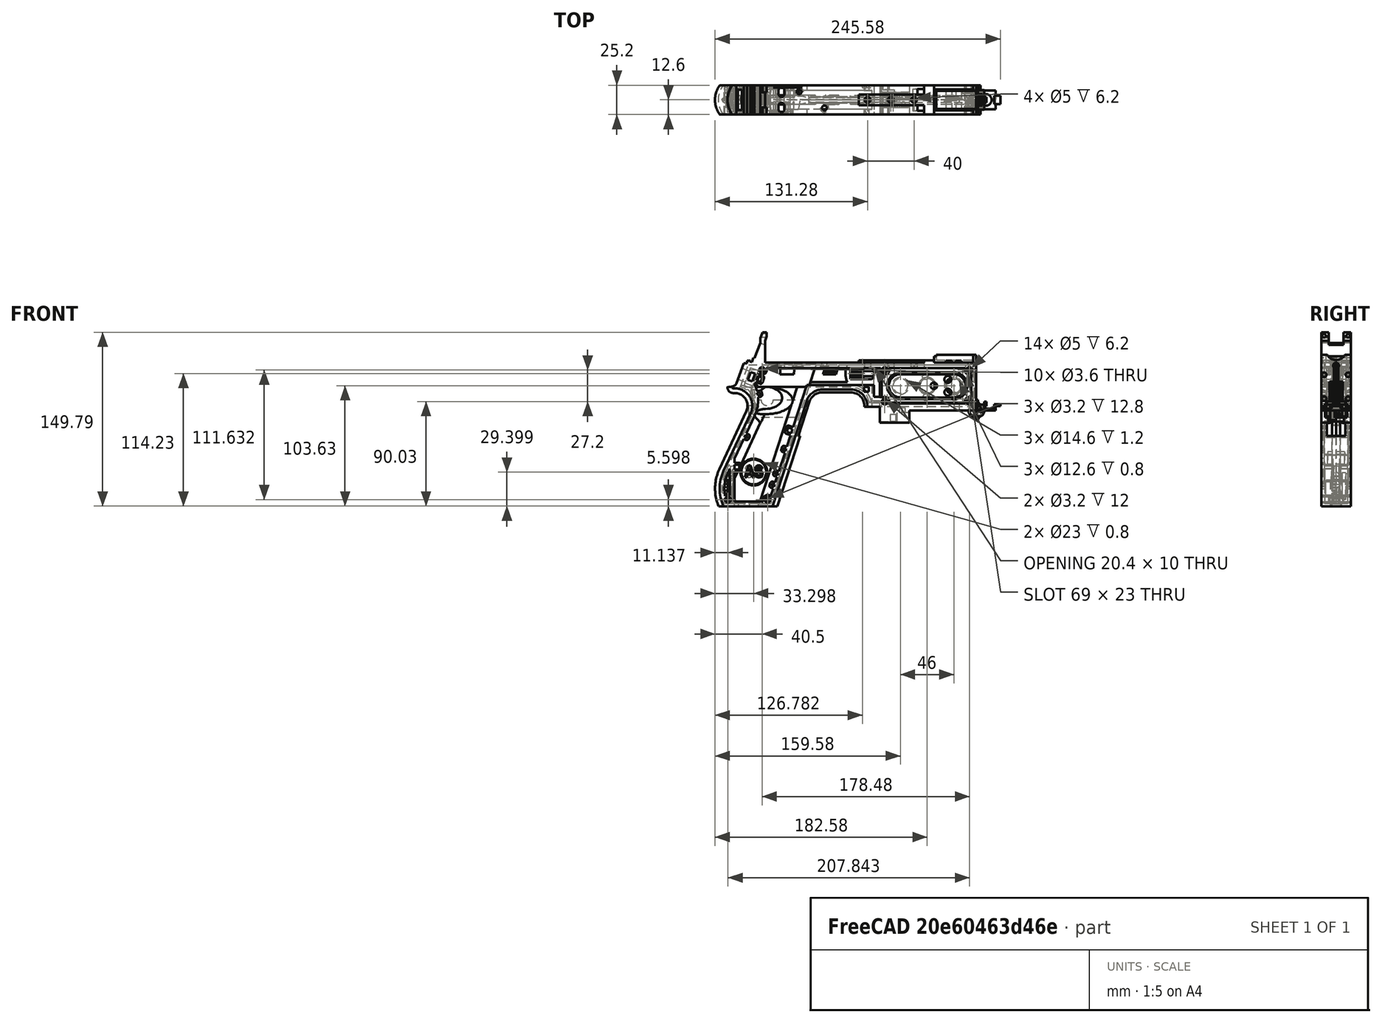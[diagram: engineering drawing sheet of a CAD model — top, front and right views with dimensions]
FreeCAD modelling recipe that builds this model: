
FCSTD DOCUMENT  (FreeCAD 1.0R39319 (Git))
Label: PICON-OF_ver_64
License: All rights reserved
LicenseURL: https://en.wikipedia.org/wiki/All_rights_reserved
objects: Sketcher::SketchObject×132, Part::Extrusion×66, Part::Cut×51, PartDesign::Pad×34, PartDesign::Pocket×21, PartDesign::Chamfer×15, PartDesign::Body×11, PartDesign::Fillet×6, Part::MultiFuse×5, Part::Part2DObjectPython×4, PartDesign::SubtractivePipe×4, PartDesign::SubtractiveLoft×4, PartDesign::Plane×3, PartDesign::SubShapeBinder×2, Part::Sweep×1, PartDesign::ShapeBinder×1, Mesh::Feature×1, PartDesign::Point×1, PartDesign::Groove×1
note: 664 computed .brp shape members not serialized (recipe doc carries the construction recipe); baked Part::Feature solids carry a one-line shape summary decoded from their .brp

FEATURE [Sketcher::SketchObject] Sketch  label="corpo principale"
  ArcFitTolerance = 1e-06
  AttacherType = Attacher::AttachEngine3D
  AttachmentSupport = -> [XZ_Plane]
  FullyConstrained = true
  MakeInternals = false
  MapMode = 5
  Placement = pos=(0,0,0) rot=(1,0,0;1.5708rad)
  sketch-geometry (65):
    g0: LineSegment StartX=0 StartY=0 StartZ=0 EndX=-57.2 EndY=0 EndZ=0
    g1: LineSegment StartX=-57.2 StartY=0 StartZ=0 EndX=-57.2 EndY=-10.4 EndZ=0
    g2: LineSegment StartX=-57.2 StartY=-10.4 StartZ=0 EndX=-82.8 EndY=-10.4 EndZ=0
    g3: LineSegment StartX=-82.8 StartY=-10.4 StartZ=0 EndX=-82.8 EndY=3.2 EndZ=0
    g4: LineSegment StartX=-82.8 StartY=3.2 StartZ=0 EndX=-93.6 EndY=3.2 EndZ=0
    g5: LineSegment StartX=-93.6 StartY=3.2 StartZ=0 EndX=-93.6 EndY=4 EndZ=0
    g6: LineSegment StartX=-107.6 StartY=18 StartZ=0 EndX=-132.428 EndY=18 EndZ=0
    g7: LineSegment StartX=-145.743 StartY=8.32624 StartZ=0 EndX=-175.232 EndY=-82.4316 EndZ=0
    g8: LineSegment StartX=-175.232 StartY=-82.4316 StartZ=0 EndX=-217.232 EndY=-82.4316 EndZ=0
    g9: LineSegment StartX=-217.232 StartY=-52.1862 StartZ=0 EndX=-193.988 EndY=-2.33927 EndZ=0
    g10: LineSegment StartX=-206.196 StartY=23.0857 StartZ=0 EndX=-199.861 EndY=40.4914 EndZ=0
    g11: LineSegment StartX=-199.861 StartY=40.4914 StartZ=0 EndX=-197.061 EndY=40.4914 EndZ=0
    g12: LineSegment StartX=-197.061 StartY=40.4914 StartZ=0 EndX=-197.061 EndY=42.8914 EndZ=0
    g13: LineSegment StartX=-197.061 StartY=42.8914 StartZ=0 EndX=-194.261 EndY=42.8914 EndZ=0
    g14: LineSegment StartX=-194.261 StartY=42.8914 StartZ=0 EndX=-194.535 EndY=42.1397 EndZ=0
    g15: LineSegment StartX=-194.535 StartY=42.1397 StartZ=0 EndX=-193.031 EndY=41.5924 EndZ=0
    g16: LineSegment StartX=-193.031 StartY=41.5924 StartZ=0 EndX=-191.663 EndY=45.3512 EndZ=0
    g17: LineSegment StartX=-191.663 StartY=45.3512 StartZ=0 EndX=-190.536 EndY=44.9408 EndZ=0
    g18: LineSegment StartX=-190.536 StartY=44.9408 StartZ=0 EndX=-185.747 EndY=58.0965 EndZ=0
    g19: LineSegment StartX=-185.747 StartY=58.0965 StartZ=0 EndX=-185.747 EndY=62.0965 EndZ=0
    g20: LineSegment StartX=-185.747 StartY=62.0965 StartZ=0 EndX=-183.832 EndY=67.3588 EndZ=0
    g21: LineSegment StartX=-183.832 StartY=67.3588 StartZ=0 EndX=-180.232 EndY=67.3588 EndZ=0
    g22: LineSegment StartX=-180.232 StartY=67.3588 StartZ=0 EndX=-180.232 EndY=63.7588 EndZ=0
    g23: LineSegment StartX=-180.232 StartY=63.7588 StartZ=0 EndX=-181.6 EndY=60 EndZ=0
    g24: LineSegment StartX=-181.6 StartY=60 StartZ=0 EndX=-181.6 EndY=41.2 EndZ=0
    g25: LineSegment StartX=-181.6 StartY=41.2 StartZ=0 EndX=-100.8 EndY=41.2 EndZ=0
    g26: LineSegment StartX=-36 StartY=43.2 StartZ=0 EndX=-36 EndY=41.2 EndZ=0
    g27: LineSegment StartX=0 StartY=48 StartZ=0 EndX=0 EndY=0 EndZ=0
    g28: LineSegment StartX=-209.901 StartY=19.85 StartZ=0 EndX=-209.901 EndY=20.1 EndZ=0
    g29: LineSegment StartX=-208.001 StartY=22 StartZ=0 EndX=-207.747 EndY=22 EndZ=0
    g30: LineSegment StartX=-207.583 StartY=19 StartZ=0 EndX=-209.051 EndY=19 EndZ=0
    g31: ArcOfCircle CenterX=-208.001 CenterY=20.1 CenterZ=0 NormalX=0 NormalY=0 NormalZ=1 AngleXU=0 Radius=1.9 StartAngle=1.5708 EndAngle=3.14159
    g32: GeomPoint [constr] X=-209.901 Y=22 Z=0
    g33: ArcOfCircle CenterX=-209.051 CenterY=19.85 CenterZ=0 NormalX=0 NormalY=0 NormalZ=1 AngleXU=0 Radius=0.85 StartAngle=3.14159 EndAngle=4.71239
    g34: GeomPoint [constr] X=-209.901 Y=19 Z=0
    g35: ArcOfCircle CenterX=-207.747 CenterY=23.65 CenterZ=0 NormalX=0 NormalY=0 NormalZ=1 AngleXU=0 Radius=1.65 StartAngle=4.71239 EndAngle=5.93412
    g36: GeomPoint [constr] X=-206.591 Y=22 Z=0
    g37: LineSegment StartX=-4 StartY=6 StartZ=0 EndX=-4 EndY=36.4 EndZ=0
    g38: LineSegment StartX=-4 StartY=36.4 StartZ=0 EndX=-185.2 EndY=36.4 EndZ=0
    g39: LineSegment StartX=-185.2 StartY=36.4 StartZ=0 EndX=-190.441 EndY=22 EndZ=0
    g40: LineSegment StartX=-214.575 StartY=-78.4316 StartZ=0 EndX=-178.142 EndY=-78.4316 EndZ=0
    g41: LineSegment StartX=-178.142 StartY=-78.4316 StartZ=0 EndX=-145.51 EndY=22 EndZ=0
    g42: LineSegment StartX=-145.51 StartY=22 StartZ=0 EndX=-87.91 EndY=22 EndZ=0
    g43: LineSegment StartX=-87.91 StartY=22 StartZ=0 EndX=-87.91 EndY=11.6 EndZ=0
    g44: LineSegment StartX=-87.91 StartY=11.6 StartZ=0 EndX=-80.11 EndY=11.6 EndZ=0
    g45: LineSegment StartX=-80.11 StartY=11.6 StartZ=0 EndX=-80.11 EndY=6 EndZ=0
    g46: LineSegment StartX=-80.11 StartY=6 StartZ=0 EndX=-4 EndY=6 EndZ=0
    g47: LineSegment StartX=-190.363 StartY=-4.02975 StartZ=0 EndX=-213.607 EndY=-53.8767 EndZ=0
    g48: ArcOfCircle CenterX=-132.428 CenterY=4 CenterZ=0 NormalX=0 NormalY=0 NormalZ=1 AngleXU=0 Radius=14 StartAngle=1.5708 EndAngle=2.82743
    g49: GeomPoint [constr] X=-142.6 Y=18 Z=0
    g50: ArcOfCircle CenterX=-107.6 CenterY=4 CenterZ=0 NormalX=0 NormalY=0 NormalZ=1 AngleXU=0 Radius=14 StartAngle=0 EndAngle=1.5708
    g51: GeomPoint [constr] X=-93.6 Y=18 Z=0
    g52: ArcOfCircle CenterX=-184.801 CenterY=-67.3089 CenterZ=0 NormalX=0 NormalY=0 NormalZ=1 AngleXU=0 Radius=35.7833 StartAngle=2.70526 EndAngle=3.57792
    g53: ArcOfCircle CenterX=-207.583 CenterY=4 CenterZ=0 NormalX=0 NormalY=0 NormalZ=1 AngleXU=0 Radius=15 StartAngle=5.84685 EndAngle=7.85398
    g54: LineSegment [constr] StartX=-213.607 StartY=-53.8767 StartZ=0 EndX=-217.232 EndY=-52.1862 EndZ=0
    g55: ArcOfCircle CenterX=-184.801 CenterY=-67.3089 CenterZ=0 NormalX=0 NormalY=0 NormalZ=1 AngleXU=0 Radius=31.7833 StartAngle=2.70526 EndAngle=3.49911
    g56: ArcOfCircle CenterX=-218.095 CenterY=8.90192 CenterZ=0 NormalX=0 NormalY=0 NormalZ=1 AngleXU=0 Radius=30.5989 StartAngle=5.84685 EndAngle=6.72553
    g57: LineSegment StartX=-44.6 StartY=43.2 StartZ=0 EndX=-36 EndY=43.2 EndZ=0
    g58: LineSegment StartX=-100.8 StartY=41.2 StartZ=0 EndX=-44.6 EndY=41.2 EndZ=0
    g59: LineSegment StartX=-44.6 StartY=41.2 StartZ=0 EndX=-44.6 EndY=43.2 EndZ=0
    g60: LineSegment StartX=-2.4 StartY=48 StartZ=0 EndX=0 EndY=48 EndZ=0
    g61: LineSegment StartX=-36 StartY=41.2 StartZ=0 EndX=-2.4 EndY=41.2 EndZ=0
    g62: LineSegment StartX=-2.4 StartY=41.2 StartZ=0 EndX=-2.4 EndY=48 EndZ=0
    g63: LineSegment [constr] StartX=-181.6 StartY=36.4 StartZ=0 EndX=-152.209 EndY=36.4 EndZ=0
    g64: LineSegment [constr] StartX=-181.6 StartY=36.4 StartZ=0 EndX=-130.41 EndY=36.4 EndZ=0
  constraints (183):
    c: Coincident(g-1,g0)
    c: PointOnObject(g0,g-1)
    c: Coincident(g0,g1)
    c: Vertical(g1)
    c: Coincident(g1,g2)
    c: Horizontal(g2)
    c: Coincident(g2,g3)
    c: Vertical(g3)
    c: Coincident(g3,g4)
    c: Coincident(g4,g5)
    c: Vertical(g5)
    c: Horizontal(g6)
    c: Coincident(g7,g8)
    c: Horizontal(g8)
    c: Coincident(g10,g11)
    c: Horizontal(g11)
    c: Coincident(g11,g12)
    c: Vertical(g12)
    c: Coincident(g12,g13)
    c: Horizontal(g13)
    c: Coincident(g13,g14)
    c: Coincident(g14,g15)
    c: Coincident(g15,g16)
    c: Coincident(g16,g17)
    c: Coincident(g17,g18)
    c: Coincident(g18,g19)
    c: Vertical(g19)
    c: Coincident(g19,g20)
    c: Coincident(g20,g21)
    c: Horizontal(g21)
    c: Coincident(g21,g22)
    c: Vertical(g22)
    c: Coincident(g22,g23)
    c: Coincident(g23,g24)
    c: Vertical(g24)
    c: Coincident(g24,g25)
    c: Horizontal(g25)
    c: Coincident(g57,g26)
    c: Vertical(g26)
    c: Coincident(g26,g61)
    c: PointOnObject(g60,g-2)
    c: Coincident(g60,g27)
    c: Coincident(g27,g0)
    c: DistanceY(g27,g27) = 48
    c: DistanceY(g1,g1) = 10.4
    c: DistanceX(g0,g0) = 57.2
    c: DistanceX(g2,g2) = 25.6
    c: Horizontal(g4)
    c: DistanceY(g3,g3) = 13.6
    c: DistanceX(g4,g4) = 10.8
    c: DistanceY(g5,g51) = 14.8
    c: DistanceX(g49,g51) = 49
    c: Distance(g7,g49) = 105.6
    c: DistanceX(g61,g60) = 36
    c: DistanceX(g25,g25) = 80.8
    c: DistanceY(g24,g24) = 18.8
    c: DistanceY(g22,g22) = 3.6
    c: Distance(g23) = 4
    c: Angle(g-1,g23) = 1.22173
    c: DistanceX(g21,g21) = 3.6
    c: Distance(g20) = 5.6
    c: Angle(g-1,g20) = 1.22173
    c: DistanceY(g19,g19) = 4
    c: Distance(g18) = 14
    c: Angle(g-1,g18) = 1.22173
    c: Distance(g17) = 1.2
    c: Distance(g16) = 4
    c: Angle(g16) = 1.22173
    c: Perpendicular(g18,g17)
    c: Distance(g15) = 1.6
    c: Perpendicular(g16,g15)
    c: Distance(g14) = 0.8
    c: DistanceX(g13,g13) = 2.8
    c: Perpendicular(g15,g14)
    c: DistanceY(g12,g12) = 2.4
    c: DistanceX(g11,g11) = 2.8
    c: Distance(g9) = 55
    c: Angle(g9,g-1) = 2.00713
    c: Horizontal(g29)
    c: Vertical(g28)
    c: Horizontal(g30)
    c: PointOnObject(g32,g29)
    c: PointOnObject(g32,g28)
    c: Tangent(g29,g31) = 1.5708
    c: Tangent(g28,g31) = 1.5708
    c: PointOnObject(g34,g28)
    c: PointOnObject(g34,g30)
    c: Tangent(g28,g33) = 1.5708
    c: Tangent(g30,g33) = 1.5708
    c: PointOnObject(g36,g29)
    c: PointOnObject(g36,g10)
    c: Tangent(g29,g35) = -1.5708
    c: Tangent(g10,g35) = -1.5708
    c: Angle(g-1,g10) = 1.22173
    c: Radius(g35) = 1.65
    c: Vertical(g37)
    c: Coincident(g37,g38)
    c: Horizontal(g38)
    c: Coincident(g38,g39)
    c: Horizontal(g40)
    c: Coincident(g40,g41)
    c: Coincident(g41,g42)
    c: Horizontal(g42)
    c: Coincident(g42,g43)
    c: Vertical(g43)
    c: Coincident(g43,g44)
    c: Horizontal(g44)
    c: Coincident(g44,g45)
    c: Vertical(g45)
    c: Coincident(g45,g46)
    c: Coincident(g46,g37)
    c: Horizontal(g46)
    c: DistanceY(g0,g37) = 6
    c: DistanceX(g37,g0) = 4
    c: DistanceY(g37,g25) = 4.8
    c: DistanceX(g38,g38) = 181.2
    c: DistanceX(g42,g42) = 57.6
    c: DistanceY(g49,g41) = 4
    c: DistanceX(g41,g49) = 2.91
    c: DistanceY(g43,g43) = 10.4
    c: DistanceX(g44,g44) = 7.8
    c: DistanceY(g7,g40) = 4
    c: Distance(g47) = 55
    c: Angle(g-1,g39) = 1.22173
    c: PointOnObject(g49,g7)
    c: PointOnObject(g49,g6)
    c: Tangent(g7,g48) = -1.5708
    c: Tangent(g6,g48) = -1.5708
    c: PointOnObject(g51,g5)
    c: PointOnObject(g51,g6)
    c: Tangent(g5,g50) = -1.5708
    c: Tangent(g6,g50) = -1.5708
    c: Radius(g50) = 14
    c: Radius(g48) = 14
    c: DistanceX(g8,g8) = 42
    c: Angle(g7,g-1) = 1.88496
    c: Parallel(g41,g7)
    c: Parallel(g47,g9)
    c: Coincident(g52,g8)
    c: Tangent(g52,g9) = 1.5708
    c: DistanceX(g9,g8) = 0
    c: Tangent(g53,g9) = -1.5708
    c: Tangent(g53,g30) = -1.5708
    c: Diameter(g53) = 30
    c: DistanceY(g53,g0) = -4
    c: Coincident(g54,g47)
    c: Distance(g54) = 4
    c: Coincident(g54,g9)
    c: Coincident(g55,g40)
    c: Tangent(g55,g47) = -1.5708
    c: Coincident(g52,g55)
    c: Coincident(g56,g39)
    c: Tangent(g56,g47) = 1.5708
    c: Horizontal(g57)
    c: DistanceX(g57,g57) = 8.6
    c: Coincident(g58,g25)
    c: Horizontal(g58)
    c: Coincident(g59,g58)
    c: Vertical(g59)
    c: DistanceY(g58,g57) = 2
    c: DistanceX(g58,g58) = 56.2
    c: Coincident(g59,g57)
    c: DistanceY(g41,g36) = 0
    c: DistanceY(g36,g39) = 0
    c: DistanceY(g28,g28) = 0.25
    c: DistanceX(g30,g36) = 2.46
    c: DistanceX(g28,g29) = 1.9
    c: Coincident(g62,g60)
    c: Horizontal(g60)
    c: DistanceX(g62,g27) = 2.4
    c: Coincident(g61,g62)
    c: DistanceY(g26,g26) = 2
    c: Vertical(g62)
    c: DistanceY(g61,g60) = 6.8
    c: Horizontal(g61)
    c: Distance(g63) = 29.391
    c: PointOnObject(g63,g38)
    c: PointOnObject(g63,g38)
    c: Distance(g64) = 51.19
    c: PointOnObject(g64,g38)
    c: PointOnObject(g64,g38)
    c: DistanceX(g24,g63) = 0
    c: DistanceX(g24,g64) = 0
FEATURE [Part::Extrusion] Extrude  label="Extrude corpo principale"
  Base = -> Sketch
  Dir = (0,-1,2e-16)
  DirMode = 2
  FaceMakerClass = Part::FaceMakerBullseye
  FaceMakerMode = 3
  LengthFwd = 25.2
  LengthRev = 12.6
  Solid = true
  Symmetric = true
FEATURE [Sketcher::SketchObject] Sketch002  label="scavo grilletto"
  ArcFitTolerance = 1e-06
  AttachmentSupport = -> [XZ_Plane]
  ExternalGeometry = -> [Sketch]
  FullyConstrained = true
  MakeInternals = false
  MapMode = 5
  Placement = pos=(0,0,0) rot=(1,0,0;1.5708rad)
  sketch-geometry (4):
    g0: LineSegment StartX=-89.51 StartY=22 StartZ=0 EndX=-152.71 EndY=22 EndZ=0
    g1: LineSegment StartX=-152.71 StartY=22 StartZ=0 EndX=-167.006 EndY=-22 EndZ=0
    g2: LineSegment StartX=-167.006 StartY=-22 StartZ=0 EndX=-89.51 EndY=-22 EndZ=0
    g3: LineSegment StartX=-89.51 StartY=-22 StartZ=0 EndX=-89.51 EndY=22 EndZ=0
  constraints (12):
    c: Horizontal(g0)
    c: Coincident(g0,g1)
    c: Coincident(g1,g2)
    c: Horizontal(g2)
    c: Coincident(g2,g3)
    c: Coincident(g3,g0)
    c: Vertical(g3)
    c: Angle(g1,g0) = 1.88496
    c: DistanceY(g3,g3) = 44
    c: DistanceX(g0,g0) = 63.2
    c: DistanceX(g0,g-3) = 1.6
    c: DistanceY(g-3,g0) = 0
FEATURE [Sketcher::SketchObject] Sketch004  label="traiettoria arrotondamento impugnatura anteriore"
  ArcFitTolerance = 1e-06
  AttachmentSupport = -> [XZ_Plane]
  ExternalGeometry = -> [Sketch]
  FullyConstrained = true
  MakeInternals = false
  MapMode = 5
  Placement = pos=(0,0,0) rot=(1,0,0;1.5708rad)
  sketch-geometry (13):
    g0: LineSegment StartX=-175.232 StartY=-82.4316 StartZ=0 EndX=-145.743 EndY=8.32624 EndZ=0
    g1: LineSegment StartX=-93.6 StartY=3.2 StartZ=0 EndX=-93.6 EndY=4 EndZ=0
    g2: LineSegment StartX=-132.428 StartY=18 StartZ=0 EndX=-107.6 EndY=18 EndZ=0
    g3: ArcOfCircle CenterX=-132.428 CenterY=4 CenterZ=0 NormalX=0 NormalY=0 NormalZ=1 AngleXU=0 Radius=14 StartAngle=1.5708 EndAngle=2.82743
    g4: ArcOfCircle CenterX=-107.6 CenterY=4 CenterZ=0 NormalX=0 NormalY=0 NormalZ=1 AngleXU=0 Radius=14 StartAngle=0 EndAngle=1.5708
    g5: LineSegment StartX=-175.232 StartY=-82.4316 StartZ=0 EndX=-217.232 EndY=-82.4316 EndZ=0
    g6: LineSegment StartX=-217.232 StartY=-52.1862 StartZ=0 EndX=-193.988 EndY=-2.33927 EndZ=0
    g7: LineSegment StartX=-209.051 StartY=19 StartZ=0 EndX=-207.583 EndY=19 EndZ=0
    g8: LineSegment StartX=-209.901 StartY=20.1 StartZ=0 EndX=-209.901 EndY=19.85 EndZ=0
    g9: ArcOfCircle CenterX=-184.801 CenterY=-67.3089 CenterZ=0 NormalX=0 NormalY=0 NormalZ=1 AngleXU=0 Radius=35.7833 StartAngle=2.70526 EndAngle=3.57792
    g10: ArcOfCircle CenterX=-207.583 CenterY=4 CenterZ=0 NormalX=0 NormalY=0 NormalZ=1 AngleXU=0 Radius=15 StartAngle=5.84685 EndAngle=7.85398
    g11: ArcOfCircle CenterX=-209.051 CenterY=19.85 CenterZ=0 NormalX=0 NormalY=0 NormalZ=1 AngleXU=0 Radius=0.85 StartAngle=3.14159 EndAngle=4.71239
    g12: ArcOfCircle CenterX=-208.001 CenterY=20.1 CenterZ=0 NormalX=0 NormalY=0 NormalZ=1 AngleXU=0 Radius=1.9 StartAngle=1.5708 EndAngle=3.14159
  constraints (26):
    c: Coincident(g0,g-3)
    c: Coincident(g0,g-6)
    c: Coincident(g1,g-8)
    c: Coincident(g1,g-7)
    c: Coincident(g2,g-5)
    c: Coincident(g2,g-4)
    c: Coincident(g3,g2)
    c: Tangent(g3,g0) = 1.5708
    c: Coincident(g4,g1)
    c: Tangent(g4,g2) = 1.5708
    c: Coincident(g5,g0)
    c: Coincident(g5,g-9)
    c: Coincident(g6,g-12)
    c: Coincident(g6,g-11)
    c: Coincident(g7,g-15)
    c: Coincident(g7,g-14)
    c: Coincident(g8,g-16)
    c: Coincident(g8,g-17)
    c: Tangent(g9,g6) = 1.5708
    c: Coincident(g9,g5)
    c: Coincident(g10,g7)
    c: Tangent(g10,g6) = -1.5708
    c: Tangent(g11,g7) = -1.5708
    c: Coincident(g11,g8)
    c: Tangent(g12,g8) = -1.5708
    c: Coincident(g12,g-17)
FEATURE [PartDesign::Plane] DatumPlane  label="Piano per disegno arrotondamento impugnatura"
  AttachmentSupport = -> [Sketch]
  Length = 73.6581
  MapMode = 7
  Placement = pos=(-145.743,1.8e-15,8.32624) rot=(0.154555,0.154555,0.97582;1.59527rad)
  ResizeMode = 0
  Width = 303.511
FEATURE [Sketcher::SketchObject] Sketch005  label="forma arrotondamento impugnatura anteriore"
  ArcFitTolerance = 1e-06
  AttachmentSupport = -> [DatumPlane]
  FullyConstrained = true
  MakeInternals = false
  MapMode = 5
  Placement = pos=(-145.743,1.8e-15,8.32624) rot=(0.154555,0.154555,0.97582;1.59527rad)
  sketch-geometry (5):
    g0: GeomPoint [constr] X=0 Y=-4 Z=0
    g1: GeomPoint [constr] X=-12.6 Y=7.1e-15 Z=0
    g2: GeomPoint [constr] X=12.6 Y=4.97e-14 Z=0
    g3: LineSegment StartX=-12.6 StartY=7.1e-15 StartZ=0 EndX=12.6 EndY=4.97e-14 EndZ=0
    g4: ArcOfCircle CenterX=-3.88e-14 CenterY=17.845 CenterZ=0 NormalX=0 NormalY=0 NormalZ=1 AngleXU=0 Radius=21.845 StartAngle=4.09759 EndAngle=5.32718
  constraints (11):
    c: DistanceY(g0,g-1) = 4
    c: DistanceX(g-1,g0) = 0
    c: DistanceX(g1,g-1) = 12.6
    c: DistanceX(g-1,g2) = 12.6
    c: DistanceY(g-1,g2) = 0
    c: DistanceY(g-1,g1) = 0
    c: Coincident(g3,g1)
    c: Coincident(g3,g2)
    c: Coincident(g4,g1)
    c: Coincident(g4,g2)
    c: PointOnObject(g0,g4)
FEATURE [Part::Sweep] Sweep  label="Sweep impugnatura"
  Frenet = true
  Sections = -> [Sketch005]
  Solid = true
  Spine = -> Sketch [Edge32,Edge33,Edge34,Edge35,Edge36,Edge37,Edge38,Edge39,Edge40,Edge41,Edge42,Edge43,Edge44]
  Transition = 1
FEATURE [Sketcher::SketchObject] Sketch008  label="buchi e pulizie varie"
  ArcFitTolerance = 1e-06
  AttachmentSupport = -> [XZ_Plane]
  ExternalGeometry = -> [Sketch]
  FullyConstrained = true
  MakeInternals = false
  MapMode = 5
  Placement = pos=(0,0,0) rot=(1,0,0;1.5708rad)
  sketch-geometry (26):
    g0: LineSegment StartX=-96.278 StartY=20.155 StartZ=0 EndX=-92.278 EndY=20.155 EndZ=0
    g1: LineSegment StartX=-92.278 StartY=20.155 StartZ=0 EndX=-92.278 EndY=16.155 EndZ=0
    g2: LineSegment StartX=-92.278 StartY=16.155 StartZ=0 EndX=-96.278 EndY=16.155 EndZ=0
    g3: LineSegment StartX=-96.278 StartY=16.155 StartZ=0 EndX=-96.278 EndY=20.155 EndZ=0
    g4: LineSegment StartX=-222.232 StartY=-82.4316 StartZ=0 EndX=-170.232 EndY=-82.4316 EndZ=0
    g5: LineSegment StartX=-170.232 StartY=-82.4316 StartZ=0 EndX=-170.232 EndY=-86.4316 EndZ=0
    g6: LineSegment StartX=-170.232 StartY=-86.4316 StartZ=0 EndX=-222.232 EndY=-86.4316 EndZ=0
    g7: LineSegment StartX=-222.232 StartY=-86.4316 StartZ=0 EndX=-222.232 EndY=-82.4316 EndZ=0
    g8: LineSegment StartX=-213.901 StartY=20.1 StartZ=0 EndX=-213.901 EndY=26 EndZ=0
    g9: LineSegment StartX=-213.901 StartY=26 StartZ=0 EndX=-206.196 EndY=26 EndZ=0
    g10: LineSegment StartX=-17.4 StartY=42.8 StartZ=0 EndX=-12.4 EndY=42.8 EndZ=0
    g11: LineSegment StartX=-12.4 StartY=42.8 StartZ=0 EndX=-12.4 EndY=41.2 EndZ=0
    g12: LineSegment StartX=-12.4 StartY=41.2 StartZ=0 EndX=-17.4 EndY=41.2 EndZ=0
    g13: LineSegment StartX=-17.4 StartY=41.2 StartZ=0 EndX=-17.4 EndY=42.8 EndZ=0
    g14: LineSegment StartX=-25.9 StartY=42.8 StartZ=0 EndX=-20.9 EndY=42.8 EndZ=0
    g15: LineSegment StartX=-20.9 StartY=42.8 StartZ=0 EndX=-20.9 EndY=41.2 EndZ=0
    g16: LineSegment StartX=-20.9 StartY=41.2 StartZ=0 EndX=-25.9 EndY=41.2 EndZ=0
    g17: LineSegment StartX=-25.9 StartY=41.2 StartZ=0 EndX=-25.9 EndY=42.8 EndZ=0
    g18: GeomPoint [constr] X=-206.196 Y=23.0857 Z=0
    g19: GeomPoint [constr] X=-213.901 Y=20.1 Z=0
    g20: BSplineCurve PolesCount=4 KnotsCount=2 Degree=3 IsPeriodic=0
    g21-g24: Circle [constr] x4 (B-spline internal-alignment scaffolding for g20; pole/knot coordinates omitted)
    g25: LineSegment StartX=-206.196 StartY=26 StartZ=0 EndX=-206.196 EndY=23.0857 EndZ=0
  constraints (73):
    c: Horizontal(g0)
    c: Coincident(g1,g0)
    c: Vertical(g1)
    c: Coincident(g2,g1)
    c: Horizontal(g2)
    c: Coincident(g3,g2)
    c: Coincident(g3,g0)
    c: Vertical(g3)
    c: DistanceX(g0,g-4) = 4.368
    c: DistanceY(g0,g-4) = 1.845
    c: DistanceY(g1,g1) = 4
    c: DistanceX(g2,g2) = 4
    c: Horizontal(g4)
    c: Coincident(g5,g4)
    c: Vertical(g5)
    c: Coincident(g6,g5)
    c: Horizontal(g6)
    c: Coincident(g7,g6)
    c: Coincident(g7,g4)
    c: Vertical(g7)
    c: DistanceY(g7,g7) = 4
    c: DistanceX(g4,g-5) = 5
    c: DistanceX(g-5,g4) = 5
    c: DistanceY(g4,g-5) = 0
    c: Coincident(g9,g8)
    c: Parallel(g9,g-6)
    c: DistanceX(g8,g-8) = 4
    c: Horizontal(g10)
    c: Coincident(g11,g10)
    c: Vertical(g11)
    c: Coincident(g12,g11)
    c: Horizontal(g12)
    c: Coincident(g13,g12)
    c: Coincident(g13,g10)
    c: Vertical(g13)
    c: Horizontal(g14)
    c: Coincident(g15,g14)
    c: Vertical(g15)
    c: Coincident(g16,g15)
    c: Horizontal(g16)
    c: Coincident(g17,g16)
    c: Coincident(g17,g14)
    c: Vertical(g17)
    c: DistanceY(g11,g10) = 1.6
    c: DistanceX(g10,g10) = 5
    c: DistanceY(g15,g14) = 1.6
    c: DistanceX(g14,g14) = 5
    c: DistanceX(g15,g12) = 3.5
    c: DistanceX(g11,g-9) = 10
    c: DistanceY(g-9,g11) = 0
    c: DistanceY(g-9,g15) = 0
    c: Perpendicular(g8,g9)
    c: DistanceY(g-7,g9) = 4
    c: DistanceY(g8,g-8) = 0
    c: InternalAlignment(g18,g20)
    c: InternalAlignment(g19,g20)
    c: InternalAlignment(g21,g20)
    c: Weight(g21) = 1
    c: InternalAlignment(g22,g20)
    c: Equal(g22,g21)
    c: InternalAlignment(g23,g20)
    c: Equal(g23,g21)
    c: InternalAlignment(g24,g20)
    c: Equal(g24,g21)
    c: Coincident(g18,g-12)
    c: Coincident(g19,g8)
    c: Coincident(g25,g9)
    c: Coincident(g25,g20)
    c: Vertical(g25)
    c: DistanceY(g20,g23) = 0
    c: DistanceY(g22,g18) = 2.26
    c: DistanceX(g22,g18) = 0.93
    c: DistanceX(g20,g23) = 2.9
FEATURE [Part::Extrusion] Extrude004  label="Extrude Buchi e pulizie varie"
  Base = -> Sketch008
  Dir = (0,-1,2e-16)
  DirMode = 2
  FaceMakerClass = Part::FaceMakerBullseye
  FaceMakerMode = 3
  LengthFwd = 25.2
  LengthRev = 0
  Solid = true
  Symmetric = true
FEATURE [Sketcher::SketchObject] Sketch009  label="rinforzi"
  ArcFitTolerance = 1e-06
  AttachmentSupport = -> [XZ_Plane]
  ExternalGeometry = -> [Sketch]
  FullyConstrained = true
  MakeInternals = false
  MapMode = 5
  Placement = pos=(0,0,0) rot=(1,0,0;1.5708rad)
  sketch-geometry (9):
    g0: LineSegment StartX=-87.91 StartY=22 StartZ=0 EndX=-87.91 EndY=36.4 EndZ=0
    g1: LineSegment StartX=-87.91 StartY=36.4 StartZ=0 EndX=-97.91 EndY=36.4 EndZ=0
    g2: LineSegment StartX=-97.91 StartY=36.4 StartZ=0 EndX=-97.91 EndY=22 EndZ=0
    g3: LineSegment StartX=-97.91 StartY=22 StartZ=0 EndX=-87.91 EndY=22 EndZ=0
    g4: LineSegment StartX=-149.713 StartY=9.06563 StartZ=0 EndX=-154.586 EndY=-5.93437 EndZ=0
    g5: LineSegment StartX=-154.586 StartY=-5.93437 StartZ=0 EndX=-191.863 EndY=-5.93437 EndZ=0
    g6: LineSegment StartX=-191.863 StartY=-5.93437 StartZ=0 EndX=-191.863 EndY=9.06563 EndZ=0
    g7: LineSegment StartX=-191.863 StartY=9.06563 StartZ=0 EndX=-149.713 EndY=9.06563 EndZ=0
    g8: LineSegment [constr] StartX=-145.51 StartY=22 StartZ=0 EndX=-149.713 EndY=9.06563 EndZ=0
  constraints (25):
    c: Vertical(g0)
    c: Coincident(g1,g0)
    c: Horizontal(g1)
    c: Coincident(g2,g1)
    c: Vertical(g2)
    c: Coincident(g3,g2)
    c: Coincident(g3,g0)
    c: Horizontal(g3)
    c: Coincident(g0,g-4)
    c: DistanceX(g3,g3) = 10
    c: DistanceY(g0,g-3) = 0
    c: Coincident(g5,g4)
    c: Horizontal(g5)
    c: Coincident(g6,g5)
    c: Vertical(g6)
    c: Coincident(g7,g6)
    c: Coincident(g7,g4)
    c: Horizontal(g7)
    c: Distance(g8) = 13.6
    c: Parallel(g-6,g8)
    c: Coincident(g-6,g8)
    c: Parallel(g4,g-6)
    c: DistanceY(g4,g4) = 15
    c: Coincident(g4,g8)
    c: DistanceX(g-5,g5) = -1.5
FEATURE [Part::Extrusion] Extrude001  label="Extrude scavo grilletto"
  Base = -> Sketch002
  Dir = (0,-1,2e-16)
  DirMode = 2
  FaceMakerClass = Part::FaceMakerBullseye
  FaceMakerMode = 3
  LengthFwd = 16
  LengthRev = 0
  Solid = true
  Symmetric = true
FEATURE [Part::Extrusion] Extrude005  label="Extrude Rinforzi"
  Base = -> Sketch009
  Dir = (0,-1,2e-16)
  DirMode = 2
  FaceMakerClass = Part::FaceMakerBullseye
  FaceMakerMode = 3
  LengthFwd = 2
  LengthRev = 0
  Placement = pos=(0,12.6,0) rot=(0,0,1;0rad)
  Solid = true
  Symmetric = false
FEATURE [PartDesign::ShapeBinder] CopyCut
  TraceSupport = false
FEATURE [PartDesign::Plane] DatumPlane001
  AttachmentSupport = -> [CopyCut]
  Length = 283.944
  MapMode = 5
  Placement = pos=(0,12.6,0) rot=(0,0.707107,0.707107;3.14159rad)
  ResizeMode = 0
  Width = 188.15
FEATURE [Sketcher::SketchObject] Sketch010  label="buco neopixel"
  ArcFitTolerance = 1e-06
  AttachmentSupport = -> [XZ_Plane]
  ExternalGeometry = -> [Sketch]
  FullyConstrained = true
  MakeInternals = false
  MapMode = 5
  Placement = pos=(0,0,0) rot=(1,0,0;1.5708rad)
  sketch-geometry (5):
    g0: LineSegment [constr] StartX=-199.861 StartY=40.4914 StartZ=0 EndX=-201.368 EndY=36.3521 EndZ=0
    g1: LineSegment StartX=-201.368 StartY=36.3521 StartZ=0 EndX=-204.932 EndY=26.5605 EndZ=0
    g2: LineSegment StartX=-201.368 StartY=36.3521 StartZ=0 EndX=-180.2 EndY=28.6477 EndZ=0
    g3: LineSegment StartX=-180.2 StartY=28.6477 StartZ=0 EndX=-183.764 EndY=18.8561 EndZ=0
    g4: LineSegment StartX=-183.764 StartY=18.8561 StartZ=0 EndX=-204.932 EndY=26.5605 EndZ=0
  constraints (14):
    c: Parallel(g0,g-3)
    c: Distance(g0) = 4.405
    c: Coincident(g0,g-3)
    c: Coincident(g2,g1)
    c: Coincident(g3,g2)
    c: Coincident(g4,g3)
    c: Coincident(g4,g1)
    c: Parallel(g1,g-3)
    c: Distance(g1) = 10.42
    c: Coincident(g1,g0)
    c: Parallel(g2,g4)
    c: Perpendicular(g1,g2)
    c: DistanceX(g-4,g2) = 5
    c: Parallel(g3,g1)
FEATURE [Part::Extrusion] Extrude006  label="Extrude buco neopixel"
  Base = -> Sketch010
  Dir = (0,-1,2e-16)
  DirMode = 2
  FaceMakerClass = Part::FaceMakerBullseye
  FaceMakerMode = 3
  LengthFwd = 17.2
  LengthRev = 0
  Solid = true
  Symmetric = true
FEATURE [Sketcher::SketchObject] Sketch011  label="fermo grilletto"
  ArcFitTolerance = 1e-06
  AttachmentSupport = -> [XZ_Plane]
  ExternalGeometry = -> [Sketch]
  FullyConstrained = true
  MakeInternals = false
  MapMode = 5
  Placement = pos=(0,0,0) rot=(1,0,0;1.5708rad)
  sketch-geometry (18):
    g0: LineSegment [constr] StartX=-145.51 StartY=22 StartZ=0 EndX=-157.347 EndY=-14.4293 EndZ=0
    g1: LineSegment [constr] StartX=-157.347 StartY=-14.4293 StartZ=0 EndX=-157.841 EndY=-15.951 EndZ=0
    g2: LineSegment StartX=-161.151 StartY=-13.1932 StartZ=0 EndX=-155.825 EndY=-14.9237 EndZ=0
    g3: LineSegment StartX=-163.167 StartY=-14.2205 StartZ=0 EndX=-164.403 EndY=-18.0247 EndZ=0
    g4: LineSegment StartX=-163.376 StartY=-20.0408 StartZ=0 EndX=-158.05 EndY=-21.7713 EndZ=0
    g5: LineSegment StartX=-158.05 StartY=-21.7713 StartZ=0 EndX=-155.825 EndY=-14.9237 EndZ=0
    g6: LineSegment StartX=-161.645 StartY=-14.7149 StartZ=0 EndX=-157.841 EndY=-15.951 EndZ=0
    g7: LineSegment StartX=-157.841 StartY=-15.951 StartZ=0 EndX=-159.077 EndY=-19.7552 EndZ=0
    g8: LineSegment StartX=-159.077 StartY=-19.7552 StartZ=0 EndX=-162.881 EndY=-18.5191 EndZ=0
    g9: LineSegment StartX=-162.881 StartY=-18.5191 StartZ=0 EndX=-161.645 EndY=-14.7149 EndZ=0
    g10: LineSegment [constr] StartX=-161.645 StartY=-14.7149 StartZ=0 EndX=-161.151 EndY=-13.1932 EndZ=0
    g11: LineSegment [constr] StartX=-159.077 StartY=-19.7552 StartZ=0 EndX=-157.555 EndY=-20.2496 EndZ=0
    g12: LineSegment [constr] StartX=-159.077 StartY=-19.7552 StartZ=0 EndX=-159.572 EndY=-21.2769 EndZ=0
    g13: LineSegment [constr] StartX=-161.645 StartY=-14.7149 StartZ=0 EndX=-163.167 EndY=-14.2205 EndZ=0
    g14: ArcOfCircle CenterX=-161.645 CenterY=-14.7149 CenterZ=0 NormalX=0 NormalY=0 NormalZ=1 AngleXU=0 Radius=1.6 StartAngle=1.25664 EndAngle=2.82743
    g15: GeomPoint [constr] X=-162.673 Y=-12.6988 Z=0
    g16: ArcOfCircle CenterX=-162.881 CenterY=-18.5191 CenterZ=0 NormalX=0 NormalY=0 NormalZ=1 AngleXU=0 Radius=1.6 StartAngle=2.82743 EndAngle=4.39823
    g17: GeomPoint [constr] X=-164.897 Y=-19.5464 Z=0
  constraints (48):
    c: Parallel(g0,g-3)
    c: Distance(g0) = 38.304
    c: Coincident(g0,g-3)
    c: Parallel(g1,g-3)
    c: Distance(g1) = 1.6
    c: Coincident(g1,g0)
    c: Coincident(g5,g4)
    c: Coincident(g5,g2)
    c: Coincident(g7,g6)
    c: Coincident(g8,g7)
    c: Coincident(g9,g8)
    c: Coincident(g9,g6)
    c: Parallel(g7,g-3)
    c: Parallel(g9,g7)
    c: Perpendicular(g6,g7)
    c: Parallel(g6,g8)
    c: Distance(g6) = 4
    c: Distance(g9) = 4
    c: Parallel(g5,g7)
    c: Parallel(g9,g3)
    c: Parallel(g2,g6)
    c: Parallel(g4,g8)
    c: Parallel(g13,g6)
    c: Parallel(g10,g9)
    c: Parallel(g11,g8)
    c: Parallel(g12,g7)
    c: Distance(g10) = 1.6
    c: Distance(g13) = 1.6
    c: Distance(g12) = 1.6
    c: Distance(g11) = 1.6
    c: Coincident(g10,g6)
    c: Coincident(g13,g6)
    c: Coincident(g12,g7)
    c: Coincident(g11,g7)
    c: Distance(g10,g15) = 1.6
    c: Distance(g15,g13) = 1.6
    c: Distance(g4,g12) = 1.6
    c: Distance(g4,g11) = 1.6
    c: PointOnObject(g15,g2)
    c: Tangent(g3,g14) = -1.5708
    c: Tangent(g2,g14) = 1.5708
    c: PointOnObject(g17,g4)
    c: PointOnObject(g17,g3)
    c: Tangent(g4,g16) = -1.5708
    c: Tangent(g3,g16) = -1.5708
    c: Equal(g16,g14)
    c: Coincident(g16,g8)
    c: Coincident(g6,g1)
FEATURE [Part::Extrusion] Extrude007  label="Extrude fermo grilletto"
  Base = -> Sketch011
  Dir = (0,-1,2e-16)
  DirMode = 2
  FaceMakerClass = Part::FaceMakerBullseye
  FaceMakerMode = 3
  LengthFwd = 25.2
  LengthRev = 0
  Solid = true
  Symmetric = true
FEATURE [Sketcher::SketchObject] Sketch012  label="buco oled"
  ArcFitTolerance = 1e-06
  AttachmentSupport = -> [XZ_Plane]
  ExternalGeometry = -> [Sketch]
  FullyConstrained = true
  MakeInternals = false
  MapMode = 5
  Placement = pos=(0,0,0) rot=(1,0,0;1.5708rad)
  sketch-geometry (4):
    g0: LineSegment StartX=-185.747 StartY=58.0965 StartZ=0 EndX=-180.232 EndY=56.0891 EndZ=0
    g1: LineSegment StartX=-185.747 StartY=58.0965 StartZ=0 EndX=-185.747 EndY=67.3588 EndZ=0
    g2: LineSegment StartX=-185.747 StartY=67.3588 StartZ=0 EndX=-180.232 EndY=67.3588 EndZ=0
    g3: LineSegment StartX=-180.232 StartY=67.3588 StartZ=0 EndX=-180.232 EndY=56.0891 EndZ=0
  constraints (10):
    c: Coincident(g1,g0)
    c: Coincident(g2,g1)
    c: Coincident(g3,g2)
    c: Coincident(g3,g0)
    c: Parallel(g1,g-5)
    c: Perpendicular(g-3,g0)
    c: Parallel(g2,g-6)
    c: Parallel(g3,g-4)
    c: Coincident(g0,g-5)
    c: Coincident(g2,g-6)
FEATURE [Part::Extrusion] Extrude008  label="Extrude buco oled"
  Base = -> Sketch012
  Dir = (0,-1,2e-16)
  DirMode = 2
  FaceMakerClass = Part::FaceMakerBullseye
  FaceMakerMode = 3
  LengthFwd = 12.8
  LengthRev = 0
  Solid = true
  Symmetric = true
FEATURE [Sketcher::SketchObject] Sketch013  label="buco pompa"
  ArcFitTolerance = 1e-06
  AttachmentSupport = -> [XZ_Plane]
  ExternalGeometry = -> [Sketch]
  FullyConstrained = true
  MakeInternals = false
  MapMode = 5
  Placement = pos=(0,0,0) rot=(1,0,0;1.5708rad)
  sketch-geometry (8):
    g0: LineSegment StartX=-82.8 StartY=-10.4 StartZ=0 EndX=-82.8 EndY=-9.6 EndZ=0
    g1: LineSegment StartX=-82.8 StartY=-9.6 StartZ=0 EndX=-67.9 EndY=-9.6 EndZ=0
    g2: LineSegment StartX=-67.9 StartY=-9.6 StartZ=0 EndX=-67.9 EndY=6 EndZ=0
    g3: LineSegment StartX=-67.9 StartY=6 StartZ=0 EndX=-65.9 EndY=6 EndZ=0
    g4: LineSegment StartX=-65.9 StartY=6 StartZ=0 EndX=-65.9 EndY=-1.7 EndZ=0
    g5: LineSegment StartX=-65.9 StartY=-1.7 StartZ=0 EndX=-57.2 EndY=-1.7 EndZ=0
    g6: LineSegment StartX=-57.2 StartY=-1.7 StartZ=0 EndX=-57.2 EndY=-10.4 EndZ=0
    g7: LineSegment StartX=-57.2 StartY=-10.4 StartZ=0 EndX=-82.8 EndY=-10.4 EndZ=0
  constraints (22):
    c: Vertical(g0)
    c: Coincident(g1,g0)
    c: Horizontal(g1)
    c: Coincident(g2,g1)
    c: Vertical(g2)
    c: Coincident(g3,g2)
    c: Horizontal(g3)
    c: Coincident(g4,g3)
    c: Vertical(g4)
    c: Coincident(g5,g4)
    c: Horizontal(g5)
    c: Coincident(g6,g5)
    c: Vertical(g6)
    c: Coincident(g7,g6)
    c: Coincident(g7,g0)
    c: DistanceY(g0,g0) = 0.8
    c: DistanceY(g6,g6) = 8.7
    c: DistanceX(g1,g1) = 14.9
    c: DistanceX(g3,g3) = 2
    c: Coincident(g0,g-4)
    c: DistanceY(g2,g-6) = 0
    c: Coincident(g6,g-5)
FEATURE [Part::Extrusion] Extrude009  label="Extrude buco pompa"
  Base = -> Sketch013
  Dir = (0,-1,2e-16)
  DirMode = 2
  FaceMakerClass = Part::FaceMakerBullseye
  FaceMakerMode = 3
  LengthFwd = 13.2
  LengthRev = 0
  Solid = true
  Symmetric = true
FEATURE [Sketcher::SketchObject] Sketch014  label="buco frontale"
  ArcFitTolerance = 1e-06
  AttachmentSupport = -> [XZ_Plane]
  ExternalGeometry = -> [Sketch]
  FullyConstrained = true
  MakeInternals = false
  MapMode = 5
  Placement = pos=(0,0,0) rot=(1,0,0;1.5708rad)
  sketch-geometry (10):
    g0: LineSegment StartX=0 StartY=0 StartZ=0 EndX=0 EndY=24.671 EndZ=0
    g1: LineSegment StartX=0 StartY=24.671 StartZ=0 EndX=-4 EndY=24.671 EndZ=0
    g2: LineSegment StartX=-4 StartY=24.671 StartZ=0 EndX=-4 EndY=16 EndZ=0
    g3: LineSegment StartX=-4 StartY=16 StartZ=0 EndX=-2.4 EndY=16 EndZ=0
    g4: LineSegment StartX=-2.4 StartY=16 StartZ=0 EndX=-2.4 EndY=10 EndZ=0
    g5: LineSegment StartX=-2.4 StartY=10 StartZ=0 EndX=-12 EndY=10 EndZ=0
    g6: LineSegment StartX=-12 StartY=10 StartZ=0 EndX=-12 EndY=6 EndZ=0
    g7: LineSegment StartX=-12 StartY=6 StartZ=0 EndX=-2.4 EndY=6 EndZ=0
    g8: LineSegment StartX=-2.4 StartY=6 StartZ=0 EndX=-2.4 EndY=0 EndZ=0
    g9: LineSegment StartX=-2.4 StartY=0 StartZ=0 EndX=0 EndY=0 EndZ=0
  constraints (29):
    c: Vertical(g0)
    c: Coincident(g1,g0)
    c: Horizontal(g1)
    c: Coincident(g2,g1)
    c: Vertical(g2)
    c: Coincident(g3,g2)
    c: Horizontal(g3)
    c: Coincident(g4,g3)
    c: Vertical(g4)
    c: Coincident(g5,g4)
    c: Horizontal(g5)
    c: Coincident(g6,g5)
    c: Vertical(g6)
    c: Coincident(g7,g6)
    c: Coincident(g8,g7)
    c: Vertical(g8)
    c: Coincident(g9,g8)
    c: Coincident(g9,g0)
    c: Horizontal(g9)
    c: DistanceY(g0,g0) = 24.671
    c: Horizontal(g7)
    c: DistanceY(g6,g6) = 4
    c: DistanceY(g4,g4) = 6
    c: DistanceX(g9,g9) = 2.4
    c: Coincident(g0,g-1)
    c: DistanceY(g-3,g7) = 0
    c: DistanceX(g8,g4) = 0
    c: DistanceX(g-3,g1) = 0
    c: DistanceX(g6,g-3) = 8
FEATURE [Part::Extrusion] Extrude010  label="Extrude buco frontale"
  Base = -> Sketch014
  Dir = (0,-1,2e-16)
  DirMode = 2
  FaceMakerClass = Part::FaceMakerBullseye
  FaceMakerMode = 3
  LengthFwd = 11.2
  LengthRev = 0
  Solid = true
  Symmetric = true
FEATURE [Sketcher::SketchObject] Sketch015  label="guida rail"
  ArcFitTolerance = 1e-06
  AttachmentSupport = -> [XZ_Plane]
  ExternalGeometry = -> [Sketch]
  FullyConstrained = true
  MakeInternals = false
  MapMode = 5
  Placement = pos=(0,0,0) rot=(1,0,0;1.5708rad)
  sketch-geometry (4):
    g0: LineSegment StartX=-100.8 StartY=43.2 StartZ=0 EndX=-44.6 EndY=43.2 EndZ=0
    g1: LineSegment StartX=-44.6 StartY=43.2 StartZ=0 EndX=-44.6 EndY=41.2 EndZ=0
    g2: LineSegment StartX=-44.6 StartY=41.2 StartZ=0 EndX=-100.8 EndY=41.2 EndZ=0
    g3: LineSegment StartX=-100.8 StartY=41.2 StartZ=0 EndX=-100.8 EndY=43.2 EndZ=0
  constraints (9):
    c: Horizontal(g0)
    c: Coincident(g1,g0)
    c: Coincident(g2,g1)
    c: Coincident(g3,g2)
    c: Coincident(g3,g0)
    c: Vertical(g3)
    c: Coincident(g2,g-3)
    c: Coincident(g1,g-3)
    c: Coincident(g0,g-4)
FEATURE [Part::Extrusion] Extrude011  label="Extrude guida rail"
  Base = -> Sketch015
  Dir = (0,-1,2e-16)
  DirMode = 2
  FaceMakerClass = Part::FaceMakerBullseye
  FaceMakerMode = 3
  LengthFwd = 9
  LengthRev = 0
  Solid = true
  Symmetric = true
FEATURE [Sketcher::SketchObject] Sketch016  label="guide per coperture laterali"
  ArcFitTolerance = 1e-06
  AttachmentSupport = -> [XZ_Plane]
  ExternalGeometry = -> [Sketch]
  FullyConstrained = true
  MakeInternals = false
  MapMode = 5
  Placement = pos=(0,0,0) rot=(1,0,0;1.5708rad)
  sketch-geometry (14):
    g0: Circle CenterX=-5.6 CenterY=7.6 CenterZ=0 NormalX=0 NormalY=0 NormalZ=1 AngleXU=0 Radius=1.6
    g1: Circle CenterX=-5.6 CenterY=7.6 CenterZ=0 NormalX=0 NormalY=0 NormalZ=1 AngleXU=0 Radius=4
    g2: Circle CenterX=-5.6 CenterY=34.8 CenterZ=0 NormalX=0 NormalY=0 NormalZ=1 AngleXU=0 Radius=1.6
    g3: Circle CenterX=-5.6 CenterY=34.8 CenterZ=0 NormalX=0 NormalY=0 NormalZ=1 AngleXU=0 Radius=4
    g4: Circle CenterX=-184.08 CenterY=34.8 CenterZ=0 NormalX=0 NormalY=0 NormalZ=1 AngleXU=0 Radius=1.6
    g5: Circle CenterX=-184.08 CenterY=34.8 CenterZ=0 NormalX=0 NormalY=0 NormalZ=1 AngleXU=0 Radius=4
    g6: Circle CenterX=-179.305 CenterY=-76.8316 CenterZ=0 NormalX=0 NormalY=0 NormalZ=1 AngleXU=0 Radius=1.6
    g7: Circle CenterX=-179.305 CenterY=-76.8316 CenterZ=0 NormalX=0 NormalY=0 NormalZ=1 AngleXU=0 Radius=4
    g8: Circle CenterX=-213.443 CenterY=-76.8316 CenterZ=0 NormalX=0 NormalY=0 NormalZ=1 AngleXU=0 Radius=1.6
    g9: Circle CenterX=-213.443 CenterY=-76.8316 CenterZ=0 NormalX=0 NormalY=0 NormalZ=1 AngleXU=0 Radius=4
    g10: Circle CenterX=-78.51 CenterY=7.6 CenterZ=0 NormalX=0 NormalY=0 NormalZ=1 AngleXU=0 Radius=1.6
    g11: Circle CenterX=-78.51 CenterY=7.6 CenterZ=0 NormalX=0 NormalY=0 NormalZ=1 AngleXU=0 Radius=4
    g12: Circle CenterX=-78.51 CenterY=34.8 CenterZ=0 NormalX=0 NormalY=0 NormalZ=1 AngleXU=0 Radius=1.6
    g13: Circle CenterX=-78.51 CenterY=34.8 CenterZ=0 NormalX=0 NormalY=0 NormalZ=1 AngleXU=0 Radius=4
  constraints (35):
    c: Diameter(g0) = 3.2
    c: Diameter(g1) = 8
    c: Coincident(g0,g1)
    c: Diameter(g2) = 3.2
    c: Diameter(g3) = 8
    c: Coincident(g3,g2)
    c: Tangent(g2,g-7)
    c: Diameter(g4) = 3.2
    c: Diameter(g5) = 8
    c: Coincident(g5,g4)
    c: Tangent(g4,g-7)
    c: Tangent(g4,g-8)
    c: Diameter(g6) = 3.2
    c: Diameter(g7) = 8
    c: Coincident(g7,g6)
    c: Tangent(g6,g-9)
    c: Tangent(g6,g-10)
    c: Diameter(g8) = 3.2
    c: Diameter(g9) = 8
    c: Coincident(g9,g8)
    c: Tangent(g8,g-10)
    c: Tangent(g8,g-11)
    c: Diameter(g10) = 3.2
    c: Diameter(g11) = 8
    c: Diameter(g12) = 3.2
    c: Diameter(g13) = 8
    c: Coincident(g12,g13)
    c: Coincident(g10,g11)
    c: Tangent(g12,g-7)
    c: DistanceX(g12,g10) = 0
    c: Tangent(g2,g-6)
    c: Tangent(g0,g-6)
    c: Tangent(g0,g-3)
    c: Tangent(g10,g-3)
    c: Tangent(g10,g-4)
FEATURE [Part::Extrusion] Extrude012  label="extrude guide per coperture laterali"
  Base = -> Sketch016
  Dir = (0,-1,2e-16)
  DirMode = 2
  FaceMakerClass = Part::FaceMakerBullseye
  FaceMakerMode = 3
  LengthFwd = 25.2
  LengthRev = 0
  Solid = true
  Symmetric = true
FEATURE [Sketcher::SketchObject] Sketch017  label="supporto CAM"
  ArcFitTolerance = 1e-06
  AttachmentSupport = -> [XZ_Plane]
  ExternalGeometry = -> [Sketch]
  FullyConstrained = true
  MakeInternals = false
  MapMode = 5
  Placement = pos=(0,0,0) rot=(1,0,0;1.5708rad)
  sketch-geometry (6):
    g0: LineSegment StartX=-2.4 StartY=48 StartZ=0 EndX=-2.4 EndY=41.2 EndZ=0
    g1: LineSegment StartX=-2.4 StartY=48 StartZ=0 EndX=-34 EndY=48 EndZ=0
    g2: LineSegment StartX=-34 StartY=48 StartZ=0 EndX=-34 EndY=46.72 EndZ=0
    g3: LineSegment StartX=-34 StartY=46.72 StartZ=0 EndX=-36 EndY=46.72 EndZ=0
    g4: LineSegment StartX=-36 StartY=46.72 StartZ=0 EndX=-36 EndY=41.2 EndZ=0
    g5: LineSegment StartX=-36 StartY=41.2 StartZ=0 EndX=-2.4 EndY=41.2 EndZ=0
  constraints (15):
    c: Coincident(g1,g0)
    c: Horizontal(g1)
    c: Coincident(g2,g1)
    c: Vertical(g2)
    c: Coincident(g3,g2)
    c: Horizontal(g3)
    c: Coincident(g4,g3)
    c: Coincident(g5,g4)
    c: DistanceX(g1,g0) = 31.6
    c: Coincident(g5,g0)
    c: Vertical(g4)
    c: DistanceY(g2,g1) = 1.28
    c: Coincident(g0,g-3)
    c: Coincident(g0,g-3)
    c: Coincident(g4,g-4)
FEATURE [Part::Extrusion] Extrude013  label="Extrude supporto CAM"
  Base = -> Sketch017
  Dir = (0,-1,2e-16)
  DirMode = 2
  FaceMakerClass = Part::FaceMakerBullseye
  FaceMakerMode = 3
  LengthFwd = 17.8
  LengthRev = 0
  Solid = true
  Symmetric = true
FEATURE [Sketcher::SketchObject] Sketch018  label="Scavo CAM"
  ArcFitTolerance = 1e-06
  AttachmentSupport = -> [YZ_Plane]
  ExternalGeometry = -> [Sketch]
  FullyConstrained = true
  MakeInternals = false
  MapMode = 5
  Placement = pos=(0,0,0) rot=(0.57735,0.57735,0.57735;2.0944rad)
  sketch-geometry (4):
    g0: LineSegment StartX=-7.73 StartY=48 StartZ=0 EndX=7.73 EndY=48 EndZ=0
    g1: LineSegment [constr] StartX=1.07e-14 StartY=48 StartZ=0 EndX=0 EndY=43.5155 EndZ=0
    g2: ArcOfCircle CenterX=9e-15 CenterY=52.42 CenterZ=0 NormalX=0 NormalY=0 NormalZ=1 AngleXU=0 Radius=8.90445 StartAngle=3.66102 EndAngle=5.76376
    g3: Circle [constr] CenterX=9e-15 CenterY=52.42 CenterZ=0 NormalX=0 NormalY=0 NormalZ=1 AngleXU=0 Radius=8.9
  constraints (13):
    c: Horizontal(g0)
    c: DistanceY(g-3,g0) = 0
    c: DistanceX(g0,g0) = 15.46
    c: DistanceX(g0,g-3) = 7.73
    c: DistanceX(g-3) = 0
    c: Coincident(g1,g-3)
    c: PointOnObject(g1,g-2)
    c: Coincident(g2,g0)
    c: Coincident(g2,g0)
    c: PointOnObject(g1,g2)
    c: Diameter(g3) = 17.8
    c: DistanceY(g1,g3) = 4.42
    c: Coincident(g2,g3)
FEATURE [Part::Extrusion] Extrude014  label="Extrude Scavo CAM"
  Base = -> Sketch018
  Dir = (1,0,0)
  DirMode = 2
  FaceMakerClass = Part::FaceMakerBullseye
  FaceMakerMode = 3
  LengthFwd = -34
  LengthRev = 0
  Solid = true
  Symmetric = false
FEATURE [Sketcher::SketchObject] Sketch019  label="scavo rumble"
  ArcFitTolerance = 1e-06
  AttachmentSupport = -> [XZ_Plane]
  ExternalGeometry = -> [Sketch]
  FullyConstrained = true
  MakeInternals = false
  MapMode = 5
  Placement = pos=(0,0,0) rot=(1,0,0;1.5708rad)
  sketch-geometry (6):
    g0: LineSegment StartX=-168.716 StartY=-37.1227 StartZ=0 EndX=-163.58 EndY=-38.7914 EndZ=0
    g1: LineSegment StartX=-163.58 StartY=-38.7914 StartZ=0 EndX=-170.687 EndY=-60.6657 EndZ=0
    g2: LineSegment StartX=-170.687 StartY=-60.6657 StartZ=0 EndX=-175.823 EndY=-58.997 EndZ=0
    g3: LineSegment StartX=-175.823 StartY=-58.997 StartZ=0 EndX=-168.716 EndY=-37.1227 EndZ=0
    g4: LineSegment [constr] StartX=-145.51 StartY=22 StartZ=0 EndX=-165.102 EndY=-38.297 EndZ=0
    g5: LineSegment [constr] StartX=-163.58 StartY=-38.7914 StartZ=0 EndX=-165.102 EndY=-38.297 EndZ=0
  constraints (17):
    c: Coincident(g1,g0)
    c: Coincident(g2,g1)
    c: Coincident(g3,g2)
    c: Coincident(g3,g0)
    c: Parallel(g3,g-3)
    c: Parallel(g3,g1)
    c: Perpendicular(g3,g0)
    c: Perpendicular(g2,g3)
    c: Distance(g2,g0) = 23
    c: Parallel(g4,g-3)
    c: Distance(g4) = 63.4
    c: Coincident(g4,g-3)
    c: Parallel(g5,g0)
    c: Coincident(g5,g0)
    c: Coincident(g5,g4)
    c: Distance(g4,g0) = 3.8
    c: Distance(g4,g0) = 1.6
FEATURE [Part::Extrusion] Extrude015  label="scavo rumble001"
  Base = -> Sketch019
  Dir = (0,-1,2e-16)
  DirMode = 2
  FaceMakerClass = Part::FaceMakerBullseye
  FaceMakerMode = 3
  LengthFwd = 21
  LengthRev = 0
  Solid = true
  Symmetric = true
FEATURE [Sketcher::SketchObject] Sketch020  label="fermo rumble"
  ArcFitTolerance = 1e-06
  AttachmentSupport = -> [XZ_Plane]
  ExternalGeometry = -> [Sketch019,Sketch]
  FullyConstrained = true
  MakeInternals = false
  MapMode = 5
  Placement = pos=(0,0,0) rot=(1,0,0;1.5708rad)
  sketch-geometry (16):
    g0: LineSegment [constr] StartX=-170.849 StartY=-55.9866 StartZ=0 EndX=-172.209 EndY=-60.1713 EndZ=0
    g1: LineSegment [constr] StartX=-172.209 StartY=-60.1713 StartZ=0 EndX=-170.687 EndY=-60.6657 EndZ=0
    g2: LineSegment StartX=-172.262 StartY=-53.2145 StartZ=0 EndX=-170.17 EndY=-53.8943 EndZ=0
    g3: LineSegment StartX=-170.17 StartY=-53.8943 StartZ=0 EndX=-170.849 EndY=-55.9866 EndZ=0
    g4: LineSegment StartX=-170.849 StartY=-55.9866 StartZ=0 EndX=-172.942 EndY=-55.3068 EndZ=0
    g5: LineSegment StartX=-172.942 StartY=-55.3068 StartZ=0 EndX=-172.262 EndY=-53.2145 EndZ=0
    g6: LineSegment StartX=-171.767 StartY=-51.6928 StartZ=0 EndX=-168.344 EndY=-52.8052 EndZ=0
    g7: LineSegment StartX=-168.344 StartY=-52.8052 StartZ=0 EndX=-169.951 EndY=-57.7507 EndZ=0
    g8: LineSegment StartX=-169.951 StartY=-57.7507 StartZ=0 EndX=-173.374 EndY=-56.6383 EndZ=0
    g9: LineSegment StartX=-174.402 StartY=-54.6222 StartZ=0 EndX=-173.784 EndY=-52.72 EndZ=0
    g10: LineSegment [constr] StartX=-173.784 StartY=-52.72 StartZ=0 EndX=-173.289 EndY=-51.1984 EndZ=0
    g11: LineSegment [constr] StartX=-173.289 StartY=-51.1984 StartZ=0 EndX=-171.767 EndY=-51.6928 EndZ=0
    g12: ArcOfCircle CenterX=-172.88 CenterY=-55.1166 CenterZ=0 NormalX=0 NormalY=0 NormalZ=1 AngleXU=0 Radius=1.6 StartAngle=2.82743 EndAngle=4.39823
    g13: GeomPoint [constr] X=-174.896 Y=-56.1438 Z=0
    g14: ArcOfCircle CenterX=-172.262 CenterY=-53.2145 CenterZ=0 NormalX=0 NormalY=0 NormalZ=1 AngleXU=0 Radius=1.6 StartAngle=1.25664 EndAngle=2.82743
    g15: GeomPoint [constr] X=-173.289 Y=-51.1984 Z=0
  constraints (42):
    c: Parallel(g0,g-4)
    c: Distance(g0) = 4.4
    c: Coincident(g1,g0)
    c: Perpendicular(g0,g1)
    c: Distance(g1) = 1.6
    c: Coincident(g1,g-5)
    c: Coincident(g3,g2)
    c: Coincident(g4,g3)
    c: Coincident(g5,g4)
    c: Coincident(g5,g2)
    c: Parallel(g3,g-4)
    c: Parallel(g3,g5)
    c: Perpendicular(g2,g3)
    c: Parallel(g4,g2)
    c: Distance(g2) = 2.2
    c: Distance(g3) = 2.2
    c: Coincident(g7,g6)
    c: Coincident(g8,g7)
    c: Parallel(g7,g-4)
    c: Parallel(g7,g9)
    c: Perpendicular(g6,g7)
    c: Parallel(g6,g8)
    c: Distance(g6,g15) = 5.2
    c: Distance(g7) = 5.2
    c: Coincident(g11,g10)
    c: Parallel(g10,g9)
    c: Parallel(g11,g6)
    c: Distance(g10) = 1.6
    c: Distance(g11) = 1.6
    c: Coincident(g10,g15)
    c: Distance(g11,g2) = 1.6
    c: Distance(g2,g10) = 1.6
    c: PointOnObject(g13,g8)
    c: PointOnObject(g13,g9)
    c: Tangent(g8,g12) = 1.5708
    c: Tangent(g9,g12) = 1.5708
    c: PointOnObject(g15,g9)
    c: Tangent(g6,g14) = 1.5708
    c: Tangent(g9,g14) = 1.5708
    c: Equal(g12,g14)
    c: Coincident(g6,g11)
    c: Coincident(g3,g0)
FEATURE [Part::Extrusion] Extrude016  label="Extrude fermo rumble"
  Base = -> Sketch020
  Dir = (0,-1,2e-16)
  DirMode = 2
  FaceMakerClass = Part::FaceMakerBullseye
  FaceMakerMode = 3
  LengthFwd = 25.2
  LengthRev = 0
  Solid = true
  Symmetric = true
FEATURE [Sketcher::SketchObject] Sketch021  label="perno fermo rumble001"
  ArcFitTolerance = 1e-06
  AttachmentSupport = -> [XZ_Plane001]
  FullyConstrained = true
  MakeInternals = false
  MapMode = 5
  Placement = pos=(0,0,0) rot=(1,0,0;1.5708rad)
  sketch-geometry (16):
    g0: LineSegment StartX=0 StartY=0.45 StartZ=0 EndX=0 EndY=1.55 EndZ=0
    g1: LineSegment StartX=0.45 StartY=2 StartZ=0 EndX=1.55 EndY=2 EndZ=0
    g2: LineSegment StartX=2 StartY=1.55 StartZ=0 EndX=2 EndY=0.45 EndZ=0
    g3: LineSegment StartX=1.55 StartY=0 StartZ=0 EndX=0.45 EndY=0 EndZ=0
    g4: ArcOfCircle [constr] CenterX=0.45 CenterY=1.55 CenterZ=0 NormalX=0 NormalY=0 NormalZ=1 AngleXU=0 Radius=0.45 StartAngle=1.5708 EndAngle=3.14159
    g5: GeomPoint [constr] X=0 Y=2 Z=0
    g6: LineSegment StartX=0.45 StartY=2 StartZ=0 EndX=0 EndY=1.55 EndZ=0
    g7: ArcOfCircle [constr] CenterX=1.55 CenterY=1.55 CenterZ=0 NormalX=0 NormalY=0 NormalZ=1 AngleXU=0 Radius=0.45 StartAngle=0 EndAngle=1.5708
    g8: GeomPoint [constr] X=2 Y=2 Z=0
    g9: LineSegment StartX=2 StartY=1.55 StartZ=0 EndX=1.55 EndY=2 EndZ=0
    g10: ArcOfCircle [constr] CenterX=1.55 CenterY=0.45 CenterZ=0 NormalX=0 NormalY=0 NormalZ=1 AngleXU=0 Radius=0.45 StartAngle=4.71239 EndAngle=6.28319
    g11: GeomPoint [constr] X=2 Y=0 Z=0
    g12: LineSegment StartX=1.55 StartY=0 StartZ=0 EndX=2 EndY=0.45 EndZ=0
    g13: ArcOfCircle [constr] CenterX=0.45 CenterY=0.45 CenterZ=0 NormalX=0 NormalY=0 NormalZ=1 AngleXU=0 Radius=0.45 StartAngle=3.14159 EndAngle=4.71239
    g14: GeomPoint [constr] X=0 Y=0 Z=0
    g15: LineSegment StartX=0 StartY=0.45 StartZ=0 EndX=0.45 EndY=0 EndZ=0
  constraints (35):
    c: Coincident(g14,g-1)
    c: PointOnObject(g5,g-2)
    c: Horizontal(g1)
    c: Vertical(g2)
    c: Horizontal(g3)
    c: DistanceX(g5,g8) = 2
    c: DistanceY(g11,g8) = 2
    c: PointOnObject(g5,g0)
    c: PointOnObject(g5,g1)
    c: Tangent(g0,g4) = 1.5708
    c: Tangent(g1,g4) = 1.5708
    c: Coincident(g6,g0)
    c: Coincident(g6,g1)
    c: PointOnObject(g8,g2)
    c: PointOnObject(g8,g1)
    c: Tangent(g2,g7) = 1.5708
    c: Tangent(g1,g7) = 1.5708
    c: Coincident(g9,g2)
    c: Coincident(g9,g1)
    c: PointOnObject(g11,g2)
    c: PointOnObject(g11,g3)
    c: Tangent(g2,g10) = 1.5708
    c: Tangent(g3,g10) = 1.5708
    c: Coincident(g12,g2)
    c: Coincident(g12,g3)
    c: PointOnObject(g14,g0)
    c: PointOnObject(g14,g3)
    c: Tangent(g0,g13) = 1.5708
    c: Tangent(g3,g13) = 1.5708
    c: Coincident(g15,g0)
    c: Coincident(g15,g3)
    c: Equal(g6,g9)
    c: Equal(g9,g12)
    c: Equal(g12,g15)
    c: DistanceX(g14,g3) = 0.45
FEATURE [Sketcher::SketchObject] Sketch022  label="fori per M3x5(OD)x6(L)"
  ArcFitTolerance = 1e-06
  AttachmentSupport = -> [XZ_Plane]
  ExternalGeometry = -> [Sketch016]
  FullyConstrained = true
  MakeInternals = false
  MapMode = 5
  Placement = pos=(0,0,0) rot=(1,0,0;1.5708rad)
  sketch-geometry (7):
    g0: Circle CenterX=-5.6 CenterY=34.8 CenterZ=0 NormalX=0 NormalY=0 NormalZ=1 AngleXU=0 Radius=2.5
    g1: Circle CenterX=-5.6 CenterY=7.6 CenterZ=0 NormalX=0 NormalY=0 NormalZ=1 AngleXU=0 Radius=2.5
    g2: Circle CenterX=-78.51 CenterY=34.8 CenterZ=0 NormalX=0 NormalY=0 NormalZ=1 AngleXU=0 Radius=2.5
    g3: Circle CenterX=-78.51 CenterY=7.6 CenterZ=0 NormalX=0 NormalY=0 NormalZ=1 AngleXU=0 Radius=2.5
    g4: Circle CenterX=-184.08 CenterY=34.8 CenterZ=0 NormalX=0 NormalY=0 NormalZ=1 AngleXU=0 Radius=2.5
    g5: Circle CenterX=-179.305 CenterY=-76.8316 CenterZ=0 NormalX=0 NormalY=0 NormalZ=1 AngleXU=0 Radius=2.5
    g6: Circle CenterX=-213.443 CenterY=-76.8316 CenterZ=0 NormalX=0 NormalY=0 NormalZ=1 AngleXU=0 Radius=2.5
  constraints (14):
    c: Diameter(g0) = 5
    c: Diameter(g1) = 5
    c: Diameter(g2) = 5
    c: Diameter(g3) = 5
    c: Diameter(g4) = 5
    c: Diameter(g5) = 5
    c: Diameter(g6) = 5
    c: Coincident(g0,g-8)
    c: Coincident(g1,g-9)
    c: Coincident(g2,g-6)
    c: Coincident(g3,g-7)
    c: Coincident(g4,g-5)
    c: Coincident(g5,g-4)
    c: Coincident(g6,g-3)
FEATURE [Part::Extrusion] Extrude018  label="Extrude fori M3x5x6 - dx"
  Base = -> Sketch022
  Dir = (0,-1,2e-16)
  DirMode = 2
  FaceMakerClass = Part::FaceMakerBullseye
  FaceMakerMode = 3
  LengthFwd = 6.2
  LengthRev = 0
  Placement = pos=(0,-9.5,0) rot=(0,0,1;0rad)
  Solid = true
  Symmetric = true
FEATURE [Part::Extrusion] Extrude019  label="Extrude fori M3x5x6 - sx"
  Base = -> Sketch022
  Dir = (0,-1,2e-16)
  DirMode = 2
  FaceMakerClass = Part::FaceMakerBullseye
  FaceMakerMode = 3
  LengthFwd = 6.2
  LengthRev = 0
  Placement = pos=(0,9.5,0) rot=(0,0,1;0rad)
  Solid = true
  Symmetric = true
FEATURE [Sketcher::SketchObject] Sketch023  label="foro anteriore M3x5x6"
  ArcFitTolerance = 1e-06
  AttachmentSupport = -> [YZ_Plane]
  FullyConstrained = true
  MakeInternals = false
  MapMode = 5
  Placement = pos=(0,0,0) rot=(0.57735,0.57735,0.57735;2.0944rad)
  sketch-geometry (2):
    g0: LineSegment [constr] StartX=0 StartY=0 StartZ=0 EndX=0 EndY=38.6 EndZ=0
    g1: Circle CenterX=0 CenterY=38.6 CenterZ=0 NormalX=0 NormalY=0 NormalZ=1 AngleXU=0 Radius=2.5
  constraints (5):
    c: Coincident(g0,g-1)
    c: PointOnObject(g0,g-2)
    c: DistanceY(g0,g0) = 38.6
    c: Diameter(g1) = 5
    c: Coincident(g1,g0)
FEATURE [Part::Extrusion] Extrude020  label="Extrude foro anteriore M3x5x6"
  Base = -> Sketch023
  Dir = (1,0,0)
  DirMode = 2
  FaceMakerClass = Part::FaceMakerBullseye
  FaceMakerMode = 3
  LengthFwd = -6.2
  LengthRev = 0
  Solid = true
  Symmetric = false
FEATURE [Sketcher::SketchObject] Sketch024  label="fori per viti frontale"
  ArcFitTolerance = 1e-06
  AttachmentSupport = -> [YZ_Plane]
  FullyConstrained = true
  MakeInternals = false
  MapMode = 5
  Placement = pos=(0,0,0) rot=(0.57735,0.57735,0.57735;2.0944rad)
  sketch-geometry (9):
    g0: LineSegment [constr] StartX=-10.3 StartY=30.721 StartZ=0 EndX=10.3 EndY=30.721 EndZ=0
    g1: LineSegment [constr] StartX=10.3 StartY=30.721 StartZ=0 EndX=10.3 EndY=10.121 EndZ=0
    g2: LineSegment [constr] StartX=10.3 StartY=10.121 StartZ=0 EndX=-10.3 EndY=10.121 EndZ=0
    g3: LineSegment [constr] StartX=-10.3 StartY=10.121 StartZ=0 EndX=-10.3 EndY=30.721 EndZ=0
    g4: LineSegment [constr] StartX=0 StartY=0 StartZ=0 EndX=0 EndY=10.121 EndZ=0
    g5: Circle CenterX=-10.3 CenterY=30.721 CenterZ=0 NormalX=0 NormalY=0 NormalZ=1 AngleXU=0 Radius=2
    g6: Circle CenterX=10.3 CenterY=30.721 CenterZ=0 NormalX=0 NormalY=0 NormalZ=1 AngleXU=0 Radius=2
    g7: Circle CenterX=-10.3 CenterY=10.121 CenterZ=0 NormalX=0 NormalY=0 NormalZ=1 AngleXU=0 Radius=2
    g8: Circle CenterX=10.3 CenterY=10.121 CenterZ=0 NormalX=0 NormalY=0 NormalZ=1 AngleXU=0 Radius=2
  constraints (22):
    c: Horizontal(g0)
    c: Coincident(g1,g0)
    c: Vertical(g1)
    c: Coincident(g2,g1)
    c: Horizontal(g2)
    c: Coincident(g3,g2)
    c: Coincident(g3,g0)
    c: Vertical(g3)
    c: DistanceX(g0,g0) = 20.6
    c: DistanceY(g3,g3) = 20.6
    c: Coincident(g4,g-1)
    c: PointOnObject(g4,g-2)
    c: DistanceY(g4,g4) = 10.121
    c: Symmetric(g2,g2,g4)
    c: Diameter(g5) = 4
    c: Diameter(g6) = 4
    c: Diameter(g7) = 4
    c: Diameter(g8) = 4
    c: Coincident(g5,g0)
    c: Coincident(g6,g0)
    c: Coincident(g7,g2)
    c: Coincident(g8,g1)
FEATURE [Part::Extrusion] Extrude021  label="Extrude fori per viti frontale"
  Base = -> Sketch024
  Dir = (1,0,0)
  DirMode = 2
  FaceMakerClass = Part::FaceMakerBullseye
  FaceMakerMode = 3
  LengthFwd = -2.4
  LengthRev = 0
  Solid = true
  Symmetric = false
FEATURE [Sketcher::SketchObject] Sketch025  label="foro per filo CAM"
  ArcFitTolerance = 1e-06
  AttachmentSupport = -> [XZ_Plane]
  ExternalGeometry = -> [Sketch]
  FullyConstrained = true
  MakeInternals = false
  MapMode = 5
  Placement = pos=(0,0,0) rot=(1,0,0;1.5708rad)
  sketch-geometry (4):
    g0: LineSegment StartX=-44.6 StartY=41.2 StartZ=0 EndX=-44.6 EndY=36.4 EndZ=0
    g1: LineSegment StartX=-44.6 StartY=36.4 StartZ=0 EndX=-54.6 EndY=36.4 EndZ=0
    g2: LineSegment StartX=-54.6 StartY=36.4 StartZ=0 EndX=-50.4 EndY=41.2 EndZ=0
    g3: LineSegment StartX=-50.4 StartY=41.2 StartZ=0 EndX=-44.6 EndY=41.2 EndZ=0
  constraints (11):
    c: Vertical(g0)
    c: Coincident(g1,g0)
    c: Horizontal(g1)
    c: Coincident(g2,g1)
    c: Coincident(g3,g2)
    c: Coincident(g3,g0)
    c: Horizontal(g3)
    c: Coincident(g0,g-3)
    c: DistanceY(g0,g-4) = 0
    c: DistanceX(g3,g3) = 5.8
    c: DistanceX(g1,g1) = 10
FEATURE [Part::Extrusion] Extrude022  label="Extrude foro per filo CAM dx"
  Base = -> Sketch025
  Dir = (0,-1,2e-16)
  DirMode = 2
  FaceMakerClass = Part::FaceMakerBullseye
  FaceMakerMode = 3
  LengthFwd = 4.9
  LengthRev = 0
  Placement = pos=(0,6.95,0) rot=(0,0,1;0rad)
  Solid = true
  Symmetric = true
FEATURE [Part::Extrusion] Extrude023  label="Extrude foro per filo CAM sx"
  Base = -> Sketch025
  Dir = (0,-1,2e-16)
  DirMode = 2
  FaceMakerClass = Part::FaceMakerBullseye
  FaceMakerMode = 3
  LengthFwd = 4.9
  LengthRev = 0
  Placement = pos=(0,-6.95,0) rot=(0,0,1;0rad)
  Solid = true
  Symmetric = true
FEATURE [Sketcher::SketchObject] Sketch026  label="foro sotto anteriore M3x5x6"
  ArcFitTolerance = 1e-06
  AttachmentSupport = -> [XY_Plane]
  FullyConstrained = true
  MakeInternals = false
  MapMode = 5
  sketch-geometry (2):
    g0: LineSegment [constr] StartX=0 StartY=0 StartZ=0 EndX=-16.5 EndY=0 EndZ=0
    g1: Circle CenterX=-16.5 CenterY=0 CenterZ=0 NormalX=0 NormalY=0 NormalZ=1 AngleXU=0 Radius=2.5
  constraints (5):
    c: Distance(g0) = 16.5
    c: Coincident(g0,g-1)
    c: PointOnObject(g0,g-1)
    c: Diameter(g1) = 5
    c: Coincident(g0,g1)
FEATURE [Sketcher::SketchObject] Sketch027  label="foro sotto posteriore M3x5x6"
  ArcFitTolerance = 1e-06
  AttachmentSupport = -> [XY_Plane]
  ExternalGeometry = -> [Sketch]
  FullyConstrained = true
  MakeInternals = false
  MapMode = 5
  sketch-geometry (2):
    g0: LineSegment [constr] StartX=-82.8 StartY=2e-16 StartZ=0 EndX=-71.3 EndY=2e-16 EndZ=0
    g1: Circle CenterX=-71.3 CenterY=2e-16 CenterZ=0 NormalX=0 NormalY=0 NormalZ=1 AngleXU=0 Radius=2.5
  constraints (5):
    c: Distance(g0) = 11.5
    c: Coincident(g0,g-3)
    c: PointOnObject(g0,g-3)
    c: Diameter(g1) = 5
    c: Coincident(g1,g0)
FEATURE [Sketcher::SketchObject] Sketch029  label="fori sotto impugnatura"
  ArcFitTolerance = 1e-06
  AttachmentSupport = -> [XY_Plane]
  ExternalGeometry = -> [Sketch]
  FullyConstrained = true
  MakeInternals = false
  MapMode = 5
  sketch-geometry (15):
    g0: LineSegment [constr] StartX=-175.232 StartY=-1.83e-14 StartZ=0 EndX=-191.232 EndY=0 EndZ=0
    g1: Circle CenterX=-191.232 CenterY=0 CenterZ=0 NormalX=0 NormalY=0 NormalZ=1 AngleXU=0 Radius=3.95
    g2: LineSegment [constr] StartX=-175.232 StartY=-1.83e-14 StartZ=0 EndX=-204.275 EndY=0 EndZ=0
    g3: LineSegment StartX=-204.275 StartY=3.525 StartZ=0 EndX=-204.275 EndY=-3.525 EndZ=0
    g4: LineSegment StartX=-205.4 StartY=-4.65 StartZ=0 EndX=-206.65 EndY=-4.65 EndZ=0
    g5: LineSegment StartX=-207.775 StartY=-3.525 StartZ=0 EndX=-207.775 EndY=3.525 EndZ=0
    g6: LineSegment StartX=-206.65 StartY=4.65 StartZ=0 EndX=-205.4 EndY=4.65 EndZ=0
    g7: ArcOfCircle CenterX=-206.65 CenterY=3.525 CenterZ=0 NormalX=0 NormalY=0 NormalZ=1 AngleXU=0 Radius=1.125 StartAngle=1.5708 EndAngle=3.14159
    g8: GeomPoint [constr] X=-207.775 Y=4.65 Z=0
    g9: ArcOfCircle CenterX=-205.4 CenterY=3.525 CenterZ=0 NormalX=0 NormalY=0 NormalZ=1 AngleXU=0 Radius=1.125 StartAngle=0 EndAngle=1.5708
    g10: GeomPoint [constr] X=-204.275 Y=4.65 Z=0
    g11: ArcOfCircle CenterX=-205.4 CenterY=-3.525 CenterZ=0 NormalX=0 NormalY=0 NormalZ=1 AngleXU=0 Radius=1.125 StartAngle=4.71239 EndAngle=6.28319
    g12: GeomPoint [constr] X=-204.275 Y=-4.65 Z=0
    g13: ArcOfCircle CenterX=-206.65 CenterY=-3.525 CenterZ=0 NormalX=0 NormalY=0 NormalZ=1 AngleXU=0 Radius=1.125 StartAngle=3.14159 EndAngle=4.71239
    g14: GeomPoint [constr] X=-207.775 Y=-4.65 Z=0
  constraints (35):
    c: Distance(g0) = 16
    c: Coincident(g0,g-3)
    c: PointOnObject(g0,g-1)
    c: Diameter(g1) = 7.9
    c: Coincident(g1,g0)
    c: Coincident(g2,g0)
    c: PointOnObject(g2,g-1)
    c: Vertical(g3)
    c: Horizontal(g4)
    c: Vertical(g5)
    c: Horizontal(g6)
    c: DistanceY(g12,g10) = 9.3
    c: DistanceX(g8,g10) = 3.5
    c: Symmetric(g10,g12,g2)
    c: PointOnObject(g8,g5)
    c: PointOnObject(g8,g6)
    c: Tangent(g5,g7) = 1.5708
    c: Tangent(g6,g7) = 1.5708
    c: PointOnObject(g10,g3)
    c: PointOnObject(g10,g6)
    c: Tangent(g3,g9) = 1.5708
    c: Tangent(g6,g9) = 1.5708
    c: PointOnObject(g12,g3)
    c: PointOnObject(g12,g4)
    c: Tangent(g3,g11) = 1.5708
    c: Tangent(g4,g11) = 1.5708
    c: PointOnObject(g14,g4)
    c: PointOnObject(g14,g5)
    c: Tangent(g4,g13) = 1.5708
    c: Tangent(g5,g13) = 1.5708
    c: Equal(g7,g9)
    c: Equal(g9,g11)
    c: Equal(g11,g13)
    c: DistanceX(g6,g6) = 1.25
    c: DistanceX(g-5,g5) = 6.8
FEATURE [Sketcher::SketchObject] Sketch030  label="fori superiori per solenoide e oled"
  ArcFitTolerance = 1e-06
  AttachmentSupport = -> [XY_Plane]
  ExternalGeometry = -> [Sketch]
  FullyConstrained = true
  MakeInternals = false
  MapMode = 5
  sketch-geometry (33):
    g0: LineSegment [constr] StartX=-181.6 StartY=1.12e-14 StartZ=0 EndX=-169.91 EndY=0 EndZ=0
    g1: LineSegment [constr] StartX=-169.91 StartY=0 StartZ=0 EndX=-169.91 EndY=-2.6 EndZ=0
    g2: LineSegment [constr] StartX=-169.91 StartY=0 StartZ=0 EndX=-169.91 EndY=2.6 EndZ=0
    g3: LineSegment StartX=-169.91 StartY=4.975 StartZ=0 EndX=-169.91 EndY=8.225 EndZ=0
    g4: LineSegment StartX=-167.535 StartY=10.6 StartZ=0 EndX=-167.285 EndY=10.6 EndZ=0
    g5: LineSegment StartX=-164.91 StartY=8.225 StartZ=0 EndX=-164.91 EndY=4.975 EndZ=0
    g6: LineSegment StartX=-167.285 StartY=2.6 StartZ=0 EndX=-167.535 EndY=2.6 EndZ=0
    g7: LineSegment StartX=-169.91 StartY=-4.975 StartZ=0 EndX=-169.91 EndY=-8.225 EndZ=0
    g8: LineSegment StartX=-167.535 StartY=-10.6 StartZ=0 EndX=-167.285 EndY=-10.6 EndZ=0
    g9: LineSegment StartX=-164.91 StartY=-8.225 StartZ=0 EndX=-164.91 EndY=-4.975 EndZ=0
    g10: LineSegment StartX=-167.285 StartY=-2.6 StartZ=0 EndX=-167.535 EndY=-2.6 EndZ=0
    g11: ArcOfCircle CenterX=-167.535 CenterY=8.225 CenterZ=0 NormalX=0 NormalY=0 NormalZ=1 AngleXU=0 Radius=2.375 StartAngle=1.5708 EndAngle=3.14159
    g12: GeomPoint [constr] X=-169.91 Y=10.6 Z=0
    g13: ArcOfCircle CenterX=-167.285 CenterY=8.225 CenterZ=0 NormalX=0 NormalY=0 NormalZ=1 AngleXU=0 Radius=2.375 StartAngle=0 EndAngle=1.5708
    g14: GeomPoint [constr] X=-164.91 Y=10.6 Z=0
    g15: ArcOfCircle CenterX=-167.285 CenterY=4.975 CenterZ=0 NormalX=0 NormalY=0 NormalZ=1 AngleXU=0 Radius=2.375 StartAngle=4.71239 EndAngle=6.28319
    g16: GeomPoint [constr] X=-164.91 Y=2.6 Z=0
    g17: ArcOfCircle CenterX=-167.535 CenterY=4.975 CenterZ=0 NormalX=0 NormalY=0 NormalZ=1 AngleXU=0 Radius=2.375 StartAngle=3.14159 EndAngle=4.71239
    g18: GeomPoint [constr] X=-169.91 Y=2.6 Z=0
    g19: ArcOfCircle CenterX=-167.535 CenterY=-4.975 CenterZ=0 NormalX=0 NormalY=0 NormalZ=1 AngleXU=0 Radius=2.375 StartAngle=1.5708 EndAngle=3.14159
    g20: GeomPoint [constr] X=-169.91 Y=-2.6 Z=0
    g21: ArcOfCircle CenterX=-167.285 CenterY=-4.975 CenterZ=0 NormalX=0 NormalY=0 NormalZ=1 AngleXU=0 Radius=2.375 StartAngle=0 EndAngle=1.5708
    g22: GeomPoint [constr] X=-164.91 Y=-2.6 Z=0
    g23: ArcOfCircle CenterX=-167.285 CenterY=-8.225 CenterZ=0 NormalX=0 NormalY=0 NormalZ=1 AngleXU=0 Radius=2.375 StartAngle=4.71239 EndAngle=6.28319
    g24: GeomPoint [constr] X=-164.91 Y=-10.6 Z=0
    g25: ArcOfCircle CenterX=-167.535 CenterY=-8.225 CenterZ=0 NormalX=0 NormalY=0 NormalZ=1 AngleXU=0 Radius=2.375 StartAngle=3.14159 EndAngle=4.71239
    g26: GeomPoint [constr] X=-169.91 Y=-10.6 Z=0
    g27: LineSegment [constr] StartX=-181.6 StartY=1.12e-14 StartZ=0 EndX=-152.209 EndY=0 EndZ=0
    g28: LineSegment [constr] StartX=-181.6 StartY=1.12e-14 StartZ=0 EndX=-130.41 EndY=0 EndZ=0
    g29: LineSegment [constr] StartX=-152.209 StartY=0 StartZ=0 EndX=-152.209 EndY=6.95 EndZ=0
    g30: LineSegment [constr] StartX=-130.41 StartY=0 StartZ=0 EndX=-130.41 EndY=-6.95 EndZ=0
    g31: Circle CenterX=-152.209 CenterY=6.95 CenterZ=0 NormalX=0 NormalY=0 NormalZ=1 AngleXU=0 Radius=2.1
    g32: Circle CenterX=-130.41 CenterY=-6.95 CenterZ=0 NormalX=0 NormalY=0 NormalZ=1 AngleXU=0 Radius=2.1
  constraints (79):
    c: Distance(g0) = 11.69
    c: PointOnObject(g0,g-1)
    c: Coincident(g-4,g0)
    c: Distance(g1) = 2.6
    c: Coincident(g1,g0)
    c: Vertical(g1)
    c: Distance(g2) = 2.6
    c: Coincident(g2,g0)
    c: Vertical(g2)
    c: Distance(g18,g12) = 8
    c: Coincident(g18,g2)
    c: Vertical(g3)
    c: Distance(g14,g12) = 5
    c: Horizontal(g4)
    c: Distance(g16,g14) = 8
    c: Vertical(g5)
    c: Distance(g26,g20) = 8
    c: Coincident(g20,g1)
    c: Vertical(g7)
    c: Distance(g26,g24) = 5
    c: Horizontal(g8)
    c: Distance(g24,g22) = 8
    c: Vertical(g9)
    c: PointOnObject(g12,g3)
    c: PointOnObject(g12,g4)
    c: Tangent(g3,g11) = 1.5708
    c: Tangent(g4,g11) = 1.5708
    c: PointOnObject(g14,g5)
    c: PointOnObject(g14,g4)
    c: Tangent(g5,g13) = 1.5708
    c: Tangent(g4,g13) = 1.5708
    c: PointOnObject(g16,g5)
    c: PointOnObject(g16,g6)
    c: Tangent(g5,g15) = 1.5708
    c: Tangent(g6,g15) = 1.5708
    c: PointOnObject(g18,g3)
    c: PointOnObject(g18,g6)
    c: Tangent(g3,g17) = 1.5708
    c: Tangent(g6,g17) = 1.5708
    c: Equal(g11,g13)
    c: Equal(g13,g15)
    c: Equal(g15,g17)
    c: DistanceX(g4,g4) = 0.25
    c: PointOnObject(g20,g7)
    c: PointOnObject(g20,g10)
    c: Tangent(g7,g19) = -1.5708
    c: Tangent(g10,g19) = -1.5708
    c: PointOnObject(g22,g9)
    c: PointOnObject(g22,g10)
    c: Tangent(g9,g21) = -1.5708
    c: Tangent(g10,g21) = -1.5708
    c: PointOnObject(g24,g9)
    c: PointOnObject(g24,g8)
    c: Tangent(g9,g23) = -1.5708
    c: Tangent(g8,g23) = -1.5708
    c: PointOnObject(g26,g8)
    c: PointOnObject(g26,g7)
    c: Tangent(g8,g25) = -1.5708
    c: Tangent(g7,g25) = -1.5708
    c: Equal(g19,g21)
    c: Equal(g21,g23)
    c: Equal(g23,g25)
    c: DistanceX(g10,g10) = 0.25
    c: Distance(g27) = 29.391
    c: Coincident(g27,g0)
    c: PointOnObject(g27,g-1)
    c: Distance(g28) = 51.19
    c: Coincident(g28,g0)
    c: PointOnObject(g28,g-1)
    c: Distance(g29) = 6.95
    c: Coincident(g29,g27)
    c: Vertical(g29)
    c: Distance(g30) = 6.95
    c: Coincident(g30,g28)
    c: Vertical(g30)
    c: Diameter(g31) = 4.2
    c: Diameter(g32) = 4.2
    c: Coincident(g32,g30)
    c: Coincident(g31,g29)
FEATURE [Sketcher::SketchObject] Sketch031  label="fori inferiori switch pompa"
  ArcFitTolerance = 1e-06
  AttachmentSupport = -> [XY_Plane]
  ExternalGeometry = -> [Sketch]
  FullyConstrained = true
  MakeInternals = false
  MapMode = 5
  sketch-geometry (4):
    g0: LineSegment [constr] StartX=-57.2 StartY=1.9e-15 StartZ=0 EndX=-62.45 EndY=1.9e-15 EndZ=0
    g1: LineSegment [constr] StartX=-62.45 StartY=3.25 StartZ=0 EndX=-62.45 EndY=-3.25 EndZ=0
    g2: Circle CenterX=-62.45 CenterY=3.25 CenterZ=0 NormalX=0 NormalY=0 NormalZ=1 AngleXU=0 Radius=1.6
    g3: Circle CenterX=-62.45 CenterY=-3.25 CenterZ=0 NormalX=0 NormalY=0 NormalZ=1 AngleXU=0 Radius=1.6
  constraints (10):
    c: Distance(g0) = 5.25
    c: Coincident(g0,g-3)
    c: PointOnObject(g0,g-3)
    c: Vertical(g1)
    c: DistanceY(g1,g1) = 6.5
    c: Symmetric(g1,g1,g0)
    c: Diameter(g2) = 3.2
    c: Diameter(g3) = 3.2
    c: Coincident(g2,g1)
    c: Coincident(g3,g1)
FEATURE [Sketcher::SketchObject] Sketch032  label="spazio per PILA 18650"
  ArcFitTolerance = 1e-06
  AttachmentSupport = -> [XY_Plane]
  ExternalGeometry = -> [Sketch]
  FullyConstrained = true
  MakeInternals = false
  MapMode = 5
  sketch-geometry (2):
    g0: LineSegment [constr] StartX=-178.142 StartY=-1.74e-14 StartZ=0 EndX=-191.142 EndY=-1.83e-14 EndZ=0
    g1: Circle CenterX=-191.142 CenterY=-1.83e-14 CenterZ=0 NormalX=0 NormalY=0 NormalZ=1 AngleXU=0 Radius=10.5
  constraints (5):
    c: Distance(g0) = 13
    c: Coincident(g0,g-3)
    c: PointOnObject(g0,g-4)
    c: Diameter(g1) = 21
    c: Coincident(g1,g0)
FEATURE [Part::Extrusion] Extrude030  label="Extrude spazio per PILA 18650"
  Base = -> Sketch032
  Dir = (0,0,1)
  DirLink = -> Sketch [Edge45]
  DirMode = 2
  FaceMakerClass = Part::FaceMakerBullseye
  FaceMakerMode = 3
  LengthFwd = 76
  LengthRev = 0
  Placement = pos=(6,0,-72) rot=(0,0,1;0rad)
  Solid = true
  Symmetric = false
FEATURE [Sketcher::SketchObject] Sketch033  label="fermo per scheda micro"
  ArcFitTolerance = 1e-06
  AttachmentSupport = -> [XZ_Plane]
  ExternalGeometry = -> [Sketch]
  FullyConstrained = true
  MakeInternals = false
  MapMode = 5
  Placement = pos=(0,0,0) rot=(1,0,0;1.5708rad)
  sketch-geometry (12):
    g0: LineSegment StartX=-11.6 StartY=6 StartZ=0 EndX=-4 EndY=6 EndZ=0
    g1: LineSegment StartX=-4 StartY=6 StartZ=0 EndX=-4 EndY=36.4 EndZ=0
    g2: LineSegment StartX=-4 StartY=36.4 StartZ=0 EndX=-11.6 EndY=36.4 EndZ=0
    g3: LineSegment StartX=-11.6 StartY=36.4 StartZ=0 EndX=-11.6 EndY=6 EndZ=0
    g4: LineSegment StartX=-80.11 StartY=11.6 StartZ=0 EndX=-70.51 EndY=11.6 EndZ=0
    g5: LineSegment StartX=-70.51 StartY=11.6 StartZ=0 EndX=-70.51 EndY=6 EndZ=0
    g6: LineSegment StartX=-70.51 StartY=6 StartZ=0 EndX=-80.11 EndY=6 EndZ=0
    g7: LineSegment StartX=-80.11 StartY=6 StartZ=0 EndX=-80.11 EndY=11.6 EndZ=0
    g8: LineSegment StartX=-78.51 StartY=36.4 StartZ=0 EndX=-70.51 EndY=36.4 EndZ=0
    g9: LineSegment StartX=-70.51 StartY=36.4 StartZ=0 EndX=-70.51 EndY=30.8 EndZ=0
    g10: LineSegment StartX=-70.51 StartY=30.8 StartZ=0 EndX=-78.51 EndY=30.8 EndZ=0
    g11: LineSegment StartX=-78.51 StartY=30.8 StartZ=0 EndX=-78.51 EndY=36.4 EndZ=0
  constraints (33):
    c: Horizontal(g0)
    c: Coincident(g1,g0)
    c: Coincident(g2,g1)
    c: Horizontal(g2)
    c: Coincident(g3,g2)
    c: Coincident(g3,g0)
    c: Vertical(g3)
    c: DistanceX(g2,g2) = 7.6
    c: Coincident(g1,g-3)
    c: Coincident(g0,g-3)
    c: Horizontal(g4)
    c: Coincident(g5,g4)
    c: Vertical(g5)
    c: Coincident(g6,g5)
    c: Horizontal(g6)
    c: Coincident(g7,g6)
    c: Coincident(g7,g4)
    c: Vertical(g7)
    c: DistanceY(g5,g5) = 5.6
    c: DistanceX(g4,g4) = 9.6
    c: Coincident(g9,g8)
    c: Vertical(g9)
    c: Coincident(g10,g9)
    c: Horizontal(g10)
    c: Coincident(g11,g10)
    c: Coincident(g11,g8)
    c: Vertical(g11)
    c: DistanceY(g9,g9) = 5.6
    c: DistanceX(g10,g10) = 8
    c: Coincident(g4,g-4)
    c: DistanceX(g4,g10) = 1.6
    c: Horizontal(g8)
    c: DistanceY(g8,g1) = 0
FEATURE [Sketcher::SketchObject] Sketch034  label="buchi guida rail"
  ArcFitTolerance = 1e-06
  AttachmentSupport = -> [XY_Plane]
  ExternalGeometry = -> [Sketch]
  FullyConstrained = true
  MakeInternals = false
  MapMode = 5
  sketch-geometry (6):
    g0: LineSegment [constr] StartX=-100.8 StartY=9.1e-15 StartZ=0 EndX=-93.3 EndY=0 EndZ=0
    g1: LineSegment [constr] StartX=-93.3 StartY=0 StartZ=0 EndX=-73.3 EndY=0 EndZ=0
    g2: LineSegment [constr] StartX=-73.3 StartY=0 StartZ=0 EndX=-53.3 EndY=0 EndZ=0
    g3: Circle CenterX=-93.3 CenterY=0 CenterZ=0 NormalX=0 NormalY=0 NormalZ=1 AngleXU=0 Radius=2.5
    g4: Circle CenterX=-73.3 CenterY=0 CenterZ=0 NormalX=0 NormalY=0 NormalZ=1 AngleXU=0 Radius=2.5
    g5: Circle CenterX=-53.3 CenterY=0 CenterZ=0 NormalX=0 NormalY=0 NormalZ=1 AngleXU=0 Radius=2.5
  constraints (15):
    c: Distance(g0) = 7.5
    c: Coincident(g0,g-3)
    c: PointOnObject(g0,g-1)
    c: Distance(g1) = 20
    c: Coincident(g1,g0)
    c: PointOnObject(g1,g-1)
    c: Distance(g2) = 20
    c: Coincident(g2,g1)
    c: PointOnObject(g2,g-1)
    c: Diameter(g3) = 5
    c: Diameter(g4) = 5
    c: Diameter(g5) = 5
    c: Coincident(g3,g0)
    c: Coincident(g4,g1)
    c: Coincident(g5,g2)
FEATURE [Part::Extrusion] Extrude032  label="Extrude buchi guida rail"
  Base = -> Sketch034
  Dir = (0,0,1)
  DirMode = 2
  FaceMakerClass = Part::FaceMakerBullseye
  FaceMakerMode = 3
  LengthFwd = -6.2
  LengthRev = 0
  Placement = pos=(0,0,43.2) rot=(0,0,1;0rad)
  Solid = true
  Symmetric = false
FEATURE [Part::Extrusion] Extrude033  label="Extrude fori superiori per solenoide e oled001"
  Base = -> Sketch030
  Dir = (0,0,1)
  DirMode = 2
  FaceMakerClass = Part::FaceMakerBullseye
  FaceMakerMode = 3
  LengthFwd = -4.8
  LengthRev = 0
  Placement = pos=(0,0,41.2) rot=(0,0,1;0rad)
  Solid = true
  Symmetric = false
FEATURE [Part::Extrusion] Extrude034  label="Extrude fori sotto impugnatura001"
  Base = -> Sketch029
  Dir = (0,0,1)
  DirMode = 2
  FaceMakerClass = Part::FaceMakerBullseye
  FaceMakerMode = 3
  LengthFwd = 5
  LengthRev = 0
  Placement = pos=(0,0,-83) rot=(0,0,1;0rad)
  Solid = true
  Symmetric = false
FEATURE [Part::Extrusion] Extrude035  label="Extrude fori inferiori switch pompa001"
  Base = -> Sketch031
  Dir = (0,0,1)
  DirMode = 2
  FaceMakerClass = Part::FaceMakerBullseye
  FaceMakerMode = 3
  LengthFwd = 4
  LengthRev = 0
  Placement = pos=(0,0,-1.7) rot=(0,0,1;0rad)
  Solid = true
  Symmetric = false
FEATURE [Part::Extrusion] Extrude036  label="Extrude foro sotto posteriore M3x5x007"
  Base = -> Sketch027
  Dir = (0,0,1)
  DirMode = 2
  FaceMakerClass = Part::FaceMakerBullseye
  FaceMakerMode = 3
  LengthFwd = 6.2
  LengthRev = 0
  Placement = pos=(0,0,-9.6) rot=(0,0,1;0rad)
  Solid = true
  Symmetric = false
FEATURE [Part::Extrusion] Extrude037  label="Extrude foro sotto anteriore M3x5x007"
  Base = -> Sketch026
  Dir = (0,0,1)
  DirMode = 2
  FaceMakerClass = Part::FaceMakerBullseye
  FaceMakerMode = 3
  LengthFwd = 6.2
  LengthRev = 0
  Solid = true
  Symmetric = false
FEATURE [Sketcher::SketchObject] Sketch035  label="foro per fissaggio micro"
  ArcFitTolerance = 1e-06
  AttachmentSupport = -> [XZ_Plane]
  ExternalGeometry = -> [Sketch,Sketch033]
  FullyConstrained = true
  MakeInternals = false
  MapMode = 5
  Placement = pos=(0,0,0) rot=(1,0,0;1.5708rad)
  sketch-geometry (3):
    g0: Circle CenterX=-7.8 CenterY=21.2 CenterZ=0 NormalX=0 NormalY=0 NormalZ=1 AngleXU=0 Radius=1.6
    g1: GeomPoint [constr] X=-4 Y=21.2 Z=0
    g2: LineSegment [constr] StartX=-4 StartY=21.2 StartZ=0 EndX=-11.6 EndY=21.2 EndZ=0
  constraints (6):
    c: Diameter(g0) = 3.2
    c: Symmetric(g-3,g-3,g1)
    c: Coincident(g2,g1)
    c: Horizontal(g2)
    c: DistanceX(g-4,g2) = 0
    c: Symmetric(g2,g1,g0)
FEATURE [Part::Extrusion] Extrude038  label="Extrude foro per fissaggio micro"
  Base = -> Sketch035
  Dir = (0,-1,2e-16)
  DirMode = 2
  FaceMakerClass = Part::FaceMakerBullseye
  FaceMakerMode = 3
  LengthFwd = 3
  LengthRev = 0
  Placement = pos=(0,8.6,0) rot=(0,0,1;0rad)
  Solid = true
  Symmetric = false
FEATURE [Sketcher::SketchObject] Sketch036  label="supporto per alimentatore"
  ArcFitTolerance = 1e-06
  AttachmentSupport = -> [XZ_Plane]
  ExternalGeometry = -> [Sketch,Sketch016,Sketch022]
  FullyConstrained = true
  MakeInternals = false
  MapMode = 5
  Placement = pos=(0,0,0) rot=(1,0,0;1.5708rad)
  sketch-geometry (5):
    g0: LineSegment StartX=-211.843 StartY=-50.0944 StartZ=0 EndX=-211.843 EndY=-80.4316 EndZ=0
    g1: LineSegment StartX=-211.843 StartY=-50.0944 StartZ=0 EndX=-207.775 EndY=-41.3701 EndZ=0
    g2: LineSegment [constr] StartX=-209.443 StartY=-50.0944 StartZ=0 EndX=-209.443 EndY=-80.4316 EndZ=0
    g3: LineSegment StartX=-207.775 StartY=-41.3701 StartZ=0 EndX=-207.775 EndY=-80.4316 EndZ=0
    g4: LineSegment StartX=-211.843 StartY=-80.4316 StartZ=0 EndX=-207.775 EndY=-80.4316 EndZ=0
  constraints (15):
    c: Vertical(g0)
    c: Coincident(g1,g0)
    c: Vertical(g2)
    c: Tangent(g2,g-5)
    c: Coincident(g3,g1)
    c: Vertical(g3)
    c: DistanceY(g-3,g3) = -2
    c: Tangent(g1,g-8)
    c: DistanceY(g-3,g0) = -2
    c: Coincident(g4,g0)
    c: Coincident(g4,g3)
    c: Tangent(g0,g-6)
    c: DistanceY(g-3,g2) = -2
    c: DistanceY(g2,g0) = 0
    c: DistanceX(g-3,g3) = 6.8
FEATURE [Part::Extrusion] Extrude039  label="Extrude039 supporto alimentatore"
  Base = -> Sketch036
  Dir = (0,-1,2e-16)
  DirMode = 2
  FaceMakerClass = Part::FaceMakerBullseye
  FaceMakerMode = 3
  LengthFwd = 25.2
  LengthRev = 0
  Solid = true
  Symmetric = true
FEATURE [Sketcher::SketchObject] Sketch037  label="scavo per alimentatore"
  ArcFitTolerance = 1e-06
  AttachmentSupport = -> [XZ_Plane]
  ExternalGeometry = -> [Sketch036]
  FullyConstrained = true
  MakeInternals = false
  MapMode = 5
  Placement = pos=(0,0,0) rot=(1,0,0;1.5708rad)
  sketch-geometry (4):
    g0: LineSegment StartX=-209.575 StartY=-50.4316 StartZ=0 EndX=-209.575 EndY=-80.4316 EndZ=0
    g1: LineSegment StartX=-209.575 StartY=-50.4316 StartZ=0 EndX=-207.775 EndY=-50.4316 EndZ=0
    g2: LineSegment StartX=-207.775 StartY=-50.4316 StartZ=0 EndX=-207.775 EndY=-80.4316 EndZ=0
    g3: LineSegment StartX=-207.775 StartY=-80.4316 StartZ=0 EndX=-209.575 EndY=-80.4316 EndZ=0
  constraints (11):
    c: Vertical(g0)
    c: Coincident(g1,g0)
    c: Horizontal(g1)
    c: Coincident(g2,g1)
    c: Vertical(g2)
    c: Coincident(g3,g2)
    c: Coincident(g3,g0)
    c: Horizontal(g3)
    c: DistanceX(g1,g1) = 1.8
    c: Coincident(g2,g-3)
    c: DistanceY(g2,g2) = 30
FEATURE [Part::Extrusion] Extrude040  label="Extrude040 scavo alimentatore"
  Base = -> Sketch037
  Dir = (0,-1,2e-16)
  DirMode = 2
  FaceMakerClass = Part::FaceMakerBullseye
  FaceMakerMode = 3
  LengthFwd = 19.5
  LengthRev = 0
  Solid = true
  Symmetric = true
FEATURE [Part::Extrusion] Extrude031  label="Extrude fermo per scheda micro"
  Base = -> Sketch033
  Dir = (0,-1,2e-16)
  DirMode = 2
  FaceMakerClass = Part::FaceMakerBullseye
  FaceMakerMode = 3
  LengthFwd = 3
  LengthRev = 0
  Placement = pos=(0,8.6,0) rot=(0,0,1;0rad)
  Solid = true
  Symmetric = false
FEATURE [Sketcher::SketchObject] Sketch038  label="scavo driver solenoide"
  ArcFitTolerance = 1e-06
  AttachmentSupport = -> [XZ_Plane]
  ExternalGeometry = -> [Sketch,Sketch036]
  FullyConstrained = true
  MakeInternals = false
  MapMode = 5
  Placement = pos=(0,0,0) rot=(1,0,0;1.5708rad)
  sketch-geometry (8):
    g0: LineSegment StartX=-193.575 StartY=-10.9177 StartZ=0 EndX=-196.838 EndY=-9.39626 EndZ=0
    g1: LineSegment StartX=-196.838 StartY=-9.39626 StartZ=0 EndX=-214.165 EndY=-46.5549 EndZ=0
    g2: LineSegment StartX=-193.575 StartY=-10.9177 StartZ=0 EndX=-190.131 EndY=-12.5236 EndZ=0
    g3: LineSegment StartX=-190.131 StartY=-12.5236 StartZ=0 EndX=-206.38 EndY=-47.3701 EndZ=0
    g4: LineSegment [constr] StartX=-214.165 StartY=-46.5549 StartZ=0 EndX=-210.902 EndY=-48.0763 EndZ=0
    g5: LineSegment StartX=-214.165 StartY=-46.5549 StartZ=0 EndX=-210.902 EndY=-48.0763 EndZ=0
    g6: LineSegment StartX=-206.38 StartY=-47.3701 StartZ=0 EndX=-207.775 EndY=-47.3701 EndZ=0
    g7: LineSegment StartX=-207.775 StartY=-47.3701 StartZ=0 EndX=-210.902 EndY=-48.0763 EndZ=0
  constraints (23):
    c: Coincident(g1,g0)
    c: Coincident(g3,g2)
    c: Distance(g2) = 3.8
    c: Distance(g1) = 41
    c: Coincident(g4,g1)
    c: Distance(g4) = 3.6
    c: Perpendicular(g4,g-3)
    c: Parallel(g1,g-3)
    c: Perpendicular(g1,g0)
    c: Distance(g0) = 3.6
    c: Coincident(g5,g1)
    c: Parallel(g3,g-3)
    c: Perpendicular(g2,g3)
    c: Coincident(g2,g0)
    c: PointOnObject(g4,g-3)
    c: Distance(g-3,g4) = 6.4
    c: Coincident(g6,g3)
    c: Horizontal(g6)
    c: PointOnObject(g6,g-4)
    c: Coincident(g7,g6)
    c: Coincident(g7,g5)
    c: DistanceY(g6,g-4) = 6
    c: Coincident(g5,g4)
FEATURE [Part::Extrusion] Extrude041  label="Extrude scavo driver solenoide"
  Base = -> Sketch038
  Dir = (0,-1,2e-16)
  DirMode = 2
  FaceMakerClass = Part::FaceMakerBullseye
  FaceMakerMode = 3
  LengthFwd = 20.6
  LengthRev = 0
  Solid = true
  Symmetric = true
FEATURE [Sketcher::SketchObject] Sketch039  label="scavo per cavo usb per micro"
  ArcFitTolerance = 1e-06
  AttachmentSupport = -> [XZ_Plane]
  ExternalGeometry = -> [Sketch,Sketch016]
  FullyConstrained = true
  MakeInternals = false
  MapMode = 5
  Placement = pos=(0,0,0) rot=(1,0,0;1.5708rad)
  sketch-geometry (4):
    g0: LineSegment StartX=-82.51 StartY=36.4 StartZ=0 EndX=-74.51 EndY=36.4 EndZ=0
    g1: LineSegment StartX=-74.51 StartY=36.4 StartZ=0 EndX=-74.51 EndY=30.8 EndZ=0
    g2: LineSegment StartX=-74.51 StartY=30.8 StartZ=0 EndX=-82.51 EndY=30.8 EndZ=0
    g3: LineSegment StartX=-82.51 StartY=30.8 StartZ=0 EndX=-82.51 EndY=36.4 EndZ=0
  constraints (11):
    c: Coincident(g1,g0)
    c: Vertical(g1)
    c: Coincident(g2,g1)
    c: Horizontal(g2)
    c: Coincident(g3,g2)
    c: Coincident(g3,g0)
    c: Vertical(g3)
    c: Tangent(g0,g-3)
    c: Tangent(g2,g-4)
    c: Tangent(g3,g-4)
    c: Tangent(g1,g-4)
FEATURE [Part::Extrusion] Extrude042  label="Extrude scavo per cavo usb per micro"
  Base = -> Sketch039
  Dir = (0,-1,2e-16)
  DirMode = 2
  FaceMakerClass = Part::FaceMakerBullseye
  FaceMakerMode = 3
  LengthFwd = 11.2
  LengthRev = 0
  Solid = true
  Symmetric = true
FEATURE [Sketcher::SketchObject] Sketch040  label="scavo saldature alimentatore connettore 5v"
  ArcFitTolerance = 1e-06
  AttachmentSupport = -> [XZ_Plane]
  ExternalGeometry = -> [Sketch037]
  FullyConstrained = true
  MakeInternals = false
  MapMode = 5
  Placement = pos=(0,0,0) rot=(1,0,0;1.5708rad)
  sketch-geometry (4):
    g0: LineSegment StartX=-211.175 StartY=-52.4316 StartZ=0 EndX=-211.175 EndY=-56.4316 EndZ=0
    g1: LineSegment StartX=-211.175 StartY=-52.4316 StartZ=0 EndX=-209.575 EndY=-52.4316 EndZ=0
    g2: LineSegment StartX=-209.575 StartY=-52.4316 StartZ=0 EndX=-209.575 EndY=-56.4316 EndZ=0
    g3: LineSegment StartX=-209.575 StartY=-56.4316 StartZ=0 EndX=-211.175 EndY=-56.4316 EndZ=0
  constraints (11):
    c: Vertical(g0)
    c: Coincident(g1,g0)
    c: Horizontal(g1)
    c: Coincident(g2,g1)
    c: Coincident(g3,g2)
    c: Coincident(g3,g0)
    c: Horizontal(g3)
    c: DistanceX(g1,g1) = 1.6
    c: DistanceY(g2,g2) = 4
    c: Tangent(g2,g-3)
    c: DistanceY(g1,g-3) = 2
FEATURE [Part::Extrusion] Extrude043  label="Extrude scavo saldature alimentatore connettore 5v"
  Base = -> Sketch040
  Dir = (0,-1,2e-16)
  DirMode = 2
  FaceMakerClass = Part::FaceMakerBullseye
  FaceMakerMode = 3
  LengthFwd = 8
  LengthRev = 0
  Solid = true
  Symmetric = true
FEATURE [Sketcher::SketchObject] Sketch041  label="scavo saldature alimentatore connettore 5v verticali"
  ArcFitTolerance = 1e-06
  AttachmentSupport = -> [XZ_Plane]
  ExternalGeometry = -> [Sketch037]
  FullyConstrained = true
  MakeInternals = false
  MapMode = 5
  Placement = pos=(0,0,0) rot=(1,0,0;1.5708rad)
  sketch-geometry (4):
    g0: LineSegment StartX=-211.175 StartY=-53.6316 StartZ=0 EndX=-209.575 EndY=-53.6316 EndZ=0
    g1: LineSegment StartX=-209.575 StartY=-53.6316 StartZ=0 EndX=-209.575 EndY=-76.6316 EndZ=0
    g2: LineSegment StartX=-209.575 StartY=-76.6316 StartZ=0 EndX=-211.175 EndY=-76.6316 EndZ=0
    g3: LineSegment StartX=-211.175 StartY=-76.6316 StartZ=0 EndX=-211.175 EndY=-53.6316 EndZ=0
  constraints (11):
    c: Horizontal(g0)
    c: Coincident(g1,g0)
    c: Coincident(g2,g1)
    c: Horizontal(g2)
    c: Coincident(g3,g2)
    c: Coincident(g3,g0)
    c: Vertical(g3)
    c: DistanceY(g3,g3) = 23
    c: DistanceX(g0,g0) = 1.6
    c: Tangent(g1,g-3)
    c: DistanceY(g0,g-3) = 3.2
FEATURE [Part::Extrusion] Extrude044  label="Extrude scavo saldature alimentatore connettore 5v verticali"
  Base = -> Sketch041
  Dir = (0,-1,2e-16)
  DirMode = 2
  FaceMakerClass = Part::FaceMakerBullseye
  FaceMakerMode = 3
  LengthFwd = 3.2
  LengthRev = 0
  Placement = pos=(0,8.3,0) rot=(0,0,1;0rad)
  Solid = true
  Symmetric = false
FEATURE [Sketcher::SketchObject] Sketch042  label="fermi per driver solenoide e alimentatore"
  ArcFitTolerance = 1e-06
  AttachmentSupport = -> [XZ_Plane]
  ExternalGeometry = -> [Sketch036,Sketch037,Sketch,Sketch038]
  FullyConstrained = true
  MakeInternals = false
  MapMode = 5
  Placement = pos=(0,0,0) rot=(1,0,0;1.5708rad)
  sketch-geometry (27):
    g0: LineSegment StartX=-198.308 StartY=-21.0683 StartZ=0 EndX=-199.238 EndY=-23.0622 EndZ=0
    g1: LineSegment StartX=-199.238 StartY=-23.0622 StartZ=0 EndX=-197.244 EndY=-23.992 EndZ=0
    g2: LineSegment StartX=-197.244 StartY=-23.992 StartZ=0 EndX=-196.314 EndY=-21.9981 EndZ=0
    g3: LineSegment StartX=-196.314 StartY=-21.9981 StartZ=0 EndX=-198.308 EndY=-21.0683 EndZ=0
    g4: LineSegment StartX=-199.082 StartY=-18.9421 StartZ=0 EndX=-201.364 EndY=-23.8361 EndZ=0
    g5: LineSegment StartX=-201.364 StartY=-23.8361 StartZ=0 EndX=-197.92 EndY=-25.4421 EndZ=0
    g6: LineSegment StartX=-195.794 StartY=-24.6682 StartZ=0 EndX=-194.864 EndY=-22.6743 EndZ=0
    g7: LineSegment StartX=-195.638 StartY=-20.548 StartZ=0 EndX=-199.082 EndY=-18.9421 EndZ=0
    g8: LineSegment [constr] StartX=-196.47 StartY=-26.1183 StartZ=0 EndX=-195.794 EndY=-24.6682 EndZ=0
    g9: LineSegment [constr] StartX=-196.47 StartY=-26.1183 StartZ=0 EndX=-197.92 EndY=-25.4421 EndZ=0
    g10: ArcOfCircle CenterX=-196.314 CenterY=-21.9981 CenterZ=0 NormalX=0 NormalY=0 NormalZ=1 AngleXU=0 Radius=1.6 StartAngle=5.84685 EndAngle=7.41765
    g11: GeomPoint [constr] X=-194.188 Y=-21.2242 Z=0
    g12: ArcOfCircle CenterX=-197.244 CenterY=-23.992 CenterZ=0 NormalX=0 NormalY=0 NormalZ=1 AngleXU=0 Radius=1.6 StartAngle=4.27606 EndAngle=5.84685
    g13: GeomPoint [constr] X=-196.47 Y=-26.1183 Z=0
    g14: LineSegment StartX=-207.775 StartY=-46.8316 StartZ=0 EndX=-207.775 EndY=-50.8316 EndZ=0
    g15: LineSegment StartX=-207.775 StartY=-46.8316 StartZ=0 EndX=-203.775 EndY=-46.8316 EndZ=0
    g16: LineSegment StartX=-203.775 StartY=-46.8316 StartZ=0 EndX=-203.775 EndY=-50.8316 EndZ=0
    g17: LineSegment StartX=-207.775 StartY=-50.8316 StartZ=0 EndX=-203.775 EndY=-50.8316 EndZ=0
    g18: LineSegment StartX=-209.375 StartY=-52.4316 StartZ=0 EndX=-203.775 EndY=-52.4316 EndZ=0
    g19: LineSegment StartX=-202.175 StartY=-50.8316 StartZ=0 EndX=-202.175 EndY=-46.8316 EndZ=0
    g20: LineSegment StartX=-203.775 StartY=-45.2316 StartZ=0 EndX=-209.375 EndY=-45.2316 EndZ=0
    g21: LineSegment StartX=-209.375 StartY=-45.2316 StartZ=0 EndX=-209.375 EndY=-52.4316 EndZ=0
    g22: ArcOfCircle CenterX=-203.775 CenterY=-46.8316 CenterZ=0 NormalX=0 NormalY=0 NormalZ=1 AngleXU=0 Radius=1.6 StartAngle=1.8e-15 EndAngle=1.5708
    g23: GeomPoint [constr] X=-202.175 Y=-45.2316 Z=0
    g24: ArcOfCircle CenterX=-203.775 CenterY=-50.8316 CenterZ=0 NormalX=0 NormalY=0 NormalZ=1 AngleXU=0 Radius=1.6 StartAngle=4.71239 EndAngle=6.28319
    g25: GeomPoint [constr] X=-202.175 Y=-52.4316 Z=0
    g26: LineSegment [constr] StartX=-207.775 StartY=-50.4316 StartZ=0 EndX=-207.775 EndY=-50.8316 EndZ=0
  constraints (69):
    c: Coincident(g1,g0)
    c: Coincident(g2,g1)
    c: Coincident(g3,g2)
    c: Coincident(g3,g0)
    c: Parallel(g0,g2)
    c: Perpendicular(g3,g0)
    c: Perpendicular(g1,g0)
    c: Coincident(g5,g4)
    c: Coincident(g7,g4)
    c: Distance(g3) = 2.2
    c: Distance(g2) = 2.2
    c: Parallel(g6,g2)
    c: Parallel(g6,g4)
    c: Perpendicular(g5,g6)
    c: Perpendicular(g7,g6)
    c: Distance(g13,g11) = 5.4
    c: Distance(g5,g13) = 5.4
    c: Coincident(g9,g8)
    c: Distance(g8) = 1.6
    c: Distance(g9) = 1.6
    c: Perpendicular(g9,g8)
    c: Parallel(g8,g6)
    c: Coincident(g8,g13)
    c: Distance(g8,g1) = 1.6
    c: Distance(g9,g1) = 1.6
    c: Tangent(g0,g-5)
    c: Distance(g0,g-6) = 27.6
    c: PointOnObject(g11,g7)
    c: PointOnObject(g11,g6)
    c: Tangent(g7,g10) = -1.5708
    c: Tangent(g6,g10) = -1.5708
    c: PointOnObject(g13,g5)
    c: Tangent(g5,g12) = -1.5708
    c: Tangent(g6,g12) = -1.5708
    c: Equal(g10,g12)
    c: Coincident(g10,g2)
    c: Vertical(g14)
    c: Coincident(g15,g14)
    c: Horizontal(g15)
    c: Coincident(g16,g15)
    c: Vertical(g16)
    c: Coincident(g17,g14)
    c: Coincident(g17,g16)
    c: Horizontal(g17)
    c: Distance(g16) = 4
    c: Distance(g15) = 4
    c: Horizontal(g18)
    c: Vertical(g19)
    c: Horizontal(g20)
    c: Coincident(g21,g20)
    c: Coincident(g21,g18)
    c: Vertical(g21)
    c: Distance(g20,g23) = 7.2
    c: Distance(g25,g23) = 7.2
    c: DistanceY(g18,g14) = 1.6
    c: DistanceX(g18,g14) = 1.6
    c: PointOnObject(g23,g20)
    c: PointOnObject(g23,g19)
    c: Tangent(g20,g22) = -1.5708
    c: Tangent(g19,g22) = -1.5708
    c: PointOnObject(g25,g19)
    c: Tangent(g18,g24) = -1.5708
    c: Tangent(g19,g24) = -1.5708
    c: Equal(g22,g24)
    c: Coincident(g22,g15)
    c: Vertical(g26)
    c: Distance(g26) = 0.4
    c: Coincident(g26,g-4)
    c: Coincident(g14,g26)
FEATURE [Part::Extrusion] Extrude045  label="Extrude fermi per driver solenoide e alimentatore"
  Base = -> Sketch042
  Dir = (0,-1,2e-16)
  DirMode = 2
  FaceMakerClass = Part::FaceMakerBullseye
  FaceMakerMode = 3
  LengthFwd = 25.2
  LengthRev = 0
  Solid = true
  Symmetric = true
FEATURE [Sketcher::SketchObject] Sketch043  label="scavo pulizia fermo alimentatore"
  ArcFitTolerance = 1e-06
  AttachmentSupport = -> [XZ_Plane]
  ExternalGeometry = -> [Sketch042,Sketch036,Sketch037]
  FullyConstrained = true
  MakeInternals = false
  MapMode = 5
  Placement = pos=(0,0,0) rot=(1,0,0;1.5708rad)
  sketch-geometry (6):
    g0: LineSegment StartX=-209.375 StartY=-52.4316 StartZ=0 EndX=-209.375 EndY=-50.4316 EndZ=0
    g1: LineSegment StartX=-209.375 StartY=-50.4316 StartZ=0 EndX=-207.775 EndY=-50.4316 EndZ=0
    g2: LineSegment StartX=-207.775 StartY=-50.4316 StartZ=0 EndX=-207.775 EndY=-45.2316 EndZ=0
    g3: LineSegment StartX=-207.775 StartY=-45.2316 StartZ=0 EndX=-202.175 EndY=-45.2316 EndZ=0
    g4: LineSegment StartX=-202.175 StartY=-45.2316 StartZ=0 EndX=-202.175 EndY=-52.4316 EndZ=0
    g5: LineSegment StartX=-202.175 StartY=-52.4316 StartZ=0 EndX=-209.375 EndY=-52.4316 EndZ=0
  constraints (13):
    c: Vertical(g0)
    c: Coincident(g1,g0)
    c: Coincident(g2,g1)
    c: Coincident(g3,g2)
    c: Coincident(g4,g3)
    c: Coincident(g5,g4)
    c: Coincident(g5,g0)
    c: Horizontal(g5)
    c: Coincident(g0,g-6)
    c: Tangent(g1,g-8)
    c: Tangent(g2,g-4)
    c: Tangent(g3,g-7)
    c: Tangent(g4,g-3)
FEATURE [Part::Extrusion] Extrude046  label="Extrude scavo pulizia fermo alimentatore"
  Base = -> Sketch043
  Dir = (0,-1,2e-16)
  DirMode = 2
  FaceMakerClass = Part::FaceMakerBullseye
  FaceMakerMode = 3
  LengthFwd = 19.5
  LengthRev = 0
  Solid = true
  Symmetric = true
FEATURE [Sketcher::SketchObject] Sketch044  label="buchini per fissaggio oled"
  ArcFitTolerance = 1e-06
  AttachmentSupport = -> [YZ_Plane]
  ExternalGeometry = -> [Sketch]
  FullyConstrained = true
  MakeInternals = false
  MapMode = 5
  Placement = pos=(0,0,0) rot=(0.57735,0.57735,0.57735;2.0944rad)
  sketch-geometry (5):
    g0: LineSegment [constr] StartX=1.5e-14 StartY=67.3588 StartZ=0 EndX=0 EndY=64.3588 EndZ=0
    g1: LineSegment [constr] StartX=0 StartY=64.3588 StartZ=0 EndX=10.4 EndY=64.3588 EndZ=0
    g2: LineSegment [constr] StartX=0 StartY=64.3588 StartZ=0 EndX=-10.4 EndY=64.3588 EndZ=0
    g3: Circle CenterX=10.4 CenterY=64.3588 CenterZ=0 NormalX=0 NormalY=0 NormalZ=1 AngleXU=0 Radius=1.5
    g4: Circle CenterX=-10.4 CenterY=64.3588 CenterZ=0 NormalX=0 NormalY=0 NormalZ=1 AngleXU=0 Radius=1.5
  constraints (13):
    c: Distance(g0) = 3
    c: PointOnObject(g0,g-2)
    c: Coincident(g1,g0)
    c: Horizontal(g1)
    c: Coincident(g2,g0)
    c: Horizontal(g2)
    c: DistanceX(g1,g1) = 10.4
    c: Coincident(g3,g1)
    c: Diameter(g4) = 3
    c: Coincident(g4,g2)
    c: Coincident(g0,g-7)
    c: Equal(g1,g2)
    c: Equal(g4,g3)
FEATURE [Part::Extrusion] Extrude047  label="Extrude buchini per fissaggio oled"
  Base = -> Sketch044
  Dir = (1,0,0)
  DirMode = 2
  FaceMakerClass = Part::FaceMakerBullseye
  FaceMakerMode = 3
  LengthFwd = 10
  LengthRev = 0
  Placement = pos=(-186,0,0) rot=(0,0,1;0rad)
  Solid = true
  Symmetric = false
FEATURE [Sketcher::SketchObject] Sketch046  label="scavo 5x5 neopixel"
  ArcFitTolerance = 1e-06
  AttachmentSupport = -> [YZ_Plane002]
  FullyConstrained = true
  MakeInternals = false
  MapMode = 5
  Placement = pos=(0,0,0) rot=(0.57735,0.57735,0.57735;2.0944rad)
  sketch-geometry (4):
    g0: LineSegment StartX=-2.7 StartY=2.7 StartZ=0 EndX=2.7 EndY=2.7 EndZ=0
    g1: LineSegment StartX=2.7 StartY=2.7 StartZ=0 EndX=2.7 EndY=-2.7 EndZ=0
    g2: LineSegment StartX=2.7 StartY=-2.7 StartZ=0 EndX=-2.7 EndY=-2.7 EndZ=0
    g3: LineSegment StartX=-2.7 StartY=-2.7 StartZ=0 EndX=-2.7 EndY=2.7 EndZ=0
  constraints (11):
    c: Horizontal(g0)
    c: Coincident(g1,g0)
    c: Vertical(g1)
    c: Coincident(g2,g1)
    c: Horizontal(g2)
    c: Coincident(g3,g2)
    c: Coincident(g3,g0)
    c: Vertical(g3)
    c: DistanceX(g0,g0) = 5.4
    c: DistanceY(g1,g1) = 5.4
    c: Symmetric(g0,g1,g-1)
FEATURE [Sketcher::SketchObject] Sketch047  label="scavo 10x10 neopixel corpo"
  ArcFitTolerance = 1e-06
  AttachmentOffset = pos=(0,0,1) rot=(0,0,1;0rad)
  AttachmentSupport = -> [YZ_Plane002]
  FullyConstrained = true
  MakeInternals = false
  MapMode = 5
  Placement = pos=(1,0,0) rot=(0.57735,0.57735,0.57735;2.0944rad)
  sketch-geometry (4):
    g0: LineSegment StartX=-5 StartY=5.1 StartZ=0 EndX=5 EndY=5.1 EndZ=0
    g1: LineSegment StartX=5 StartY=5.1 StartZ=0 EndX=5 EndY=-5.1 EndZ=0
    g2: LineSegment StartX=5 StartY=-5.1 StartZ=0 EndX=-5 EndY=-5.1 EndZ=0
    g3: LineSegment StartX=-5 StartY=-5.1 StartZ=0 EndX=-5 EndY=5.1 EndZ=0
  constraints (11):
    c: Horizontal(g0)
    c: Coincident(g1,g0)
    c: Vertical(g1)
    c: Coincident(g2,g1)
    c: Horizontal(g2)
    c: Coincident(g3,g2)
    c: Coincident(g3,g0)
    c: Vertical(g3)
    c: DistanceX(g0,g0) = 10
    c: DistanceY(g1,g1) = 10.2
    c: Symmetric(g0,g2,g-1)
FEATURE [Sketcher::SketchObject] Sketch048  label="buco per perno blocco neopixel"
  ArcFitTolerance = 1e-06
  AttachmentSupport = -> [XZ_Plane002]
  FullyConstrained = true
  MakeInternals = false
  MapMode = 5
  Placement = pos=(0,0,0) rot=(1,0,0;1.5708rad)
  sketch-geometry (4):
    g0: LineSegment StartX=3 StartY=1.2 StartZ=0 EndX=3 EndY=-1.2 EndZ=0
    g1: LineSegment StartX=3 StartY=-1.2 StartZ=0 EndX=5.4 EndY=-1.2 EndZ=0
    g2: LineSegment StartX=5.4 StartY=-1.2 StartZ=0 EndX=5.4 EndY=1.2 EndZ=0
    g3: LineSegment StartX=5.4 StartY=1.2 StartZ=0 EndX=3 EndY=1.2 EndZ=0
  constraints (11):
    c: Coincident(g1,g0)
    c: Horizontal(g1)
    c: Coincident(g2,g1)
    c: Vertical(g2)
    c: Coincident(g3,g2)
    c: Coincident(g3,g0)
    c: Horizontal(g3)
    c: DistanceX(g1,g1) = 2.4
    c: DistanceY(g2,g2) = 2.4
    c: Symmetric(g0,g0,g-1)
    c: DistanceX(g-1,g0) = 3
FEATURE [Sketcher::SketchObject] Sketch045  label="blocco principale per neopixel"
  ArcFitTolerance = 1e-06
  AttachmentSupport = -> [XZ_Plane002]
  ExternalGeometry = -> [Sketch048]
  FullyConstrained = true
  MakeInternals = false
  MapMode = 5
  Placement = pos=(0,0,0) rot=(1,0,0;1.5708rad)
  sketch-geometry (6):
    g0: LineSegment StartX=0 StartY=5.1 StartZ=0 EndX=0 EndY=-5.1 EndZ=0
    g1: LineSegment StartX=0 StartY=-5.1 StartZ=0 EndX=3 EndY=-5.1 EndZ=0
    g2: LineSegment StartX=7 StartY=-1.1 StartZ=0 EndX=7 EndY=5.1 EndZ=0
    g3: LineSegment StartX=7 StartY=5.1 StartZ=0 EndX=0 EndY=5.1 EndZ=0
    g4: ArcOfCircle CenterX=3 CenterY=-1.1 CenterZ=0 NormalX=0 NormalY=0 NormalZ=1 AngleXU=0 Radius=4 StartAngle=4.71239 EndAngle=6.28319
    g5: GeomPoint [constr] X=7 Y=-5.1 Z=0
  constraints (15):
    c: Vertical(g0)
    c: Coincident(g1,g0)
    c: Horizontal(g1)
    c: Vertical(g2)
    c: Coincident(g3,g2)
    c: Coincident(g3,g0)
    c: Horizontal(g3)
    c: DistanceY(g0,g0) = 10.2
    c: Symmetric(g0,g0,g-1)
    c: DistanceX(g3,g3) = 7
    c: PointOnObject(g5,g2)
    c: PointOnObject(g5,g1)
    c: Tangent(g2,g4) = -1.5708
    c: Tangent(g1,g4) = -1.5708
    c: DistanceX(g-3,g1) = 0
FEATURE [Sketcher::SketchObject] Sketch049  label="rinforzi esterni per corpo neopoixel"
  ArcFitTolerance = 1e-06
  AttachmentSupport = -> [XZ_Plane002]
  ExternalGeometry = -> [Sketch045]
  FullyConstrained = true
  MakeInternals = false
  MapMode = 5
  Placement = pos=(0,0,0) rot=(1,0,0;1.5708rad)
  sketch-geometry (8):
    g0: LineSegment StartX=1 StartY=-4.1 StartZ=0 EndX=2 EndY=-4.1 EndZ=0
    g1: LineSegment StartX=2 StartY=-4.1 StartZ=0 EndX=2 EndY=-5.1 EndZ=0
    g2: LineSegment StartX=2 StartY=-5.1 StartZ=0 EndX=1 EndY=-5.1 EndZ=0
    g3: LineSegment StartX=1 StartY=-5.1 StartZ=0 EndX=1 EndY=-4.1 EndZ=0
    g4: LineSegment StartX=1 StartY=5.1 StartZ=0 EndX=2 EndY=5.1 EndZ=0
    g5: LineSegment StartX=2 StartY=5.1 StartZ=0 EndX=2 EndY=4.1 EndZ=0
    g6: LineSegment StartX=2 StartY=4.1 StartZ=0 EndX=1 EndY=4.1 EndZ=0
    g7: LineSegment StartX=1 StartY=4.1 StartZ=0 EndX=1 EndY=5.1 EndZ=0
  constraints (24):
    c: Horizontal(g0)
    c: Coincident(g1,g0)
    c: Vertical(g1)
    c: Coincident(g2,g1)
    c: Horizontal(g2)
    c: Coincident(g3,g2)
    c: Coincident(g3,g0)
    c: Vertical(g3)
    c: Horizontal(g4)
    c: Coincident(g5,g4)
    c: Vertical(g5)
    c: Coincident(g6,g5)
    c: Horizontal(g6)
    c: Coincident(g7,g6)
    c: Coincident(g7,g4)
    c: Vertical(g7)
    c: DistanceX(g4,g4) = 1
    c: DistanceY(g5,g5) = 1
    c: DistanceX(g0,g0) = 1
    c: DistanceY(g1,g1) = 1
    c: DistanceX(g-3,g4) = 1
    c: DistanceY(g-3,g4) = 0
    c: DistanceX(g-4,g2) = 1
    c: DistanceY(g2,g-4) = 0
FEATURE [Sketcher::SketchObject] Sketch052  label="scavo saldature driver solenoide"
  ArcFitTolerance = 1e-06
  AttachmentSupport = -> [XZ_Plane]
  ExternalGeometry = -> [Sketch038]
  FullyConstrained = true
  MakeInternals = false
  MapMode = 5
  Placement = pos=(0,0,0) rot=(1,0,0;1.5708rad)
  sketch-geometry (4):
    g0: LineSegment StartX=-197.2 StartY=-9.22721 StartZ=0 EndX=-198.891 EndY=-12.8524 EndZ=0
    g1: LineSegment StartX=-198.891 StartY=-12.8524 StartZ=0 EndX=-198.528 EndY=-13.0215 EndZ=0
    g2: LineSegment StartX=-198.528 StartY=-13.0215 StartZ=0 EndX=-196.838 EndY=-9.39626 EndZ=0
    g3: LineSegment StartX=-196.838 StartY=-9.39626 StartZ=0 EndX=-197.2 EndY=-9.22721 EndZ=0
  constraints (11):
    c: Coincident(g1,g0)
    c: Coincident(g2,g1)
    c: Coincident(g3,g2)
    c: Coincident(g3,g0)
    c: Parallel(g2,g0)
    c: Perpendicular(g2,g3)
    c: Perpendicular(g1,g2,g1) = 1.5708
    c: Parallel(g2,g-3)
    c: Distance(g2) = 4
    c: Distance(g3) = 0.4
    c: Coincident(g2,g-3)
FEATURE [Part::Extrusion] Extrude055  label="Extrude scavo saldature driver solenoide"
  Base = -> Sketch052
  Dir = (0,-1,2e-16)
  DirMode = 2
  FaceMakerClass = Part::FaceMakerBullseye
  FaceMakerMode = 3
  LengthFwd = 6
  LengthRev = 0
  Solid = true
  Symmetric = true
FEATURE [Sketcher::SketchObject] Sketch053  label="scavo saldature rumble"
  ArcFitTolerance = 1e-06
  AttachmentSupport = -> [XZ_Plane]
  ExternalGeometry = -> [Sketch019]
  FullyConstrained = true
  MakeInternals = false
  MapMode = 5
  Placement = pos=(0,0,0) rot=(1,0,0;1.5708rad)
  sketch-geometry (4):
    g0: LineSegment StartX=-169.451 StartY=-56.8615 StartZ=0 EndX=-170.687 EndY=-60.6657 EndZ=0
    g1: LineSegment StartX=-170.687 StartY=-60.6657 StartZ=0 EndX=-169.546 EndY=-61.0365 EndZ=0
    g2: LineSegment StartX=-169.546 StartY=-61.0365 StartZ=0 EndX=-168.31 EndY=-57.2323 EndZ=0
    g3: LineSegment StartX=-168.31 StartY=-57.2323 StartZ=0 EndX=-169.451 EndY=-56.8615 EndZ=0
  constraints (11):
    c: Coincident(g1,g0)
    c: Coincident(g2,g1)
    c: Coincident(g3,g2)
    c: Coincident(g3,g0)
    c: Parallel(g0,g2)
    c: Perpendicular(g3,g0)
    c: Perpendicular(g1,g0)
    c: Parallel(g0,g-3)
    c: Distance(g0) = 4
    c: Coincident(g0,g-3)
    c: Distance(g1) = 1.2
FEATURE [Part::Extrusion] Extrude056  label="Extrude scavo saldature rumble"
  Base = -> Sketch053
  Dir = (0,-1,2e-16)
  DirMode = 2
  FaceMakerClass = Part::FaceMakerBullseye
  FaceMakerMode = 3
  LengthFwd = 8.4
  LengthRev = 0
  Solid = true
  Symmetric = true
FEATURE [Sketcher::SketchObject] Sketch054  label="scavo saldature alimentatore connettore USB"
  ArcFitTolerance = 1e-06
  AttachmentSupport = -> [XZ_Plane]
  ExternalGeometry = -> [Sketch037]
  FullyConstrained = true
  MakeInternals = false
  MapMode = 5
  Placement = pos=(0,0,0) rot=(1,0,0;1.5708rad)
  sketch-geometry (4):
    g0: LineSegment StartX=-209.575 StartY=-80.4316 StartZ=0 EndX=-210.375 EndY=-80.4316 EndZ=0
    g1: LineSegment StartX=-210.375 StartY=-80.4316 StartZ=0 EndX=-210.375 EndY=-72.4316 EndZ=0
    g2: LineSegment StartX=-210.375 StartY=-72.4316 StartZ=0 EndX=-209.575 EndY=-72.4316 EndZ=0
    g3: LineSegment StartX=-209.575 StartY=-72.4316 StartZ=0 EndX=-209.575 EndY=-80.4316 EndZ=0
  constraints (11):
    c: Horizontal(g0)
    c: Coincident(g1,g0)
    c: Vertical(g1)
    c: Coincident(g2,g1)
    c: Horizontal(g2)
    c: Coincident(g3,g2)
    c: Coincident(g3,g0)
    c: Vertical(g3)
    c: DistanceX(g0,g0) = 0.8
    c: DistanceY(g3,g3) = 8
    c: Coincident(g0,g-4)
FEATURE [Part::Extrusion] Extrude057  label="Extrude scavo saldature alimentatore connettore USB"
  Base = -> Sketch054
  Dir = (0,-1,2e-16)
  DirMode = 2
  FaceMakerClass = Part::FaceMakerBullseye
  FaceMakerMode = 3
  LengthFwd = 11
  LengthRev = 0
  Solid = true
  Symmetric = true
FEATURE [Sketcher::SketchObject] Sketch055  label="buco interno per micro switch"
  ArcFitTolerance = 1e-06
  AttachmentSupport = -> [XZ_Plane]
  ExternalGeometry = -> [Sketch]
  FullyConstrained = true
  MakeInternals = false
  MapMode = 5
  Placement = pos=(0,0,0) rot=(1,0,0;1.5708rad)
  sketch-geometry (11):
    g0: LineSegment [constr] StartX=-194.483 StartY=34.2854 StartZ=0 EndX=-196.022 EndY=30.0568 EndZ=0
    g1: LineSegment [constr] StartX=-196.022 StartY=30.0568 StartZ=0 EndX=-197.561 EndY=25.8282 EndZ=0
    g2: LineSegment [constr] StartX=-196.022 StartY=30.0568 StartZ=0 EndX=-194.143 EndY=29.3727 EndZ=0
    g3: LineSegment [constr] StartX=-196.022 StartY=30.0568 StartZ=0 EndX=-197.902 EndY=30.7408 EndZ=0
    g4: LineSegment StartX=-196.362 StartY=34.9694 StartZ=0 EndX=-192.604 EndY=33.6014 EndZ=0
    g5: LineSegment StartX=-199.441 StartY=26.5122 StartZ=0 EndX=-195.682 EndY=25.1441 EndZ=0
    g6: LineSegment StartX=-192.604 StartY=33.6014 StartZ=0 EndX=-195.682 EndY=25.1441 EndZ=0
    g7: LineSegment StartX=-196.362 StartY=34.9694 StartZ=0 EndX=-199.441 EndY=26.5122 EndZ=0
    g8: GeomPoint [constr] X=-187.821 Y=29.2 Z=0
    g9: LineSegment [constr] StartX=-188.505 StartY=27.3206 StartZ=0 EndX=-196.022 EndY=30.0568 EndZ=0
    g10: LineSegment [constr] StartX=-187.821 StartY=29.2 StartZ=0 EndX=-188.505 EndY=27.3206 EndZ=0
  constraints (27):
    c: Coincident(g2,g0)
    c: Parallel(g0,g-3)
    c: Tangent(g1,g0) = -1.5708
    c: Perpendicular(g0,g2)
    c: Tangent(g2,g3)
    c: Distance(g0,g1) = 9
    c: Equal(g0,g1)
    c: Distance(g3,g2) = 4
    c: Equal(g2,g3)
    c: Parallel(g3,g4)
    c: Symmetric(g4,g4,g0)
    c: Parallel(g6,g1)
    c: Parallel(g7,g1)
    c: Symmetric(g6,g6,g2)
    c: Symmetric(g5,g5,g1)
    c: Symmetric(g7,g7,g3)
    c: Coincident(g7,g4)
    c: Coincident(g6,g4)
    c: Coincident(g5,g6)
    c: Symmetric(g-3,g-3,g8)
    c: Perpendicular(g-3,g9)
    c: Distance(g9) = 8
    c: Coincident(g3,g9)
    c: Coincident(g10,g8)
    c: Parallel(g10,g-3)
    c: Distance(g10) = 2
    c: Coincident(g10,g9)
FEATURE [Sketcher::SketchObject] Sketch056  label="buco esterno per micro switch"
  ArcFitTolerance = 1e-06
  AttachmentSupport = -> [XZ_Plane]
  ExternalGeometry = -> [Sketch055]
  FullyConstrained = true
  MakeInternals = false
  MapMode = 5
  Placement = pos=(0,0,0) rot=(1,0,0;1.5708rad)
  sketch-geometry (17):
    g0: GeomPoint [constr] X=-194.143 Y=29.3727 Z=0
    g1: GeomPoint [constr] X=-194.483 Y=34.2854 Z=0
    g2: GeomPoint [constr] X=-197.902 Y=30.7408 Z=0
    g3: GeomPoint [constr] X=-197.561 Y=25.8282 Z=0
    g4: GeomPoint [constr] X=-196.022 Y=30.0568 Z=0
    g5: LineSegment [constr] StartX=-194.483 StartY=34.2854 StartZ=0 EndX=-196.022 EndY=30.0568 EndZ=0
    g6: LineSegment [constr] StartX=-196.022 StartY=30.0568 StartZ=0 EndX=-197.561 EndY=25.8282 EndZ=0
    g7: LineSegment [constr] StartX=-197.902 StartY=30.7408 StartZ=0 EndX=-196.022 EndY=30.0568 EndZ=0
    g8: LineSegment [constr] StartX=-196.022 StartY=30.0568 StartZ=0 EndX=-194.143 EndY=29.3727 EndZ=0
    g9: LineSegment [constr] StartX=-195.338 StartY=31.9362 StartZ=0 EndX=-196.022 EndY=30.0568 EndZ=0
    g10: LineSegment [constr] StartX=-196.022 StartY=30.0568 StartZ=0 EndX=-196.706 EndY=28.1774 EndZ=0
    g11: LineSegment [constr] StartX=-196.022 StartY=30.0568 StartZ=0 EndX=-196.821 EndY=30.3475 EndZ=0
    g12: LineSegment [constr] StartX=-196.022 StartY=30.0568 StartZ=0 EndX=-195.223 EndY=29.7661 EndZ=0
    g13: LineSegment StartX=-194.539 StartY=31.6454 StartZ=0 EndX=-195.907 EndY=27.8867 EndZ=0
    g14: LineSegment StartX=-196.137 StartY=32.2269 StartZ=0 EndX=-197.505 EndY=28.4681 EndZ=0
    g15: LineSegment StartX=-196.137 StartY=32.2269 StartZ=0 EndX=-194.539 EndY=31.6454 EndZ=0
    g16: LineSegment StartX=-197.505 StartY=28.4681 StartZ=0 EndX=-195.907 EndY=27.8867 EndZ=0
  constraints (34):
    c: Symmetric(g-5,g-5,g1)
    c: Symmetric(g-5,g-6,g0)
    c: Symmetric(g-6,g-6,g3)
    c: Symmetric(g-5,g-6,g2)
    c: Coincident(g5,g1)
    c: Coincident(g5,g4)
    c: Coincident(g6,g4)
    c: Coincident(g6,g3)
    c: Equal(g5,g6)
    c: Coincident(g7,g2)
    c: Coincident(g7,g4)
    c: Coincident(g8,g4)
    c: Coincident(g8,g0)
    c: Equal(g7,g8)
    c: Coincident(g11,g9)
    c: Coincident(g12,g9)
    c: Tangent(g10,g9) = -1.5708
    c: Perpendicular(g11,g9)
    c: Parallel(g9,g-4)
    c: Equal(g9,g10)
    c: Parallel(g12,g11)
    c: Equal(g11,g12)
    c: Distance(g11,g12) = 1.7
    c: Distance(g9,g10) = 4
    c: Symmetric(g13,g13,g12)
    c: Parallel(g13,g9)
    c: Symmetric(g14,g14,g11)
    c: Symmetric(g15,g15,g9)
    c: Parallel(g15,g11)
    c: Symmetric(g16,g16,g10)
    c: Coincident(g16,g14)
    c: Coincident(g15,g14)
    c: Coincident(g13,g15)
    c: Coincident(g9,g4)
FEATURE [Sketcher::SketchObject] Sketch057  label="buco interno per SWITCH"
  ArcFitTolerance = 1e-06
  AttachmentSupport = -> [XZ_Plane]
  ExternalGeometry = -> [Sketch]
  FullyConstrained = true
  MakeInternals = false
  MapMode = 5
  Placement = pos=(0,0,0) rot=(1,0,0;1.5708rad)
  sketch-geometry (10):
    g0: GeomPoint [constr] X=-187.821 Y=29.2 Z=0
    g1: LineSegment [constr] StartX=-188.505 StartY=27.3206 StartZ=0 EndX=-193.203 EndY=29.0307 EndZ=0
    g2: LineSegment [constr] StartX=-190.809 StartY=35.6086 StartZ=0 EndX=-195.597 EndY=22.4529 EndZ=0
    g3: GeomPoint [constr] X=-193.203 Y=29.0307 Z=0
    g4: LineSegment [constr] StartX=-196.492 StartY=30.2278 StartZ=0 EndX=-189.914 EndY=27.8336 EndZ=0
    g5: LineSegment StartX=-194.098 StartY=36.8056 StartZ=0 EndX=-187.52 EndY=34.4115 EndZ=0
    g6: LineSegment StartX=-194.098 StartY=36.8056 StartZ=0 EndX=-198.886 EndY=23.6499 EndZ=0
    g7: LineSegment StartX=-187.52 StartY=34.4115 StartZ=0 EndX=-192.308 EndY=21.2558 EndZ=0
    g8: LineSegment StartX=-198.886 StartY=23.6499 StartZ=0 EndX=-192.308 EndY=21.2558 EndZ=0
    g9: LineSegment [constr] StartX=-187.821 StartY=29.2 StartZ=0 EndX=-188.505 EndY=27.3206 EndZ=0
  constraints (23):
    c: Symmetric(g-3,g-3,g0)
    c: Perpendicular(g1,g-3)
    c: Parallel(g2,g-3)
    c: Symmetric(g2,g2,g3)
    c: Perpendicular(g2,g4)
    c: Symmetric(g4,g4,g3)
    c: Distance(g2) = 14
    c: Distance(g4) = 7
    c: Distance(g1) = 5
    c: Parallel(g5,g4)
    c: Parallel(g7,g2)
    c: Symmetric(g5,g5,g2)
    c: Symmetric(g6,g6,g4)
    c: Symmetric(g7,g7,g4)
    c: Symmetric(g8,g8,g2)
    c: Coincident(g6,g5)
    c: Coincident(g7,g5)
    c: Coincident(g8,g7)
    c: Coincident(g3,g1)
    c: Coincident(g9,g0)
    c: Parallel(g9,g-3)
    c: Distance(g9) = 2
    c: Coincident(g1,g9)
FEATURE [Sketcher::SketchObject] Sketch058  label="buco esterno per SWITCH"
  ArcFitTolerance = 1e-06
  AttachmentSupport = -> [XZ_Plane]
  ExternalGeometry = -> [Sketch057]
  FullyConstrained = true
  MakeInternals = false
  MapMode = 5
  Placement = pos=(0,0,0) rot=(1,0,0;1.5708rad)
  sketch-geometry (12):
    g0: GeomPoint [constr] X=-190.809 Y=35.6086 Z=0
    g1: GeomPoint [constr] X=-196.492 Y=30.2278 Z=0
    g2: GeomPoint [constr] X=-189.914 Y=27.8336 Z=0
    g3: GeomPoint [constr] X=-195.597 Y=22.4529 Z=0
    g4: GeomPoint [constr] X=-193.203 Y=29.0307 Z=0
    g5: LineSegment [constr] StartX=-192.006 StartY=32.3196 StartZ=0 EndX=-194.4 EndY=25.7418 EndZ=0
    g6: GeomPoint [constr] X=-193.203 Y=29.0307 Z=0
    g7: LineSegment [constr] StartX=-195.082 StartY=29.7148 StartZ=0 EndX=-191.324 EndY=28.3467 EndZ=0
    g8: LineSegment StartX=-193.885 StartY=33.0037 StartZ=0 EndX=-190.127 EndY=31.6356 EndZ=0
    g9: LineSegment StartX=-190.127 StartY=31.6356 StartZ=0 EndX=-192.521 EndY=25.0578 EndZ=0
    g10: LineSegment StartX=-196.28 StartY=26.4258 StartZ=0 EndX=-192.521 EndY=25.0578 EndZ=0
    g11: LineSegment StartX=-193.885 StartY=33.0037 StartZ=0 EndX=-196.28 EndY=26.4258 EndZ=0
  constraints (21):
    c: Symmetric(g-6,g-6,g3)
    c: Symmetric(g-4,g-6,g2)
    c: Symmetric(g-5,g-4,g0)
    c: Symmetric(g-5,g-6,g1)
    c: Symmetric(g1,g2,g4)
    c: Parallel(g5,g-4)
    c: Symmetric(g5,g5,g6)
    c: Perpendicular(g7,g5)
    c: Symmetric(g7,g7,g6)
    c: Distance(g5) = 7
    c: Distance(g7) = 4
    c: Parallel(g8,g7)
    c: Parallel(g11,g5)
    c: Symmetric(g8,g8,g5)
    c: Symmetric(g9,g9,g7)
    c: Symmetric(g10,g10,g5)
    c: Symmetric(g11,g11,g7)
    c: Coincident(g11,g8)
    c: Coincident(g9,g8)
    c: Coincident(g9,g10)
    c: Coincident(g6,g4)
FEATURE [Part::Extrusion] Extrude060  label="Extrude buco interno per SWITCH destro"
  Base = -> Sketch057
  Dir = (0,-1,2e-16)
  DirMode = 2
  FaceMakerClass = Part::FaceMakerBullseye
  FaceMakerMode = 3
  LengthFwd = 13.2
  LengthRev = 0
  Placement = pos=(0,2.6,0) rot=(0,0,1;0rad)
  Solid = true
  Symmetric = false
FEATURE [Part::Extrusion] Extrude061  label="Extrude buco esterno per SWITCH destro"
  Base = -> Sketch058
  Dir = (0,-1,2e-16)
  DirMode = 2
  FaceMakerClass = Part::FaceMakerBullseye
  FaceMakerMode = 3
  LengthFwd = 2
  LengthRev = 0
  Placement = pos=(0,-10.6,0) rot=(0,0,1;0rad)
  Solid = true
  Symmetric = false
FEATURE [Sketcher::SketchObject] Sketch059  label="buco per spazio introduzione SWITCH"
  ArcFitTolerance = 1e-06
  AttachmentSupport = -> [XZ_Plane]
  ExternalGeometry = -> [Sketch057,Sketch010]
  FullyConstrained = true
  MakeInternals = false
  MapMode = 5
  Placement = pos=(0,0,0) rot=(1,0,0;1.5708rad)
  sketch-geometry (8):
    g0: LineSegment [constr] StartX=-201.368 StartY=36.3521 StartZ=0 EndX=-195.094 EndY=34.0687 EndZ=0
    g1: LineSegment [constr] StartX=-194.098 StartY=36.8056 StartZ=0 EndX=-195.094 EndY=34.0687 EndZ=0
    g2: LineSegment StartX=-198.658 StartY=24.2771 StartZ=0 EndX=-199.654 EndY=21.5401 EndZ=0
    g3: LineSegment StartX=-199.654 StartY=21.5401 StartZ=0 EndX=-181.196 EndY=14.822 EndZ=0
    g4: LineSegment StartX=-181.196 StartY=14.822 StartZ=0 EndX=-180.2 EndY=17.559 EndZ=0
    g5: LineSegment StartX=-180.2 StartY=17.559 StartZ=0 EndX=-198.658 EndY=24.2771 EndZ=0
    g6: LineSegment [constr] StartX=-204.932 StartY=26.5605 StartZ=0 EndX=-198.658 EndY=24.2771 EndZ=0
    g7: LineSegment [constr] StartX=-198.658 StartY=24.2771 StartZ=0 EndX=-199.654 EndY=21.5401 EndZ=0
  constraints (20):
    c: Parallel(g1,g-3)
    c: Parallel(g0,g-4)
    c: Coincident(g0,g-4)
    c: Coincident(g1,g-3)
    c: Coincident(g0,g1)
    c: Coincident(g3,g2)
    c: Coincident(g4,g3)
    c: Coincident(g5,g4)
    c: Coincident(g5,g2)
    c: Parallel(g5,g-5)
    c: Parallel(g3,g-5)
    c: Parallel(g4,g-6)
    c: DistanceX(g-6,g4) = 0
    c: Coincident(g6,g-5)
    c: Equal(g6,g0)
    c: Coincident(g7,g6)
    c: Equal(g7,g1)
    c: Tangent(g7,g-3)
    c: Coincident(g2,g6)
    c: Coincident(g2,g7)
FEATURE [Part::Extrusion] Extrude062  label="Extrude buco per spazio introduzione SWITCH"
  Base = -> Sketch059
  Dir = (0,-1,2e-16)
  DirMode = 2
  FaceMakerClass = Part::FaceMakerBullseye
  FaceMakerMode = 3
  LengthFwd = 13.2
  LengthRev = 0
  Solid = true
  Symmetric = true
FEATURE [Part::Extrusion] Extrude063  label="Extrude buco interno per SWITCH sinistro"
  Base = -> Sketch057
  Dir = (0,-1,2e-16)
  DirMode = 2
  FaceMakerClass = Part::FaceMakerBullseye
  FaceMakerMode = 3
  LengthFwd = 13.2
  LengthRev = 0
  Placement = pos=(0,10.6,0) rot=(0,0,1;0rad)
  Solid = true
  Symmetric = false
FEATURE [Part::Extrusion] Extrude064  label="Extrude buco esterno per SWITCH sinistro"
  Base = -> Sketch058
  Dir = (0,-1,2e-16)
  DirMode = 2
  FaceMakerClass = Part::FaceMakerBullseye
  FaceMakerMode = 3
  LengthFwd = 2
  LengthRev = 0
  Placement = pos=(0,12.6,0) rot=(0,0,1;0rad)
  Solid = true
  Symmetric = false
FEATURE [Sketcher::SketchObject] Sketch061  label="struttura esterna blocco switch"
  ArcFitTolerance = 1e-06
  AttachmentSupport = -> [XZ_Plane003]
  FullyConstrained = true
  MakeInternals = false
  MapMode = 5
  Placement = pos=(0,0,0) rot=(1,0,0;1.5708rad)
  sketch-geometry (5):
    g0: LineSegment StartX=-1 StartY=-5.1 StartZ=0 EndX=1 EndY=-5.1 EndZ=0
    g1: LineSegment StartX=1 StartY=-5.1 StartZ=0 EndX=1 EndY=5.1 EndZ=0
    g2: LineSegment StartX=1 StartY=5.1 StartZ=0 EndX=-1 EndY=5.1 EndZ=0
    g3: LineSegment StartX=-1 StartY=5.1 StartZ=0 EndX=-1 EndY=-5.1 EndZ=0
    g4: GeomPoint [constr] X=0 Y=0 Z=0
  constraints (12):
    c: Coincident(g0,g1)
    c: Coincident(g1,g2)
    c: Coincident(g2,g3)
    c: Coincident(g3,g0)
    c: Horizontal(g0)
    c: Horizontal(g2)
    c: Vertical(g1)
    c: Vertical(g3)
    c: Symmetric(g2,g0,g4)
    c: Distance(g1,g3) = 2
    c: Distance(g0,g2) = 10.2
    c: Coincident(g4,g-1)
FEATURE [Sketcher::SketchObject] Sketch062  label="struttura interna blocco switch"
  ArcFitTolerance = 1e-06
  AttachmentSupport = -> [XZ_Plane003]
  ExternalGeometry = -> [Sketch061]
  FullyConstrained = true
  MakeInternals = false
  MapMode = 5
  Placement = pos=(0,0,0) rot=(1,0,0;1.5708rad)
  sketch-geometry (5):
    g0: LineSegment StartX=-1 StartY=3.1 StartZ=0 EndX=-1 EndY=-3.1 EndZ=0
    g1: LineSegment StartX=-1 StartY=-3.1 StartZ=0 EndX=1 EndY=-3.1 EndZ=0
    g2: LineSegment StartX=1 StartY=-3.1 StartZ=0 EndX=1 EndY=3.1 EndZ=0
    g3: LineSegment StartX=1 StartY=3.1 StartZ=0 EndX=-1 EndY=3.1 EndZ=0
    g4: GeomPoint [constr] X=0 Y=0 Z=0
  constraints (12):
    c: Coincident(g0,g1)
    c: Coincident(g1,g2)
    c: Coincident(g2,g3)
    c: Coincident(g3,g0)
    c: Vertical(g0)
    c: Vertical(g2)
    c: Horizontal(g1)
    c: Horizontal(g3)
    c: Symmetric(g2,g0,g4)
    c: Coincident(g4,g-1)
    c: Distance(g0) = 6.2
    c: Equal(g3,g-3)
FEATURE [Sketcher::SketchObject] Sketch063  label="blocchi tra switch"
  ArcFitTolerance = 1e-06
  AttachmentSupport = -> [XZ_Plane003]
  ExternalGeometry = -> [Sketch061,Sketch062]
  FullyConstrained = true
  MakeInternals = false
  MapMode = 5
  Placement = pos=(0,0,0) rot=(1,0,0;1.5708rad)
  sketch-geometry (8):
    g0: LineSegment StartX=-3 StartY=5.1 StartZ=0 EndX=-1 EndY=5.1 EndZ=0
    g1: LineSegment StartX=-1 StartY=5.1 StartZ=0 EndX=-1 EndY=3.1 EndZ=0
    g2: LineSegment StartX=-1 StartY=3.1 StartZ=0 EndX=-3 EndY=3.1 EndZ=0
    g3: LineSegment StartX=-3 StartY=3.1 StartZ=0 EndX=-3 EndY=5.1 EndZ=0
    g4: LineSegment StartX=-3 StartY=-3.1 StartZ=0 EndX=-1 EndY=-3.1 EndZ=0
    g5: LineSegment StartX=-1 StartY=-3.1 StartZ=0 EndX=-1 EndY=-5.1 EndZ=0
    g6: LineSegment StartX=-1 StartY=-5.1 StartZ=0 EndX=-3 EndY=-5.1 EndZ=0
    g7: LineSegment StartX=-3 StartY=-5.1 StartZ=0 EndX=-3 EndY=-3.1 EndZ=0
  constraints (20):
    c: Horizontal(g0)
    c: Coincident(g1,g0)
    c: Coincident(g2,g1)
    c: Horizontal(g2)
    c: Coincident(g3,g2)
    c: Coincident(g3,g0)
    c: Vertical(g3)
    c: Horizontal(g4)
    c: Coincident(g5,g4)
    c: Coincident(g6,g5)
    c: Horizontal(g6)
    c: Coincident(g7,g6)
    c: Coincident(g7,g4)
    c: Vertical(g7)
    c: Coincident(g0,g-4)
    c: Coincident(g1,g-5)
    c: Coincident(g4,g-6)
    c: Coincident(g5,g-7)
    c: Distance(g0) = 2
    c: Distance(g4) = 2
FEATURE [Sketcher::SketchObject] Sketch066  label="piano per rampino"
  ArcFitTolerance = 1e-06
  AttachmentSupport = -> [XZ_Plane002]
  ExternalGeometry = -> [Sketch045]
  FullyConstrained = true
  MakeInternals = false
  MapMode = 5
  Placement = pos=(0,0,0) rot=(1,0,0;1.5708rad)
  sketch-geometry (4):
    g0: LineSegment StartX=5.4 StartY=5.1 StartZ=0 EndX=5.4 EndY=3.9 EndZ=0
    g1: LineSegment StartX=5.4 StartY=3.9 StartZ=0 EndX=7 EndY=3.9 EndZ=0
    g2: LineSegment StartX=7 StartY=3.9 StartZ=0 EndX=7 EndY=5.1 EndZ=0
    g3: LineSegment StartX=7 StartY=5.1 StartZ=0 EndX=5.4 EndY=5.1 EndZ=0
  constraints (11):
    c: Coincident(g0,g1)
    c: Coincident(g1,g2)
    c: Coincident(g2,g3)
    c: Coincident(g3,g0)
    c: Vertical(g0)
    c: Vertical(g2)
    c: Horizontal(g1)
    c: Horizontal(g3)
    c: Distance(g0,g2) = 1.6
    c: Distance(g1,g3) = 1.2
    c: Coincident(g2,g-3)
FEATURE [Sketcher::SketchObject] Sketch064  label="rampini_per_serraggio_struttura"
  ArcFitTolerance = 1e-06
  AttachmentSupport = -> [XZ_Plane002]
  ExternalGeometry = -> [Sketch066,Sketch045]
  FullyConstrained = true
  MakeInternals = false
  MapMode = 5
  Placement = pos=(0,0,0) rot=(1,0,0;1.5708rad)
  sketch-geometry (7):
    g0: LineSegment StartX=7 StartY=5.1 StartZ=0 EndX=7 EndY=3.9 EndZ=0
    g1: LineSegment StartX=7 StartY=3.9 StartZ=0 EndX=9 EndY=3.9 EndZ=0
    g2: LineSegment StartX=7 StartY=5.1 StartZ=0 EndX=7 EndY=5.1 EndZ=0
    g3: LineSegment StartX=7 StartY=5.1 StartZ=0 EndX=7 EndY=7.5 EndZ=0
    g4: LineSegment StartX=9 StartY=5.1 StartZ=0 EndX=9 EndY=3.9 EndZ=0
    g5: LineSegment StartX=7 StartY=7.5 StartZ=0 EndX=9 EndY=7.5 EndZ=0
    g6: LineSegment StartX=9 StartY=7.5 StartZ=0 EndX=9 EndY=5.1 EndZ=0
  constraints (20):
    c: Vertical(g0)
    c: Coincident(g1,g0)
    c: Horizontal(g1)
    c: Coincident(g2,g0)
    c: Horizontal(g2)
    c: Coincident(g3,g2)
    c: Vertical(g3)
    c: Coincident(g5,g3)
    c: Coincident(g4,g6)
    c: Coincident(g4,g1)
    c: Vertical(g4)
    c: Coincident(g0,g-3)
    c: DistanceY(g-4,g3) = 2.4
    c: DistanceX(g1,g1) = 2
    c: DistanceY(g2,g6) = 0
    c: DistanceX(g2,g2) = 0
    c: DistanceY(g0,g0) = 1.2
    c: Coincident(g5,g6)
    c: Horizontal(g5)
    c: Vertical(g6)
FEATURE [Sketcher::SketchObject] Sketch067  label="perno per blocco switch"
  ArcFitTolerance = 1e-06
  AttachmentSupport = -> [XZ_Plane]
  ExternalGeometry = -> [Sketch,Sketch010]
  FullyConstrained = true
  MakeInternals = false
  MapMode = 5
  Placement = pos=(0,0,0) rot=(1,0,0;1.5708rad)
  sketch-geometry (14):
    g0: LineSegment StartX=-191.073 StartY=24.9429 StartZ=0 EndX=-185.81 EndY=23.0276 EndZ=0
    g1: LineSegment StartX=-183.76 StartY=23.9839 StartZ=0 EndX=-182.392 EndY=27.7427 EndZ=0
    g2: LineSegment StartX=-183.348 StartY=29.7934 StartZ=0 EndX=-188.61 EndY=31.7087 EndZ=0
    g3: LineSegment StartX=-188.61 StartY=31.7087 StartZ=0 EndX=-191.073 EndY=24.9429 EndZ=0
    g4: GeomPoint [constr] X=-186.459 Y=27.0946 Z=0
    g5: LineSegment StartX=-189.022 StartY=25.8992 StartZ=0 EndX=-185.263 EndY=24.5311 EndZ=0
    g6: LineSegment StartX=-185.263 StartY=24.5311 StartZ=0 EndX=-183.895 EndY=28.2899 EndZ=0
    g7: LineSegment StartX=-183.895 StartY=28.2899 StartZ=0 EndX=-187.654 EndY=29.658 EndZ=0
    g8: LineSegment StartX=-187.654 StartY=29.658 StartZ=0 EndX=-189.022 EndY=25.8992 EndZ=0
    g9: GeomPoint [constr] X=-186.459 Y=27.0946 Z=0
    g10: ArcOfCircle CenterX=-185.263 CenterY=24.5311 CenterZ=0 NormalX=0 NormalY=0 NormalZ=1 AngleXU=0 Radius=1.6 StartAngle=4.36332 EndAngle=5.93412
    g11: GeomPoint [constr] X=-184.307 Y=22.4804 Z=0
    g12: ArcOfCircle CenterX=-183.895 CenterY=28.2899 CenterZ=0 NormalX=0 NormalY=0 NormalZ=1 AngleXU=0 Radius=1.6 StartAngle=5.93412 EndAngle=7.50492
    g13: GeomPoint [constr] X=-181.844 Y=29.2462 Z=0
  constraints (30):
    c: Coincident(g2,g3)
    c: Coincident(g3,g0)
    c: Symmetric(g13,g0,g4)
    c: Distance(g11,g3) = 7.2
    c: Distance(g0,g2) = 7.2
    c: Parallel(g3,g1)
    c: Parallel(g2,g0)
    c: Perpendicular(g2,g3)
    c: Coincident(g5,g6)
    c: Coincident(g6,g7)
    c: Coincident(g7,g8)
    c: Coincident(g8,g5)
    c: Symmetric(g7,g5,g9)
    c: Distance(g6,g8) = 4
    c: Distance(g5,g7) = 4
    c: Coincident(g9,g4)
    c: Parallel(g8,g6)
    c: Parallel(g7,g5)
    c: Perpendicular(g7,g8)
    c: Tangent(g8,g-3)
    c: Tangent(g2,g-4)
    c: PointOnObject(g11,g1)
    c: PointOnObject(g11,g0)
    c: Tangent(g1,g10) = -1.5708
    c: Tangent(g0,g10) = -1.5708
    c: PointOnObject(g13,g1)
    c: Tangent(g1,g12) = -1.5708
    c: Tangent(g2,g12) = -1.5708
    c: Equal(g10,g12)
    c: Coincident(g10,g5)
FEATURE [Part::Extrusion] Extrude072  label="Extrude perno per blocco switch"
  Base = -> Sketch067
  Dir = (0,-1,2e-16)
  DirMode = 2
  FaceMakerClass = Part::FaceMakerBullseye
  FaceMakerMode = 3
  LengthFwd = 25.2
  LengthRev = 0
  Solid = true
  Symmetric = true
FEATURE [Part::MultiFuse] Fusion
  Refine = true
  Shapes = -> [Extrude,Sweep,Extrude007,Extrude011,Extrude005,Extrude012,Extrude013,Extrude016,Extrude031,Extrude039,Extrude045,Extrude072]
FEATURE [Part::Cut] Cut
  Base = -> Fusion
  Refine = true
  Tool = -> Extrude001
FEATURE [Part::Cut] Cut001
  Base = -> Cut
  Refine = true
  Tool = -> Extrude004
FEATURE [Part::Cut] Cut002
  Base = -> Cut001
  Refine = true
  Tool = -> Extrude006
FEATURE [Part::Cut] Cut003
  Base = -> Cut002
  Refine = true
  Tool = -> Extrude008
FEATURE [Part::Cut] Cut004
  Base = -> Cut003
  Refine = true
  Tool = -> Extrude009
FEATURE [Part::Cut] Cut005
  Base = -> Cut004
  Refine = true
  Tool = -> Extrude010
FEATURE [Part::Cut] Cut006
  Base = -> Cut005
  Refine = true
  Tool = -> Extrude014
FEATURE [Part::Cut] Cut007
  Base = -> Cut006
  Refine = true
  Tool = -> Extrude015
FEATURE [Part::Cut] Cut008
  Base = -> Cut007
  Refine = true
  Tool = -> Extrude018
FEATURE [Part::Cut] Cut009
  Base = -> Cut008
  Refine = true
  Tool = -> Extrude019
FEATURE [Part::Cut] Cut010
  Base = -> Cut009
  Refine = true
  Tool = -> Extrude020
FEATURE [Part::Cut] Cut011
  Base = -> Cut010
  Refine = true
  Tool = -> Extrude021
FEATURE [Part::Cut] Cut012
  Base = -> Cut011
  Refine = true
  Tool = -> Extrude022
FEATURE [Part::Cut] Cut013
  Base = -> Cut012
  Refine = true
  Tool = -> Extrude023
FEATURE [Part::Cut] Cut014
  Base = -> Cut013
  Refine = true
  Tool = -> Extrude032
FEATURE [Part::Cut] Cut015
  Base = -> Cut014
  Refine = true
  Tool = -> Extrude033
FEATURE [Part::Cut] Cut016
  Base = -> Cut015
  Refine = true
  Tool = -> Extrude034
FEATURE [Part::Cut] Cut017
  Base = -> Cut016
  Refine = true
  Tool = -> Extrude035
FEATURE [Part::Cut] Cut018
  Base = -> Cut017
  Refine = true
  Tool = -> Extrude036
FEATURE [Part::Cut] Cut019
  Base = -> Cut018
  Refine = true
  Tool = -> Extrude037
FEATURE [Part::Cut] Cut020
  Base = -> Cut019
  Refine = true
  Tool = -> Extrude030
FEATURE [Part::Cut] Cut022
  Base = -> Cut020
  Refine = true
  Tool = -> Extrude038
FEATURE [Part::Cut] Cut023
  Base = -> Cut022
  Refine = true
  Tool = -> Extrude041
FEATURE [Part::Cut] Cut024
  Base = -> Cut023
  Refine = true
  Tool = -> Extrude040
FEATURE [Part::Cut] Cut025
  Base = -> Cut024
  Refine = true
  Tool = -> Extrude042
FEATURE [Part::Cut] Cut026
  Base = -> Cut025
  Refine = true
  Tool = -> Extrude043
FEATURE [Part::Cut] Cut027
  Base = -> Cut026
  Refine = true
  Tool = -> Extrude044
FEATURE [Part::Cut] Cut028
  Base = -> Cut027
  Refine = true
  Tool = -> Extrude046
FEATURE [Part::Cut] Cut029
  Base = -> Cut028
  Refine = true
  Tool = -> Extrude047
FEATURE [Part::Cut] Cut033
  Base = -> Cut029
  Refine = true
  Tool = -> Extrude055
FEATURE [Part::Cut] Cut034
  Base = -> Cut033
  Refine = true
  Tool = -> Extrude056
FEATURE [Part::Cut] Cut035
  Base = -> Cut034
  Refine = true
  Tool = -> Extrude057
FEATURE [Part::Cut] Cut037
  Base = -> Cut035
  Refine = true
  Tool = -> Extrude060
FEATURE [Part::Cut] Cut038
  Base = -> Cut037
  Refine = true
  Tool = -> Extrude061
FEATURE [Part::Cut] Cut039
  Base = -> Cut038
  Refine = true
  Tool = -> Extrude063
FEATURE [Part::Cut] Cut040
  Base = -> Cut039
  Refine = true
  Tool = -> Extrude064
FEATURE [Part::Cut] Cut041
  Base = -> Cut040
  Refine = true
  Tool = -> Extrude062
FEATURE [Sketcher::SketchObject] Sketch068  label="base con smusso sopra neopixel"
  ArcFitTolerance = 1e-06
  AttachmentSupport = -> [YZ_Plane002]
  FullyConstrained = true
  MakeInternals = false
  MapMode = 5
  Placement = pos=(0,0,0) rot=(0.57735,0.57735,0.57735;2.0944rad)
  sketch-geometry (5):
    g0: LineSegment StartX=-9.5 StartY=-6.1 StartZ=0 EndX=9.5 EndY=-6.1 EndZ=0
    g1: LineSegment StartX=9.5 StartY=-6.1 StartZ=0 EndX=9.5 EndY=6.1 EndZ=0
    g2: LineSegment StartX=9.5 StartY=6.1 StartZ=0 EndX=-9.5 EndY=6.1 EndZ=0
    g3: LineSegment StartX=-9.5 StartY=6.1 StartZ=0 EndX=-9.5 EndY=-6.1 EndZ=0
    g4: GeomPoint [constr] X=0 Y=0 Z=0
  constraints (12):
    c: Coincident(g0,g1)
    c: Coincident(g1,g2)
    c: Coincident(g2,g3)
    c: Coincident(g3,g0)
    c: Horizontal(g0)
    c: Horizontal(g2)
    c: Vertical(g1)
    c: Vertical(g3)
    c: Symmetric(g2,g0,g4)
    c: Distance(g1,g3) = 19
    c: Distance(g0,g2) = 12.2
    c: Coincident(g4,g-1)
FEATURE [Sketcher::SketchObject] Sketch069  label="cilindro minore"
  ArcFitTolerance = 1e-06
  AttachmentSupport = -> [XZ_Plane004]
  FullyConstrained = true
  MakeInternals = false
  MapMode = 5
  Placement = pos=(0,0,0) rot=(1,0,0;1.5708rad)
  sketch-geometry (1):
    g0: Circle CenterX=0 CenterY=0 CenterZ=0 NormalX=0 NormalY=0 NormalZ=1 AngleXU=0 Radius=5.8
  constraints (2):
    c: Diameter(g0) = 11.6
    c: Coincident(g0,g-1)
FEATURE [Sketcher::SketchObject] Sketch070  label="cilindro maggiore"
  ArcFitTolerance = 1e-06
  AttachmentSupport = -> [XZ_Plane004]
  ExternalGeometry = -> [Sketch069]
  FullyConstrained = true
  MakeInternals = false
  MapMode = 5
  Placement = pos=(0,0,0) rot=(1,0,0;1.5708rad)
  sketch-geometry (1):
    g0: Circle CenterX=0 CenterY=0 CenterZ=0 NormalX=0 NormalY=0 NormalZ=1 AngleXU=0 Radius=6.5
  constraints (2):
    c: Coincident(g0,g-1)
    c: Diameter(g0) = 13
FEATURE [Sketcher::SketchObject] Sketch071  label="buco interno"
  ArcFitTolerance = 1e-06
  AttachmentSupport = -> [XZ_Plane004]
  ExternalGeometry = -> [Sketch069]
  FullyConstrained = true
  MakeInternals = false
  MapMode = 5
  Placement = pos=(0,0,0) rot=(1,0,0;1.5708rad)
  sketch-geometry (1):
    g0: Circle CenterX=0 CenterY=0 CenterZ=0 NormalX=0 NormalY=0 NormalZ=1 AngleXU=0 Radius=5
  constraints (2):
    c: Coincident(g0,g-1)
    c: Diameter(g0) = 10
FEATURE [PartDesign::Pad] Pad
  Direction = (0,-1,2e-16)
  Length = 1.2
  Length2 = 10
  Placement = pos=(0,0,0) rot=(1,0,0;1.5708rad)
  Profile = -> Sketch070
  ReferenceAxis = -> Sketch070 [N_Axis]
  Refine = true
  Suppressed = false
  Type = 0
FEATURE [PartDesign::Pad] Pad001
  BaseFeature = -> Pad
  Direction = (0,-1,2e-16)
  Length = 5.6
  Length2 = 10
  Placement = pos=(0,0,0) rot=(1,0,0;1.5708rad)
  Profile = -> Sketch069
  ReferenceAxis = -> Sketch069 [N_Axis]
  Refine = true
  Suppressed = false
  Type = 0
FEATURE [PartDesign::Pocket] Pocket
  BaseFeature = -> Pad001
  Direction = (0,1,-2e-16)
  Length = 7
  Length2 = 5
  Midplane = true
  Placement = pos=(0,0,0) rot=(1,0,0;1.5708rad)
  Profile = -> Sketch071
  ReferenceAxis = -> Sketch071 [N_Axis]
  Refine = true
  Suppressed = false
  Type = 0
FEATURE [PartDesign::Fillet] Fillet
  Base = -> Pocket [Face7]
  BaseFeature = -> Pocket
  Placement = pos=(0,0,0) rot=(1,0,0;1.5708rad)
  Radius = 1
  Refine = true
  SupportTransform = false
  Suppressed = false
  UseAllEdges = false
FEATURE [PartDesign::Body] Body004  label="pulsanti lato sinistro"
  AllowCompound = false
  Group = -> [Sketch069,Sketch070,Sketch071,Pad,Pad001,Pocket,Fillet]
  Origin = -> Origin004
  Tip = -> Fillet
FEATURE [Sketcher::SketchObject] Sketch072  label="buco per saldature e diodo driver solenoide"
  ArcFitTolerance = 1e-06
  AttachmentSupport = -> [XZ_Plane]
  ExternalGeometry = -> [Sketch038]
  FullyConstrained = true
  MakeInternals = false
  MapMode = 5
  Placement = pos=(0,0,0) rot=(1,0,0;1.5708rad)
  sketch-geometry (4):
    g0: LineSegment StartX=-214.165 StartY=-46.5549 StartZ=0 EndX=-209.093 EndY=-35.6792 EndZ=0
    g1: LineSegment StartX=-209.093 StartY=-35.6792 StartZ=0 EndX=-209.456 EndY=-35.5101 EndZ=0
    g2: LineSegment StartX=-209.456 StartY=-35.5101 StartZ=0 EndX=-214.527 EndY=-46.3858 EndZ=0
    g3: LineSegment StartX=-214.527 StartY=-46.3858 StartZ=0 EndX=-214.165 EndY=-46.5549 EndZ=0
  constraints (11):
    c: Coincident(g1,g0)
    c: Coincident(g2,g1)
    c: Coincident(g3,g2)
    c: Coincident(g3,g0)
    c: Parallel(g-3,g0)
    c: Parallel(g0,g2)
    c: Perpendicular(g0,g3)
    c: Perpendicular(g1,g0)
    c: Distance(g3) = 0.4
    c: Distance(g2) = 12
    c: Coincident(g0,g-3)
FEATURE [Part::Extrusion] Extrude074  label="Extrude buco per saldature e diodo driver solenoide"
  Base = -> Sketch072
  Dir = (0,-1,2e-16)
  DirMode = 2
  FaceMakerClass = Part::FaceMakerBullseye
  FaceMakerMode = 3
  LengthFwd = 14.6
  LengthRev = 0
  Solid = true
  Symmetric = true
FEATURE [Part::Cut] Cut042
  Base = -> Cut041
  Refine = true
  Tool = -> Extrude074
FEATURE [Sketcher::SketchObject] Sketch073  label="fori slargati blocco solenoide"
  ArcFitTolerance = 1e-06
  AttachmentSupport = -> [XY_Plane]
  ExternalGeometry = -> [Sketch030]
  FullyConstrained = true
  MakeInternals = false
  MapMode = 5
  sketch-geometry (2):
    g0: Circle CenterX=-152.209 CenterY=6.95 CenterZ=0 NormalX=0 NormalY=0 NormalZ=1 AngleXU=0 Radius=3.7
    g1: Circle CenterX=-130.41 CenterY=-6.95 CenterZ=0 NormalX=0 NormalY=0 NormalZ=1 AngleXU=0 Radius=3.7
  constraints (4):
    c: Diameter(g0) = 7.4
    c: Coincident(g0,g-3)
    c: Diameter(g1) = 7.4
    c: Coincident(g1,g-4)
FEATURE [Part::Extrusion] Extrude075  label="Extrude fori slargati blocco solenoide"
  Base = -> Sketch073
  Dir = (0,0,1)
  DirMode = 2
  FaceMakerClass = Part::FaceMakerBullseye
  FaceMakerMode = 3
  LengthFwd = 1.5
  LengthRev = 0
  Placement = pos=(0,0,36.4) rot=(0,0,1;0rad)
  Solid = true
  Symmetric = false
FEATURE [Part::Cut] Cut043
  Base = -> Cut042
  Refine = true
  Tool = -> Extrude075
FEATURE [Sketcher::SketchObject] Sketch074  label="lato sx pistola"
  ArcFitTolerance = 1e-06
  AttachmentSupport = -> [XZ_Plane]
  ExternalGeometry = -> [Sketch016,Sketch,Sketch058]
  FullyConstrained = true
  MakeInternals = false
  MapMode = 5
  Placement = pos=(0,0,0) rot=(1,0,0;1.5708rad)
  sketch-geometry (37):
    g0: LineSegment StartX=-82.8 StartY=3.2 StartZ=0 EndX=0 EndY=3.2 EndZ=0
    g1: LineSegment StartX=-82.8 StartY=3.2 StartZ=0 EndX=-82.8 EndY=6.2 EndZ=0
    g2: LineSegment [constr] StartX=-107.6 StartY=18 StartZ=0 EndX=-107.6 EndY=20 EndZ=0
    g3: LineSegment [constr] StartX=-132.428 StartY=18 StartZ=0 EndX=-132.428 EndY=20 EndZ=0
    g4: LineSegment StartX=-132.428 StartY=20 StartZ=0 EndX=-107.6 EndY=20 EndZ=0
    g5: ArcOfCircle CenterX=-107.6 CenterY=4 CenterZ=0 NormalX=0 NormalY=0 NormalZ=1 AngleXU=0 Radius=16 StartAngle=0.137937 EndAngle=1.5708
    g6: LineSegment StartX=-82.8 StartY=6.2 StartZ=0 EndX=-91.752 EndY=6.2 EndZ=0
    g7: LineSegment [constr] StartX=-145.743 StartY=8.32624 StartZ=0 EndX=-147.645 EndY=8.94427 EndZ=0
    g8: ArcOfCircle CenterX=-132.428 CenterY=4 CenterZ=0 NormalX=0 NormalY=0 NormalZ=1 AngleXU=0 Radius=16 StartAngle=1.5708 EndAngle=2.82743
    g9: LineSegment StartX=-215.932 StartY=-80.4316 StartZ=0 EndX=-176.685 EndY=-80.4316 EndZ=0
    g10: LineSegment StartX=-147.645 StartY=8.94427 StartZ=0 EndX=-176.685 EndY=-80.4316 EndZ=0
    g11: LineSegment [constr] StartX=-193.988 StartY=-2.33927 StartZ=0 EndX=-192.176 EndY=-3.18451 EndZ=0
    g12: LineSegment [constr] StartX=-217.232 StartY=-52.1862 StartZ=0 EndX=-215.42 EndY=-53.0314 EndZ=0
    g13: LineSegment StartX=-192.176 StartY=-3.18451 StartZ=0 EndX=-215.42 EndY=-53.0314 EndZ=0
    g14: ArcOfCircle CenterX=-184.801 CenterY=-67.3089 CenterZ=0 NormalX=0 NormalY=0 NormalZ=1 AngleXU=0 Radius=33.7833 StartAngle=2.70526 EndAngle=3.54053
    g15: ArcOfCircle CenterX=-207.583 CenterY=4 CenterZ=0 NormalX=0 NormalY=0 NormalZ=1 AngleXU=0 Radius=17 StartAngle=5.84685 EndAngle=7.56663
    g16: LineSegment StartX=-202.765 StartY=20.303 StartZ=0 EndX=-195.887 EndY=39.2 EndZ=0
    g17: LineSegment [constr] StartX=-193.885 StartY=33.0037 StartZ=0 EndX=-197.644 EndY=34.3718 EndZ=0
    g18: LineSegment StartX=-195.887 StartY=39.2 StartZ=0 EndX=0 EndY=39.2 EndZ=0
    g19: LineSegment StartX=0 StartY=3.2 StartZ=0 EndX=0 EndY=39.2 EndZ=0
    g20: LineSegment StartX=-189.939 StartY=31.5672 StartZ=0 EndX=-192.333 EndY=24.9893 EndZ=0
    g21: LineSegment StartX=-196.467 StartY=26.4942 StartZ=0 EndX=-194.073 EndY=33.0721 EndZ=0
    g22: Circle CenterX=-213.443 CenterY=-76.8316 CenterZ=0 NormalX=0 NormalY=0 NormalZ=1 AngleXU=0 Radius=1.8
    g23: Circle CenterX=-179.305 CenterY=-76.8316 CenterZ=0 NormalX=0 NormalY=0 NormalZ=1 AngleXU=0 Radius=1.8
    g24: Circle CenterX=-184.08 CenterY=34.8 CenterZ=0 NormalX=0 NormalY=0 NormalZ=1 AngleXU=0 Radius=1.8
    g25: Circle CenterX=-78.51 CenterY=34.8 CenterZ=0 NormalX=0 NormalY=0 NormalZ=1 AngleXU=0 Radius=1.8
    g26: Circle CenterX=-78.51 CenterY=7.6 CenterZ=0 NormalX=0 NormalY=0 NormalZ=1 AngleXU=0 Radius=1.8
    g27: Circle CenterX=-5.6 CenterY=34.8 CenterZ=0 NormalX=0 NormalY=0 NormalZ=1 AngleXU=0 Radius=1.8
    g28: Circle CenterX=-5.6 CenterY=7.6 CenterZ=0 NormalX=0 NormalY=0 NormalZ=1 AngleXU=0 Radius=1.8
    g29: LineSegment StartX=-190.127 StartY=31.6356 StartZ=0 EndX=-189.939 EndY=31.5672 EndZ=0
    g30: LineSegment StartX=-194.073 StartY=33.0721 StartZ=0 EndX=-193.885 EndY=33.0037 EndZ=0
    g31: LineSegment StartX=-193.885 StartY=33.0037 StartZ=0 EndX=-190.127 EndY=31.6356 EndZ=0
    g32: LineSegment StartX=-196.467 StartY=26.4942 StartZ=0 EndX=-192.333 EndY=24.9893 EndZ=0
    g33: Circle CenterX=-19 CenterY=21.2 CenterZ=0 NormalX=0 NormalY=0 NormalZ=1 AngleXU=0 Radius=6.3
    g34: Circle CenterX=-42 CenterY=21.2 CenterZ=0 NormalX=0 NormalY=0 NormalZ=1 AngleXU=0 Radius=6.3
    g35: Circle CenterX=-65 CenterY=21.2 CenterZ=0 NormalX=0 NormalY=0 NormalZ=1 AngleXU=0 Radius=6.3
    g36: LineSegment [constr] StartX=-4 StartY=21.2 StartZ=0 EndX=-65 EndY=21.2 EndZ=0
  constraints (96):
    c: Coincident(g0,g-41)
    c: Horizontal(g0)
    c: PointOnObject(g0,g-39)
    c: Coincident(g1,g0)
    c: Vertical(g1)
    c: DistanceY(g1,g1) = 3
    c: Coincident(g2,g-17)
    c: Vertical(g2)
    c: Coincident(g3,g-16)
    c: Vertical(g3)
    c: DistanceY(g2,g2) = 2
    c: DistanceY(g3,g3) = 2
    c: Coincident(g4,g3)
    c: Coincident(g4,g2)
    c: Coincident(g5,g-17)
    c: Coincident(g5,g2)
    c: Coincident(g6,g1)
    c: Horizontal(g6)
    c: Coincident(g6,g5)
    c: Coincident(g7,g-15)
    c: Coincident(g8,g7)
    c: Coincident(g8,g3)
    c: Coincident(g8,g-15)
    c: Horizontal(g9)
    c: DistanceY(g-13,g9) = 2
    c: Coincident(g10,g7)
    c: Parallel(g10,g-14)
    c: Coincident(g9,g10)
    c: Distance(g11) = 2
    c: Coincident(g11,g-11)
    c: Perpendicular(g-11,g11)
    c: Distance(g12) = 2
    c: Coincident(g12,g-12)
    c: Perpendicular(g-11,g12)
    c: Coincident(g13,g11)
    c: Coincident(g13,g12)
    c: Coincident(g14,g-32)
    c: Coincident(g14,g12)
    c: Coincident(g14,g9)
    c: Coincident(g15,g-10)
    c: Coincident(g15,g11)
    c: Parallel(g16,g-22)
    c: Distance(g17) = 4
    c: PointOnObject(g17,g16)
    c: Coincident(g15,g16)
    c: Horizontal(g18)
    c: Coincident(g18,g16)
    c: Coincident(g19,g0)
    c: PointOnObject(g19,g-39)
    c: DistanceY(g19,g-36) = 2
    c: Coincident(g18,g19)
    c: Diameter(g22) = 3.6
    c: Coincident(g22,g-9)
    c: Diameter(g23) = 3.6
    c: Coincident(g23,g-8)
    c: Diameter(g24) = 3.6
    c: Diameter(g25) = 3.6
    c: Diameter(g26) = 3.6
    c: Diameter(g27) = 3.6
    c: Diameter(g28) = 3.6
    c: Coincident(g27,g-4)
    c: Coincident(g28,g-3)
    c: Coincident(g25,g-6)
    c: Coincident(g26,g-5)
    c: Coincident(g24,g-7)
    c: Parallel(g20,g-21)
    c: Equal(g20,g-21)
    c: Parallel(g21,g-19)
    c: Equal(g21,g-19)
    c: Distance(g29) = 0.2
    c: Distance(g30) = 0.2
    c: Parallel(g29,g-20)
    c: Parallel(g31,g-20)
    c: Equal(g31,g-20)
    c: Coincident(g30,g31)
    c: Coincident(g31,g29)
    c: Coincident(g29,g-21)
    c: Parallel(g30,g31)
    c: Coincident(g17,g30)
    c: Coincident(g20,g29)
    c: Coincident(g21,g30)
    c: Perpendicular(g16,g17)
    c: Coincident(g32,g21)
    c: Coincident(g32,g20)
    c: Perpendicular(g10,g7)
    c: Diameter(g33) = 12.6
    c: Diameter(g34) = 12.6
    c: Diameter(g35) = 12.6
    c: Horizontal(g36)
    c: PointOnObject(g33,g36)
    c: PointOnObject(g34,g36)
    c: DistanceX(g34,g33) = 23
    c: DistanceX(g35,g34) = 23
    c: DistanceX(g33,g36) = 15
    c: Symmetric(g-24,g-24,g36)
    c: Coincident(g36,g35)
FEATURE [Sketcher::SketchObject] Sketch075  label="lato dx pistola"
  ArcFitTolerance = 1e-06
  AttachmentSupport = -> [XZ_Plane]
  ExternalGeometry = -> [Sketch016,Sketch,Sketch058,Sketch074]
  FullyConstrained = true
  MakeInternals = false
  MapMode = 5
  Placement = pos=(0,0,0) rot=(1,0,0;1.5708rad)
  sketch-geometry (61):
    g0: LineSegment StartX=-82.8 StartY=3.2 StartZ=0 EndX=0 EndY=3.2 EndZ=0
    g1: LineSegment StartX=-82.8 StartY=3.2 StartZ=0 EndX=-82.8 EndY=6.2 EndZ=0
    g2: LineSegment [constr] StartX=-107.6 StartY=18 StartZ=0 EndX=-107.6 EndY=20 EndZ=0
    g3: LineSegment [constr] StartX=-132.428 StartY=18 StartZ=0 EndX=-132.428 EndY=20 EndZ=0
    g4: LineSegment StartX=-132.428 StartY=20 StartZ=0 EndX=-107.6 EndY=20 EndZ=0
    g5: ArcOfCircle CenterX=-107.6 CenterY=4 CenterZ=0 NormalX=0 NormalY=0 NormalZ=1 AngleXU=0 Radius=16 StartAngle=0.137937 EndAngle=1.5708
    g6: LineSegment StartX=-82.8 StartY=6.2 StartZ=0 EndX=-91.752 EndY=6.2 EndZ=0
    g7: LineSegment [constr] StartX=-145.743 StartY=8.32624 StartZ=0 EndX=-147.645 EndY=8.94427 EndZ=0
    g8: ArcOfCircle CenterX=-132.428 CenterY=4 CenterZ=0 NormalX=0 NormalY=0 NormalZ=1 AngleXU=0 Radius=16 StartAngle=1.5708 EndAngle=2.82743
    g9: LineSegment StartX=-215.932 StartY=-80.4316 StartZ=0 EndX=-176.685 EndY=-80.4316 EndZ=0
    g10: LineSegment StartX=-147.645 StartY=8.94427 StartZ=0 EndX=-176.685 EndY=-80.4316 EndZ=0
    g11: LineSegment [constr] StartX=-193.988 StartY=-2.33927 StartZ=0 EndX=-192.176 EndY=-3.18451 EndZ=0
    g12: LineSegment [constr] StartX=-217.232 StartY=-52.1862 StartZ=0 EndX=-215.42 EndY=-53.0314 EndZ=0
    g13: LineSegment StartX=-192.176 StartY=-3.18451 StartZ=0 EndX=-215.42 EndY=-53.0314 EndZ=0
    g14: ArcOfCircle CenterX=-184.801 CenterY=-67.3089 CenterZ=0 NormalX=0 NormalY=0 NormalZ=1 AngleXU=0 Radius=33.7833 StartAngle=2.70526 EndAngle=3.54053
    g15: ArcOfCircle CenterX=-207.583 CenterY=4 CenterZ=0 NormalX=0 NormalY=0 NormalZ=1 AngleXU=0 Radius=17 StartAngle=5.84685 EndAngle=7.56663
    g16: LineSegment StartX=-202.765 StartY=20.303 StartZ=0 EndX=-195.887 EndY=39.2 EndZ=0
    g17: LineSegment [constr] StartX=-193.885 StartY=33.0037 StartZ=0 EndX=-197.644 EndY=34.3718 EndZ=0
    g18: LineSegment StartX=-195.887 StartY=39.2 StartZ=0 EndX=0 EndY=39.2 EndZ=0
    g19: LineSegment StartX=0 StartY=3.2 StartZ=0 EndX=0 EndY=39.2 EndZ=0
    g20: LineSegment StartX=-189.939 StartY=31.5672 StartZ=0 EndX=-192.333 EndY=24.9893 EndZ=0
    g21: LineSegment StartX=-196.467 StartY=26.4942 StartZ=0 EndX=-194.073 EndY=33.0721 EndZ=0
    g22: Circle CenterX=-213.443 CenterY=-76.8316 CenterZ=0 NormalX=0 NormalY=0 NormalZ=1 AngleXU=0 Radius=1.8
    g23: Circle CenterX=-179.305 CenterY=-76.8316 CenterZ=0 NormalX=0 NormalY=0 NormalZ=1 AngleXU=0 Radius=1.8
    g24: Circle CenterX=-184.08 CenterY=34.8 CenterZ=0 NormalX=0 NormalY=0 NormalZ=1 AngleXU=0 Radius=1.8
    g25: Circle CenterX=-78.51 CenterY=34.8 CenterZ=0 NormalX=0 NormalY=0 NormalZ=1 AngleXU=0 Radius=1.8
    g26: Circle CenterX=-78.51 CenterY=7.6 CenterZ=0 NormalX=0 NormalY=0 NormalZ=1 AngleXU=0 Radius=1.8
    g27: Circle CenterX=-5.6 CenterY=34.8 CenterZ=0 NormalX=0 NormalY=0 NormalZ=1 AngleXU=0 Radius=1.8
    g28: Circle CenterX=-5.6 CenterY=7.6 CenterZ=0 NormalX=0 NormalY=0 NormalZ=1 AngleXU=0 Radius=1.8
    g29: LineSegment StartX=-190.127 StartY=31.6356 StartZ=0 EndX=-189.939 EndY=31.5672 EndZ=0
    g30: LineSegment StartX=-194.073 StartY=33.0721 StartZ=0 EndX=-193.885 EndY=33.0037 EndZ=0
    g31: LineSegment StartX=-193.885 StartY=33.0037 StartZ=0 EndX=-190.127 EndY=31.6356 EndZ=0
    g32: LineSegment StartX=-196.467 StartY=26.4942 StartZ=0 EndX=-192.333 EndY=24.9893 EndZ=0
    g33: LineSegment [constr] StartX=-4 StartY=21.2 StartZ=0 EndX=-87.91 EndY=21.2 EndZ=0
    g34: GeomPoint [constr] X=-4 Y=21.2 Z=0
    g35: LineSegment [constr] StartX=-15.2 StartY=33.7 StartZ=0 EndX=-15.2 EndY=8.7 EndZ=0
    g36: LineSegment [constr] StartX=-15.2 StartY=33.7 StartZ=0 EndX=-56.2 EndY=33.7 EndZ=0
    g37: LineSegment [constr] StartX=-15.2 StartY=8.7 StartZ=0 EndX=-56.2 EndY=8.7 EndZ=0
    g38: LineSegment [constr] StartX=-56.2 StartY=33.7 StartZ=0 EndX=-56.2 EndY=8.7 EndZ=0
    g39: Circle CenterX=-18.6 CenterY=30.3 CenterZ=0 NormalX=0 NormalY=0 NormalZ=1 AngleXU=0 Radius=3.4
    g40: Circle CenterX=-18.6 CenterY=12.1 CenterZ=0 NormalX=0 NormalY=0 NormalZ=1 AngleXU=0 Radius=3.4
    g41: Circle CenterX=-43.2 CenterY=30.3 CenterZ=0 NormalX=0 NormalY=0 NormalZ=1 AngleXU=0 Radius=3.4
    g42: Circle CenterX=-43.2 CenterY=12.1 CenterZ=0 NormalX=0 NormalY=0 NormalZ=1 AngleXU=0 Radius=3.4
    g43: LineSegment [constr] StartX=-4 StartY=21.2 StartZ=0 EndX=-15.2 EndY=21.2 EndZ=0
    g44: LineSegment [constr] StartX=-15.2 StartY=21.2 StartZ=0 EndX=-36.2 EndY=21.2 EndZ=0
    g45: LineSegment [constr] StartX=-41.5 StartY=16.2 StartZ=0 EndX=-30.9 EndY=16.2 EndZ=0
    g46: LineSegment [constr] StartX=-30.9 StartY=16.2 StartZ=0 EndX=-30.9 EndY=26.2 EndZ=0
    g47: LineSegment [constr] StartX=-30.9 StartY=26.2 StartZ=0 EndX=-41.5 EndY=26.2 EndZ=0
    g48: LineSegment [constr] StartX=-41.5 StartY=26.2 StartZ=0 EndX=-41.5 EndY=16.2 EndZ=0
    g49: GeomPoint [constr] X=-36.2 Y=21.2 Z=0
    g50: Circle CenterX=-36.2 CenterY=21.2 CenterZ=0 NormalX=0 NormalY=0 NormalZ=1 AngleXU=0 Radius=2.8
    g51: LineSegment [constr] StartX=-24.2 StartY=26.7 StartZ=0 EndX=-24.2 EndY=15.7 EndZ=0
    g52: Circle CenterX=-24.2 CenterY=26.7 CenterZ=0 NormalX=0 NormalY=0 NormalZ=1 AngleXU=0 Radius=3
    g53: Circle CenterX=-24.2 CenterY=15.7 CenterZ=0 NormalX=0 NormalY=0 NormalZ=1 AngleXU=0 Radius=3
    g54: GeomPoint X=-18.6 Y=30.3 Z=0
    g55: GeomPoint X=-18.6 Y=12.1 Z=0
    g56: GeomPoint X=-43.2 Y=12.1 Z=0
    g57: GeomPoint X=-43.2 Y=30.3 Z=0
    g58: Circle CenterX=-65 CenterY=21.2 CenterZ=0 NormalX=0 NormalY=0 NormalZ=1 AngleXU=0 Radius=1.5
    g59: Circle CenterX=-42 CenterY=21.2 CenterZ=0 NormalX=0 NormalY=0 NormalZ=1 AngleXU=0 Radius=1.5
    g60: Circle CenterX=-19 CenterY=21.2 CenterZ=0 NormalX=0 NormalY=0 NormalZ=1 AngleXU=0 Radius=1.5
  constraints (149):
    c: Coincident(g0,g-41)
    c: Horizontal(g0)
    c: PointOnObject(g0,g-39)
    c: Coincident(g1,g0)
    c: Vertical(g1)
    c: DistanceY(g1,g1) = 3
    c: Coincident(g2,g-17)
    c: Vertical(g2)
    c: Coincident(g3,g-16)
    c: Vertical(g3)
    c: DistanceY(g2,g2) = 2
    c: DistanceY(g3,g3) = 2
    c: Coincident(g4,g3)
    c: Coincident(g4,g2)
    c: Coincident(g5,g-17)
    c: Coincident(g5,g2)
    c: Coincident(g6,g1)
    c: Horizontal(g6)
    c: Coincident(g6,g5)
    c: Coincident(g7,g-15)
    c: Coincident(g8,g7)
    c: Coincident(g8,g3)
    c: Coincident(g8,g-15)
    c: Horizontal(g9)
    c: DistanceY(g-13,g9) = 2
    c: Coincident(g10,g7)
    c: Parallel(g10,g-14)
    c: Coincident(g9,g10)
    c: Distance(g11) = 2
    c: Coincident(g11,g-11)
    c: Perpendicular(g-11,g11)
    c: Distance(g12) = 2
    c: Coincident(g12,g-12)
    c: Perpendicular(g-11,g12)
    c: Coincident(g13,g11)
    c: Coincident(g13,g12)
    c: Coincident(g14,g-32)
    c: Coincident(g14,g12)
    c: Coincident(g14,g9)
    c: Coincident(g15,g-10)
    c: Coincident(g15,g11)
    c: Parallel(g16,g-22)
    c: Distance(g17) = 4
    c: PointOnObject(g17,g16)
    c: Coincident(g15,g16)
    c: Horizontal(g18)
    c: Coincident(g18,g16)
    c: Coincident(g19,g0)
    c: PointOnObject(g19,g-39)
    c: DistanceY(g19,g-36) = 2
    c: Coincident(g18,g19)
    c: Diameter(g22) = 3.6
    c: Coincident(g22,g-9)
    c: Diameter(g23) = 3.6
    c: Coincident(g23,g-8)
    c: Diameter(g24) = 3.6
    c: Diameter(g25) = 3.6
    c: Diameter(g26) = 3.6
    c: Diameter(g27) = 3.6
    c: Diameter(g28) = 3.6
    c: Coincident(g27,g-4)
    c: Coincident(g28,g-3)
    c: Coincident(g25,g-6)
    c: Coincident(g26,g-5)
    c: Coincident(g24,g-7)
    c: Parallel(g20,g-21)
    c: Equal(g20,g-21)
    c: Parallel(g21,g-19)
    c: Equal(g21,g-19)
    c: Distance(g29) = 0.2
    c: Distance(g30) = 0.2
    c: Parallel(g29,g-20)
    c: Parallel(g31,g-20)
    c: Equal(g31,g-20)
    c: Coincident(g30,g31)
    c: Coincident(g31,g29)
    c: Coincident(g29,g-21)
    c: Parallel(g30,g31)
    c: Coincident(g17,g30)
    c: Coincident(g20,g29)
    c: Coincident(g21,g30)
    c: Perpendicular(g16,g17)
    c: Coincident(g32,g21)
    c: Coincident(g32,g20)
    c: Perpendicular(g10,g7)
    c: Horizontal(g33)
    c: Symmetric(g-24,g-24,g33)
    c: PointOnObject(g33,g-28)
    c: Symmetric(g-24,g-24,g34)
    c: DistanceY(g35,g35) = 25
    c: Symmetric(g35,g35,g33)
    c: Distance(g36) = 41
    c: Coincident(g36,g35)
    c: Horizontal(g36)
    c: Coincident(g37,g35)
    c: Horizontal(g37)
    c: Coincident(g38,g36)
    c: Vertical(g38)
    c: Coincident(g37,g38)
    c: Diameter(g39) = 6.8
    c: Diameter(g40) = 6.8
    c: Tangent(g39,g36)
    c: Tangent(g40,g37)
    c: Tangent(g39,g35)
    c: Tangent(g40,g35)
    c: Diameter(g41) = 6.8
    c: Diameter(g42) = 6.8
    c: Tangent(g41,g36)
    c: Tangent(g42,g37)
    c: DistanceX(g41,g39) = 24.6
    c: DistanceX(g42,g40) = 24.6
    c: Distance(g43) = 11.2
    c: Coincident(g43,g33)
    c: PointOnObject(g43,g33)
    c: PointOnObject(g43,g35)
    c: Distance(g44) = 21
    c: Coincident(g44,g43)
    c: PointOnObject(g44,g33)
    c: Coincident(g45,g46)
    c: Coincident(g46,g47)
    c: Coincident(g47,g48)
    c: Coincident(g48,g45)
    c: Horizontal(g45)
    c: Horizontal(g47)
    c: Vertical(g46)
    c: Vertical(g48)
    c: Symmetric(g47,g45,g49)
    c: Distance(g46,g48) = 10.6
    c: Distance(g45,g47) = 10
    c: Coincident(g49,g44)
    c: Diameter(g50) = 5.6
    c: Coincident(g50,g44)
    c: Distance(g51) = 11
    c: Symmetric(g51,g51,g33)
    c: DistanceX(g51,g43) = 9
    c: Diameter(g52) = 6
    c: Coincident(g52,g51)
    c: Diameter(g53) = 6
    c: Coincident(g53,g51)
    c: Coincident(g40,g55)
    c: Coincident(g39,g54)
    c: Coincident(g41,g57)
    c: Coincident(g42,g56)
    c: Diameter(g58) = 3
    c: Diameter(g59) = 3
    c: Diameter(g60) = 3
    c: Coincident(g58,g-44)
    c: Coincident(g59,g-46)
    c: Coincident(g60,g-45)
FEATURE [Sketcher::SketchObject] Sketch078
  ArcFitTolerance = 1e-06
  AttachmentSupport = -> [XZ_Plane005]
  FullyConstrained = true
  MakeInternals = false
  MapMode = 5
  Placement = pos=(0,0,0) rot=(1,0,0;1.5708rad)
  sketch-geometry (5):
    g0: LineSegment [constr] StartX=0 StartY=5.5 StartZ=0 EndX=0 EndY=-5.5 EndZ=0
    g1: ArcOfCircle CenterX=0 CenterY=5.5 CenterZ=0 NormalX=0 NormalY=0 NormalZ=1 AngleXU=0 Radius=2.7 StartAngle=0 EndAngle=3.14159
    g2: ArcOfCircle CenterX=0 CenterY=-5.5 CenterZ=0 NormalX=0 NormalY=0 NormalZ=1 AngleXU=0 Radius=2.7 StartAngle=3.1416 EndAngle=6.28318
    g3: LineSegment StartX=-2.7 StartY=5.5 StartZ=0 EndX=-2.7 EndY=-5.50001 EndZ=0
    g4: LineSegment StartX=2.7 StartY=5.5 StartZ=0 EndX=2.7 EndY=-5.50001 EndZ=0
  constraints (13):
    c: Distance(g0) = 11
    c: Vertical(g0)
    c: Symmetric(g0,g0,g-1)
    c: Radius(g1) = 2.7
    c: Coincident(g1,g0)
    c: Radius(g2) = 2.7
    c: Coincident(g2,g0)
    c: Vertical(g3)
    c: Vertical(g4)
    c: Coincident(g2,g4)
    c: Coincident(g2,g3)
    c: Tangent(g3,g1) = -1.5708
    c: Tangent(g4,g1) = 1.5708
FEATURE [PartDesign::Pad] Pad002
  Direction = (0,-1,2e-16)
  Length = 0.8
  Length2 = 10
  Placement = pos=(0,0,0) rot=(1,0,0;1.5708rad)
  Profile = -> Sketch078
  ReferenceAxis = -> Sketch078 [N_Axis]
  Refine = true
  Suppressed = false
  Type = 0
FEATURE [Sketcher::SketchObject] Sketch079
  ArcFitTolerance = 1e-06
  AttachmentSupport = -> [XZ_Plane005]
  ExternalGeometry = -> [Sketch078]
  FullyConstrained = true
  MakeInternals = false
  MapMode = 5
  Placement = pos=(0,0,0) rot=(1,0,0;1.5708rad)
  sketch-geometry (2):
    g0: Circle CenterX=-1e-16 CenterY=5.5 CenterZ=0 NormalX=0 NormalY=0 NormalZ=1 AngleXU=0 Radius=2.7
    g1: Circle CenterX=0 CenterY=-5.5 CenterZ=0 NormalX=0 NormalY=0 NormalZ=1 AngleXU=0 Radius=2.7
  constraints (4):
    c: Coincident(g0,g-3)
    c: PointOnObject(g-3,g0)
    c: Coincident(g1,g-4)
    c: Equal(g1,g-4)
FEATURE [PartDesign::Pad] Pad003
  BaseFeature = -> Pad002
  Direction = (0,-1,2e-16)
  Length = 5
  Length2 = 10
  Placement = pos=(0,0,0) rot=(1,0,0;1.5708rad)
  Profile = -> Sketch079
  ReferenceAxis = -> Sketch079 [N_Axis]
  Refine = true
  Suppressed = false
  Type = 0
FEATURE [PartDesign::Fillet] Fillet001
  Base = -> Pad003 [Edge16,Edge14]
  BaseFeature = -> Pad003
  Placement = pos=(0,0,0) rot=(1,0,0;1.5708rad)
  Radius = 0.4
  Refine = true
  SupportTransform = false
  Suppressed = false
  UseAllEdges = false
FEATURE [PartDesign::Body] Body005  label="pulsanti lato destro"
  AllowCompound = false
  Group = -> [Sketch078,Pad002,Sketch079,Pad003,Fillet001]
  Origin = -> Origin005
  Tip = -> Fillet001
FEATURE [PartDesign::SubShapeBinder] Binder
  BindCopyOnChange = 0
  BindMode = 0
  ClaimChildren = false
  Context = -> Body006 [Binder.]
  Fuse = false
  MakeFace = true
  OffsetFill = false
  OffsetIntersection = false
  OffsetJoinType = 0
  OffsetOpenResult = false
  PartialLoad = false
  Refine = true
  Relative = true
  Support = -> [Body[Sketch074.]]
  _Version = 2
FEATURE [PartDesign::SubShapeBinder] Binder001
  BindCopyOnChange = 0
  BindMode = 0
  ClaimChildren = false
  Context = -> Body007 [Binder001.]
  Fuse = false
  MakeFace = true
  OffsetFill = false
  OffsetIntersection = false
  OffsetJoinType = 0
  OffsetOpenResult = false
  PartialLoad = false
  Refine = true
  Relative = true
  Support = -> [Body[Sketch075.]]
  _Version = 2
FEATURE [Mesh::Feature] logo_per_PCB_definitivo_positivo
  Placement = pos=(-191,17,-66) rot=(0,1,1;0rad)
FEATURE [Sketcher::SketchObject] Sketch114  label="Sketch114 - base lato DX"
  ArcFitTolerance = 1e-06
  AttachmentSupport = -> [Binder001]
  ExternalGeometry = -> [Binder001]
  FullyConstrained = true
  MakeInternals = false
  MapMode = 5
  Placement = pos=(0,1e-15,0) rot=(0,0.707107,0.707107;3.14159rad)
  sketch-geometry (30):
    g0: Circle CenterX=5.6 CenterY=34.8 CenterZ=0 NormalX=0 NormalY=0 NormalZ=1 AngleXU=0 Radius=1.8
    g1: Circle CenterX=5.6 CenterY=7.6 CenterZ=0 NormalX=0 NormalY=0 NormalZ=1 AngleXU=0 Radius=1.8
    g2: Circle CenterX=24.2 CenterY=26.7 CenterZ=0 NormalX=0 NormalY=0 NormalZ=1 AngleXU=0 Radius=3
    g3: Circle CenterX=24.2 CenterY=15.7 CenterZ=0 NormalX=0 NormalY=0 NormalZ=1 AngleXU=0 Radius=3
    g4: Circle CenterX=36.2 CenterY=21.2 CenterZ=0 NormalX=0 NormalY=0 NormalZ=1 AngleXU=0 Radius=2.8
    g5: Circle CenterX=78.51 CenterY=34.8 CenterZ=0 NormalX=0 NormalY=0 NormalZ=1 AngleXU=0 Radius=1.8
    g6: Circle CenterX=78.51 CenterY=7.6 CenterZ=0 NormalX=0 NormalY=0 NormalZ=1 AngleXU=0 Radius=1.8
    g7: Circle CenterX=184.08 CenterY=34.8 CenterZ=0 NormalX=0 NormalY=0 NormalZ=1 AngleXU=0 Radius=1.8
    g8: Circle CenterX=213.443 CenterY=-76.8316 CenterZ=0 NormalX=0 NormalY=0 NormalZ=1 AngleXU=0 Radius=1.8
    g9: Circle CenterX=179.305 CenterY=-76.8316 CenterZ=0 NormalX=0 NormalY=0 NormalZ=1 AngleXU=0 Radius=1.8
    g10: ArcOfCircle [constr] CenterX=132.428 CenterY=4 CenterZ=0 NormalX=0 NormalY=0 NormalZ=1 AngleXU=0 Radius=16 StartAngle=0.314159 EndAngle=1.5708
    g11: ArcOfCircle CenterX=107.6 CenterY=4 CenterZ=0 NormalX=0 NormalY=0 NormalZ=1 AngleXU=0 Radius=16 StartAngle=1.5708 EndAngle=3.00366
    g12: ArcOfCircle CenterX=207.583 CenterY=4 CenterZ=0 NormalX=0 NormalY=0 NormalZ=1 AngleXU=0 Radius=17 StartAngle=1.85815 EndAngle=3.57792
    g13: ArcOfCircle CenterX=184.801 CenterY=-67.3089 CenterZ=0 NormalX=0 NormalY=0 NormalZ=1 AngleXU=0 Radius=33.7833 StartAngle=5.88425 EndAngle=6.71952
    g14: LineSegment StartX=0 StartY=39.2 StartZ=0 EndX=0 EndY=3.2 EndZ=0
    g15: LineSegment StartX=0 StartY=3.2 StartZ=0 EndX=82.8 EndY=3.2 EndZ=0
    g16: LineSegment StartX=82.8 StartY=3.2 StartZ=0 EndX=82.8 EndY=6.2 EndZ=0
    g17: LineSegment StartX=82.8 StartY=6.2 StartZ=0 EndX=91.752 EndY=6.2 EndZ=0
    g18: LineSegment StartX=107.6 StartY=20 StartZ=0 EndX=132.428 EndY=20 EndZ=0
    g19: LineSegment StartX=147.645 StartY=8.94427 StartZ=0 EndX=176.685 EndY=-80.4316 EndZ=0
    g20: LineSegment StartX=176.685 StartY=-80.4316 StartZ=0 EndX=215.932 EndY=-80.4316 EndZ=0
    g21: LineSegment StartX=215.42 StartY=-53.0314 StartZ=0 EndX=192.176 EndY=-3.18451 EndZ=0
    g22: LineSegment StartX=202.765 StartY=20.303 StartZ=0 EndX=195.887 EndY=39.2 EndZ=0
    g23: LineSegment StartX=195.887 StartY=39.2 StartZ=0 EndX=0 EndY=39.2 EndZ=0
    g24: LineSegment StartX=196.467 StartY=26.4942 StartZ=0 EndX=194.073 EndY=33.0721 EndZ=0
    g25: LineSegment StartX=194.073 StartY=33.0721 StartZ=0 EndX=189.939 EndY=31.5672 EndZ=0
    g26: LineSegment StartX=189.939 StartY=31.5672 StartZ=0 EndX=192.333 EndY=24.9893 EndZ=0
    g27: LineSegment StartX=192.333 StartY=24.9893 StartZ=0 EndX=196.467 EndY=26.4942 EndZ=0
    g28: LineSegment StartX=132.428 StartY=20 StartZ=0 EndX=144.053 EndY=20 EndZ=0
    g29: LineSegment StartX=144.053 StartY=20 StartZ=0 EndX=147.645 EndY=8.94427 EndZ=0
  constraints (65):
    c: Equal(g0,g-25)
    c: Equal(g2,g-29)
    c: Equal(g3,g-30)
    c: Equal(g4,g-28)
    c: Equal(g1,g-26)
    c: Coincident(g0,g-25)
    c: Coincident(g1,g-26)
    c: Coincident(g2,g-29)
    c: Coincident(g3,g-30)
    c: Coincident(g4,g-28)
    c: Equal(g5,g-23)
    c: Equal(g6,g-24)
    c: Coincident(g5,g-23)
    c: Coincident(g6,g-24)
    c: Equal(g7,g-20)
    c: Coincident(g7,g-20)
    c: Equal(g9,g-22)
    c: Coincident(g9,g-22)
    c: Equal(g8,g-21)
    c: Coincident(g8,g-21)
    c: Equal(g13,g-12)
    c: Equal(g12,g-14)
    c: Equal(g10,g-9)
    c: Equal(g11,g-7)
    c: Coincident(g14,g-27)
    c: Coincident(g14,g-27)
    c: Coincident(g15,g14)
    c: Coincident(g15,g-5)
    c: Coincident(g16,g15)
    c: Coincident(g16,g-6)
    c: Coincident(g17,g16)
    c: Coincident(g17,g-7)
    c: Coincident(g11,g17)
    c: Coincident(g11,g-8)
    c: Coincident(g18,g11)
    c: Coincident(g18,g-9)
    c: Coincident(g10,g18)
    c: Coincident(g10,g-10)
    c: Coincident(g19,g10)
    c: Coincident(g19,g-11)
    c: Coincident(g20,g19)
    c: Coincident(g20,g-12)
    c: Coincident(g13,g20)
    c: Coincident(g13,g-13)
    c: Coincident(g21,g13)
    c: Coincident(g21,g-14)
    c: Coincident(g12,g21)
    c: Coincident(g12,g-15)
    c: Coincident(g22,g12)
    c: Coincident(g22,g-15)
    c: Coincident(g23,g22)
    c: Coincident(g23,g14)
    c: Coincident(g24,g-18)
    c: Coincident(g24,g-16)
    c: Coincident(g25,g24)
    c: Coincident(g25,g-19)
    c: Coincident(g26,g25)
    c: Coincident(g26,g-19)
    c: Coincident(g27,g26)
    c: Coincident(g27,g24)
    c: Coincident(g29,g10)
    c: Coincident(g28,g10)
    c: Coincident(g29,g28)
    c: Parallel(g28,g18)
    c: Parallel(g29,g19)
FEATURE [PartDesign::Pad] Pad011
  Direction = (0,1,-2e-16)
  Length = 2
  Length2 = 10
  Profile = -> Sketch114
  ReferenceAxis = -> Sketch114 [N_Axis]
  Refine = true
  Reversed = true
  Suppressed = false
  Type = 0
FEATURE [Sketcher::SketchObject] Sketch115
  ArcFitTolerance = 1e-06
  AttachmentSupport = -> [Pad011]
  ExternalGeometry = -> [Binder001]
  FullyConstrained = true
  MakeInternals = false
  MapMode = 5
  Placement = pos=(0,1.7e-15,0) rot=(0,0.707107,0.707107;3.14159rad)
  sketch-geometry (4):
    g0: ArcOfCircle CenterX=24.2 CenterY=26.7 CenterZ=0 NormalX=0 NormalY=0 NormalZ=1 AngleXU=0 Radius=3 StartAngle=4.48384e-08 EndAngle=3.14159
    g1: ArcOfCircle CenterX=24.2 CenterY=15.7 CenterZ=0 NormalX=0 NormalY=0 NormalZ=1 AngleXU=0 Radius=3 StartAngle=3.14159 EndAngle=6.28318
    g2: LineSegment StartX=21.2 StartY=26.7 StartZ=0 EndX=21.2 EndY=15.7 EndZ=0
    g3: LineSegment StartX=27.2 StartY=26.7 StartZ=0 EndX=27.2 EndY=15.7 EndZ=0
  constraints (12):
    c: Equal(g1,g-4)
    c: Equal(g0,g-3)
    c: Coincident(g0,g-3)
    c: Coincident(g1,g-4)
    c: Vertical(g2)
    c: Vertical(g3)
    c: Tangent(g3,g-3)
    c: Tangent(g2,g-3)
    c: Coincident(g0,g2)
    c: Coincident(g0,g3)
    c: Coincident(g1,g2)
    c: Coincident(g3,g1)
FEATURE [Sketcher::SketchObject] Sketch117  label="Sketch117 - fori per inserto M3 x 3 x 4.5"
  ArcFitTolerance = 1e-06
  AttachmentSupport = -> [Pad011]
  ExternalGeometry = -> [Binder001]
  FullyConstrained = true
  MakeInternals = false
  MapMode = 5
  Placement = pos=(0,1.7e-15,0) rot=(0,0.707107,0.707107;3.14159rad)
  sketch-geometry (4):
    g0: Circle CenterX=43.2 CenterY=30.3 CenterZ=0 NormalX=0 NormalY=0 NormalZ=1 AngleXU=0 Radius=2.25
    g1: Circle CenterX=43.2 CenterY=12.1 CenterZ=0 NormalX=0 NormalY=0 NormalZ=1 AngleXU=0 Radius=2.25
    g2: Circle CenterX=18.6 CenterY=30.3 CenterZ=0 NormalX=0 NormalY=0 NormalZ=1 AngleXU=0 Radius=2.25
    g3: Circle CenterX=18.6 CenterY=12.1 CenterZ=0 NormalX=0 NormalY=0 NormalZ=1 AngleXU=0 Radius=2.25
  constraints (8):
    c: Diameter(g0) = 4.5
    c: Diameter(g1) = 4.5
    c: Diameter(g2) = 4.5
    c: Diameter(g3) = 4.5
    c: Coincident(g2,g-3)
    c: Coincident(g3,g-6)
    c: Coincident(g0,g-4)
    c: Coincident(g1,g-5)
FEATURE [Sketcher::SketchObject] Sketch118
  ArcFitTolerance = 1e-06
  AttachmentSupport = -> [Pad011]
  ExternalGeometry = -> [Binder001]
  FullyConstrained = true
  MakeInternals = false
  MapMode = 5
  Placement = pos=(0,-2,0) rot=(1,0,0;1.5708rad)
  sketch-geometry (12):
    g0: Circle CenterX=-78.51 CenterY=34.8 CenterZ=0 NormalX=0 NormalY=0 NormalZ=1 AngleXU=0 Radius=1.8
    g1: Circle CenterX=-78.51 CenterY=7.6 CenterZ=0 NormalX=0 NormalY=0 NormalZ=1 AngleXU=0 Radius=1.8
    g2: Circle CenterX=-5.6 CenterY=34.8 CenterZ=0 NormalX=0 NormalY=0 NormalZ=1 AngleXU=0 Radius=1.8
    g3: Circle CenterX=-5.6 CenterY=7.6 CenterZ=0 NormalX=0 NormalY=0 NormalZ=1 AngleXU=0 Radius=1.8
    g4: LineSegment StartX=0 StartY=39.2 StartZ=0 EndX=0 EndY=3.2 EndZ=0
    g5: LineSegment StartX=0 StartY=3.2 StartZ=0 EndX=-82.8 EndY=3.2 EndZ=0
    g6: LineSegment StartX=-82.8 StartY=3.2 StartZ=0 EndX=-82.8 EndY=39.2 EndZ=0
    g7: LineSegment StartX=-82.8 StartY=39.2 StartZ=0 EndX=0 EndY=39.2 EndZ=0
    g8: ArcOfCircle CenterX=-65 CenterY=21.2 CenterZ=0 NormalX=0 NormalY=0 NormalZ=1 AngleXU=0 Radius=10 StartAngle=1.5708 EndAngle=4.71239
    g9: ArcOfCircle CenterX=-19 CenterY=21.2 CenterZ=0 NormalX=0 NormalY=0 NormalZ=1 AngleXU=0 Radius=10 StartAngle=4.71239 EndAngle=7.85398
    g10: LineSegment StartX=-65 StartY=31.2 StartZ=0 EndX=-19 EndY=31.2 EndZ=0
    g11: LineSegment StartX=-65 StartY=11.2 StartZ=0 EndX=-19 EndY=11.2 EndZ=0
  constraints (25):
    c: Equal(g2,g-5)
    c: Equal(g3,g-7)
    c: Equal(g1,g-6)
    c: Equal(g0,g-4)
    c: Coincident(g0,g-4)
    c: Coincident(g1,g-6)
    c: Coincident(g3,g-7)
    c: Coincident(g2,g-5)
    c: Coincident(g4,g-8)
    c: Coincident(g4,g-9)
    c: Coincident(g5,g4)
    c: Coincident(g5,g-10)
    c: Coincident(g6,g5)
    c: PointOnObject(g6,g-3)
    c: Vertical(g6)
    c: Coincident(g7,g6)
    c: Coincident(g7,g4)
    c: Tangent(g8,g10) = 1.5708
    c: Tangent(g8,g11) = -1.5708
    c: Tangent(g9,g10) = 1.5708
    c: Tangent(g9,g11) = -1.5708
    c: Equal(g8,g9)
    c: Radius(g8) = 10
    c: Coincident(g8,g-11)
    c: Coincident(g9,g-12)
FEATURE [Sketcher::SketchObject] Sketch120
  ArcFitTolerance = 1e-06
  AttachmentSupport = -> [Pad011]
  ExternalGeometry = -> [Binder001]
  FullyConstrained = true
  MakeInternals = false
  MapMode = 5
  Placement = pos=(0,-2,0) rot=(1,0,0;1.5708rad)
  sketch-geometry (4):
    g0: LineSegment StartX=-137.815 StartY=39.2 StartZ=0 EndX=-142.655 EndY=24.303 EndZ=0
    g1: LineSegment StartX=-137.815 StartY=39.2 StartZ=0 EndX=-110.815 EndY=39.2 EndZ=0
    g2: LineSegment StartX=-142.655 StartY=24.303 StartZ=0 EndX=-110.815 EndY=24.303 EndZ=0
    g3: ArcOfCircle CenterX=-92.2534 CenterY=31.7515 CenterZ=0 NormalX=0 NormalY=0 NormalZ=1 AngleXU=0 Radius=20 StartAngle=2.75997 EndAngle=3.52321
  constraints (12):
    c: PointOnObject(g0,g-3)
    c: Coincident(g1,g0)
    c: PointOnObject(g1,g-3)
    c: Coincident(g2,g0)
    c: Horizontal(g2)
    c: Tangent(g0,g-4)
    c: Vertical(g2,g1)
    c: DistanceX(g1,g1) = 27
    c: DistanceY(g-6,g0) = 4
    c: Radius(g3) = 20
    c: Coincident(g3,g1)
    c: Coincident(g3,g2)
FEATURE [Sketcher::SketchObject] Sketch121
  ArcFitTolerance = 1e-06
  AttachmentSupport = -> [Pad011]
  ExternalGeometry = -> [Binder001]
  FullyConstrained = true
  MakeInternals = false
  MapMode = 5
  Placement = pos=(0,-2,0) rot=(1,0,0;1.5708rad)
  sketch-geometry (15):
    g0: LineSegment StartX=-137.815 StartY=39.2 StartZ=0 EndX=-143.955 EndY=20.303 EndZ=0
    g1: LineSegment StartX=-143.955 StartY=20.303 StartZ=0 EndX=-190.141 EndY=20.303 EndZ=0
    g2: LineSegment StartX=-190.141 StartY=20.303 StartZ=0 EndX=-186.139 EndY=31.3 EndZ=0
    g3: LineSegment StartX=-178.754 StartY=39.2 StartZ=0 EndX=-180.791 EndY=33.6029 EndZ=0
    g4: ArcOfCircle CenterX=-184.08 CenterY=34.8 CenterZ=0 NormalX=0 NormalY=0 NormalZ=1 AngleXU=0 Radius=3.5 StartAngle=4.71239 EndAngle=5.93412
    g5: LineSegment StartX=-184.08 StartY=31.3 StartZ=0 EndX=-186.139 EndY=31.3 EndZ=0
    g6: LineSegment StartX=-137.815 StartY=39.2 StartZ=0 EndX=-156.815 EndY=39.2 EndZ=0
    g7: LineSegment StartX=-168.815 StartY=39.2 StartZ=0 EndX=-178.754 EndY=39.2 EndZ=0
    g8: LineSegment StartX=-157.815 StartY=39.2 StartZ=0 EndX=-167.815 EndY=39.2 EndZ=0
    g9: LineSegment StartX=-168.815 StartY=31.2 StartZ=0 EndX=-156.815 EndY=31.2 EndZ=0
    g10: LineSegment StartX=-167.436 StartY=36.2 StartZ=0 EndX=-157.436 EndY=36.2 EndZ=0
    g11: ArcOfCircle CenterX=-176.411 CenterY=35.2 CenterZ=0 NormalX=0 NormalY=0 NormalZ=1 AngleXU=0 Radius=20 StartAngle=6.08183 EndAngle=6.48454
    g12: ArcOfCircle CenterX=-188.411 CenterY=35.2 CenterZ=0 NormalX=0 NormalY=0 NormalZ=1 AngleXU=0 Radius=20 StartAngle=6.08183 EndAngle=6.48454
    g13: ArcOfCircle CenterX=-177.411 CenterY=35.2 CenterZ=0 NormalX=0 NormalY=0 NormalZ=1 AngleXU=0 Radius=20 StartAngle=0.0500209 EndAngle=0.201358
    g14: ArcOfCircle CenterX=-187.411 CenterY=35.2 CenterZ=0 NormalX=0 NormalY=0 NormalZ=1 AngleXU=0 Radius=20 StartAngle=0.0500209 EndAngle=0.201358
  constraints (46):
    c: PointOnObject(g0,g-3)
    c: Tangent(g0,g-5)
    c: Coincident(g1,g0)
    c: Horizontal(g1)
    c: Coincident(g2,g1)
    c: PointOnObject(g3,g-3)
    c: Parallel(g3,g-6)
    c: Parallel(g2,g-6)
    c: Radius(g4) = 3.5
    c: Coincident(g4,g-7)
    c: Tangent(g3,g4) = 1.5708
    c: Horizontal(g5)
    c: Tangent(g5,g4) = 1.5708
    c: DistanceX(g-8,g5) = 3.8
    c: Coincident(g2,g5)
    c: Coincident(g6,g0)
    c: PointOnObject(g6,g-3)
    c: DistanceX(g6,g6) = 19
    c: PointOnObject(g7,g-3)
    c: DistanceX(g7,g6) = 12
    c: Coincident(g7,g3)
    c: PointOnObject(g8,g-3)
    c: PointOnObject(g8,g-3)
    c: DistanceX(g8,g8) = 10
    c: DistanceX(g8,g6) = 1
    c: Horizontal(g9)
    c: Vertical(g7,g9)
    c: Vertical(g6,g9)
    c: DistanceY(g9,g7) = 8
    c: Horizontal(g10)
    c: Equal(g8,g10)
    c: DistanceY(g10,g8) = 3
    c: Radius(g11) = 20
    c: Coincident(g11,g6)
    c: Coincident(g11,g9)
    c: Radius(g12) = 20
    c: Coincident(g12,g7)
    c: Coincident(g12,g9)
    c: Equal(g13,g11)
    c: Coincident(g13,g8)
    c: Coincident(g13,g10)
    c: Horizontal(g13,g11)
    c: Equal(g14,g12)
    c: Coincident(g14,g8)
    c: Coincident(g14,g10)
    c: Horizontal(g1,g-6)
FEATURE [Sketcher::SketchObject] Sketch122
  ArcFitTolerance = 1e-06
  AttachmentSupport = -> [Pad011]
  ExternalGeometry = -> [Binder001]
  FullyConstrained = true
  MakeInternals = false
  MapMode = 5
  Placement = pos=(0,-2,0) rot=(1,0,0;1.5708rad)
  sketch-geometry (8):
    g0: ArcOfCircle CenterX=-184.801 CenterY=-67.3089 CenterZ=0 NormalX=0 NormalY=0 NormalZ=1 AngleXU=0 Radius=33.7833 StartAngle=2.70526 EndAngle=3.54053
    g1: LineSegment StartX=-176.685 StartY=-80.4316 StartZ=0 EndX=-215.932 EndY=-80.4316 EndZ=0
    g2: LineSegment StartX=-215.42 StartY=-53.0314 StartZ=0 EndX=-192.176 EndY=-3.18454 EndZ=0
    g3: ArcOfCircle CenterX=-207.583 CenterY=4 CenterZ=0 NormalX=0 NormalY=0 NormalZ=1 AngleXU=0 Radius=17 StartAngle=5.84685 EndAngle=7.56663
    g4: Circle CenterX=-213.443 CenterY=-76.8316 CenterZ=0 NormalX=0 NormalY=0 NormalZ=1 AngleXU=0 Radius=3
    g5: Circle CenterX=-179.305 CenterY=-76.8316 CenterZ=0 NormalX=0 NormalY=0 NormalZ=1 AngleXU=0 Radius=3
    g6: LineSegment StartX=-143.955 StartY=20.303 StartZ=0 EndX=-176.685 EndY=-80.4316 EndZ=0
    g7: LineSegment StartX=-202.765 StartY=20.303 StartZ=0 EndX=-143.955 EndY=20.303 EndZ=0
  constraints (18):
    c: Coincident(g0,g-7)
    c: Coincident(g0,g-8)
    c: Coincident(g1,g0)
    c: Tangent(g2,g-5)
    c: Coincident(g3,g-6)
    c: Coincident(g2,g3)
    c: Coincident(g0,g2)
    c: Diameter(g4) = 6
    c: Diameter(g5) = 6
    c: Coincident(g4,g-9)
    c: Coincident(g5,g-10)
    c: Horizontal(g1)
    c: Coincident(g6,g1)
    c: Tangent(g6,g-4)
    c: Coincident(g3,g-6)
    c: Coincident(g7,g3)
    c: Horizontal(g7)
    c: Coincident(g7,g6)
FEATURE [Sketcher::SketchObject] Sketch123
  ArcFitTolerance = 1e-06
  AttachmentSupport = -> [Pad011]
  ExternalGeometry = -> [Binder001]
  FullyConstrained = true
  MakeInternals = false
  MapMode = 5
  Placement = pos=(0,-2,0) rot=(1,0,0;1.5708rad)
  sketch-geometry (4):
    g0: LineSegment StartX=-108 StartY=36.8 StartZ=0 EndX=-90 EndY=36.8 EndZ=0
    g1: LineSegment StartX=-108 StartY=36.8 StartZ=0 EndX=-108 EndY=26.8 EndZ=0
    g2: LineSegment StartX=-108 StartY=26.8 StartZ=0 EndX=-90 EndY=26.8 EndZ=0
    g3: ArcOfCircle CenterX=-94 CenterY=31.8 CenterZ=0 NormalX=0 NormalY=0 NormalZ=1 AngleXU=0 Radius=6.40312 StartAngle=5.38713 EndAngle=7.17924
  constraints (13):
    c: Horizontal(g0)
    c: Coincident(g1,g0)
    c: Vertical(g1)
    c: Coincident(g2,g1)
    c: Horizontal(g2)
    c: DistanceX(g0,g0) = 18
    c: DistanceY(g1,g1) = 10
    c: Equal(g0,g2)
    c: DistanceX(g0,g-3) = 90
    c: DistanceY(g0,g-3) = 2.4
    c: Coincident(g3,g0)
    c: Coincident(g3,g2)
    c: DistanceX(g3,g0) = 4
FEATURE [PartDesign::Chamfer] Chamfer014
  Angle = 45
  Base = -> Pad011 [Edge80,Edge4,Edge7]
  BaseFeature = -> Pad011
  ChamferType = 0
  FlipDirection = false
  Refine = true
  Size = 1.9
  Size2 = 1
  SupportTransform = false
  Suppressed = false
  UseAllEdges = false
FEATURE [PartDesign::Pocket] Pocket006
  BaseFeature = -> Chamfer014
  Direction = (0,-1,2e-16)
  Length = 1.2
  Length2 = 5
  Profile = -> Sketch115
  ReferenceAxis = -> Sketch115 [N_Axis]
  Refine = true
  Suppressed = false
  Type = 0
FEATURE [Sketcher::SketchObject] Sketch116  label="Sketch116 - pieno per inserto M3 x 3 x 4,5"
  ArcFitTolerance = 1e-06
  AttachmentSupport = -> [Pocket006]
  ExternalGeometry = -> [Binder001]
  FullyConstrained = true
  MakeInternals = false
  MapMode = 5
  Placement = pos=(0,1.7e-15,0) rot=(0,0.707107,0.707107;3.14159rad)
  sketch-geometry (4):
    g0: Circle CenterX=43.2 CenterY=30.3 CenterZ=0 NormalX=0 NormalY=0 NormalZ=1 AngleXU=0 Radius=3.4
    g1: Circle CenterX=43.2 CenterY=12.1 CenterZ=0 NormalX=0 NormalY=0 NormalZ=1 AngleXU=0 Radius=3.4
    g2: Circle CenterX=18.6 CenterY=30.3 CenterZ=0 NormalX=0 NormalY=0 NormalZ=1 AngleXU=0 Radius=3.4
    g3: Circle CenterX=18.6 CenterY=12.1 CenterZ=0 NormalX=0 NormalY=0 NormalZ=1 AngleXU=0 Radius=3.4
  constraints (8):
    c: Diameter(g0) = 6.8
    c: Diameter(g1) = 6.8
    c: Diameter(g2) = 6.8
    c: Diameter(g3) = 6.8
    c: Coincident(g2,g-3)
    c: Coincident(g0,g-4)
    c: Coincident(g3,g-6)
    c: Coincident(g1,g-5)
FEATURE [PartDesign::Pad] Pad012
  BaseFeature = -> Pocket006
  Direction = (0,1,-2e-16)
  Length = 2.4
  Length2 = 10
  Profile = -> Sketch116
  ReferenceAxis = -> Sketch116 [N_Axis]
  Refine = true
  Suppressed = false
  Type = 0
FEATURE [PartDesign::Pocket] Pocket007
  BaseFeature = -> Pad012
  Direction = (0,-1,2e-16)
  Length = 0.6
  Length2 = 2.4
  Profile = -> Sketch117
  ReferenceAxis = -> Sketch117 [N_Axis]
  Refine = true
  Suppressed = false
  Type = 4
FEATURE [PartDesign::Pad] Pad013
  BaseFeature = -> Pocket007
  Direction = (0,-1,2e-16)
  Length = 1.6
  Length2 = 10
  Profile = -> Sketch118
  ReferenceAxis = -> Sketch118 [N_Axis]
  Refine = true
  Suppressed = false
  Type = 0
FEATURE [Sketcher::SketchObject] Sketch119
  ArcFitTolerance = 1e-06
  AttachmentSupport = -> [Pad013]
  ExternalGeometry = -> [Binder001]
  FullyConstrained = true
  MakeInternals = false
  MapMode = 5
  Placement = pos=(0,-3.6,0) rot=(1,0,0;1.5708rad)
  sketch-geometry (21):
    g0: LineSegment [constr] StartX=-82.8 StartY=3.2 StartZ=0 EndX=-82.8 EndY=39.2 EndZ=0
    g1: ArcOfCircle CenterX=-78.51 CenterY=34.8 CenterZ=0 NormalX=0 NormalY=0 NormalZ=1 AngleXU=0 Radius=3.5 StartAngle=4.71239 EndAngle=6.28319
    g2: ArcOfCircle CenterX=-78.51 CenterY=7.6 CenterZ=0 NormalX=0 NormalY=0 NormalZ=1 AngleXU=0 Radius=3.5 StartAngle=0 EndAngle=1.5708
    g3: ArcOfCircle CenterX=-5.6 CenterY=34.8 CenterZ=0 NormalX=0 NormalY=0 NormalZ=1 AngleXU=0 Radius=3.5 StartAngle=3.14159 EndAngle=4.71239
    g4: ArcOfCircle CenterX=-5.6 CenterY=7.6 CenterZ=0 NormalX=0 NormalY=0 NormalZ=1 AngleXU=0 Radius=3.5 StartAngle=1.5708 EndAngle=3.14159
    g5: LineSegment StartX=0 StartY=39.2 StartZ=0 EndX=0 EndY=31.3 EndZ=0
    g6: LineSegment StartX=0 StartY=39.2 StartZ=0 EndX=-9.1 EndY=39.2 EndZ=0
    g7: LineSegment StartX=0 StartY=3.2 StartZ=0 EndX=0 EndY=11.1 EndZ=0
    g8: LineSegment StartX=0 StartY=3.2 StartZ=0 EndX=-9.1 EndY=3.2 EndZ=0
    g9: LineSegment StartX=-82.8 StartY=3.2 StartZ=0 EndX=-75.01 EndY=3.2 EndZ=0
    g10: LineSegment StartX=-82.8 StartY=3.2 StartZ=0 EndX=-82.8 EndY=11.1 EndZ=0
    g11: LineSegment StartX=-82.8 StartY=39.2 StartZ=0 EndX=-82.8 EndY=31.3 EndZ=0
    g12: LineSegment StartX=-82.8 StartY=39.2 StartZ=0 EndX=-75.01 EndY=39.2 EndZ=0
    g13: LineSegment StartX=-82.8 StartY=31.3 StartZ=0 EndX=-78.51 EndY=31.3 EndZ=0
    g14: LineSegment StartX=-75.01 StartY=39.2 StartZ=0 EndX=-75.01 EndY=34.8 EndZ=0
    g15: LineSegment StartX=-82.8 StartY=11.1 StartZ=0 EndX=-78.51 EndY=11.1 EndZ=0
    g16: LineSegment StartX=-75.01 StartY=3.2 StartZ=0 EndX=-75.01 EndY=7.6 EndZ=0
    g17: LineSegment StartX=-9.1 StartY=39.2 StartZ=0 EndX=-9.1 EndY=34.8 EndZ=0
    g18: LineSegment StartX=0 StartY=31.3 StartZ=0 EndX=-5.6 EndY=31.3 EndZ=0
    g19: LineSegment StartX=0 StartY=11.1 StartZ=0 EndX=-5.6 EndY=11.1 EndZ=0
    g20: LineSegment StartX=-9.1 StartY=3.2 StartZ=0 EndX=-9.1 EndY=7.6 EndZ=0
  constraints (51):
    c: Coincident(g0,g-10)
    c: PointOnObject(g0,g-8)
    c: Vertical(g0)
    c: Coincident(g1,g-3)
    c: Coincident(g2,g-4)
    c: Coincident(g3,g-5)
    c: Coincident(g4,g-6)
    c: Radius(g4) = 3.5
    c: Radius(g3) = 3.5
    c: Radius(g1) = 3.5
    c: Radius(g2) = 3.5
    c: Coincident(g5,g-9)
    c: PointOnObject(g5,g-9)
    c: Coincident(g6,g5)
    c: PointOnObject(g6,g-8)
    c: Coincident(g7,g-9)
    c: PointOnObject(g7,g-9)
    c: Coincident(g8,g7)
    c: PointOnObject(g8,g-7)
    c: Coincident(g9,g0)
    c: PointOnObject(g9,g-7)
    c: Coincident(g10,g0)
    c: PointOnObject(g10,g0)
    c: Coincident(g11,g0)
    c: PointOnObject(g11,g0)
    c: Coincident(g12,g0)
    c: PointOnObject(g12,g-8)
    c: Coincident(g13,g11)
    c: Horizontal(g13)
    c: Coincident(g14,g12)
    c: Vertical(g14)
    c: Coincident(g15,g10)
    c: Horizontal(g15)
    c: Coincident(g16,g9)
    c: Vertical(g16)
    c: Coincident(g17,g6)
    c: Vertical(g17)
    c: Coincident(g18,g5)
    c: Horizontal(g18)
    c: Coincident(g19,g7)
    c: Horizontal(g19)
    c: Coincident(g20,g8)
    c: Vertical(g20)
    c: Tangent(g20,g4) = 1.5708
    c: Tangent(g4,g19) = -1.5708
    c: Tangent(g18,g3) = 1.5708
    c: Tangent(g3,g17) = -1.5708
    c: Tangent(g13,g1) = -1.5708
    c: Tangent(g1,g14) = 1.5708
    c: Tangent(g16,g2) = -1.5708
    c: Tangent(g2,g15) = 1.5708
FEATURE [PartDesign::Pocket] Pocket008
  BaseFeature = -> Pad013
  Direction = (0,1,-2e-16)
  Length = 1.6
  Length2 = 5
  Profile = -> Sketch119
  ReferenceAxis = -> Sketch119 [N_Axis]
  Refine = true
  Suppressed = false
  Type = 0
FEATURE [PartDesign::Pad] Pad017
  BaseFeature = -> Pocket008
  Direction = (0,-1,2e-16)
  Length = 1.6
  Length2 = 10
  Profile = -> Sketch123
  ReferenceAxis = -> Sketch123 [N_Axis]
  Refine = true
  Suppressed = false
  Type = 0
FEATURE [Sketcher::SketchObject] Sketch125
  ArcFitTolerance = 1e-06
  AttachmentSupport = -> [Pad017]
  ExternalGeometry = -> [Pad017]
  FullyConstrained = true
  MakeInternals = false
  MapMode = 5
  Placement = pos=(0,-3.6,8e-16) rot=(1,0,0;1.5708rad)
  sketch-geometry (20):
    g0: LineSegment StartX=-108 StartY=35.8 StartZ=0 EndX=-108 EndY=35 EndZ=0
    g1: LineSegment StartX=-108 StartY=35 StartZ=0 EndX=-97 EndY=35 EndZ=0
    g2: LineSegment StartX=-97 StartY=35 StartZ=0 EndX=-97 EndY=35.8 EndZ=0
    g3: LineSegment StartX=-97 StartY=35.8 StartZ=0 EndX=-108 EndY=35.8 EndZ=0
    g4: LineSegment StartX=-108 StartY=28.6 StartZ=0 EndX=-108 EndY=27.8 EndZ=0
    g5: LineSegment StartX=-108 StartY=27.8 StartZ=0 EndX=-97 EndY=27.8 EndZ=0
    g6: LineSegment StartX=-97 StartY=27.8 StartZ=0 EndX=-97 EndY=28.6 EndZ=0
    g7: LineSegment StartX=-97 StartY=28.6 StartZ=0 EndX=-108 EndY=28.6 EndZ=0
    g8: LineSegment StartX=-108 StartY=30.4 StartZ=0 EndX=-108 EndY=29.6 EndZ=0
    g9: LineSegment StartX=-108 StartY=29.6 StartZ=0 EndX=-97 EndY=29.6 EndZ=0
    g10: LineSegment StartX=-97 StartY=29.6 StartZ=0 EndX=-97 EndY=30.4 EndZ=0
    g11: LineSegment StartX=-97 StartY=30.4 StartZ=0 EndX=-108 EndY=30.4 EndZ=0
    g12: LineSegment StartX=-108 StartY=32.2 StartZ=0 EndX=-108 EndY=31.4 EndZ=0
    g13: LineSegment StartX=-108 StartY=31.4 StartZ=0 EndX=-97 EndY=31.4 EndZ=0
    g14: LineSegment StartX=-97 StartY=31.4 StartZ=0 EndX=-97 EndY=32.2 EndZ=0
    g15: LineSegment StartX=-97 StartY=32.2 StartZ=0 EndX=-108 EndY=32.2 EndZ=0
    g16: LineSegment StartX=-108 StartY=34 StartZ=0 EndX=-108 EndY=33.2 EndZ=0
    g17: LineSegment StartX=-108 StartY=33.2 StartZ=0 EndX=-97 EndY=33.2 EndZ=0
    g18: LineSegment StartX=-97 StartY=33.2 StartZ=0 EndX=-97 EndY=34 EndZ=0
    g19: LineSegment StartX=-97 StartY=34 StartZ=0 EndX=-108 EndY=34 EndZ=0
  constraints (55):
    c: Coincident(g1,g0)
    c: Horizontal(g1)
    c: Coincident(g2,g1)
    c: Vertical(g2)
    c: Coincident(g3,g2)
    c: Horizontal(g3)
    c: Coincident(g3,g0)
    c: DistanceX(g1,g1) = 11
    c: DistanceY(g2,g2) = 0.8
    c: Coincident(g5,g4)
    c: Horizontal(g5)
    c: Coincident(g6,g5)
    c: Vertical(g6)
    c: Coincident(g7,g6)
    c: Horizontal(g7)
    c: Coincident(g7,g4)
    c: Coincident(g9,g8)
    c: Horizontal(g9)
    c: Coincident(g10,g9)
    c: Vertical(g10)
    c: Coincident(g11,g10)
    c: Horizontal(g11)
    c: Coincident(g11,g8)
    c: Coincident(g13,g12)
    c: Horizontal(g13)
    c: Coincident(g14,g13)
    c: Vertical(g14)
    c: Coincident(g15,g14)
    c: Horizontal(g15)
    c: Coincident(g15,g12)
    c: Coincident(g17,g16)
    c: Horizontal(g17)
    c: Coincident(g18,g17)
    c: Vertical(g18)
    c: Coincident(g19,g18)
    c: Horizontal(g19)
    c: Coincident(g19,g16)
    c: Equal(g3,g19)
    c: Equal(g3,g15)
    c: Equal(g3,g11)
    c: Equal(g3,g7)
    c: Equal(g2,g18)
    c: Equal(g2,g14)
    c: Equal(g2,g10)
    c: Equal(g2,g6)
    c: DistanceY(g-4,g4) = 1
    c: DistanceY(g4,g8) = 1
    c: DistanceY(g8,g12) = 1
    c: DistanceY(g12,g16) = 1
    c: DistanceY(g16,g0) = 1
    c: Tangent(g0,g-5)
    c: Tangent(g16,g-5)
    c: Tangent(g12,g-5)
    c: Tangent(g8,g-5)
    c: Tangent(g4,g-5)
FEATURE [PartDesign::Chamfer] Chamfer009
  Angle = 45
  Base = -> Pad017 [Edge151,Edge154]
  BaseFeature = -> Pad017
  ChamferType = 1
  FlipDirection = false
  Refine = true
  Size = 1.5
  Size2 = 2.8
  SupportTransform = false
  Suppressed = false
  UseAllEdges = false
FEATURE [PartDesign::Pocket] Pocket009
  BaseFeature = -> Chamfer009
  Direction = (0,1,-2e-16)
  Length = 1
  Length2 = 5
  Profile = -> Sketch125
  ReferenceAxis = -> Sketch125 [N_Axis]
  Refine = true
  Suppressed = false
  Type = 0
FEATURE [PartDesign::Pad] Pad014
  BaseFeature = -> Pocket009
  Direction = (0,-1,2e-16)
  Length = 0.8
  Length2 = 10
  Profile = -> Sketch120
  ReferenceAxis = -> Sketch120 [N_Axis]
  Refine = true
  Suppressed = false
  Type = 0
FEATURE [Sketcher::SketchObject] Sketch124
  ArcFitTolerance = 1e-06
  AttachmentSupport = -> [Pad014]
  ExternalGeometry = -> [Binder001]
  FullyConstrained = true
  MakeInternals = false
  MapMode = 5
  Placement = pos=(0,-2.8,6e-16) rot=(1,0,0;1.5708rad)
  sketch-geometry (4):
    g0: LineSegment StartX=-129 StartY=39.2 StartZ=0 EndX=-131.599 EndY=31.2 EndZ=0
    g1: LineSegment StartX=-118 StartY=39.2 StartZ=0 EndX=-120.599 EndY=31.2 EndZ=0
    g2: LineSegment StartX=-129 StartY=39.2 StartZ=0 EndX=-118 EndY=39.2 EndZ=0
    g3: LineSegment StartX=-120.599 StartY=31.2 StartZ=0 EndX=-131.599 EndY=31.2 EndZ=0
  constraints (12):
    c: PointOnObject(g0,g-3)
    c: PointOnObject(g1,g-3)
    c: Parallel(g-4,g0)
    c: Parallel(g-4,g1)
    c: Coincident(g2,g0)
    c: Coincident(g2,g1)
    c: DistanceX(g2,g2) = 11
    c: DistanceY(g1,g1) = 8
    c: Coincident(g3,g1)
    c: Horizontal(g3)
    c: Coincident(g3,g0)
    c: DistanceX(g1,g-3) = 118
FEATURE [PartDesign::Pad] Pad018
  BaseFeature = -> Pad014
  Direction = (0,-1,2e-16)
  Length = 1.2
  Length2 = 10
  Profile = -> Sketch124
  ReferenceAxis = -> Sketch124 [N_Axis]
  Refine = true
  Suppressed = false
  Type = 0
FEATURE [Sketcher::SketchObject] Sketch126
  ArcFitTolerance = 1e-06
  AttachmentSupport = -> [Pad018]
  ExternalGeometry = -> [Pad018]
  FullyConstrained = true
  MakeInternals = false
  MapMode = 5
  Placement = pos=(0,-4,0) rot=(1,0,0;1.5708rad)
  sketch-geometry (8):
    g0: LineSegment StartX=-129.877 StartY=36.5 StartZ=0 EndX=-130.137 EndY=35.7 EndZ=0
    g1: LineSegment StartX=-130.69 StartY=34 StartZ=0 EndX=-130.95 EndY=33.2 EndZ=0
    g2: LineSegment StartX=-129.877 StartY=36.5 StartZ=0 EndX=-118.877 EndY=36.5 EndZ=0
    g3: LineSegment StartX=-130.137 StartY=35.7 StartZ=0 EndX=-119.137 EndY=35.7 EndZ=0
    g4: LineSegment StartX=-130.69 StartY=34 StartZ=0 EndX=-119.69 EndY=34 EndZ=0
    g5: LineSegment StartX=-130.95 StartY=33.2 StartZ=0 EndX=-119.95 EndY=33.2 EndZ=0
    g6: LineSegment StartX=-118.877 StartY=36.5 StartZ=0 EndX=-119.137 EndY=35.7 EndZ=0
    g7: LineSegment StartX=-119.69 StartY=34 StartZ=0 EndX=-119.95 EndY=33.2 EndZ=0
  constraints (20):
    c: Coincident(g2,g0)
    c: Horizontal(g2)
    c: Coincident(g3,g0)
    c: Horizontal(g3)
    c: Coincident(g4,g1)
    c: Horizontal(g4)
    c: Coincident(g5,g1)
    c: Horizontal(g5)
    c: Coincident(g6,g2)
    c: Coincident(g6,g3)
    c: Coincident(g7,g4)
    c: Coincident(g7,g5)
    c: Tangent(g0,g-4)
    c: Tangent(g6,g-5)
    c: Tangent(g1,g-4)
    c: Tangent(g7,g-5)
    c: DistanceY(g3,g2) = 0.8
    c: DistanceY(g5,g4) = 0.8
    c: DistanceY(g-6,g1) = 2
    c: DistanceY(g-6,g0) = 4.5
FEATURE [PartDesign::Chamfer] Chamfer008
  Angle = 45
  Base = -> Pad018 [Edge257]
  BaseFeature = -> Pad018
  ChamferType = 1
  FlipDirection = false
  Refine = true
  Size = 1
  Size2 = 6
  SupportTransform = false
  Suppressed = false
  UseAllEdges = false
FEATURE [PartDesign::Pocket] Pocket010
  BaseFeature = -> Chamfer008
  Direction = (0,1,-2e-16)
  Length = 1
  Length2 = 5
  Profile = -> Sketch126
  ReferenceAxis = -> Sketch126 [N_Axis]
  Refine = true
  Suppressed = false
  Type = 0
FEATURE [PartDesign::Pad] Pad015
  BaseFeature = -> Pocket010
  Direction = (0,-1,2e-16)
  Length = 2
  Length2 = 10
  Profile = -> Sketch121
  ReferenceAxis = -> Sketch121 [N_Axis]
  Refine = true
  Suppressed = false
  Type = 0
FEATURE [PartDesign::Pad] Pad016
  BaseFeature = -> Pad015
  Direction = (0,-1,2e-16)
  Length = 1.6
  Length2 = 10
  Profile = -> Sketch122
  ReferenceAxis = -> Sketch122 [N_Axis]
  Refine = true
  Suppressed = false
  Type = 0
FEATURE [Sketcher::SketchObject] Sketch129
  ArcFitTolerance = 1e-06
  AttachmentSupport = -> [Pad016]
  ExternalGeometry = -> [Binder001]
  FullyConstrained = true
  MakeInternals = false
  MapMode = 5
  Placement = pos=(0,-3.6,0) rot=(1,0,0;1.5708rad)
  sketch-geometry (12):
    g0: LineSegment [constr] StartX=-192.176 StartY=-3.18451 StartZ=0 EndX=-181.223 EndY=20.303 EndZ=0
    g1: LineSegment [constr] StartX=-202.765 StartY=20.303 StartZ=0 EndX=-181.223 EndY=20.303 EndZ=0
    g2: LineSegment StartX=-202.765 StartY=20.303 StartZ=0 EndX=-181.223 EndY=20.303 EndZ=0
    g3: LineSegment StartX=-192.176 StartY=-3.18451 StartZ=0 EndX=-196.804 EndY=-13.1107 EndZ=0
    g4: ArcOfCircle CenterX=-207.583 CenterY=4 CenterZ=0 NormalX=0 NormalY=0 NormalZ=1 AngleXU=0 Radius=17 StartAngle=5.84685 EndAngle=7.56663
    g5: ArcOfEllipse CenterX=-181.223 CenterY=8.55923 CenterZ=0 NormalX=0 NormalY=0 NormalZ=1 MajorRadius=23.4779 MinorRadius=11.7437 AngleXU=2e-16 StartAngle=4.71239 EndAngle=7.85398
    g6: LineSegment [constr] StartX=-157.745 StartY=8.55923 StartZ=0 EndX=-204.701 EndY=8.55923 EndZ=0
    g7: LineSegment [constr] StartX=-181.223 StartY=20.303 StartZ=0 EndX=-181.223 EndY=-3.18451 EndZ=0
    g8: GeomPoint [constr] X=-160.894 Y=8.55923 Z=0
    g9: GeomPoint [constr] X=-201.553 Y=8.55923 Z=0
    g10: ArcOfCircle CenterX=-181.223 CenterY=-20.3763 CenterZ=0 NormalX=0 NormalY=0 NormalZ=1 AngleXU=0 Radius=17.1918 StartAngle=1.57079 EndAngle=2.70526
    g11: GeomPoint [constr] X=-181.223 Y=-3.18451 Z=0
  constraints (23):
    c: Coincident(g0,g-5)
    c: Coincident(g1,g-6)
    c: Horizontal(g1)
    c: Coincident(g1,g0)
    c: Parallel(g0,g-4)
    c: Coincident(g2,g1)
    c: Coincident(g2,g0)
    c: Coincident(g3,g0)
    c: Equal(g4,g-5)
    c: Coincident(g4,g1)
    c: Coincident(g4,g0)
    c: InternalAlignment(g6-g9 -> g5) x4
    c: Vertical(g5,g0)
    c: Horizontal(g6)
    c: Coincident(g5,g0)
    c: DistanceX(g6,g-3) = 10.1
    c: Tangent(g10,g3) = -1.5708
    c: PointOnObject(g11,g10)
    c: Tangent(g5,g10,g11) = 1.5708
    c: Coincident(g10,g5)
    c: Coincident(g11,g7)
    c: Parallel(g3,g-4)
    c: Horizontal(g5,g0)
FEATURE [Sketcher::SketchObject] Sketch130
  ArcFitTolerance = 1e-06
  AttachmentOffset = pos=(0,0,-1.6) rot=(0,0,1;0rad)
  AttachmentSupport = -> [Pad016]
  ExternalGeometry = -> [Binder001]
  FullyConstrained = true
  MakeInternals = false
  MapMode = 5
  Placement = pos=(0,-2,-4e-16) rot=(1,0,0;1.5708rad)
  sketch-geometry (12):
    g0: LineSegment [constr] StartX=-192.176 StartY=-3.18451 StartZ=0 EndX=-181.223 EndY=20.303 EndZ=0
    g1: LineSegment [constr] StartX=-202.765 StartY=20.303 StartZ=0 EndX=-181.223 EndY=20.303 EndZ=0
    g2: LineSegment StartX=-202.765 StartY=20.303 StartZ=0 EndX=-181.223 EndY=20.303 EndZ=0
    g3: LineSegment StartX=-192.176 StartY=-3.18451 StartZ=0 EndX=-193.827 EndY=-6.72678 EndZ=0
    g4: ArcOfCircle CenterX=-207.583 CenterY=4 CenterZ=0 NormalX=0 NormalY=0 NormalZ=1 AngleXU=0 Radius=17 StartAngle=5.84685 EndAngle=7.56663
    g5: ArcOfEllipse CenterX=-181.223 CenterY=10.803 CenterZ=0 NormalX=0 NormalY=0 NormalZ=1 MajorRadius=14.4779 MinorRadius=9.5 AngleXU=0 StartAngle=4.71239 EndAngle=7.85398
    g6: LineSegment [constr] StartX=-166.745 StartY=10.803 StartZ=0 EndX=-195.701 EndY=10.803 EndZ=0
    g7: LineSegment [constr] StartX=-181.223 StartY=20.303 StartZ=0 EndX=-181.223 EndY=1.30297 EndZ=0
    g8: GeomPoint [constr] X=-170.298 Y=10.803 Z=0
    g9: GeomPoint [constr] X=-192.148 Y=10.803 Z=0
    g10: ArcOfCircle CenterX=-181.223 CenterY=-12.6042 CenterZ=0 NormalX=0 NormalY=0 NormalZ=1 AngleXU=0 Radius=13.9072 StartAngle=1.5708 EndAngle=2.70526
    g11: GeomPoint [constr] X=-181.223 Y=1.30297 Z=0
  constraints (23):
    c: Coincident(g0,g-5)
    c: Coincident(g1,g-6)
    c: Horizontal(g1)
    c: Coincident(g1,g0)
    c: Parallel(g0,g-4)
    c: Coincident(g2,g1)
    c: Coincident(g2,g0)
    c: Coincident(g3,g0)
    c: Equal(g4,g-5)
    c: Coincident(g4,g1)
    c: Coincident(g4,g0)
    c: InternalAlignment(g6-g9 -> g5) x4
    c: Vertical(g5,g0)
    c: Horizontal(g6)
    c: Coincident(g5,g0)
    c: DistanceX(g6,g-3) = 19.1
    c: Tangent(g10,g3) = -1.5708
    c: PointOnObject(g11,g10)
    c: Tangent(g5,g10,g11) = 1.5708
    c: Coincident(g10,g5)
    c: Coincident(g11,g7)
    c: Parallel(g3,g-4)
    c: DistanceY(g5,g0) = 19
FEATURE [Part::Part2DObjectPython] Clone2D001  label="Sketch130 (2D)"  # Draft 2D object (typed FeaturePython)
  Fuse = false
  Objects = -> [Sketch130]
  Placement = pos=(0,-2,-4e-16) rot=(1,0,0;1.5708rad)
  Scale = (1,1,1)
FEATURE [Sketcher::SketchObject] Sketch131
  ArcFitTolerance = 1e-06
  AttachmentOffset = pos=(0,0,-3.5) rot=(0,0,1;0rad)
  AttachmentSupport = -> [Pad016]
  ExternalGeometry = -> [Binder001]
  FullyConstrained = true
  MakeInternals = false
  MapMode = 5
  Placement = pos=(0,-0.1,-8e-16) rot=(1,0,0;1.5708rad)
  sketch-geometry (1):
    g0: GeomPoint X=-197.47 Y=8.55923 Z=0
  constraints (1):
    c: Symmetric(g-6,g-4,g0)
FEATURE [Sketcher::SketchObject] Sketch132
  ArcFitTolerance = 1e-06
  AttachmentSupport = -> [Pad016]
  ExternalGeometry = -> [Binder001]
  FullyConstrained = true
  MakeInternals = false
  MapMode = 5
  Placement = pos=(0,-3.6,0) rot=(1,0,0;1.5708rad)
  sketch-geometry (3):
    g0: LineSegment [constr] StartX=-215.42 StartY=-53.0314 StartZ=0 EndX=-167.782 EndY=-53.0314 EndZ=0
    g1: Circle CenterX=-191.282 CenterY=-53.0314 CenterZ=0 NormalX=0 NormalY=0 NormalZ=1 AngleXU=0 Radius=11.5
    g2: Circle CenterX=-191.282 CenterY=-53.0314 CenterZ=0 NormalX=0 NormalY=0 NormalZ=1 AngleXU=0 Radius=10.7
  constraints (8):
    c: Coincident(g0,g-3)
    c: PointOnObject(g0,g-4)
    c: Horizontal(g0)
    c: Diameter(g1) = 23
    c: PointOnObject(g1,g0)
    c: DistanceX(g1,g0) = 23.5
    c: Diameter(g2) = 21.4
    c: Coincident(g2,g1)
FEATURE [Part::Part2DObjectPython] ShapeString  # Draft 2D object (typed FeaturePython)
  FontFile = <path>
  Fuse = false
  Justification = 6
  JustificationReference = 0
  KeepLeftMargin = false
  MakeFace = true
  ObliqueAngle = 0
  Placement = pos=(-199,-3.6,-57.5) rot=(1,0,0;1.5708rad)
  ScaleToSize = true
  Size = 10
  String = AS
  Tracking = 0
FEATURE [Sketcher::SketchObject] Sketch133
  ArcFitTolerance = 1e-06
  AttachmentSupport = -> [Binder]
  ExternalGeometry = -> [Binder]
  FullyConstrained = true
  MakeInternals = false
  MapMode = 5
  Placement = pos=(0,9e-16,0) rot=(0,0.707107,0.707107;3.14159rad)
  sketch-geometry (30):
    g0: LineSegment StartX=0 StartY=39.2 StartZ=0 EndX=0 EndY=3.2 EndZ=0
    g1: LineSegment StartX=0 StartY=3.2 StartZ=0 EndX=82.8 EndY=3.2 EndZ=0
    g2: LineSegment StartX=82.8 StartY=3.2 StartZ=0 EndX=82.8 EndY=6.2 EndZ=0
    g3: LineSegment StartX=82.8 StartY=6.2 StartZ=0 EndX=91.752 EndY=6.2 EndZ=0
    g4: LineSegment StartX=0 StartY=39.2 StartZ=0 EndX=195.887 EndY=39.2 EndZ=0
    g5: LineSegment StartX=195.887 StartY=39.2 StartZ=0 EndX=202.765 EndY=20.303 EndZ=0
    g6: LineSegment StartX=192.333 StartY=24.9893 StartZ=0 EndX=196.467 EndY=26.4942 EndZ=0
    g7: LineSegment StartX=196.467 StartY=26.4942 StartZ=0 EndX=194.073 EndY=33.0721 EndZ=0
    g8: LineSegment StartX=194.073 StartY=33.0721 StartZ=0 EndX=189.939 EndY=31.5672 EndZ=0
    g9: LineSegment StartX=189.939 StartY=31.5672 StartZ=0 EndX=192.333 EndY=24.9893 EndZ=0
    g10: ArcOfCircle CenterX=107.6 CenterY=4 CenterZ=0 NormalX=0 NormalY=0 NormalZ=1 AngleXU=0 Radius=16 StartAngle=1.5708 EndAngle=3.00366
    g11: LineSegment StartX=107.6 StartY=20 StartZ=0 EndX=132.428 EndY=20 EndZ=0
    g12: ArcOfCircle [constr] CenterX=132.428 CenterY=4 CenterZ=0 NormalX=0 NormalY=0 NormalZ=1 AngleXU=0 Radius=16 StartAngle=0.314159 EndAngle=1.5708
    g13: LineSegment StartX=147.645 StartY=8.94427 StartZ=0 EndX=176.685 EndY=-80.4316 EndZ=0
    g14: LineSegment StartX=176.685 StartY=-80.4316 StartZ=0 EndX=215.932 EndY=-80.4316 EndZ=0
    g15: ArcOfCircle CenterX=207.583 CenterY=4 CenterZ=0 NormalX=0 NormalY=0 NormalZ=1 AngleXU=0 Radius=17 StartAngle=1.85815 EndAngle=3.57792
    g16: ArcOfCircle CenterX=184.801 CenterY=-67.3089 CenterZ=0 NormalX=0 NormalY=0 NormalZ=1 AngleXU=0 Radius=33.7833 StartAngle=5.88425 EndAngle=6.71952
    g17: LineSegment StartX=192.176 StartY=-3.18451 StartZ=0 EndX=215.42 EndY=-53.0314 EndZ=0
    g18: Circle CenterX=5.6 CenterY=34.8 CenterZ=0 NormalX=0 NormalY=0 NormalZ=1 AngleXU=0 Radius=1.8
    g19: Circle CenterX=5.6 CenterY=7.6 CenterZ=0 NormalX=0 NormalY=0 NormalZ=1 AngleXU=0 Radius=1.8
    g20: Circle CenterX=78.51 CenterY=34.8 CenterZ=0 NormalX=0 NormalY=0 NormalZ=1 AngleXU=0 Radius=1.8
    g21: Circle CenterX=78.51 CenterY=7.6 CenterZ=0 NormalX=0 NormalY=0 NormalZ=1 AngleXU=0 Radius=1.8
    g22: Circle CenterX=184.08 CenterY=34.8 CenterZ=0 NormalX=0 NormalY=0 NormalZ=1 AngleXU=0 Radius=1.8
    g23: Circle CenterX=179.305 CenterY=-76.8316 CenterZ=0 NormalX=0 NormalY=0 NormalZ=1 AngleXU=0 Radius=1.8
    g24: Circle CenterX=213.443 CenterY=-76.8316 CenterZ=0 NormalX=0 NormalY=0 NormalZ=1 AngleXU=0 Radius=1.8
    g25: Circle CenterX=19 CenterY=21.2 CenterZ=0 NormalX=0 NormalY=0 NormalZ=1 AngleXU=0 Radius=6.3
    g26: Circle CenterX=42 CenterY=21.2 CenterZ=0 NormalX=0 NormalY=0 NormalZ=1 AngleXU=0 Radius=6.3
    g27: Circle CenterX=65 CenterY=21.2 CenterZ=0 NormalX=0 NormalY=0 NormalZ=1 AngleXU=0 Radius=6.3
    g28: LineSegment StartX=132.428 StartY=20 StartZ=0 EndX=144.053 EndY=20 EndZ=0
    g29: LineSegment StartX=147.645 StartY=8.94427 StartZ=0 EndX=144.053 EndY=20 EndZ=0
  constraints (65):
    c: Coincident(g0,g-4)
    c: Coincident(g0,g-5)
    c: Coincident(g1,g0)
    c: Coincident(g1,g-6)
    c: Coincident(g2,g1)
    c: Coincident(g2,g-7)
    c: Coincident(g3,g2)
    c: Coincident(g3,g-8)
    c: Coincident(g4,g0)
    c: Coincident(g4,g-16)
    c: Coincident(g5,g4)
    c: Coincident(g5,g-16)
    c: Coincident(g6,g-20)
    c: Coincident(g6,g-21)
    c: Coincident(g7,g6)
    c: Coincident(g7,g-23)
    c: Coincident(g8,g7)
    c: Coincident(g8,g-22)
    c: Coincident(g9,g8)
    c: Coincident(g9,g6)
    c: Equal(g10,g-8)
    c: Coincident(g10,g3)
    c: Coincident(g10,g-9)
    c: Coincident(g11,g10)
    c: Coincident(g11,g-10)
    c: Equal(g12,g-10)
    c: Coincident(g12,g11)
    c: Coincident(g12,g-11)
    c: Coincident(g13,g12)
    c: Coincident(g13,g-12)
    c: Coincident(g14,g13)
    c: Coincident(g14,g-13)
    c: Equal(g15,g-15)
    c: Coincident(g15,g5)
    c: Coincident(g15,g-15)
    c: Equal(g16,g-13)
    c: Coincident(g16,g14)
    c: Coincident(g16,g-14)
    c: Coincident(g17,g15)
    c: Coincident(g17,g16)
    c: Equal(g18,g-28)
    c: Equal(g19,g-29)
    c: Equal(g20,g-26)
    c: Equal(g21,g-27)
    c: Equal(g22,g-17)
    c: Equal(g24,g-25)
    c: Equal(g23,g-24)
    c: Coincident(g23,g-24)
    c: Coincident(g24,g-25)
    c: Coincident(g22,g-17)
    c: Coincident(g20,g-26)
    c: Coincident(g21,g-27)
    c: Coincident(g18,g-28)
    c: Coincident(g19,g-29)
    c: Equal(g25,g-30)
    c: Equal(g26,g-31)
    c: Equal(g27,g-32)
    c: Coincident(g25,g-30)
    c: Coincident(g26,g-31)
    c: Coincident(g27,g-32)
    c: Parallel(g28,g11)
    c: Parallel(g29,g13)
    c: Coincident(g28,g11)
    c: Coincident(g29,g12)
    c: Coincident(g29,g28)
FEATURE [PartDesign::Pad] Pad019
  Direction = (0,1,-2e-16)
  Length = 2
  Length2 = 10
  Profile = -> Sketch133
  ReferenceAxis = -> Sketch133 [N_Axis]
  Refine = true
  Suppressed = false
  Type = 0
FEATURE [Sketcher::SketchObject] Sketch091  label="Sketch091 - forma anteriore"
  ArcFitTolerance = 1e-06
  AttachmentSupport = -> [Pad019]
  ExternalGeometry = -> [Binder]
  FullyConstrained = true
  MakeInternals = false
  MapMode = 5
  Placement = pos=(0,2,0) rot=(0,0.707107,0.707107;3.14159rad)
  sketch-geometry (12):
    g0: Circle CenterX=5.6 CenterY=34.8 CenterZ=0 NormalX=0 NormalY=0 NormalZ=1 AngleXU=0 Radius=1.8
    g1: Circle CenterX=5.6 CenterY=7.6 CenterZ=0 NormalX=0 NormalY=0 NormalZ=1 AngleXU=0 Radius=1.8
    g2: Circle CenterX=78.51 CenterY=34.8 CenterZ=0 NormalX=0 NormalY=0 NormalZ=1 AngleXU=0 Radius=1.8
    g3: Circle CenterX=78.51 CenterY=7.6 CenterZ=0 NormalX=0 NormalY=0 NormalZ=1 AngleXU=0 Radius=1.8
    g4: LineSegment StartX=0 StartY=39.2 StartZ=0 EndX=0 EndY=3.2 EndZ=0
    g5: LineSegment StartX=0 StartY=3.2 StartZ=0 EndX=82.8 EndY=3.2 EndZ=0
    g6: LineSegment StartX=82.8 StartY=3.2 StartZ=0 EndX=82.8 EndY=39.2 EndZ=0
    g7: LineSegment StartX=82.8 StartY=39.2 StartZ=0 EndX=0 EndY=39.2 EndZ=0
    g8: ArcOfCircle CenterX=19 CenterY=21.2 CenterZ=0 NormalX=0 NormalY=0 NormalZ=1 AngleXU=0 Radius=10 StartAngle=1.5708 EndAngle=4.71239
    g9: ArcOfCircle CenterX=65 CenterY=21.2 CenterZ=0 NormalX=0 NormalY=0 NormalZ=1 AngleXU=0 Radius=10 StartAngle=4.71239 EndAngle=7.85398
    g10: LineSegment StartX=19 StartY=31.2 StartZ=0 EndX=65 EndY=31.2 EndZ=0
    g11: LineSegment StartX=19 StartY=11.2 StartZ=0 EndX=65 EndY=11.2 EndZ=0
  constraints (25):
    c: Equal(g2,g-7)
    c: Equal(g3,g-8)
    c: Equal(g1,g-13)
    c: Equal(g0,g-12)
    c: Coincident(g0,g-12)
    c: Coincident(g1,g-13)
    c: Coincident(g3,g-8)
    c: Coincident(g2,g-7)
    c: Coincident(g4,g-4)
    c: Coincident(g4,g-5)
    c: Coincident(g5,g4)
    c: Coincident(g5,g-6)
    c: Coincident(g6,g5)
    c: PointOnObject(g6,g-3)
    c: Vertical(g6)
    c: Coincident(g7,g6)
    c: Coincident(g7,g4)
    c: Tangent(g8,g10) = 1.5708
    c: Tangent(g8,g11) = -1.5708
    c: Tangent(g9,g10) = 1.5708
    c: Tangent(g9,g11) = -1.5708
    c: Equal(g8,g9)
    c: Radius(g8) = 10
    c: Coincident(g8,g-11)
    c: Coincident(g9,g-9)
FEATURE [Sketcher::SketchObject] Sketch093  label="Sketch093 - scavi interni pulsanti"
  ArcFitTolerance = 1e-06
  AttachmentSupport = -> [Pad019]
  ExternalGeometry = -> [Binder]
  FullyConstrained = true
  MakeInternals = false
  MapMode = 5
  Placement = pos=(0,1.8e-15,0) rot=(1,0,0;1.5708rad)
  sketch-geometry (3):
    g0: Circle CenterX=-65 CenterY=21.2 CenterZ=0 NormalX=0 NormalY=0 NormalZ=1 AngleXU=0 Radius=7.3
    g1: Circle CenterX=-42 CenterY=21.2 CenterZ=0 NormalX=0 NormalY=0 NormalZ=1 AngleXU=0 Radius=7.3
    g2: Circle CenterX=-19 CenterY=21.2 CenterZ=0 NormalX=0 NormalY=0 NormalZ=1 AngleXU=0 Radius=7.3
  constraints (6):
    c: Coincident(g0,g-3)
    c: Coincident(g1,g-4)
    c: Coincident(g2,g-5)
    c: Diameter(g0) = 14.6
    c: Diameter(g1) = 14.6
    c: Diameter(g2) = 14.6
FEATURE [Sketcher::SketchObject] Sketch094  label="Sketch094 - forma centrale"
  ArcFitTolerance = 1e-06
  AttachmentSupport = -> [Pad019]
  ExternalGeometry = -> [Binder]
  FullyConstrained = true
  MakeInternals = false
  MapMode = 5
  Placement = pos=(0,2,0) rot=(0,0.707107,0.707107;3.14159rad)
  sketch-geometry (4):
    g0: LineSegment StartX=137.815 StartY=39.2 StartZ=0 EndX=142.655 EndY=24.303 EndZ=0
    g1: LineSegment StartX=110.815 StartY=24.303 StartZ=0 EndX=142.655 EndY=24.303 EndZ=0
    g2: LineSegment StartX=137.815 StartY=39.2 StartZ=0 EndX=110.815 EndY=39.2 EndZ=0
    g3: ArcOfCircle CenterX=92.2534 CenterY=31.7515 CenterZ=0 NormalX=0 NormalY=0 NormalZ=1 AngleXU=0 Radius=20 StartAngle=5.90156 EndAngle=6.66481
  constraints (12):
    c: PointOnObject(g0,g-3)
    c: Tangent(g0,g-5)
    c: Horizontal(g1)
    c: Coincident(g1,g0)
    c: Coincident(g2,g0)
    c: PointOnObject(g2,g-3)
    c: DistanceX(g2,g2) = 27
    c: Vertical(g1,g2)
    c: Coincident(g3,g2)
    c: Radius(g3) = 20
    c: Coincident(g3,g1)
    c: DistanceY(g-6,g0) = 4
FEATURE [Sketcher::SketchObject] Sketch095  label="Sketch095 - forma posteriore"
  ArcFitTolerance = 1e-06
  AttachmentSupport = -> [Pad019]
  ExternalGeometry = -> [Binder]
  FullyConstrained = true
  MakeInternals = false
  MapMode = 5
  Placement = pos=(0,2,0) rot=(0,0.707107,0.707107;3.14159rad)
  sketch-geometry (15):
    g0: LineSegment StartX=137.815 StartY=39.2 StartZ=0 EndX=143.955 EndY=20.303 EndZ=0
    g1: LineSegment StartX=143.955 StartY=20.303 StartZ=0 EndX=190.141 EndY=20.303 EndZ=0
    g2: ArcOfCircle CenterX=184.08 CenterY=34.8 CenterZ=0 NormalX=0 NormalY=0 NormalZ=1 AngleXU=0 Radius=3.5 StartAngle=3.49066 EndAngle=4.71239
    g3: LineSegment StartX=180.791 StartY=33.6029 StartZ=0 EndX=178.754 EndY=39.2 EndZ=0
    g4: LineSegment StartX=184.08 StartY=31.3 StartZ=0 EndX=186.139 EndY=31.3 EndZ=0
    g5: LineSegment StartX=190.141 StartY=20.303 StartZ=0 EndX=186.139 EndY=31.3 EndZ=0
    g6: LineSegment StartX=137.815 StartY=39.2 StartZ=0 EndX=156.815 EndY=39.2 EndZ=0
    g7: LineSegment StartX=178.754 StartY=39.2 StartZ=0 EndX=168.815 EndY=39.2 EndZ=0
    g8: LineSegment StartX=156.815 StartY=31.2 StartZ=0 EndX=168.815 EndY=31.2 EndZ=0
    g9: ArcOfCircle CenterX=176.411 CenterY=35.2 CenterZ=0 NormalX=0 NormalY=0 NormalZ=1 AngleXU=0 Radius=20 StartAngle=2.94023 EndAngle=3.34295
    g10: ArcOfCircle CenterX=188.411 CenterY=35.2 CenterZ=0 NormalX=0 NormalY=0 NormalZ=1 AngleXU=0 Radius=20 StartAngle=2.94023 EndAngle=3.34295
    g11: LineSegment StartX=157.815 StartY=39.2 StartZ=0 EndX=167.815 EndY=39.2 EndZ=0
    g12: LineSegment StartX=157.436 StartY=36.2 StartZ=0 EndX=167.436 EndY=36.2 EndZ=0
    g13: ArcOfCircle CenterX=177.411 CenterY=35.2 CenterZ=0 NormalX=0 NormalY=0 NormalZ=1 AngleXU=0 Radius=20 StartAngle=2.94023 EndAngle=3.09157
    g14: ArcOfCircle CenterX=187.411 CenterY=35.2 CenterZ=0 NormalX=0 NormalY=0 NormalZ=1 AngleXU=0 Radius=20 StartAngle=2.94023 EndAngle=3.09157
  constraints (46):
    c: PointOnObject(g0,g-3)
    c: Tangent(g0,g-6)
    c: Coincident(g1,g0)
    c: Horizontal(g1)
    c: Radius(g2) = 3.5
    c: Coincident(g2,g-5)
    c: PointOnObject(g3,g-3)
    c: Parallel(g3,g-4)
    c: Tangent(g3,g2) = 1.5708
    c: Horizontal(g4)
    c: Tangent(g4,g2) = -1.5708
    c: Coincident(g5,g1)
    c: Parallel(g5,g-4)
    c: Coincident(g5,g4)
    c: DistanceX(g4,g-8) = 3.8
    c: Coincident(g6,g0)
    c: PointOnObject(g6,g-3)
    c: Coincident(g7,g3)
    c: PointOnObject(g7,g-3)
    c: Horizontal(g8)
    c: DistanceX(g6,g7) = 12
    c: Vertical(g8,g6)
    c: Vertical(g7,g8)
    c: DistanceY(g8,g6) = 8
    c: Coincident(g9,g8)
    c: Coincident(g9,g6)
    c: Coincident(g10,g7)
    c: Coincident(g10,g8)
    c: Radius(g9) = 20
    c: Radius(g10) = 20
    c: PointOnObject(g11,g-3)
    c: PointOnObject(g11,g-3)
    c: DistanceX(g11,g11) = 10
    c: DistanceX(g6,g11) = 1
    c: Horizontal(g12)
    c: Equal(g12,g11)
    c: DistanceY(g12,g11) = 3
    c: Coincident(g13,g11)
    c: Coincident(g13,g12)
    c: Radius(g13) = 20
    c: Coincident(g14,g11)
    c: Coincident(g14,g12)
    c: Radius(g14) = 20
    c: DistanceX(g0,g6) = 19
    c: Horizontal(g9,g13)
    c: Horizontal(g0,g-4)
FEATURE [Sketcher::SketchObject] Sketch096  label="Sketch096 - forma impugnatura"
  ArcFitTolerance = 1e-06
  AttachmentSupport = -> [Pad019]
  ExternalGeometry = -> [Binder]
  FullyConstrained = true
  MakeInternals = false
  MapMode = 5
  Placement = pos=(0,2,0) rot=(0,0.707107,0.707107;3.14159rad)
  sketch-geometry (8):
    g0: LineSegment StartX=176.685 StartY=-80.4316 StartZ=0 EndX=143.955 EndY=20.303 EndZ=0
    g1: LineSegment StartX=176.685 StartY=-80.4316 StartZ=0 EndX=215.932 EndY=-80.4316 EndZ=0
    g2: Circle CenterX=179.305 CenterY=-76.8316 CenterZ=0 NormalX=0 NormalY=0 NormalZ=1 AngleXU=0 Radius=3
    g3: Circle CenterX=213.443 CenterY=-76.8316 CenterZ=0 NormalX=0 NormalY=0 NormalZ=1 AngleXU=0 Radius=3
    g4: LineSegment StartX=143.955 StartY=20.303 StartZ=0 EndX=202.765 EndY=20.303 EndZ=0
    g5: LineSegment StartX=215.42 StartY=-53.0314 StartZ=0 EndX=192.176 EndY=-3.18451 EndZ=0
    g6: ArcOfCircle CenterX=184.801 CenterY=-67.3089 CenterZ=0 NormalX=0 NormalY=0 NormalZ=1 AngleXU=0 Radius=33.7833 StartAngle=5.88425 EndAngle=6.71952
    g7: ArcOfCircle CenterX=207.583 CenterY=4 CenterZ=0 NormalX=0 NormalY=0 NormalZ=1 AngleXU=0 Radius=17 StartAngle=1.85815 EndAngle=3.57792
  constraints (19):
    c: Coincident(g0,g-4)
    c: PointOnObject(g0,g-3)
    c: Horizontal(g0,g-7)
    c: Coincident(g1,g0)
    c: Coincident(g1,g-5)
    c: Diameter(g2) = 6
    c: Diameter(g3) = 6
    c: Coincident(g2,g-9)
    c: Coincident(g3,g-10)
    c: Coincident(g4,g0)
    c: Coincident(g5,g-6)
    c: Coincident(g6,g1)
    c: Coincident(g6,g5)
    c: Equal(g-5,g6)
    c: Coincident(g5,g-7)
    c: Coincident(g4,g-7)
    c: Tangent(g7,g-7)
    c: Coincident(g7,g4)
    c: Coincident(g7,g5)
FEATURE [Sketcher::SketchObject] Sketch097
  ArcFitTolerance = 1e-06
  AttachmentSupport = -> [Pad019]
  ExternalGeometry = -> [Binder]
  FullyConstrained = true
  MakeInternals = false
  MapMode = 5
  Placement = pos=(0,2,0) rot=(0,0.707107,0.707107;3.14159rad)
  sketch-geometry (4):
    g0: LineSegment StartX=90 StartY=36.8 StartZ=0 EndX=108 EndY=36.8 EndZ=0
    g1: LineSegment StartX=108 StartY=36.8 StartZ=0 EndX=108 EndY=26.8 EndZ=0
    g2: LineSegment StartX=108 StartY=26.8 StartZ=0 EndX=90 EndY=26.8 EndZ=0
    g3: ArcOfCircle CenterX=94 CenterY=31.8 CenterZ=0 NormalX=0 NormalY=0 NormalZ=1 AngleXU=0 Radius=6.40312 StartAngle=2.24554 EndAngle=4.03765
  constraints (13):
    c: Horizontal(g0)
    c: Coincident(g1,g0)
    c: Vertical(g1)
    c: DistanceX(g0,g0) = 18
    c: DistanceY(g1,g1) = 10
    c: Coincident(g2,g1)
    c: Horizontal(g2)
    c: Equal(g2,g0)
    c: DistanceY(g0,g-3) = 2.4
    c: Coincident(g3,g0)
    c: Coincident(g3,g2)
    c: DistanceX(g2,g3) = 4
    c: DistanceX(g-3,g0) = 90
FEATURE [PartDesign::Chamfer] Chamfer015
  Angle = 45
  Base = -> Pad019 [Edge19,Edge22,Edge79]
  BaseFeature = -> Pad019
  ChamferType = 0
  FlipDirection = false
  Refine = true
  Size = 1.9
  Size2 = 1
  SupportTransform = false
  Suppressed = false
  UseAllEdges = false
FEATURE [PartDesign::Pocket] Pocket002
  BaseFeature = -> Chamfer015
  Direction = (0,1,-2e-16)
  Length = 1.2
  Length2 = 5
  Profile = -> Sketch093
  ReferenceAxis = -> Sketch093 [N_Axis]
  Refine = true
  Suppressed = false
  Type = 0
FEATURE [PartDesign::Pad] Pad005
  BaseFeature = -> Pocket002
  Direction = (0,1,-2e-16)
  Length = 1.6
  Length2 = 10
  Profile = -> Sketch091
  ReferenceAxis = -> Sketch091 [N_Axis]
  Refine = true
  Suppressed = false
  Type = 0
FEATURE [Sketcher::SketchObject] Sketch092  label="Sketch092 - scavi per viti anteriori"
  ArcFitTolerance = 1e-06
  AttachmentSupport = -> [Pad005]
  ExternalGeometry = -> [Binder]
  FullyConstrained = true
  MakeInternals = false
  MapMode = 5
  Placement = pos=(0,3.6,0) rot=(0,0.707107,0.707107;3.14159rad)
  sketch-geometry (20):
    g0: ArcOfCircle CenterX=5.6 CenterY=7.6 CenterZ=0 NormalX=0 NormalY=0 NormalZ=1 AngleXU=0 Radius=3.5 StartAngle=0 EndAngle=1.5708
    g1: ArcOfCircle CenterX=5.6 CenterY=34.8 CenterZ=0 NormalX=0 NormalY=0 NormalZ=1 AngleXU=0 Radius=3.5 StartAngle=4.71239 EndAngle=6.28319
    g2: ArcOfCircle CenterX=78.51 CenterY=34.8 CenterZ=0 NormalX=0 NormalY=0 NormalZ=1 AngleXU=0 Radius=3.5 StartAngle=3.14159 EndAngle=4.71239
    g3: ArcOfCircle CenterX=78.51 CenterY=7.6 CenterZ=0 NormalX=0 NormalY=0 NormalZ=1 AngleXU=0 Radius=3.5 StartAngle=1.5708 EndAngle=3.14159
    g4: LineSegment StartX=0 StartY=3.2 StartZ=0 EndX=0 EndY=11.1 EndZ=0
    g5: LineSegment StartX=0 StartY=11.1 StartZ=0 EndX=5.6 EndY=11.1 EndZ=0
    g6: LineSegment StartX=0 StartY=3.2 StartZ=0 EndX=9.1 EndY=3.2 EndZ=0
    g7: LineSegment StartX=9.1 StartY=3.2 StartZ=0 EndX=9.1 EndY=7.6 EndZ=0
    g8: LineSegment StartX=0 StartY=39.2 StartZ=0 EndX=0 EndY=31.3 EndZ=0
    g9: LineSegment StartX=0 StartY=31.3 StartZ=0 EndX=5.6 EndY=31.3 EndZ=0
    g10: LineSegment StartX=0 StartY=39.2 StartZ=0 EndX=9.1 EndY=39.2 EndZ=0
    g11: LineSegment StartX=9.1 StartY=39.2 StartZ=0 EndX=9.1 EndY=34.8 EndZ=0
    g12: LineSegment StartX=82.8 StartY=39.2 StartZ=0 EndX=75.01 EndY=39.2 EndZ=0
    g13: LineSegment StartX=82.8 StartY=39.2 StartZ=0 EndX=82.8 EndY=31.3 EndZ=0
    g14: LineSegment StartX=82.8 StartY=31.3 StartZ=0 EndX=78.51 EndY=31.3 EndZ=0
    g15: LineSegment StartX=82.8 StartY=3.2 StartZ=0 EndX=75.01 EndY=3.2 EndZ=0
    g16: LineSegment StartX=75.01 StartY=3.2 StartZ=0 EndX=75.01 EndY=7.6 EndZ=0
    g17: LineSegment StartX=82.8 StartY=3.2 StartZ=0 EndX=82.8 EndY=11.1 EndZ=0
    g18: LineSegment StartX=82.8 StartY=11.1 StartZ=0 EndX=78.51 EndY=11.1 EndZ=0
    g19: LineSegment StartX=75.01 StartY=39.2 StartZ=0 EndX=75.01 EndY=34.8 EndZ=0
  constraints (48):
    c: Radius(g0) = 3.5
    c: Coincident(g0,g-10)
    c: Radius(g1) = 3.5
    c: Coincident(g1,g-9)
    c: Radius(g2) = 3.5
    c: Coincident(g2,g-8)
    c: Radius(g3) = 3.5
    c: Coincident(g3,g-7)
    c: Coincident(g4,g-5)
    c: PointOnObject(g4,g-4)
    c: Coincident(g5,g4)
    c: Horizontal(g5)
    c: Coincident(g6,g4)
    c: PointOnObject(g6,g-5)
    c: Coincident(g7,g6)
    c: Vertical(g7)
    c: Coincident(g8,g-4)
    c: PointOnObject(g8,g-4)
    c: Coincident(g9,g8)
    c: Horizontal(g9)
    c: Coincident(g10,g8)
    c: PointOnObject(g10,g-3)
    c: Coincident(g11,g10)
    c: Vertical(g11)
    c: PointOnObject(g12,g-3)
    c: PointOnObject(g12,g-3)
    c: Coincident(g13,g12)
    c: Vertical(g13)
    c: Coincident(g14,g13)
    c: Horizontal(g14)
    c: Coincident(g15,g-6)
    c: PointOnObject(g15,g-5)
    c: Coincident(g16,g15)
    c: Vertical(g16)
    c: Coincident(g17,g15)
    c: Coincident(g18,g17)
    c: Horizontal(g18)
    c: Tangent(g3,g18) = -1.5708
    c: Tangent(g16,g3) = 1.5708
    c: Coincident(g19,g12)
    c: Vertical(g19)
    c: Tangent(g2,g19) = -1.5708
    c: Tangent(g2,g14) = 1.5708
    c: Tangent(g0,g7) = -1.5708
    c: Tangent(g0,g5) = 1.5708
    c: Tangent(g9,g1) = -1.5708
    c: Tangent(g1,g11) = 1.5708
    c: Tangent(g17,g13)
FEATURE [PartDesign::Pocket] Pocket001
  BaseFeature = -> Pad005
  Direction = (0,-1,2e-16)
  Length = 1.6
  Length2 = 5
  Profile = -> Sketch092
  ReferenceAxis = -> Sketch092 [N_Axis]
  Refine = true
  Suppressed = false
  Type = 0
FEATURE [PartDesign::Pad] Pad006
  BaseFeature = -> Pocket001
  Direction = (0,1,-2e-16)
  Length = 0.8
  Length2 = 10
  Profile = -> Sketch094
  ReferenceAxis = -> Sketch094 [N_Axis]
  Refine = true
  Suppressed = false
  Type = 0
FEATURE [PartDesign::Pad] Pad007
  BaseFeature = -> Pad006
  Direction = (0,1,-2e-16)
  Length = 2
  Length2 = 10
  Profile = -> Sketch095
  ReferenceAxis = -> Sketch095 [N_Axis]
  Refine = true
  Suppressed = false
  Type = 0
FEATURE [PartDesign::Pad] Pad008  label="Pad008 - forma impugnatura"
  BaseFeature = -> Pad007
  Direction = (0,1,-2e-16)
  Length = 1.6
  Length2 = 10
  Profile = -> Sketch096
  ReferenceAxis = -> Sketch096 [N_Axis]
  Refine = true
  Suppressed = false
  Type = 0
FEATURE [PartDesign::Pad] Pad009
  BaseFeature = -> Pad008
  Direction = (0,1,-2e-16)
  Length = 1.6
  Length2 = 10
  Profile = -> Sketch097
  ReferenceAxis = -> Sketch097 [N_Axis]
  Refine = true
  Suppressed = false
  Type = 0
FEATURE [Sketcher::SketchObject] Sketch098
  ArcFitTolerance = 1e-06
  AttachmentSupport = -> [Pad006]
  ExternalGeometry = -> [Binder]
  FullyConstrained = true
  MakeInternals = false
  MapMode = 5
  Placement = pos=(0,2.8,-7e-16) rot=(0,0.707107,0.707107;3.14159rad)
  sketch-geometry (4):
    g0: LineSegment StartX=118 StartY=39.2 StartZ=0 EndX=129 EndY=39.2 EndZ=0
    g1: LineSegment StartX=120.599 StartY=31.2 StartZ=0 EndX=131.599 EndY=31.2 EndZ=0
    g2: LineSegment StartX=129 StartY=39.2 StartZ=0 EndX=131.599 EndY=31.2 EndZ=0
    g3: LineSegment StartX=118 StartY=39.2 StartZ=0 EndX=120.599 EndY=31.2 EndZ=0
  constraints (12):
    c: PointOnObject(g0,g-3)
    c: PointOnObject(g0,g-3)
    c: DistanceX(g0,g0) = 11
    c: Horizontal(g1)
    c: Equal(g1,g0)
    c: Coincident(g2,g0)
    c: Coincident(g3,g0)
    c: Parallel(g-4,g2)
    c: Coincident(g1,g2)
    c: Coincident(g1,g3)
    c: DistanceY(g1,g0) = 8
    c: DistanceX(g-3,g0) = 118
FEATURE [Sketcher::SketchObject] Sketch099
  ArcFitTolerance = 1e-06
  AttachmentSupport = -> [Pad008]
  ExternalGeometry = -> [Binder]
  FullyConstrained = true
  MakeInternals = false
  MapMode = 5
  Placement = pos=(0,3.6,0) rot=(0,0.707107,0.707107;3.14159rad)
  sketch-geometry (13):
    g0: LineSegment StartX=192.176 StartY=-3.18451 StartZ=0 EndX=196.804 EndY=-13.1108 EndZ=0
    g1: LineSegment [constr] StartX=202.765 StartY=20.303 StartZ=0 EndX=181.223 EndY=20.303 EndZ=0
    g2: LineSegment [constr] StartX=181.223 StartY=20.303 StartZ=0 EndX=181.223 EndY=-3.18451 EndZ=0
    g3: ArcOfCircle CenterX=181.223 CenterY=-20.3764 CenterZ=0 NormalX=0 NormalY=0 NormalZ=1 AngleXU=0 Radius=17.1918 StartAngle=0.436332 EndAngle=1.57079
    g4: ArcOfEllipse CenterX=181.223 CenterY=8.55923 CenterZ=0 NormalX=0 NormalY=0 NormalZ=1 MajorRadius=23.4779 MinorRadius=11.7437 AngleXU=0 StartAngle=1.5708 EndAngle=4.71239
    g5: LineSegment [constr] StartX=204.701 StartY=8.55923 StartZ=0 EndX=157.745 EndY=8.55923 EndZ=0
    g6: LineSegment [constr] StartX=181.223 StartY=20.303 StartZ=0 EndX=181.223 EndY=-3.18451 EndZ=0
    g7: GeomPoint [constr] X=201.553 Y=8.55923 Z=0
    g8: GeomPoint [constr] X=160.894 Y=8.55923 Z=0
    g9: GeomPoint [constr] X=181.223 Y=-3.18451 Z=0
    g10: LineSegment StartX=181.223 StartY=20.303 StartZ=0 EndX=202.765 EndY=20.303 EndZ=0
    g11: ArcOfCircle CenterX=207.583 CenterY=4 CenterZ=0 NormalX=0 NormalY=0 NormalZ=1 AngleXU=0 Radius=17 StartAngle=1.85815 EndAngle=3.57792
    g12: LineSegment [constr] StartX=172.411 StartY=39.2 StartZ=0 EndX=192.176 EndY=-3.18451 EndZ=0
  constraints (27):
    c: Coincident(g1,g-7)
    c: Horizontal(g1)
    c: Coincident(g2,g1)
    c: Vertical(g2)
    c: Horizontal(g2,g0)
    c: Coincident(g3,g0)
    c: Coincident(g3,g2)
    c: InternalAlignment(g5-g8 -> g4) x4
    c: Horizontal(g5)
    c: PointOnObject(g4,g2)
    c: Coincident(g4,g1)
    c: DistanceX(g-3,g5) = 10.1
    c: Coincident(g4,g2)
    c: Tangent(g3,g-5)
    c: PointOnObject(g9,g4)
    c: PointOnObject(g9,g3)
    c: Tangent(g4,g3,g9) = 1.5708
    c: Coincident(g10,g1)
    c: Coincident(g10,g1)
    c: Equal(g11,g-4)
    c: Coincident(g11,g1)
    c: Coincident(g11,g0)
    c: PointOnObject(g12,g-6)
    c: PointOnObject(g1,g12)
    c: Tangent(g12,g-5) = -1.5708
    c: Tangent(g0,g-5) = -1.5708
    c: Horizontal(g9,g12)
FEATURE [Sketcher::SketchObject] Sketch106  label="Sketch106 - smusso impuniatura interno"
  ArcFitTolerance = 1e-06
  AttachmentSupport = -> [Pad008]
  ExternalGeometry = -> [Pad008]
  FullyConstrained = true
  MakeInternals = false
  MapMode = 5
  Placement = pos=(0,-1.585e-13,-80.4316) rot=(1,0,0;3.14159rad)
  sketch-geometry (9):
    g0: LineSegment StartX=-176.685 StartY=-3.6 StartZ=0 EndX=-176.685 EndY=-2.14526e-11 EndZ=0
    g1: LineSegment [constr] StartX=-176.685 StartY=-1.416e-13 StartZ=0 EndX=-176.685 EndY=-2.14524e-11 EndZ=0
    g2: LineSegment [constr] StartX=-186.685 StartY=-3.6 StartZ=0 EndX=-186.685 EndY=-2.14526e-11 EndZ=0
    g3: ArcOfEllipse CenterX=-186.685 CenterY=-2.14524e-11 CenterZ=0 NormalX=0 NormalY=0 NormalZ=1 MajorRadius=10 MinorRadius=3.6 AngleXU=3.14159 StartAngle=1.5708 EndAngle=3.14159
    g4: LineSegment [constr] StartX=-196.685 StartY=-1.416e-13 StartZ=0 EndX=-176.685 EndY=-1.416e-13 EndZ=0
    g5: LineSegment [constr] StartX=-186.685 StartY=-3.6 StartZ=0 EndX=-186.685 EndY=3.6 EndZ=0
    g6: GeomPoint [constr] X=-196.015 Y=-1.389e-13 Z=0
    g7: GeomPoint [constr] X=-177.356 Y=-1.416e-13 Z=0
    g8: LineSegment StartX=-176.685 StartY=-3.6 StartZ=0 EndX=-186.685 EndY=-3.6 EndZ=0
  constraints (15):
    c: PointOnObject(g2,g-3)
    c: Coincident(g1,g-5)
    c: DistanceY(g1,g1) = 0
    c: Coincident(g0,g1)
    c: DistanceX(g2,g-5) = 10
    c: Vertical(g2)
    c: Horizontal(g2,g0)
    c: InternalAlignment(g4-g7 -> g3) x4
    c: Coincident(g3,g2)
    c: Horizontal(g4)
    c: Coincident(g3,g0)
    c: Tangent(g0,g-5) = 1.5708
    c: Coincident(g3,g2)
    c: Coincident(g8,g0)
    c: Coincident(g8,g2)
FEATURE [Sketcher::SketchObject] Sketch107  label="Sketch107 - smusso impugnatura esterno"
  ArcFitTolerance = 1e-06
  AttachmentSupport = -> [Pad008]
  ExternalGeometry = -> [Pad008]
  FullyConstrained = true
  MakeInternals = false
  MapMode = 5
  Placement = pos=(0,-1.585e-13,-80.4316) rot=(1,0,0;3.14159rad)
  sketch-geometry (9):
    g0: LineSegment [constr] StartX=-215.932 StartY=-1.416e-13 StartZ=0 EndX=-215.932 EndY=-6.75e-14 EndZ=0
    g1: LineSegment StartX=-215.932 StartY=-3.6 StartZ=0 EndX=-215.932 EndY=-6.75e-14 EndZ=0
    g2: LineSegment StartX=-215.932 StartY=-3.6 StartZ=0 EndX=-205.932 EndY=-3.6 EndZ=0
    g3: LineSegment [constr] StartX=-205.932 StartY=-3.6 StartZ=0 EndX=-205.932 EndY=-6.75e-14 EndZ=0
    g4: ArcOfEllipse CenterX=-205.932 CenterY=-6.75e-14 CenterZ=0 NormalX=0 NormalY=0 NormalZ=1 MajorRadius=10 MinorRadius=3.6 AngleXU=-3.14159 StartAngle=-2.66e-14 EndAngle=1.5708
    g5: LineSegment [constr] StartX=-215.932 StartY=-1.416e-13 StartZ=0 EndX=-195.932 EndY=-1.416e-13 EndZ=0
    g6: LineSegment [constr] StartX=-205.932 StartY=-3.6 StartZ=0 EndX=-205.932 EndY=3.6 EndZ=0
    g7: GeomPoint [constr] X=-215.262 Y=-1.568e-13 Z=0
    g8: GeomPoint [constr] X=-196.602 Y=-1.551e-13 Z=0
  constraints (16):
    c: Coincident(g0,g-6)
    c: PointOnObject(g0,g-6)
    c: DistanceY(g0,g0) = 0
    c: Coincident(g1,g-6)
    c: Coincident(g1,g0)
    c: Tangent(g2,g-3)
    c: DistanceX(g2,g2) = 10
    c: Coincident(g3,g2)
    c: Vertical(g3)
    c: Horizontal(g3,g0)
    c: InternalAlignment(g5-g8 -> g4) x4
    c: Coincident(g4,g3)
    c: Horizontal(g5)
    c: Coincident(g4,g0)
    c: Coincident(g4,g2)
    c: PointOnObject(g2,g1)
FEATURE [Sketcher::SketchObject] Sketch108
  ArcFitTolerance = 1e-06
  AttachmentOffset = pos=(0,0,-1.6) rot=(0,0,1;0rad)
  AttachmentSupport = -> [Pad008]
  ExternalGeometry = -> [Binder]
  FullyConstrained = true
  MakeInternals = false
  MapMode = 5
  Placement = pos=(0,2,4e-16) rot=(0,0.707107,0.707107;3.14159rad)
  sketch-geometry (14):
    g0: LineSegment StartX=192.176 StartY=-3.18451 StartZ=0 EndX=193.827 EndY=-6.72678 EndZ=0
    g1: LineSegment [constr] StartX=202.765 StartY=20.303 StartZ=0 EndX=181.223 EndY=20.303 EndZ=0
    g2: LineSegment [constr] StartX=181.223 StartY=20.303 StartZ=0 EndX=181.223 EndY=1.30297 EndZ=0
    g3: ArcOfCircle CenterX=181.223 CenterY=-12.6042 CenterZ=0 NormalX=0 NormalY=0 NormalZ=1 AngleXU=0 Radius=13.9072 StartAngle=0.436332 EndAngle=1.5708
    g4: ArcOfEllipse CenterX=181.223 CenterY=10.803 CenterZ=0 NormalX=0 NormalY=0 NormalZ=1 MajorRadius=14.4779 MinorRadius=9.5 AngleXU=0 StartAngle=1.5708 EndAngle=4.71239
    g5: LineSegment [constr] StartX=195.701 StartY=10.803 StartZ=0 EndX=166.745 EndY=10.803 EndZ=0
    g6: LineSegment [constr] StartX=181.223 StartY=20.303 StartZ=0 EndX=181.223 EndY=1.30297 EndZ=0
    g7: GeomPoint [constr] X=192.148 Y=10.803 Z=0
    g8: GeomPoint [constr] X=170.298 Y=10.803 Z=0
    g9: LineSegment StartX=181.223 StartY=20.303 StartZ=0 EndX=202.765 EndY=20.303 EndZ=0
    g10: ArcOfCircle CenterX=207.583 CenterY=4 CenterZ=0 NormalX=0 NormalY=0 NormalZ=1 AngleXU=0 Radius=17 StartAngle=1.85815 EndAngle=3.57792
    g11: LineSegment [constr] StartX=172.411 StartY=39.2 StartZ=0 EndX=192.176 EndY=-3.18451 EndZ=0
    g12: GeomPoint [constr] X=181.223 Y=1.30297 Z=0
    g13: GeomPoint [constr] X=181.223 Y=1.30297 Z=0
  constraints (28):
    c: Coincident(g1,g-7)
    c: Horizontal(g1)
    c: Coincident(g2,g1)
    c: Vertical(g2)
    c: Coincident(g3,g2)
    c: InternalAlignment(g5-g8 -> g4) x4
    c: Horizontal(g5)
    c: PointOnObject(g4,g2)
    c: Coincident(g4,g1)
    c: DistanceX(g-3,g5) = 19.1
    c: Coincident(g4,g2)
    c: Coincident(g9,g1)
    c: Coincident(g9,g1)
    c: Coincident(g10,g1)
    c: Coincident(g10,g0)
    c: PointOnObject(g11,g-6)
    c: PointOnObject(g1,g11)
    c: DistanceY(g2,g1) = 19
    c: Coincident(g10,g-4)
    c: PointOnObject(g12,g4)
    c: PointOnObject(g12,g3)
    c: Tangent(g11,g-5) = -1.5708
    c: Tangent(g0,g-5) = -1.5708
    c: Tangent(g3,g0) = 1.5708
    c: PointOnObject(g13,g4)
    c: PointOnObject(g13,g3)
    c: Tangent(g4,g3,g13) = 1.5708
    c: Horizontal(g11,g0)
FEATURE [Part::Part2DObjectPython] Clone2D  label="Sketch108 (2D)"  # Draft 2D object (typed FeaturePython)
  Fuse = false
  Objects = -> [Sketch108]
  Placement = pos=(0,2,4e-16) rot=(0,0.707107,0.707107;3.14159rad)
  Scale = (1,1,1)
FEATURE [Sketcher::SketchObject] Sketch109
  ArcFitTolerance = 1e-06
  AttachmentOffset = pos=(0,0,-3.5) rot=(0,0,1;0rad)
  AttachmentSupport = -> [Pad008]
  ExternalGeometry = -> [Binder]
  FullyConstrained = true
  MakeInternals = false
  MapMode = 5
  Placement = pos=(0,0.1,8e-16) rot=(0,0.707107,0.707107;3.14159rad)
  sketch-geometry (1):
    g0: GeomPoint X=197.47 Y=8.55923 Z=0
  constraints (1):
    c: Symmetric(g-7,g-5,g0)
FEATURE [PartDesign::Chamfer] Chamfer005
  Angle = 45
  Base = -> Pad009 [Edge215,Edge212]
  BaseFeature = -> Pad009
  ChamferType = 1
  FlipDirection = false
  Refine = true
  Size = 1.5
  Size2 = 2.8
  SupportTransform = false
  Suppressed = false
  UseAllEdges = false
FEATURE [Sketcher::SketchObject] Sketch111
  ArcFitTolerance = 1e-06
  AttachmentSupport = -> [Pad009]
  ExternalGeometry = -> [Pad009]
  FullyConstrained = true
  MakeInternals = false
  MapMode = 5
  Placement = pos=(0,3.6,-8e-16) rot=(0,0.707107,0.707107;3.14159rad)
  sketch-geometry (21):
    g0: LineSegment [constr] StartX=97 StartY=36.8 StartZ=0 EndX=97 EndY=26.8 EndZ=0
    g1: LineSegment StartX=97 StartY=28.6 StartZ=0 EndX=97 EndY=27.8 EndZ=0
    g2: LineSegment StartX=97 StartY=27.8 StartZ=0 EndX=108 EndY=27.8 EndZ=0
    g3: LineSegment StartX=108 StartY=27.8 StartZ=0 EndX=108 EndY=28.6 EndZ=0
    g4: LineSegment StartX=108 StartY=28.6 StartZ=0 EndX=97 EndY=28.6 EndZ=0
    g5: LineSegment StartX=97 StartY=35.8 StartZ=0 EndX=97 EndY=35 EndZ=0
    g6: LineSegment StartX=97 StartY=35 StartZ=0 EndX=108 EndY=35 EndZ=0
    g7: LineSegment StartX=108 StartY=35 StartZ=0 EndX=108 EndY=35.8 EndZ=0
    g8: LineSegment StartX=108 StartY=35.8 StartZ=0 EndX=97 EndY=35.8 EndZ=0
    g9: LineSegment StartX=97 StartY=30.4 StartZ=0 EndX=97 EndY=29.6 EndZ=0
    g10: LineSegment StartX=97 StartY=29.6 StartZ=0 EndX=108 EndY=29.6 EndZ=0
    g11: LineSegment StartX=108 StartY=29.6 StartZ=0 EndX=108 EndY=30.4 EndZ=0
    g12: LineSegment StartX=108 StartY=30.4 StartZ=0 EndX=97 EndY=30.4 EndZ=0
    g13: LineSegment StartX=97 StartY=34 StartZ=0 EndX=97 EndY=33.2 EndZ=0
    g14: LineSegment StartX=97 StartY=33.2 StartZ=0 EndX=108 EndY=33.2 EndZ=0
    g15: LineSegment StartX=108 StartY=33.2 StartZ=0 EndX=108 EndY=34 EndZ=0
    g16: LineSegment StartX=108 StartY=34 StartZ=0 EndX=97 EndY=34 EndZ=0
    g17: LineSegment StartX=97 StartY=32.2 StartZ=0 EndX=97 EndY=31.4 EndZ=0
    g18: LineSegment StartX=97 StartY=31.4 StartZ=0 EndX=108 EndY=31.4 EndZ=0
    g19: LineSegment StartX=108 StartY=31.4 StartZ=0 EndX=108 EndY=32.2 EndZ=0
    g20: LineSegment StartX=108 StartY=32.2 StartZ=0 EndX=97 EndY=32.2 EndZ=0
  constraints (54):
    c: Vertical(g0)
    c: PointOnObject(g0,g-3)
    c: PointOnObject(g0,g-4)
    c: DistanceX(g0,g-5) = 11
    c: Coincident(g1,g2)
    c: Coincident(g2,g3)
    c: Coincident(g3,g4)
    c: Coincident(g4,g1)
    c: Horizontal(g2)
    c: Horizontal(g4)
    c: Tangent(g1,g0)
    c: Tangent(g3,g-5)
    c: DistanceY(g2,g3) = 0.8
    c: Coincident(g5,g6)
    c: Coincident(g6,g7)
    c: Coincident(g7,g8)
    c: Coincident(g8,g5)
    c: Horizontal(g6)
    c: Horizontal(g8)
    c: DistanceY(g6,g7) = 0.8
    c: Coincident(g9,g10)
    c: Coincident(g10,g11)
    c: Coincident(g11,g12)
    c: Coincident(g12,g9)
    c: Horizontal(g10)
    c: Horizontal(g12)
    c: DistanceY(g10,g11) = 0.8
    c: Tangent(g5,g0)
    c: Tangent(g7,g-5)
    c: Tangent(g9,g0)
    c: Tangent(g11,g-5)
    c: Coincident(g13,g14)
    c: Coincident(g14,g15)
    c: Coincident(g15,g16)
    c: Coincident(g16,g13)
    c: Horizontal(g14)
    c: Horizontal(g16)
    c: DistanceY(g14,g15) = 0.8
    c: Tangent(g13,g0)
    c: Tangent(g15,g-5)
    c: Coincident(g17,g18)
    c: Coincident(g18,g19)
    c: Coincident(g19,g20)
    c: Coincident(g20,g17)
    c: Horizontal(g18)
    c: Horizontal(g20)
    c: DistanceY(g18,g19) = 0.8
    c: Tangent(g17,g0)
    c: Tangent(g19,g-5)
    c: DistanceY(g1,g9) = 1
    c: DistanceY(g9,g17) = 1
    c: DistanceY(g17,g13) = 1
    c: DistanceY(g13,g5) = 1
    c: DistanceY(g0,g1) = 1
FEATURE [PartDesign::Pocket] Pocket004
  BaseFeature = -> Chamfer005
  Direction = (0,-1,2e-16)
  Length = 1
  Length2 = 5
  Profile = -> Sketch111
  ReferenceAxis = -> Sketch111 [N_Axis]
  Refine = true
  Suppressed = false
  Type = 0
FEATURE [PartDesign::Pad] Pad010
  BaseFeature = -> Pocket004
  Direction = (0,1,-2e-16)
  Length = 1.2
  Length2 = 10
  Profile = -> Sketch098
  ReferenceAxis = -> Sketch098 [N_Axis]
  Refine = true
  Suppressed = false
  Type = 0
FEATURE [PartDesign::Chamfer] Chamfer006
  Angle = 45
  Base = -> Pad010 [Edge291]
  BaseFeature = -> Pad010
  ChamferType = 1
  FlipDirection = false
  Refine = true
  Size = 1
  Size2 = 6
  SupportTransform = false
  Suppressed = false
  UseAllEdges = false
FEATURE [Sketcher::SketchObject] Sketch110
  ArcFitTolerance = 1e-06
  AttachmentSupport = -> [Pad010]
  ExternalGeometry = -> [Sketch098]
  FullyConstrained = true
  MakeInternals = false
  MapMode = 5
  Placement = pos=(0,4,-9e-16) rot=(0,0.707107,0.707107;3.14159rad)
  sketch-geometry (8):
    g0: LineSegment StartX=119.69 StartY=34 StartZ=0 EndX=130.69 EndY=34 EndZ=0
    g1: LineSegment StartX=119.95 StartY=33.2 StartZ=0 EndX=130.95 EndY=33.2 EndZ=0
    g2: LineSegment StartX=119.137 StartY=35.7 StartZ=0 EndX=130.137 EndY=35.7 EndZ=0
    g3: LineSegment StartX=118.877 StartY=36.5 StartZ=0 EndX=129.877 EndY=36.5 EndZ=0
    g4: LineSegment StartX=118.877 StartY=36.5 StartZ=0 EndX=119.137 EndY=35.7 EndZ=0
    g5: LineSegment StartX=129.877 StartY=36.5 StartZ=0 EndX=130.137 EndY=35.7 EndZ=0
    g6: LineSegment StartX=119.69 StartY=34 StartZ=0 EndX=119.95 EndY=33.2 EndZ=0
    g7: LineSegment StartX=130.69 StartY=34 StartZ=0 EndX=130.95 EndY=33.2 EndZ=0
  constraints (24):
    c: Horizontal(g0)
    c: Horizontal(g1)
    c: Horizontal(g2)
    c: Horizontal(g3)
    c: Equal(g1,g-5)
    c: Equal(g0,g-5)
    c: Equal(g2,g-5)
    c: Equal(g3,g-5)
    c: PointOnObject(g0,g-3)
    c: PointOnObject(g1,g-3)
    c: PointOnObject(g2,g-3)
    c: PointOnObject(g3,g-3)
    c: Coincident(g4,g3)
    c: Coincident(g4,g2)
    c: Coincident(g5,g3)
    c: Coincident(g5,g2)
    c: Coincident(g6,g0)
    c: Coincident(g6,g1)
    c: Coincident(g7,g0)
    c: Coincident(g7,g1)
    c: DistanceY(g1,g0) = 0.8
    c: DistanceY(g2,g3) = 0.8
    c: DistanceY(g-5,g1) = 2
    c: DistanceY(g-5,g2) = 4.5
FEATURE [PartDesign::Pocket] Pocket003
  BaseFeature = -> Chamfer006
  Direction = (0,-1,2e-16)
  Length = 1
  Length2 = 5
  Profile = -> Sketch110
  ReferenceAxis = -> Sketch110 [N_Axis]
  Refine = true
  Suppressed = false
  Type = 0
FEATURE [PartDesign::SubtractivePipe] SubtractivePipe
  AuxilleryCurvelinear = true
  AuxillerySpineTangent = false
  BaseFeature = -> Pocket003
  Binormal = (0,0,0)
  Mode = 0
  Profile = -> Sketch106
  Refine = true
  Spine = -> Pad008 [Edge215]
  SpineTangent = false
  Suppressed = false
  Transformation = 0
  Transition = 0
FEATURE [PartDesign::SubtractivePipe] SubtractivePipe001
  AuxilleryCurvelinear = true
  AuxillerySpineTangent = false
  BaseFeature = -> SubtractivePipe
  Binormal = (0,0,0)
  Mode = 0
  Profile = -> Sketch107
  Refine = true
  Spine = -> Pad008 [Edge213,Edge216,Edge210]
  SpineTangent = false
  Suppressed = false
  Transformation = 0
  Transition = 0
FEATURE [PartDesign::SubtractiveLoft] SubtractiveLoft
  BaseFeature = -> SubtractivePipe001
  Closed = false
  Profile = -> Sketch099
  Refine = true
  Ruled = false
  Sections = -> [Sketch108]
  Suppressed = false
FEATURE [PartDesign::SubtractiveLoft] SubtractiveLoft001
  BaseFeature = -> SubtractiveLoft
  Closed = false
  Profile = -> Clone2D
  Refine = true
  Ruled = false
  Sections = -> [Sketch109]
  Suppressed = false
FEATURE [Sketcher::SketchObject] Sketch112
  ArcFitTolerance = 1e-06
  AttachmentSupport = -> [Pad008]
  ExternalGeometry = -> [Binder]
  FullyConstrained = true
  MakeInternals = false
  MapMode = 5
  Placement = pos=(0,3.6,0) rot=(0,0.707107,0.707107;3.14159rad)
  sketch-geometry (4):
    g0: LineSegment [constr] StartX=167.782 StartY=-53.0314 StartZ=0 EndX=215.42 EndY=-53.0314 EndZ=0
    g1: GeomPoint [constr] X=191.282 Y=-53.0314 Z=0
    g2: Circle CenterX=191.282 CenterY=-53.0314 CenterZ=0 NormalX=0 NormalY=0 NormalZ=1 AngleXU=0 Radius=11.5
    g3: Circle CenterX=191.282 CenterY=-53.0314 CenterZ=0 NormalX=0 NormalY=0 NormalZ=1 AngleXU=0 Radius=10.7
  constraints (9):
    c: Horizontal(g0)
    c: PointOnObject(g0,g-3)
    c: Diameter(g2) = 23
    c: Coincident(g2,g1)
    c: Diameter(g3) = 21.4
    c: Coincident(g3,g1)
    c: DistanceX(g0,g1) = 23.5
    c: PointOnObject(g1,g0)
    c: Coincident(g0,g-4)
FEATURE [PartDesign::Chamfer] Chamfer016
  Angle = 45
  Base = -> SubtractiveLoft001 [Edge118,Edge117,Edge119,Edge120,Edge109]
  BaseFeature = -> SubtractiveLoft001
  ChamferType = 0
  FlipDirection = false
  Refine = true
  Size = 1.5
  Size2 = 1
  SupportTransform = false
  Suppressed = false
  UseAllEdges = false
FEATURE [PartDesign::Chamfer] Chamfer017
  Angle = 45
  Base = -> Chamfer016 [Edge15]
  BaseFeature = -> Chamfer016
  ChamferType = 0
  FlipDirection = false
  Refine = true
  Size = 1.6
  Size2 = 1
  SupportTransform = false
  Suppressed = false
  UseAllEdges = false
FEATURE [PartDesign::Chamfer] Chamfer018
  Angle = 45
  Base = -> Chamfer017 [Edge10]
  BaseFeature = -> Chamfer017
  ChamferType = 0
  FlipDirection = false
  Refine = true
  Size = 3.5
  Size2 = 1
  SupportTransform = false
  Suppressed = false
  UseAllEdges = false
FEATURE [PartDesign::Chamfer] Chamfer019
  Angle = 45
  Base = -> Chamfer018 [Edge94]
  BaseFeature = -> Chamfer018
  ChamferType = 0
  FlipDirection = false
  Refine = true
  Size = 1.9
  Size2 = 1
  SupportTransform = false
  Suppressed = false
  UseAllEdges = false
FEATURE [PartDesign::Fillet] Fillet009
  Base = -> Chamfer019 [Edge83]
  BaseFeature = -> Chamfer019
  Radius = 1.1
  Refine = true
  SupportTransform = false
  Suppressed = false
  UseAllEdges = false
FEATURE [PartDesign::Fillet] Fillet010
  Base = -> Fillet009 [Edge74]
  BaseFeature = -> Fillet009
  Radius = 1.9
  Refine = true
  SupportTransform = false
  Suppressed = false
  UseAllEdges = false
FEATURE [PartDesign::Pocket] Pocket005
  BaseFeature = -> Fillet010
  Direction = (0,-1,2e-16)
  Length = 0.8
  Length2 = 5
  Profile = -> Sketch112
  ReferenceAxis = -> Sketch112 [N_Axis]
  Refine = true
  Suppressed = false
  Type = 0
FEATURE [Part::Part2DObjectPython] ShapeString001  # Draft 2D object (typed FeaturePython)
  FontFile = <path>
  Fuse = false
  Justification = 6
  JustificationReference = 0
  KeepLeftMargin = false
  MakeFace = true
  ObliqueAngle = 0
  Placement = pos=(-183.5,3.6,-57.5) rot=(0,0.707107,0.707107;3.14159rad)
  ScaleToSize = true
  Size = 10
  String = AS
  Tracking = 0
FEATURE [PartDesign::Pocket] Pocket013
  BaseFeature = -> Pocket005
  Direction = (-1e-16,-1,2e-16)
  Length = 1
  Length2 = 5
  Profile = -> ShapeString001
  ReferenceAxis = -> ShapeString001 [N_Axis]
  Refine = true
  Suppressed = false
  Type = 0
FEATURE [PartDesign::Pad] Pad020
  Direction = (0,-1,2e-16)
  Length = 25.2
  Length2 = 10
  Midplane = true
  Placement = pos=(0,0,0) rot=(1,0,0;1.5708rad)
  Profile = -> Sketch021
  ReferenceAxis = -> Sketch021 [N_Axis]
  Refine = true
  Suppressed = false
  Type = 0
FEATURE [PartDesign::Body] Body001  label="perno fermo rumble e driver solenoide"
  AllowCompound = false
  Group = -> [Sketch021,Pad020]
  Origin = -> Origin001
  Tip = -> Pad020
FEATURE [PartDesign::Pad] Pad021
  Direction = (0,-1,2e-16)
  Length = 16.8
  Length2 = 10
  Midplane = true
  Placement = pos=(0,0,0) rot=(1,0,0;1.5708rad)
  Profile = -> Sketch061
  ReferenceAxis = -> Sketch061 [N_Axis]
  Refine = true
  Suppressed = false
  Type = 0
FEATURE [PartDesign::Pocket] Pocket014
  BaseFeature = -> Pad021
  Direction = (0,1,-2e-16)
  Length = 12.8
  Length2 = 5
  Midplane = true
  Placement = pos=(0,0,0) rot=(1,0,0;1.5708rad)
  Profile = -> Sketch062
  ReferenceAxis = -> Sketch062 [N_Axis]
  Refine = true
  Suppressed = false
  Type = 0
FEATURE [PartDesign::Pad] Pad022
  BaseFeature = -> Pocket014
  Direction = (0,-1,2e-16)
  Length = 7.6
  Length2 = 10
  Midplane = true
  Placement = pos=(0,0,0) rot=(1,0,0;1.5708rad)
  Profile = -> Sketch063
  ReferenceAxis = -> Sketch063 [N_Axis]
  Refine = true
  Suppressed = false
  Type = 0
FEATURE [PartDesign::Body] Body003  label="blocco switch"
  AllowCompound = false
  Group = -> [Sketch061,Sketch062,Sketch063,Pad021,Pocket014,Pad022]
  Origin = -> Origin003
  Tip = -> Pad022
FEATURE [PartDesign::Pad] Pad024
  Direction = (0,-1,2e-16)
  Length = 17
  Length2 = 10
  Midplane = true
  Placement = pos=(0,0,0) rot=(1,0,0;1.5708rad)
  Profile = -> Sketch045
  ReferenceAxis = -> Sketch045 [N_Axis]
  Refine = true
  Suppressed = false
  Type = 0
FEATURE [PartDesign::Pocket] Pocket015
  BaseFeature = -> Pad024
  Direction = (-1,0,0)
  Length = 8
  Length2 = 5
  Placement = pos=(0,0,0) rot=(1,0,0;1.5708rad)
  Profile = -> Sketch047
  ReferenceAxis = -> Sketch047 [N_Axis]
  Refine = true
  Reversed = true
  Suppressed = false
  Type = 0
FEATURE [PartDesign::Pocket] Pocket016
  BaseFeature = -> Pocket015
  Direction = (-1,0,0)
  Length = 1
  Length2 = 5
  Placement = pos=(0,0,0) rot=(1,0,0;1.5708rad)
  Profile = -> Sketch046
  ReferenceAxis = -> Sketch046 [N_Axis]
  Refine = true
  Reversed = true
  Suppressed = false
  Type = 0
FEATURE [PartDesign::Pocket] Pocket017
  BaseFeature = -> Pocket016
  Direction = (0,1,-2e-16)
  Length = 17
  Length2 = 5
  Midplane = true
  Placement = pos=(0,0,0) rot=(1,0,0;1.5708rad)
  Profile = -> Sketch048
  ReferenceAxis = -> Sketch048 [N_Axis]
  Refine = true
  Suppressed = false
  Type = 0
FEATURE [PartDesign::Pad] Pad025
  BaseFeature = -> Pocket017
  Direction = (0,-1,2e-16)
  Length = 17
  Length2 = 10
  Midplane = true
  Placement = pos=(0,0,0) rot=(1,0,0;1.5708rad)
  Profile = -> Sketch049
  ReferenceAxis = -> Sketch049 [N_Axis]
  Refine = true
  Suppressed = false
  Type = 0
FEATURE [PartDesign::Pad] Pad026
  BaseFeature = -> Pad025
  Direction = (0,-1,2e-16)
  Length = 17
  Length2 = 10
  Midplane = true
  Placement = pos=(0,0,0) rot=(1,0,0;1.5708rad)
  Profile = -> Sketch066
  ReferenceAxis = -> Sketch066 [N_Axis]
  Refine = true
  Suppressed = false
  Type = 0
FEATURE [PartDesign::Pad] Pad027
  BaseFeature = -> Pad026
  Direction = (0,-1,2e-16)
  Length = 5
  Length2 = 10
  Midplane = true
  Placement = pos=(0,0,0) rot=(1,0,0;1.5708rad)
  Profile = -> Sketch064
  ReferenceAxis = -> Sketch064 [N_Axis]
  Refine = true
  Suppressed = false
  Type = 0
FEATURE [PartDesign::Pad] Pad028
  BaseFeature = -> Pad027
  Direction = (1,0,0)
  Length = 1
  Length2 = 10
  Placement = pos=(0,0,0) rot=(1,0,0;1.5708rad)
  Profile = -> Sketch068
  ReferenceAxis = -> Sketch068 [N_Axis]
  Refine = true
  Reversed = true
  Suppressed = false
  Type = 0
FEATURE [PartDesign::Chamfer] Chamfer020
  Angle = 45
  Base = -> Pad028 [Edge73,Edge75,Edge78,Edge77]
  BaseFeature = -> Pad028
  ChamferType = 0
  FlipDirection = false
  Placement = pos=(0,0,0) rot=(1,0,0;1.5708rad)
  Refine = true
  Size = 0.5
  Size2 = 1
  SupportTransform = false
  Suppressed = false
  UseAllEdges = false
FEATURE [PartDesign::Body] Body002  label="supporto per neopixel"
  AllowCompound = false
  Group = -> [Sketch045,Sketch047,Sketch046,Sketch048,Sketch049,Sketch066,Sketch064,Sketch068,Pad024,Pocket015,Pocket016,Pocket017,Pad025,Pad026,Pad027,Pad028,Chamfer020]
  Origin = -> Origin002
  Tip = -> Chamfer020
FEATURE [Sketcher::SketchObject] Sketch134  label="perno fermo rumble002"
  ArcFitTolerance = 1e-06
  AttachmentSupport = -> [XZ_Plane008]
  FullyConstrained = true
  MakeInternals = false
  MapMode = 5
  Placement = pos=(0,0,0) rot=(1,0,0;1.5708rad)
  sketch-geometry (16):
    g0: LineSegment StartX=0 StartY=0.45 StartZ=0 EndX=0 EndY=1.55 EndZ=0
    g1: LineSegment StartX=0.45 StartY=2 StartZ=0 EndX=1.55 EndY=2 EndZ=0
    g2: LineSegment StartX=2 StartY=1.55 StartZ=0 EndX=2 EndY=0.45 EndZ=0
    g3: LineSegment StartX=1.55 StartY=0 StartZ=0 EndX=0.45 EndY=0 EndZ=0
    g4: ArcOfCircle [constr] CenterX=0.45 CenterY=1.55 CenterZ=0 NormalX=0 NormalY=0 NormalZ=1 AngleXU=0 Radius=0.45 StartAngle=1.5708 EndAngle=3.14159
    g5: GeomPoint [constr] X=0 Y=2 Z=0
    g6: LineSegment StartX=0.45 StartY=2 StartZ=0 EndX=0 EndY=1.55 EndZ=0
    g7: ArcOfCircle [constr] CenterX=1.55 CenterY=1.55 CenterZ=0 NormalX=0 NormalY=0 NormalZ=1 AngleXU=0 Radius=0.45 StartAngle=0 EndAngle=1.5708
    g8: GeomPoint [constr] X=2 Y=2 Z=0
    g9: LineSegment StartX=2 StartY=1.55 StartZ=0 EndX=1.55 EndY=2 EndZ=0
    g10: ArcOfCircle [constr] CenterX=1.55 CenterY=0.45 CenterZ=0 NormalX=0 NormalY=0 NormalZ=1 AngleXU=0 Radius=0.45 StartAngle=4.71239 EndAngle=6.28319
    g11: GeomPoint [constr] X=2 Y=0 Z=0
    g12: LineSegment StartX=1.55 StartY=0 StartZ=0 EndX=2 EndY=0.45 EndZ=0
    g13: ArcOfCircle [constr] CenterX=0.45 CenterY=0.45 CenterZ=0 NormalX=0 NormalY=0 NormalZ=1 AngleXU=0 Radius=0.45 StartAngle=3.14159 EndAngle=4.71239
    g14: GeomPoint [constr] X=0 Y=0 Z=0
    g15: LineSegment StartX=0 StartY=0.45 StartZ=0 EndX=0.45 EndY=0 EndZ=0
  constraints (35):
    c: Coincident(g14,g-1)
    c: PointOnObject(g5,g-2)
    c: Horizontal(g1)
    c: Vertical(g2)
    c: Horizontal(g3)
    c: DistanceX(g5,g8) = 2
    c: DistanceY(g11,g8) = 2
    c: PointOnObject(g5,g0)
    c: PointOnObject(g5,g1)
    c: Tangent(g0,g4) = 1.5708
    c: Tangent(g1,g4) = 1.5708
    c: Coincident(g6,g0)
    c: Coincident(g6,g1)
    c: PointOnObject(g8,g2)
    c: PointOnObject(g8,g1)
    c: Tangent(g2,g7) = 1.5708
    c: Tangent(g1,g7) = 1.5708
    c: Coincident(g9,g2)
    c: Coincident(g9,g1)
    c: PointOnObject(g11,g2)
    c: PointOnObject(g11,g3)
    c: Tangent(g2,g10) = 1.5708
    c: Tangent(g3,g10) = 1.5708
    c: Coincident(g12,g2)
    c: Coincident(g12,g3)
    c: PointOnObject(g14,g0)
    c: PointOnObject(g14,g3)
    c: Tangent(g0,g13) = 1.5708
    c: Tangent(g3,g13) = 1.5708
    c: Coincident(g15,g0)
    c: Coincident(g15,g3)
    c: Equal(g6,g9)
    c: Equal(g9,g12)
    c: Equal(g12,g15)
    c: DistanceX(g14,g3) = 0.45
FEATURE [PartDesign::Pad] Pad029
  Direction = (0,-1,2e-16)
  Length = 17
  Length2 = 10
  Midplane = true
  Placement = pos=(0,0,0) rot=(1,0,0;1.5708rad)
  Profile = -> Sketch134
  ReferenceAxis = -> Sketch134 [N_Axis]
  Refine = true
  Suppressed = false
  Type = 0
FEATURE [PartDesign::Body] Body008  label="perno fermo neopixel"
  AllowCompound = false
  Group = -> [Sketch134,Pad029]
  Origin = -> Origin008
  Tip = -> Pad029
FEATURE [Sketcher::SketchObject] Sketch135  label="perno fermo rumble003"
  ArcFitTolerance = 1e-06
  AttachmentSupport = -> [XZ_Plane009]
  FullyConstrained = true
  MakeInternals = false
  MapMode = 5
  Placement = pos=(0,0,0) rot=(1,0,0;1.5708rad)
  sketch-geometry (16):
    g0: LineSegment StartX=4.69e-14 StartY=0.8 StartZ=0 EndX=-3.04e-14 EndY=3.1 EndZ=0
    g1: LineSegment StartX=0.8 StartY=3.9 StartZ=0 EndX=3.1 EndY=3.9 EndZ=0
    g2: LineSegment StartX=3.9 StartY=3.1 StartZ=0 EndX=3.9 EndY=0.8 EndZ=0
    g3: LineSegment StartX=3.1 StartY=0 StartZ=0 EndX=0.8 EndY=0 EndZ=0
    g4: ArcOfCircle [constr] CenterX=0.8 CenterY=3.1 CenterZ=0 NormalX=0 NormalY=0 NormalZ=1 AngleXU=0 Radius=0.8 StartAngle=1.5708 EndAngle=3.14159
    g5: GeomPoint [constr] X=0 Y=3.9 Z=0
    g6: LineSegment StartX=0.8 StartY=3.9 StartZ=0 EndX=-3.04e-14 EndY=3.1 EndZ=0
    g7: ArcOfCircle [constr] CenterX=3.1 CenterY=3.1 CenterZ=0 NormalX=0 NormalY=0 NormalZ=1 AngleXU=0 Radius=0.8 StartAngle=-2.4e-14 EndAngle=1.5708
    g8: GeomPoint [constr] X=3.9 Y=3.9 Z=0
    g9: LineSegment StartX=3.9 StartY=3.1 StartZ=0 EndX=3.1 EndY=3.9 EndZ=0
    g10: ArcOfCircle [constr] CenterX=3.1 CenterY=0.8 CenterZ=0 NormalX=0 NormalY=0 NormalZ=1 AngleXU=0 Radius=0.8 StartAngle=4.71239 EndAngle=6.28319
    g11: GeomPoint [constr] X=3.9 Y=0 Z=0
    g12: LineSegment StartX=3.1 StartY=0 StartZ=0 EndX=3.9 EndY=0.8 EndZ=0
    g13: ArcOfCircle [constr] CenterX=0.8 CenterY=0.8 CenterZ=0 NormalX=0 NormalY=0 NormalZ=1 AngleXU=0 Radius=0.8 StartAngle=3.14159 EndAngle=4.71239
    g14: GeomPoint [constr] X=0 Y=0 Z=0
    g15: LineSegment StartX=4.69e-14 StartY=0.8 StartZ=0 EndX=0.8 EndY=0 EndZ=0
  constraints (35):
    c: Coincident(g14,g-1)
    c: PointOnObject(g5,g-2)
    c: Horizontal(g1)
    c: Vertical(g2)
    c: Horizontal(g3)
    c: DistanceX(g5,g8) = 3.9
    c: DistanceY(g11,g8) = 3.9
    c: PointOnObject(g5,g0)
    c: PointOnObject(g5,g1)
    c: Tangent(g0,g4) = 1.5708
    c: Tangent(g1,g4) = 1.5708
    c: Coincident(g6,g0)
    c: Coincident(g6,g1)
    c: PointOnObject(g8,g2)
    c: PointOnObject(g8,g1)
    c: Tangent(g2,g7) = 1.5708
    c: Tangent(g1,g7) = 1.5708
    c: Coincident(g9,g2)
    c: Coincident(g9,g1)
    c: PointOnObject(g11,g2)
    c: PointOnObject(g11,g3)
    c: Tangent(g2,g10) = 1.5708
    c: Tangent(g3,g10) = 1.5708
    c: Coincident(g12,g2)
    c: Coincident(g12,g3)
    c: PointOnObject(g14,g0)
    c: PointOnObject(g14,g3)
    c: Tangent(g0,g13) = 1.5708
    c: Tangent(g3,g13) = 1.5708
    c: Coincident(g15,g0)
    c: Coincident(g15,g3)
    c: Equal(g6,g9)
    c: Equal(g9,g12)
    c: Equal(g12,g15)
    c: DistanceX(g14,g3) = 0.8
FEATURE [PartDesign::Pad] Pad030
  Direction = (0,-1,2e-16)
  Length = 25.2
  Length2 = 10
  Midplane = true
  Placement = pos=(0,0,0) rot=(1,0,0;1.5708rad)
  Profile = -> Sketch135
  ReferenceAxis = -> Sketch135 [N_Axis]
  Refine = true
  Suppressed = false
  Type = 0
FEATURE [PartDesign::Body] Body009  label="perno fermo switch - caricabatterie - grilletto"
  AllowCompound = false
  Group = -> [Sketch135,Pad030]
  Origin = -> Origin009
  Tip = -> Pad030
FEATURE [Sketcher::SketchObject] Sketch136  label="scavo_rele"
  ArcFitTolerance = 1e-06
  AttachmentSupport = -> [XZ_Plane]
  ExternalGeometry = -> [Sketch]
  FullyConstrained = true
  MakeInternals = false
  MapMode = 5
  Placement = pos=(0,0,0) rot=(1,0,0;1.5708rad)
  sketch-geometry (7):
    g0: LineSegment [constr] StartX=-172.456 StartY=-60.9321 StartZ=0 EndX=-176.597 EndY=-73.6763 EndZ=0
    g1: LineSegment [constr] StartX=-172.456 StartY=-60.9321 StartZ=0 EndX=-170.364 EndY=-61.612 EndZ=0
    g2: LineSegment [constr] StartX=-172.456 StartY=-60.9321 StartZ=0 EndX=-176.07 EndY=-59.7579 EndZ=0
    g3: LineSegment StartX=-176.07 StartY=-59.7579 StartZ=0 EndX=-170.364 EndY=-61.612 EndZ=0
    g4: LineSegment StartX=-176.07 StartY=-59.7579 StartZ=0 EndX=-180.211 EndY=-72.502 EndZ=0
    g5: LineSegment StartX=-170.364 StartY=-61.612 StartZ=0 EndX=-174.505 EndY=-74.3561 EndZ=0
    g6: LineSegment StartX=-180.211 StartY=-72.502 StartZ=0 EndX=-174.505 EndY=-74.3561 EndZ=0
  constraints (19):
    c: Tangent(g0,g-3)
    c: Distance(g0,g-3) = 87.2
    c: Distance(g0,g0) = 13.4
    c: Coincident(g1,g0)
    c: Coincident(g2,g0)
    c: Distance(g2) = 3.8
    c: Distance(g1) = 2.2
    c: Perpendicular(g0,g1)
    c: Perpendicular(g0,g2)
    c: Coincident(g3,g2)
    c: Coincident(g3,g1)
    c: Equal(g4,g0)
    c: Equal(g5,g0)
    c: Parallel(g4,g0)
    c: Parallel(g5,g0)
    c: Coincident(g4,g2)
    c: Coincident(g5,g1)
    c: Coincident(g6,g4)
    c: Coincident(g6,g5)
FEATURE [Part::Extrusion] Extrude076  label="Extrude076 - scavo_rele"
  Base = -> Sketch136
  Dir = (0,-1,2e-16)
  DirMode = 2
  FaceMakerClass = Part::FaceMakerBullseye
  FaceMakerMode = 3
  LengthFwd = 18.2
  LengthRev = 0
  Solid = true
  Symmetric = true
FEATURE [Sketcher::SketchObject] Sketch137  label="scavo_nuovo_driver"
  ArcFitTolerance = 1e-06
  AttachmentSupport = -> [XZ_Plane]
  ExternalGeometry = -> [Sketch]
  FullyConstrained = true
  MakeInternals = false
  MapMode = 5
  Placement = pos=(0,0,0) rot=(1,0,0;1.5708rad)
  sketch-geometry (7):
    g0: LineSegment [constr] StartX=-160.034 StartY=-22.6997 StartZ=0 EndX=-164.854 EndY=-37.5361 EndZ=0
    g1: LineSegment [constr] StartX=-160.034 StartY=-22.6997 StartZ=0 EndX=-156.99 EndY=-23.6885 EndZ=0
    g2: LineSegment [constr] StartX=-160.034 StartY=-22.6997 StartZ=0 EndX=-163.648 EndY=-21.5254 EndZ=0
    g3: LineSegment StartX=-163.648 StartY=-21.5254 StartZ=0 EndX=-156.99 EndY=-23.6885 EndZ=0
    g4: LineSegment StartX=-163.648 StartY=-21.5254 StartZ=0 EndX=-168.468 EndY=-36.3619 EndZ=0
    g5: LineSegment StartX=-156.99 StartY=-23.6885 StartZ=0 EndX=-161.811 EndY=-38.525 EndZ=0
    g6: LineSegment StartX=-168.468 StartY=-36.3619 StartZ=0 EndX=-161.811 EndY=-38.525 EndZ=0
  constraints (19):
    c: Distance(g0,g-3) = 47
    c: Distance(g0) = 15.6
    c: Tangent(g0,g-3)
    c: Coincident(g1,g0)
    c: Coincident(g2,g0)
    c: Distance(g1) = 3.2
    c: Distance(g2) = 3.8
    c: Perpendicular(g0,g1)
    c: Perpendicular(g0,g2)
    c: Coincident(g3,g2)
    c: Coincident(g3,g1)
    c: Equal(g4,g0)
    c: Equal(g5,g0)
    c: Parallel(g4,g0)
    c: Parallel(g5,g0)
    c: Coincident(g4,g2)
    c: Coincident(g5,g1)
    c: Coincident(g6,g4)
    c: Coincident(g6,g5)
FEATURE [Part::Extrusion] Extrude077  label="Extrude077 - scavo_nuovo_driver"
  Base = -> Sketch137
  Dir = (0,-1,2e-16)
  DirMode = 2
  FaceMakerClass = Part::FaceMakerBullseye
  FaceMakerMode = 3
  LengthFwd = 20.8
  LengthRev = 0
  Solid = true
  Symmetric = true
FEATURE [Sketcher::SketchObject] Sketch138  label="scavo_nuovo_driver_alto"
  ArcFitTolerance = 1e-06
  AttachmentSupport = -> [XZ_Plane]
  ExternalGeometry = -> [Sketch]
  FullyConstrained = true
  MakeInternals = false
  MapMode = 5
  Placement = pos=(0,0,0) rot=(1,0,0;1.5708rad)
  sketch-geometry (7):
    g0: LineSegment [constr] StartX=-188.917 StartY=18.1185 StartZ=0 EndX=-187.75 EndY=4.97025 EndZ=0
    g1: LineSegment StartX=-187.75 StartY=4.97025 StartZ=0 EndX=-189.742 EndY=4.79337 EndZ=0
    g2: LineSegment StartX=-187.75 StartY=4.97025 StartZ=0 EndX=-182.769 EndY=5.41245 EndZ=0
    g3: LineSegment StartX=-190.909 StartY=17.9416 StartZ=0 EndX=-189.742 EndY=4.79337 EndZ=0
    g4: LineSegment StartX=-183.937 StartY=18.5607 StartZ=0 EndX=-182.769 EndY=5.41245 EndZ=0
    g5: LineSegment StartX=-190.909 StartY=17.9416 StartZ=0 EndX=-188.917 EndY=18.1185 EndZ=0
    g6: LineSegment StartX=-188.917 StartY=18.1185 StartZ=0 EndX=-183.937 EndY=18.5607 EndZ=0
  constraints (20):
    c: Distance(g0) = 13.2
    c: DistanceY(g-3,g0) = 9
    c: PointOnObject(g0,g-4)
    c: PointOnObject(g0,g-4)
    c: Coincident(g1,g0)
    c: Coincident(g2,g0)
    c: Distance(g1) = 2
    c: Distance(g2) = 5
    c: Perpendicular(g0,g1)
    c: Perpendicular(g0,g2)
    c: Equal(g3,g0)
    c: Parallel(g3,g0)
    c: Coincident(g3,g1)
    c: Equal(g4,g0)
    c: Parallel(g4,g0)
    c: Coincident(g4,g2)
    c: Coincident(g5,g3)
    c: Coincident(g5,g0)
    c: Coincident(g6,g0)
    c: Coincident(g6,g4)
FEATURE [Part::Extrusion] Extrude078  label="Extrude078 - scavo_nuovo_driver_alto"
  Base = -> Sketch138
  Dir = (0,-1,2e-16)
  DirMode = 2
  FaceMakerClass = Part::FaceMakerBullseye
  FaceMakerMode = 3
  LengthFwd = 17.2
  LengthRev = 0
  Solid = true
  Symmetric = true
FEATURE [Sketcher::SketchObject] Sketch139  label="fermi_nuovo_driver_alto"
  ArcFitTolerance = 1e-06
  AttachmentSupport = -> [XZ_Plane]
  ExternalGeometry = -> [Sketch138,Sketch]
  FullyConstrained = true
  MakeInternals = false
  MapMode = 5
  Placement = pos=(0,0,0) rot=(1,0,0;1.5708rad)
  sketch-geometry (17):
    g0: LineSegment [constr] StartX=-188.41 StartY=16.8018 StartZ=0 EndX=-187.948 EndY=14.1416 EndZ=0
    g1: LineSegment [constr] StartX=-187.948 StartY=14.1416 StartZ=0 EndX=-187.486 EndY=11.4815 EndZ=0
    g2: LineSegment StartX=-187.948 StartY=14.1416 StartZ=0 EndX=-187.76 EndY=13.0579 EndZ=0
    g3: LineSegment StartX=-187.948 StartY=14.1416 StartZ=0 EndX=-188.136 EndY=15.2254 EndZ=0
    g4: LineSegment StartX=-187.76 StartY=13.0579 StartZ=0 EndX=-185.592 EndY=13.4346 EndZ=0
    g5: LineSegment StartX=-188.136 StartY=15.2254 StartZ=0 EndX=-185.969 EndY=15.6021 EndZ=0
    g6: LineSegment StartX=-185.969 StartY=15.6021 StartZ=0 EndX=-185.592 EndY=13.4346 EndZ=0
    g7: LineSegment StartX=-187.486 StartY=11.4815 StartZ=0 EndX=-189.062 EndY=11.2075 EndZ=0
    g8: LineSegment StartX=-188.41 StartY=16.8018 StartZ=0 EndX=-189.987 EndY=16.5278 EndZ=0
    g9: LineSegment StartX=-189.987 StartY=16.5278 StartZ=0 EndX=-189.062 EndY=11.2075 EndZ=0
    g10: LineSegment StartX=-187.486 StartY=11.4815 StartZ=0 EndX=-185.318 EndY=11.8582 EndZ=0
    g11: LineSegment StartX=-188.41 StartY=16.8018 StartZ=0 EndX=-186.243 EndY=17.1785 EndZ=0
    g12: LineSegment StartX=-184.393 StartY=15.8761 StartZ=0 EndX=-184.016 EndY=13.7086 EndZ=0
    g13: ArcOfCircle CenterX=-185.969 CenterY=15.6021 CenterZ=0 NormalX=0 NormalY=0 NormalZ=1 AngleXU=0 Radius=1.6 StartAngle=0.172085 EndAngle=1.74288
    g14: GeomPoint [constr] X=-184.667 Y=17.4525 Z=0
    g15: ArcOfCircle CenterX=-185.592 CenterY=13.4346 CenterZ=0 NormalX=0 NormalY=0 NormalZ=1 AngleXU=0 Radius=1.6 StartAngle=4.88447 EndAngle=6.45527
    g16: GeomPoint [constr] X=-183.742 Y=12.1322 Z=0
  constraints (43):
    c: Tangent(g1,g0) = -1.5708
    c: Distance(g0) = 2.7
    c: Equal(g1,g0)
    c: Tangent(g1,g-5)
    c: Coincident(g2,g0)
    c: Coincident(g3,g0)
    c: Distance(g2) = 1.1
    c: Equal(g3,g2)
    c: PointOnObject(g3,g2)
    c: Coincident(g4,g2)
    c: Coincident(g5,g3)
    c: Distance(g4) = 2.2
    c: Equal(g4,g5)
    c: Perpendicular(g1,g4)
    c: Perpendicular(g0,g5)
    c: Coincident(g6,g5)
    c: Coincident(g6,g4)
    c: Coincident(g7,g1)
    c: Coincident(g8,g0)
    c: Distance(g7) = 1.6
    c: Equal(g7,g8)
    c: Perpendicular(g1,g7)
    c: Perpendicular(g8,g0)
    c: Coincident(g9,g8)
    c: Coincident(g9,g7)
    c: Coincident(g10,g1)
    c: Coincident(g11,g0)
    c: Distance(g10,g16) = 3.8
    c: Perpendicular(g1,g10)
    c: Perpendicular(g1,g11)
    c: DistanceY(g0,g-4) = 3.8
    c: PointOnObject(g14,g12)
    c: PointOnObject(g14,g11)
    c: Tangent(g12,g13) = 1.5708
    c: Tangent(g11,g13) = 1.5708
    c: PointOnObject(g16,g12)
    c: PointOnObject(g16,g10)
    c: Tangent(g12,g15) = 1.5708
    c: Tangent(g10,g15) = -1.5708
    c: Equal(g13,g15)
    c: Coincident(g13,g5)
    c: Parallel(g2,g0)
    c: PointOnObject(g0,g-5)
FEATURE [Part::Extrusion] Extrude079  label="Extrude079 - fermi_nuovo_driver_alto"
  Base = -> Sketch139
  Dir = (0,-1,2e-16)
  DirMode = 2
  FaceMakerClass = Part::FaceMakerBullseye
  FaceMakerMode = 3
  LengthFwd = 25.2
  LengthRev = 0
  Solid = true
  Symmetric = true
FEATURE [Sketcher::SketchObject] Sketch140  label="scavo_diodo_nuovo_driver_alto"
  ArcFitTolerance = 1e-06
  AttachmentSupport = -> [XZ_Plane]
  ExternalGeometry = -> [Sketch138]
  FullyConstrained = true
  MakeInternals = false
  MapMode = 5
  Placement = pos=(0,0,0) rot=(1,0,0;1.5708rad)
  sketch-geometry (4):
    g0: LineSegment StartX=-190.909 StartY=17.9416 StartZ=0 EndX=-189.742 EndY=4.79337 EndZ=0
    g1: LineSegment StartX=-193.898 StartY=17.6763 StartZ=0 EndX=-192.73 EndY=4.52805 EndZ=0
    g2: LineSegment StartX=-190.909 StartY=17.9416 StartZ=0 EndX=-193.898 EndY=17.6763 EndZ=0
    g3: LineSegment StartX=-192.73 StartY=4.52805 StartZ=0 EndX=-189.742 EndY=4.79337 EndZ=0
  constraints (11):
    c: Equal(g0,g-3)
    c: Parallel(g0,g-3)
    c: Equal(g1,g-3)
    c: Parallel(g1,g-3)
    c: Coincident(g2,g0)
    c: Distance(g2) = 3
    c: Perpendicular(g0,g2)
    c: Coincident(g1,g2)
    c: Coincident(g3,g1)
    c: Coincident(g3,g0)
    c: Coincident(g0,g-3)
FEATURE [Part::Extrusion] Extrude080  label="Extrude080 - scavo_diodo_nuovo_driver_alto"
  Base = -> Sketch140
  Dir = (0,-1,2e-16)
  DirMode = 2
  FaceMakerClass = Part::FaceMakerBullseye
  FaceMakerMode = 3
  LengthFwd = 4
  LengthRev = 0
  Placement = pos=(0,7.8,0) rot=(0,0,1;0rad)
  Solid = true
  Symmetric = false
FEATURE [Part::MultiFuse] Fusion001
  Refine = true
  Shapes = -> [Cut043,Extrude079]
FEATURE [Part::Cut] Cut044
  Base = -> Fusion001
  Refine = true
  Tool = -> Extrude078
FEATURE [Part::Cut] Cut045
  Base = -> Cut044
  Refine = true
  Tool = -> Extrude080
FEATURE [Sketcher::SketchObject] Sketch141  label="fermi_nuovo_driver"
  ArcFitTolerance = 1e-06
  AttachmentSupport = -> [XZ_Plane]
  ExternalGeometry = -> [Sketch,Sketch137]
  FullyConstrained = true
  MakeInternals = false
  MapMode = 5
  Placement = pos=(0,0,0) rot=(1,0,0;1.5708rad)
  sketch-geometry (17):
    g0: LineSegment [constr] StartX=-156.99 StartY=-23.6885 StartZ=0 EndX=-160.034 EndY=-22.6997 EndZ=0
    g1: LineSegment [constr] StartX=-160.034 StartY=-22.6997 StartZ=0 EndX=-162.815 EndY=-31.2592 EndZ=0
    g2: LineSegment [constr] StartX=-162.815 StartY=-31.2592 StartZ=0 EndX=-164.484 EndY=-36.3949 EndZ=0
    g3: LineSegment StartX=-164.484 StartY=-36.3949 StartZ=0 EndX=-166.576 EndY=-35.715 EndZ=0
    g4: LineSegment StartX=-167.603 StartY=-33.6989 StartZ=0 EndX=-166.923 EndY=-31.6066 EndZ=0
    g5: LineSegment StartX=-164.907 StartY=-30.5793 StartZ=0 EndX=-161.293 EndY=-31.7536 EndZ=0
    g6: LineSegment StartX=-161.293 StartY=-31.7536 StartZ=0 EndX=-162.962 EndY=-36.8893 EndZ=0
    g7: LineSegment StartX=-164.484 StartY=-36.3949 StartZ=0 EndX=-162.962 EndY=-36.8893 EndZ=0
    g8: LineSegment StartX=-165.402 StartY=-32.101 StartZ=0 EndX=-166.082 EndY=-34.1933 EndZ=0
    g9: LineSegment StartX=-166.082 StartY=-34.1933 StartZ=0 EndX=-163.989 EndY=-34.8732 EndZ=0
    g10: LineSegment StartX=-163.989 StartY=-34.8732 StartZ=0 EndX=-163.309 EndY=-32.7809 EndZ=0
    g11: LineSegment StartX=-163.309 StartY=-32.7809 StartZ=0 EndX=-165.402 EndY=-32.101 EndZ=0
    g12: ArcOfCircle CenterX=-165.402 CenterY=-32.101 CenterZ=0 NormalX=0 NormalY=0 NormalZ=1 AngleXU=0 Radius=1.6 StartAngle=1.25664 EndAngle=2.82743
    g13: GeomPoint [constr] X=-166.429 Y=-30.0849 Z=0
    g14: ArcOfCircle CenterX=-166.082 CenterY=-34.1933 CenterZ=0 NormalX=0 NormalY=0 NormalZ=1 AngleXU=0 Radius=1.6 StartAngle=2.82743 EndAngle=4.39823
    g15: GeomPoint [constr] X=-168.098 Y=-35.2206 Z=0
    g16: LineSegment [constr] StartX=-160.034 StartY=-22.6997 StartZ=0 EndX=-164.854 EndY=-37.5361 EndZ=0
  constraints (44):
    c: Coincident(g0,g-4)
    c: PointOnObject(g0,g-3)
    c: Parallel(g0,g-4)
    c: Coincident(g1,g0)
    c: Parallel(g1,g-3)
    c: Coincident(g2,g1)
    c: Distance(g2) = 5.4
    c: Coincident(g3,g2)
    c: Parallel(g2,g-3)
    c: Distance(g15,g13) = 5.4
    c: Perpendicular(g3,g2)
    c: Parallel(g4,g2)
    c: Distance(g5,g13) = 5.4
    c: Distance(g3,g15) = 3.8
    c: Perpendicular(g4,g5)
    c: Coincident(g6,g5)
    c: Distance(g6) = 5.4
    c: Parallel(g6,g4)
    c: Coincident(g7,g2)
    c: Coincident(g7,g6)
    c: Coincident(g8,g9)
    c: Coincident(g9,g10)
    c: Coincident(g10,g11)
    c: Coincident(g11,g8)
    c: Distance(g8,g10) = 2.2
    c: Distance(g9,g11) = 2.2
    c: Perpendicular(g11,g8)
    c: Equal(g8,g10)
    c: Equal(g11,g9)
    c: Tangent(g10,g2)
    c: Distance(g10,g1) = 1.6
    c: PointOnObject(g13,g4)
    c: PointOnObject(g13,g5)
    c: Tangent(g4,g12) = 1.5708
    c: Tangent(g5,g12) = 1.5708
    c: PointOnObject(g15,g4)
    c: Tangent(g4,g14) = 1.5708
    c: Tangent(g3,g14) = 1.5708
    c: Equal(g14,g12)
    c: Coincident(g12,g8)
    c: Coincident(g16,g0)
    c: PointOnObject(g16,g-5)
    c: Parallel(g16,g-3)
    c: Distance(g16,g2) = 1.2
FEATURE [Part::Extrusion] Extrude081  label="Extrude081 - fermi_nuovo_driver"
  Base = -> Sketch141
  Dir = (0,-1,2e-16)
  DirMode = 2
  FaceMakerClass = Part::FaceMakerBullseye
  FaceMakerMode = 3
  LengthFwd = 25.2
  LengthRev = 0
  Solid = true
  Symmetric = true
FEATURE [Part::MultiFuse] Fusion002
  Refine = true
  Shapes = -> [Cut045,Extrude081]
FEATURE [Part::Cut] Cut046
  Base = -> Fusion002
  Refine = true
  Tool = -> Extrude077
FEATURE [Sketcher::SketchObject] Sketch142  label="fermi_rele"
  ArcFitTolerance = 1e-06
  AttachmentSupport = -> [XZ_Plane]
  ExternalGeometry = -> [Sketch,Sketch136]
  FullyConstrained = true
  MakeInternals = false
  MapMode = 5
  Placement = pos=(0,0,0) rot=(1,0,0;1.5708rad)
  sketch-geometry (15):
    g0: LineSegment StartX=-176.936 StartY=-62.4208 StartZ=0 EndX=-177.615 EndY=-64.5131 EndZ=0
    g1: LineSegment StartX=-174.919 StartY=-61.3936 StartZ=0 EndX=-171.305 EndY=-62.5678 EndZ=0
    g2: LineSegment StartX=-171.305 StartY=-62.5678 StartZ=0 EndX=-172.974 EndY=-67.7035 EndZ=0
    g3: LineSegment StartX=-176.588 StartY=-66.5293 StartZ=0 EndX=-172.974 EndY=-67.7035 EndZ=0
    g4: LineSegment StartX=-175.414 StartY=-62.9152 StartZ=0 EndX=-173.322 EndY=-63.5951 EndZ=0
    g5: LineSegment StartX=-175.414 StartY=-62.9152 StartZ=0 EndX=-176.094 EndY=-65.0076 EndZ=0
    g6: LineSegment StartX=-173.322 StartY=-63.5951 StartZ=0 EndX=-174.001 EndY=-65.6874 EndZ=0
    g7: LineSegment StartX=-176.094 StartY=-65.0076 StartZ=0 EndX=-174.001 EndY=-65.6874 EndZ=0
    g8: LineSegment [constr] StartX=-173.322 StartY=-63.5951 StartZ=0 EndX=-172.827 EndY=-62.0734 EndZ=0
    g9: LineSegment [constr] StartX=-173.322 StartY=-63.5951 StartZ=0 EndX=-171.8 EndY=-64.0895 EndZ=0
    g10: LineSegment [constr] StartX=-170.364 StartY=-61.612 StartZ=0 EndX=-172.456 EndY=-60.9321 EndZ=0
    g11: ArcOfCircle CenterX=-175.414 CenterY=-62.9152 CenterZ=0 NormalX=0 NormalY=0 NormalZ=1 AngleXU=0 Radius=1.6 StartAngle=1.25664 EndAngle=2.82743
    g12: GeomPoint [constr] X=-176.441 Y=-60.8991 Z=0
    g13: ArcOfCircle CenterX=-176.094 CenterY=-65.0076 CenterZ=0 NormalX=0 NormalY=0 NormalZ=1 AngleXU=0 Radius=1.6 StartAngle=2.82743 EndAngle=4.39823
    g14: GeomPoint [constr] X=-178.11 Y=-66.0348 Z=0
  constraints (39):
    c: Distance(g14,g12) = 5.4
    c: Distance(g1,g12) = 5.4
    c: Perpendicular(g1,g0)
    c: Coincident(g2,g1)
    c: Parallel(g2,g0)
    c: Coincident(g3,g2)
    c: Parallel(g2,g-3)
    c: Coincident(g5,g4)
    c: Distance(g5) = 2.2
    c: Distance(g4) = 2.2
    c: Perpendicular(g4,g5)
    c: Coincident(g6,g4)
    c: Equal(g6,g5)
    c: Parallel(g6,g5)
    c: Coincident(g7,g5)
    c: Coincident(g7,g6)
    c: Coincident(g8,g4)
    c: Coincident(g9,g4)
    c: Distance(g8) = 1.6
    c: Distance(g9) = 1.6
    c: Parallel(g8,g6)
    c: Parallel(g9,g4)
    c: PointOnObject(g8,g1)
    c: PointOnObject(g9,g2)
    c: Coincident(g10,g-4)
    c: Parallel(g10,g-4)
    c: PointOnObject(g10,g-3)
    c: Tangent(g6,g-3) = 1.5708
    c: Distance(g4,g10) = 2.8
    c: PointOnObject(g12,g1)
    c: Tangent(g1,g11) = 1.5708
    c: Tangent(g0,g11) = -1.5708
    c: PointOnObject(g14,g3)
    c: PointOnObject(g14,g0)
    c: Tangent(g3,g13) = -1.5708
    c: Tangent(g0,g13) = -1.5708
    c: Equal(g11,g13)
    c: Coincident(g11,g4)
    c: Parallel(g3,g1)
FEATURE [Part::Extrusion] Extrude082  label="Extrude082 - fermi_rele"
  Base = -> Sketch142
  Dir = (0,-1,2e-16)
  DirMode = 2
  FaceMakerClass = Part::FaceMakerBullseye
  FaceMakerMode = 3
  LengthFwd = 25.2
  LengthRev = 0
  Solid = true
  Symmetric = true
FEATURE [Part::MultiFuse] Fusion003
  Refine = true
  Shapes = -> [Cut046,Extrude082]
FEATURE [Part::Cut] Cut047
  Base = -> Fusion003
  Refine = true
  Tool = -> Extrude076
FEATURE [Sketcher::SketchObject] Sketch143  label="foro_passaggio_cavi_led_batteria"
  ArcFitTolerance = 1e-06
  AttachmentSupport = -> [XZ_Plane]
  ExternalGeometry = -> [Sketch,Sketch042,Sketch036]
  FullyConstrained = true
  MakeInternals = false
  MapMode = 5
  Placement = pos=(0,0,0) rot=(1,0,0;1.5708rad)
  sketch-geometry (4):
    g0: LineSegment StartX=-207.775 StartY=-41.3701 StartZ=0 EndX=-213.607 EndY=-53.8767 EndZ=0
    g1: LineSegment StartX=-213.607 StartY=-53.8767 StartZ=0 EndX=-211.843 EndY=-59.5559 EndZ=0
    g2: LineSegment StartX=-207.775 StartY=-41.3701 StartZ=0 EndX=-207.775 EndY=-50.8316 EndZ=0
    g3: LineSegment StartX=-207.775 StartY=-50.8316 StartZ=0 EndX=-211.843 EndY=-59.5559 EndZ=0
  constraints (9):
    c: Coincident(g0,g-3)
    c: PointOnObject(g1,g-6)
    c: Coincident(g1,g0)
    c: Coincident(g2,g0)
    c: Coincident(g2,g-7)
    c: Coincident(g3,g2)
    c: Parallel(g3,g0)
    c: Coincident(g3,g1)
    c: Coincident(g0,g-5)
FEATURE [Part::Extrusion] Extrude083  label="Extrude083 - foro_passaggio_cavi_led_batteria"
  Base = -> Sketch143
  Dir = (0,-1,2e-16)
  DirMode = 2
  FaceMakerClass = Part::FaceMakerBullseye
  FaceMakerMode = 3
  LengthFwd = 6
  LengthRev = 0
  Placement = pos=(0,1.2,0) rot=(0,0,1;0rad)
  Solid = true
  Symmetric = true
FEATURE [Part::Cut] Cut048
  Base = -> Cut047
  Refine = true
  Tool = -> Extrude083
FEATURE [Sketcher::SketchObject] Sketch144  label="foro_areazione_alimentatore"
  ArcFitTolerance = 1e-06
  AttachmentSupport = -> [XZ_Plane]
  ExternalGeometry = -> [Sketch036]
  FullyConstrained = true
  MakeInternals = false
  MapMode = 5
  Placement = pos=(0,0,0) rot=(1,0,0;1.5708rad)
  sketch-geometry (4):
    g0: LineSegment StartX=-211.843 StartY=-60.3701 StartZ=0 EndX=-207.775 EndY=-60.3701 EndZ=0
    g1: LineSegment StartX=-207.775 StartY=-60.3701 StartZ=0 EndX=-207.775 EndY=-70.3701 EndZ=0
    g2: LineSegment StartX=-211.843 StartY=-60.3701 StartZ=0 EndX=-211.843 EndY=-70.3701 EndZ=0
    g3: LineSegment StartX=-207.775 StartY=-70.3701 StartZ=0 EndX=-211.843 EndY=-70.3701 EndZ=0
  constraints (11):
    c: Horizontal(g0)
    c: Distance(g1) = 10
    c: Coincident(g1,g0)
    c: Tangent(g1,g-3)
    c: PointOnObject(g0,g-4)
    c: Coincident(g2,g0)
    c: PointOnObject(g2,g-4)
    c: Coincident(g3,g1)
    c: Horizontal(g3)
    c: Coincident(g3,g2)
    c: DistanceY(g0,g-3) = 19
FEATURE [Part::Extrusion] Extrude084  label="Extrude084 - foro_areazione_alimentatore"
  Base = -> Sketch144
  Dir = (0,-1,2e-16)
  DirMode = 2
  FaceMakerClass = Part::FaceMakerBullseye
  FaceMakerMode = 3
  LengthFwd = 10
  LengthRev = 0
  Solid = true
  Symmetric = true
FEATURE [Part::Cut] Cut049
  Base = -> Cut048
  Refine = true
  Tool = -> Extrude084
FEATURE [Sketcher::SketchObject] Sketch145  label="foro_per_condesatore"
  ArcFitTolerance = 1e-06
  AttachmentSupport = -> [XZ_Plane]
  ExternalGeometry = -> [Sketch138]
  FullyConstrained = true
  MakeInternals = false
  MapMode = 5
  Placement = pos=(0,0,0) rot=(1,0,0;1.5708rad)
  sketch-geometry (1):
    g0: Circle CenterX=-179.742 CenterY=9.59337 CenterZ=0 NormalX=0 NormalY=0 NormalZ=1 AngleXU=0 Radius=5.4
  constraints (3):
    c: Diameter(g0) = 10.8
    c: DistanceX(g-3,g0) = 10
    c: DistanceY(g-3,g0) = 4.8
FEATURE [Part::Extrusion] Extrude085  label="Extrude085 - foro_per_condesatore"
  Base = -> Sketch145
  Dir = (0,-1,2e-16)
  DirMode = 2
  FaceMakerClass = Part::FaceMakerBullseye
  FaceMakerMode = 3
  LengthFwd = 25.2
  LengthRev = 0
  Solid = true
  Symmetric = true
FEATURE [Part::Cut] Cut050
  Base = -> Cut049
  Refine = true
  Tool = -> Extrude085
FEATURE [Sketcher::SketchObject] Sketch146  label="scavo_pulsante_6x6_per_led_batteria"
  ArcFitTolerance = 1e-06
  AttachmentSupport = -> [XZ_Plane]
  ExternalGeometry = -> [Sketch016]
  FullyConstrained = true
  MakeInternals = false
  MapMode = 5
  Placement = pos=(0,0,0) rot=(1,0,0;1.5708rad)
  sketch-geometry (5):
    g0: LineSegment StartX=-216.643 StartY=-65.8316 StartZ=0 EndX=-216.643 EndY=-72.8316 EndZ=0
    g1: LineSegment StartX=-216.643 StartY=-72.8316 StartZ=0 EndX=-210.243 EndY=-72.8316 EndZ=0
    g2: LineSegment StartX=-210.243 StartY=-72.8316 StartZ=0 EndX=-210.243 EndY=-65.8316 EndZ=0
    g3: LineSegment StartX=-210.243 StartY=-65.8316 StartZ=0 EndX=-216.643 EndY=-65.8316 EndZ=0
    g4: GeomPoint [constr] X=-213.443 Y=-69.3316 Z=0
  constraints (13):
    c: Coincident(g0,g1)
    c: Coincident(g1,g2)
    c: Coincident(g2,g3)
    c: Coincident(g3,g0)
    c: Vertical(g0)
    c: Vertical(g2)
    c: Horizontal(g1)
    c: Horizontal(g3)
    c: Distance(g0,g2) = 6.4
    c: Distance(g1,g3) = 7
    c: Tangent(g1,g-3)
    c: Symmetric(g0,g2,g4)
    c: Vertical(g-3,g4)
FEATURE [Part::Extrusion] Extrude086  label="Extrude086 - scavo_pulsante_6x6_per_led_batteria"
  Base = -> Sketch146
  Dir = (0,-1,2e-16)
  DirMode = 2
  FaceMakerClass = Part::FaceMakerBullseye
  FaceMakerMode = 3
  LengthFwd = 4
  LengthRev = 0
  Placement = pos=(0,12.6,0) rot=(0,0,1;0rad)
  Solid = true
  Symmetric = false
FEATURE [Sketcher::SketchObject] Sketch147  label="scavo_led_stato_batteria"
  ArcFitTolerance = 1e-06
  AttachmentSupport = -> [XZ_Plane]
  ExternalGeometry = -> [Sketch016]
  FullyConstrained = true
  MakeInternals = false
  MapMode = 5
  Placement = pos=(0,0,0) rot=(1,0,0;1.5708rad)
  sketch-geometry (5):
    g0: LineSegment StartX=-215.843 StartY=-56.2316 StartZ=0 EndX=-215.843 EndY=-65.4316 EndZ=0
    g1: LineSegment StartX=-215.843 StartY=-65.4316 StartZ=0 EndX=-211.043 EndY=-65.4316 EndZ=0
    g2: LineSegment StartX=-211.043 StartY=-65.4316 StartZ=0 EndX=-211.043 EndY=-56.2316 EndZ=0
    g3: LineSegment StartX=-211.043 StartY=-56.2316 StartZ=0 EndX=-215.843 EndY=-56.2316 EndZ=0
    g4: GeomPoint [constr] X=-213.443 Y=-60.8316 Z=0
  constraints (13):
    c: Coincident(g0,g1)
    c: Coincident(g1,g2)
    c: Coincident(g2,g3)
    c: Coincident(g3,g0)
    c: Distance(g0,g2) = 4.8
    c: Distance(g1,g3) = 9.2
    c: Equal(g0,g2)
    c: Equal(g1,g3)
    c: Perpendicular(g3,g0)
    c: DistanceY(g-3,g0) = 11.4
    c: Vertical(g2)
    c: Symmetric(g0,g2,g4)
    c: Vertical(g4,g-3)
FEATURE [Part::Extrusion] Extrude087  label="Extrude087 - scavo_led_stato_batteria"
  Base = -> Sketch147
  Dir = (0,-1,2e-16)
  DirMode = 2
  FaceMakerClass = Part::FaceMakerBullseye
  FaceMakerMode = 3
  LengthFwd = 2.2
  LengthRev = 0
  Placement = pos=(0,12.6,0) rot=(0,0,1;0rad)
  Solid = true
  Symmetric = false
FEATURE [Sketcher::SketchObject] Sketch148
  ArcFitTolerance = 1e-06
  AttachmentSupport = -> [Pad016]
  ExternalGeometry = -> [Pad016]
  FullyConstrained = true
  MakeInternals = false
  MapMode = 5
  Placement = pos=(0,0,-80.4316) rot=(1,0,0;3.14159rad)
  sketch-geometry (8):
    g0: LineSegment StartX=-176.685 StartY=3.6 StartZ=0 EndX=-186.685 EndY=3.6 EndZ=0
    g1: LineSegment StartX=-176.685 StartY=3.6 StartZ=0 EndX=-176.685 EndY=-9e-16 EndZ=0
    g2: LineSegment [constr] StartX=-186.685 StartY=3.6 StartZ=0 EndX=-186.685 EndY=-9e-16 EndZ=0
    g3: ArcOfEllipse CenterX=-186.685 CenterY=-9e-16 CenterZ=0 NormalX=0 NormalY=0 NormalZ=1 MajorRadius=10 MinorRadius=3.6 AngleXU=0 StartAngle=0 EndAngle=1.5708
    g4: LineSegment [constr] StartX=-176.685 StartY=-1e-15 StartZ=0 EndX=-196.685 EndY=-1e-15 EndZ=0
    g5: LineSegment [constr] StartX=-186.685 StartY=3.6 StartZ=0 EndX=-186.685 EndY=-3.6 EndZ=0
    g6: GeomPoint [constr] X=-177.356 Y=-1e-15 Z=0
    g7: GeomPoint [constr] X=-196.015 Y=-1e-15 Z=0
  constraints (13):
    c: Distance(g0) = 10
    c: Coincident(g0,g-5)
    c: PointOnObject(g0,g-3)
    c: Coincident(g1,g0)
    c: Coincident(g1,g-5)
    c: Coincident(g2,g0)
    c: Vertical(g2)
    c: PointOnObject(g2,g-4)
    c: InternalAlignment(g4-g7 -> g3) x4
    c: Coincident(g3,g2)
    c: Coincident(g3,g0)
    c: Coincident(g3,g1)
    c: Horizontal(g4)
FEATURE [PartDesign::SubtractivePipe] SubtractivePipe004
  AuxilleryCurvelinear = true
  AuxillerySpineTangent = false
  BaseFeature = -> Pad016
  Binormal = (0,0,0)
  Mode = 0
  Profile = -> Sketch148
  Refine = true
  Spine = -> Pad016 [Edge253]
  SpineTangent = false
  Suppressed = false
  Transformation = 0
  Transition = 0
FEATURE [Sketcher::SketchObject] Sketch149
  ArcFitTolerance = 1e-06
  AttachmentSupport = -> [Pad016]
  ExternalGeometry = -> [Pad016]
  FullyConstrained = true
  MakeInternals = false
  MapMode = 5
  Placement = pos=(0,0,-80.4316) rot=(1,0,0;3.14159rad)
  sketch-geometry (8):
    g0: LineSegment StartX=-215.932 StartY=3.6 StartZ=0 EndX=-205.932 EndY=3.6 EndZ=0
    g1: LineSegment StartX=-215.932 StartY=3.6 StartZ=0 EndX=-215.932 EndY=-4e-16 EndZ=0
    g2: LineSegment [constr] StartX=-205.932 StartY=3.6 StartZ=0 EndX=-205.932 EndY=-9e-16 EndZ=0
    g3: ArcOfEllipse CenterX=-205.932 CenterY=-1e-15 CenterZ=0 NormalX=0 NormalY=0 NormalZ=1 MajorRadius=10 MinorRadius=3.6 AngleXU=-3.14159 StartAngle=4.71239 EndAngle=6.28319
    g4: LineSegment [constr] StartX=-215.932 StartY=-1e-15 StartZ=0 EndX=-195.932 EndY=-1e-15 EndZ=0
    g5: LineSegment [constr] StartX=-205.932 StartY=-3.6 StartZ=0 EndX=-205.932 EndY=3.6 EndZ=0
    g6: GeomPoint [constr] X=-215.262 Y=-2.1e-15 Z=0
    g7: GeomPoint [constr] X=-196.602 Y=-9e-16 Z=0
  constraints (13):
    c: Distance(g0) = 10
    c: Coincident(g0,g-5)
    c: PointOnObject(g0,g-5)
    c: Coincident(g1,g0)
    c: Coincident(g1,g-4)
    c: Coincident(g2,g0)
    c: Vertical(g2)
    c: PointOnObject(g2,g-3)
    c: InternalAlignment(g4-g7 -> g3) x4
    c: Coincident(g3,g2)
    c: Coincident(g3,g0)
    c: Coincident(g3,g1)
    c: Horizontal(g4)
FEATURE [PartDesign::SubtractivePipe] SubtractivePipe005
  AuxilleryCurvelinear = true
  AuxillerySpineTangent = false
  BaseFeature = -> SubtractivePipe004
  Binormal = (0,0,0)
  Mode = 0
  Profile = -> Sketch149
  Refine = true
  Spine = -> Pad016 [Edge251,Edge256,Edge255]
  SpineTangent = false
  Suppressed = false
  Transformation = 0
  Transition = 0
FEATURE [PartDesign::SubtractiveLoft] SubtractiveLoft002
  BaseFeature = -> SubtractivePipe005
  Closed = false
  Profile = -> Sketch129
  Refine = true
  Ruled = false
  Sections = -> [Sketch130]
  Suppressed = false
FEATURE [PartDesign::SubtractiveLoft] SubtractiveLoft003
  BaseFeature = -> SubtractiveLoft002
  Closed = false
  Profile = -> Clone2D001
  Refine = true
  Ruled = false
  Sections = -> [Sketch131]
  Suppressed = false
FEATURE [PartDesign::Chamfer] Chamfer010
  Angle = 45
  Base = -> SubtractiveLoft003 [Edge203,Edge204,Edge202,Edge201,Edge195]
  BaseFeature = -> SubtractiveLoft003
  ChamferType = 0
  FlipDirection = false
  Refine = true
  Size = 1.5
  Size2 = 1
  SupportTransform = false
  Suppressed = false
  UseAllEdges = false
FEATURE [PartDesign::Chamfer] Chamfer011
  Angle = 45
  Base = -> Chamfer010 [Edge15]
  BaseFeature = -> Chamfer010
  ChamferType = 0
  FlipDirection = false
  Refine = true
  Size = 1.6
  Size2 = 1
  SupportTransform = false
  Suppressed = false
  UseAllEdges = false
FEATURE [PartDesign::Chamfer] Chamfer012
  Angle = 45
  Base = -> Chamfer011 [Edge10]
  BaseFeature = -> Chamfer011
  ChamferType = 0
  FlipDirection = false
  Refine = true
  Size = 3.5
  Size2 = 1
  SupportTransform = false
  Suppressed = false
  UseAllEdges = false
FEATURE [PartDesign::Chamfer] Chamfer013
  Angle = 45
  Base = -> Chamfer012 [Edge94]
  BaseFeature = -> Chamfer012
  ChamferType = 0
  FlipDirection = false
  Refine = true
  Size = 1.9
  Size2 = 1
  SupportTransform = false
  Suppressed = false
  UseAllEdges = false
FEATURE [PartDesign::Fillet] Fillet007
  Base = -> Chamfer013 [Edge83]
  BaseFeature = -> Chamfer013
  Radius = 1.1
  Refine = true
  SupportTransform = false
  Suppressed = false
  UseAllEdges = false
FEATURE [PartDesign::Fillet] Fillet008
  Base = -> Fillet007 [Edge75]
  BaseFeature = -> Fillet007
  Radius = 1.9
  Refine = true
  SupportTransform = false
  Suppressed = false
  UseAllEdges = false
FEATURE [PartDesign::Pocket] Pocket011
  BaseFeature = -> Fillet008
  Direction = (0,1,-2e-16)
  Length = 0.8
  Length2 = 5
  Profile = -> Sketch132
  ReferenceAxis = -> Sketch132 [N_Axis]
  Refine = true
  Suppressed = false
  Type = 0
FEATURE [PartDesign::Pocket] Pocket012
  BaseFeature = -> Pocket011
  Direction = (0,1,0)
  Length = 1
  Length2 = 5
  Profile = -> ShapeString
  ReferenceAxis = -> ShapeString [N_Axis]
  Refine = true
  Suppressed = false
  Type = 0
FEATURE [Sketcher::SketchObject] Sketch150
  ArcFitTolerance = 1e-06
  AttachmentSupport = -> [Pad008]
  ExternalGeometry = -> [Pad008]
  FullyConstrained = true
  MakeInternals = false
  MapMode = 5
  Placement = pos=(0,3.6,0) rot=(0,0.707107,0.707107;3.14159rad)
  sketch-geometry (7):
    g0: LineSegment [constr] StartX=210.343 StartY=-66.0316 StartZ=0 EndX=210.343 EndY=-72.8316 EndZ=0
    g1: LineSegment [constr] StartX=210.343 StartY=-72.8316 StartZ=0 EndX=216.543 EndY=-72.8316 EndZ=0
    g2: LineSegment [constr] StartX=216.543 StartY=-72.8316 StartZ=0 EndX=216.543 EndY=-66.0316 EndZ=0
    g3: LineSegment [constr] StartX=216.543 StartY=-66.0316 StartZ=0 EndX=210.343 EndY=-66.0316 EndZ=0
    g4: LineSegment [constr] StartX=210.343 StartY=-72.8316 StartZ=0 EndX=216.543 EndY=-66.0316 EndZ=0
    g5: LineSegment [constr] StartX=210.343 StartY=-66.0316 StartZ=0 EndX=213.443 EndY=-69.4316 EndZ=0
    g6: Circle CenterX=213.443 CenterY=-69.4316 CenterZ=0 NormalX=0 NormalY=0 NormalZ=1 AngleXU=0 Radius=2
  constraints (18):
    c: Coincident(g0,g1)
    c: Coincident(g1,g2)
    c: Coincident(g2,g3)
    c: Coincident(g3,g0)
    c: Vertical(g0)
    c: Vertical(g2)
    c: Horizontal(g1)
    c: Horizontal(g3)
    c: Distance(g0,g2) = 6.2
    c: Distance(g1,g3) = 6.8
    c: DistanceY(g-3,g1) = 4
    c: Coincident(g4,g0)
    c: Coincident(g4,g2)
    c: Coincident(g5,g0)
    c: Symmetric(g0,g2,g5)
    c: Diameter(g6) = 4
    c: Coincident(g6,g5)
    c: Vertical(g5,g-3)
FEATURE [Sketcher::SketchObject] Sketch151
  ArcFitTolerance = 1e-06
  AttachmentSupport = -> [Pad008]
  ExternalGeometry = -> [Pad008]
  FullyConstrained = true
  MakeInternals = false
  MapMode = 5
  Placement = pos=(0,3.6,0) rot=(0,0.707107,0.707107;3.14159rad)
  sketch-geometry (10):
    g0: LineSegment [constr] StartX=211.143 StartY=-56.2316 StartZ=0 EndX=211.143 EndY=-65.4316 EndZ=0
    g1: LineSegment [constr] StartX=211.143 StartY=-65.4316 StartZ=0 EndX=215.743 EndY=-65.4316 EndZ=0
    g2: LineSegment [constr] StartX=215.743 StartY=-65.4316 StartZ=0 EndX=215.743 EndY=-56.2316 EndZ=0
    g3: LineSegment [constr] StartX=215.743 StartY=-56.2316 StartZ=0 EndX=211.143 EndY=-56.2316 EndZ=0
    g4: LineSegment StartX=212.243 StartY=-63.8316 StartZ=0 EndX=214.643 EndY=-63.8316 EndZ=0
    g5: LineSegment StartX=214.643 StartY=-63.8316 StartZ=0 EndX=214.643 EndY=-57.0316 EndZ=0
    g6: LineSegment StartX=214.643 StartY=-57.0316 StartZ=0 EndX=212.243 EndY=-57.0316 EndZ=0
    g7: LineSegment StartX=212.243 StartY=-57.0316 StartZ=0 EndX=212.243 EndY=-63.8316 EndZ=0
    g8: GeomPoint [constr] X=213.443 Y=-60.4316 Z=0
    g9: GeomPoint [constr] X=213.443 Y=-60.8316 Z=0
  constraints (26):
    c: Coincident(g0,g1)
    c: Coincident(g1,g2)
    c: Coincident(g2,g3)
    c: Coincident(g3,g0)
    c: Vertical(g0)
    c: Vertical(g2)
    c: Horizontal(g1)
    c: Horizontal(g3)
    c: Distance(g0,g2) = 4.6
    c: Distance(g1,g3) = 9.2
    c: DistanceY(g-3,g1) = 11.4
    c: Coincident(g4,g5)
    c: Coincident(g5,g6)
    c: Coincident(g6,g7)
    c: Coincident(g7,g4)
    c: Horizontal(g4)
    c: Horizontal(g6)
    c: Vertical(g5)
    c: Vertical(g7)
    c: Symmetric(g6,g4,g8)
    c: Distance(g5,g7) = 2.4
    c: Distance(g4,g6) = 6.8
    c: Symmetric(g2,g0,g9)
    c: Vertical(g8,g9)
    c: DistanceY(g1,g4) = 1.6
    c: Vertical(g9,g-3)
FEATURE [PartDesign::Pocket] Pocket019
  BaseFeature = -> Pocket013
  Direction = (0,-1,2e-16)
  Length = 3.6
  Length2 = 5
  Profile = -> Sketch151
  ReferenceAxis = -> Sketch151 [N_Axis]
  Refine = true
  Suppressed = false
  Type = 0
FEATURE [PartDesign::Pocket] Pocket018
  BaseFeature = -> Pocket019
  Direction = (0,-1,2e-16)
  Length = 3.6
  Length2 = 5
  Profile = -> Sketch150
  ReferenceAxis = -> Sketch150 [N_Axis]
  Refine = true
  Suppressed = false
  Type = 0
FEATURE [PartDesign::Point] DatumPoint
  AttacherType = Attacher::AttachEnginePoint
  AttachmentSupport = -> [Sketch150]
  MapMode = 36
  Placement = pos=(-213.443,3.6,-69.4316) rot=(0,1,0;3.14159rad)
FEATURE [PartDesign::Plane] DatumPlane002
  AttachmentSupport = -> [DatumPoint]
  Length = 265.655
  MapMode = 1
  Placement = pos=(-213.443,3.6,-69.4316) rot=(0,0,1;0rad)
  ResizeMode = 0
  Width = 72.0719
FEATURE [Sketcher::SketchObject] Sketch152
  ArcFitTolerance = 1e-06
  AttachmentSupport = -> [DatumPlane002]
  ExternalGeometry = -> [Sketch150]
  FullyConstrained = true
  MakeInternals = false
  MapMode = 5
  Placement = pos=(-213.443,3.6,-69.4316) rot=(0,0,1;0rad)
  sketch-geometry (7):
    g0: LineSegment StartX=0 StartY=0 StartZ=0 EndX=-4 EndY=5.1e-15 EndZ=0
    g1: ArcOfEllipse CenterX=0 CenterY=0 CenterZ=0 NormalX=0 NormalY=0 NormalZ=1 MajorRadius=4 MinorRadius=3.6 AngleXU=3.14159 StartAngle=2e-16 EndAngle=1.5708
    g2: LineSegment [constr] StartX=-4 StartY=9e-16 StartZ=0 EndX=4 EndY=-9e-16 EndZ=0
    g3: LineSegment [constr] StartX=0 StartY=-3.6 StartZ=0 EndX=0 EndY=3.6 EndZ=0
    g4: GeomPoint [constr] X=-1.74356 Y=2.5e-15 Z=0
    g5: GeomPoint [constr] X=1.74356 Y=-2e-15 Z=0
    g6: LineSegment StartX=0 StartY=0 StartZ=0 EndX=-5.5e-15 EndY=-3.6 EndZ=0
  constraints (11):
    c: PointOnObject(g1,g-2)
    c: Distance(g0) = 4
    c: PointOnObject(g0,g-1)
    c: InternalAlignment(g2-g5 -> g1) x4
    c: Coincident(g1,g0)
    c: Vertical(g3)
    c: Coincident(g1,g-1)
    c: Distance(g6) = 3.6
    c: Coincident(g6,g1)
    c: Coincident(g1,g6)
    c: Coincident(g0,g1)
FEATURE [PartDesign::Groove] Groove
  Angle = 360
  Angle2 = 60
  Axis = (0,1,0)
  Base = (-213.443,3.6,-69.4316)
  BaseFeature = -> Pocket018
  Profile = -> Sketch152
  ReferenceAxis = -> Sketch152 [V_Axis]
  Refine = true
  Reversed = true
  Suppressed = false
  Type = 0
FEATURE [PartDesign::Body] Body006  label="lato SX"
  AllowCompound = false
  Group = -> [Binder,Pad019,Chamfer015,Pocket002,Sketch133,Sketch091,Pad005,Sketch092,Pocket001,Sketch093,Sketch094,Pad006,Sketch095,Pad007,Sketch096,Pad008,Sketch097,Pad009,Chamfer005,Pocket004,Sketch098,Pad010,Chamfer006,Pocket003,SubtractivePipe,SubtractivePipe001,Sketch099,Sketch106,Sketch107,Sketch108,Clone2D,Sketch109,SubtractiveLoft,SubtractiveLoft001,Sketch110,Sketch111,Sketch112,Chamfer016,Chamfer017,+15 more]
  Origin = -> Origin006
  Tip = -> Groove
FEATURE [Sketcher::SketchObject] Sketch153  label="ripieno_per_sostegno_led_batteria"
  ArcFitTolerance = 1e-06
  AttachmentSupport = -> [XZ_Plane]
  ExternalGeometry = -> [Sketch036]
  FullyConstrained = true
  MakeInternals = false
  MapMode = 5
  Placement = pos=(0,0,0) rot=(1,0,0;1.5708rad)
  sketch-geometry (4):
    g0: LineSegment StartX=-217.343 StartY=-54.5944 StartZ=0 EndX=-217.343 EndY=-63.1944 EndZ=0
    g1: LineSegment StartX=-217.343 StartY=-63.1944 StartZ=0 EndX=-211.843 EndY=-63.1944 EndZ=0
    g2: LineSegment StartX=-211.843 StartY=-63.1944 StartZ=0 EndX=-211.843 EndY=-54.5944 EndZ=0
    g3: LineSegment StartX=-211.843 StartY=-54.5944 StartZ=0 EndX=-217.343 EndY=-54.5944 EndZ=0
  constraints (11):
    c: Coincident(g0,g1)
    c: Coincident(g1,g2)
    c: Coincident(g2,g3)
    c: Coincident(g3,g0)
    c: Vertical(g0)
    c: Horizontal(g1)
    c: Horizontal(g3)
    c: Tangent(g2,g-3)
    c: DistanceY(g2,g-3) = 4.5
    c: DistanceX(g3,g3) = 5.5
    c: DistanceY(g0,g0) = 8.6
FEATURE [Part::Extrusion] Extrude088  label="Extrude088 - ripieno_per_sostegno_led_batteria"
  Base = -> Sketch153
  Dir = (0,-1,2e-16)
  DirMode = 2
  FaceMakerClass = Part::FaceMakerBullseye
  FaceMakerMode = 3
  LengthFwd = 4
  LengthRev = 0
  Placement = pos=(0,12.6,0) rot=(0,0,1;0rad)
  Solid = true
  Symmetric = false
FEATURE [Part::MultiFuse] Fusion004
  Refine = true
  Shapes = -> [Cut050,Extrude088]
FEATURE [Part::Cut] Cut051
  Base = -> Fusion004
  Refine = true
  Tool = -> Extrude087
FEATURE [Part::Cut] Cut052
  Base = -> Cut051
  Refine = true
  Tool = -> Extrude086
FEATURE [Sketcher::SketchObject] Sketch154
  ArcFitTolerance = 1e-06
  AttachmentSupport = -> [Pad016]
  ExternalGeometry = -> [Binder001]
  FullyConstrained = true
  MakeInternals = false
  MapMode = 5
  Placement = pos=(0,-3.6,0) rot=(1,0,0;1.5708rad)
  sketch-geometry (25):
    g0: LineSegment StartX=-214.643 StartY=-72.4316 StartZ=0 EndX=-212.243 EndY=-72.4316 EndZ=0
    g1: LineSegment StartX=-212.243 StartY=-72.4316 StartZ=0 EndX=-212.243 EndY=-71.2316 EndZ=0
    g2: LineSegment StartX=-212.243 StartY=-71.2316 StartZ=0 EndX=-214.643 EndY=-71.2316 EndZ=0
    g3: LineSegment StartX=-214.643 StartY=-71.2316 StartZ=0 EndX=-214.643 EndY=-72.4316 EndZ=0
    g4: GeomPoint [constr] X=-213.443 Y=-71.8316 Z=0
    g5: LineSegment StartX=-214.643 StartY=-69.6316 StartZ=0 EndX=-212.243 EndY=-69.6316 EndZ=0
    g6: LineSegment StartX=-212.243 StartY=-69.6316 StartZ=0 EndX=-212.243 EndY=-68.4316 EndZ=0
    g7: LineSegment StartX=-212.243 StartY=-68.4316 StartZ=0 EndX=-214.643 EndY=-68.4316 EndZ=0
    g8: LineSegment StartX=-214.643 StartY=-68.4316 StartZ=0 EndX=-214.643 EndY=-69.6316 EndZ=0
    g9: GeomPoint [constr] X=-213.443 Y=-69.0316 Z=0
    g10: LineSegment StartX=-214.643 StartY=-66.8316 StartZ=0 EndX=-212.243 EndY=-66.8316 EndZ=0
    g11: LineSegment StartX=-212.243 StartY=-66.8316 StartZ=0 EndX=-212.243 EndY=-65.6316 EndZ=0
    g12: LineSegment StartX=-212.243 StartY=-65.6316 StartZ=0 EndX=-214.643 EndY=-65.6316 EndZ=0
    g13: LineSegment StartX=-214.643 StartY=-65.6316 StartZ=0 EndX=-214.643 EndY=-66.8316 EndZ=0
    g14: GeomPoint [constr] X=-213.443 Y=-66.2316 Z=0
    g15: LineSegment StartX=-214.643 StartY=-64.0316 StartZ=0 EndX=-212.243 EndY=-64.0316 EndZ=0
    g16: LineSegment StartX=-212.243 StartY=-64.0316 StartZ=0 EndX=-212.243 EndY=-62.8316 EndZ=0
    g17: LineSegment StartX=-212.243 StartY=-62.8316 StartZ=0 EndX=-214.643 EndY=-62.8316 EndZ=0
    g18: LineSegment StartX=-214.643 StartY=-62.8316 StartZ=0 EndX=-214.643 EndY=-64.0316 EndZ=0
    g19: GeomPoint [constr] X=-213.443 Y=-63.4316 Z=0
    g20: LineSegment StartX=-214.643 StartY=-61.2316 StartZ=0 EndX=-212.243 EndY=-61.2316 EndZ=0
    g21: LineSegment StartX=-212.243 StartY=-61.2316 StartZ=0 EndX=-212.243 EndY=-60.0316 EndZ=0
    g22: LineSegment StartX=-212.243 StartY=-60.0316 StartZ=0 EndX=-214.643 EndY=-60.0316 EndZ=0
    g23: LineSegment StartX=-214.643 StartY=-60.0316 StartZ=0 EndX=-214.643 EndY=-61.2316 EndZ=0
    g24: GeomPoint [constr] X=-213.443 Y=-60.6316 Z=0
  constraints (65):
    c: Coincident(g0,g1)
    c: Coincident(g1,g2)
    c: Coincident(g2,g3)
    c: Coincident(g3,g0)
    c: Horizontal(g0)
    c: Horizontal(g2)
    c: Vertical(g1)
    c: Vertical(g3)
    c: Symmetric(g2,g0,g4)
    c: Distance(g1,g3) = 2.4
    c: Distance(g0,g2) = 1.2
    c: Coincident(g5,g6)
    c: Coincident(g6,g7)
    c: Coincident(g7,g8)
    c: Coincident(g8,g5)
    c: Horizontal(g5)
    c: Horizontal(g7)
    c: Vertical(g6)
    c: Vertical(g8)
    c: Symmetric(g7,g5,g9)
    c: Distance(g6,g8) = 2.4
    c: Distance(g5,g7) = 1.2
    c: Coincident(g10,g11)
    c: Coincident(g11,g12)
    c: Coincident(g12,g13)
    c: Coincident(g13,g10)
    c: Horizontal(g10)
    c: Horizontal(g12)
    c: Vertical(g11)
    c: Vertical(g13)
    c: Symmetric(g12,g10,g14)
    c: Distance(g11,g13) = 2.4
    c: Distance(g10,g12) = 1.2
    c: Coincident(g15,g16)
    c: Coincident(g16,g17)
    c: Coincident(g17,g18)
    c: Coincident(g18,g15)
    c: Horizontal(g15)
    c: Horizontal(g17)
    c: Vertical(g16)
    c: Vertical(g18)
    c: Symmetric(g17,g15,g19)
    c: Distance(g16,g18) = 2.4
    c: Distance(g15,g17) = 1.2
    c: Vertical(g4,g-3)
    c: Vertical(g9,g-3)
    c: Vertical(g14,g-3)
    c: Vertical(g19,g-3)
    c: DistanceY(g-3,g4) = 5
    c: DistanceY(g4,g9) = 2.8
    c: DistanceY(g9,g14) = 2.8
    c: DistanceY(g14,g19) = 2.8
    c: Coincident(g20,g21)
    c: Coincident(g21,g22)
    c: Coincident(g22,g23)
    c: Coincident(g23,g20)
    c: Horizontal(g20)
    c: Horizontal(g22)
    c: Vertical(g21)
    c: Vertical(g23)
    c: Symmetric(g22,g20,g24)
    c: Distance(g21,g23) = 2.4
    c: Distance(g20,g22) = 1.2
    c: DistanceY(g19,g24) = 2.8
    c: Vertical(g-3,g24)
FEATURE [PartDesign::Pocket] Pocket020
  BaseFeature = -> Pocket012
  Direction = (0,1,-2e-16)
  Length = 3.6
  Length2 = 5
  Profile = -> Sketch154
  ReferenceAxis = -> Sketch154 [N_Axis]
  Refine = true
  Suppressed = false
  Type = 0
FEATURE [PartDesign::Body] Body007  label="lato DX"
  AllowCompound = false
  Group = -> [Binder001,Sketch114,Pad011,Chamfer014,Sketch115,Pocket006,Sketch116,Pad012,Sketch117,Pocket007,Sketch118,Pad013,Sketch119,Pocket008,Pad017,Chamfer009,Pocket009,Sketch123,Sketch120,Pad014,Pad018,Chamfer008,Pocket010,Sketch121,Pad015,Sketch122,Pad016,SubtractivePipe004,SubtractivePipe005,Sketch149,Sketch148,Sketch124,Sketch125,Sketch126,Sketch129,Sketch130,Clone2D001,Sketch131,SubtractiveLoft002,+13 more]
  Origin = -> Origin007
  Tip = -> Pocket020
FEATURE [Sketcher::SketchObject] Sketch155  label="fermo per protezione batteria"
  ArcFitTolerance = 1e-06
  AttachmentSupport = -> [XZ_Plane]
  ExternalGeometry = -> [Sketch016,Sketch]
  FullyConstrained = true
  MakeInternals = false
  MapMode = 5
  Placement = pos=(0,0,0) rot=(1,0,0;1.5708rad)
  sketch-geometry (5):
    g0: LineSegment StartX=-183.305 StartY=-76.0316 StartZ=0 EndX=-179.305 EndY=-76.0316 EndZ=0
    g1: LineSegment StartX=-179.305 StartY=-76.0316 StartZ=0 EndX=-179.305 EndY=-74.4316 EndZ=0
    g2: LineSegment StartX=-179.305 StartY=-74.4316 StartZ=0 EndX=-183.305 EndY=-74.4316 EndZ=0
    g3: LineSegment [constr] StartX=-183.305 StartY=-76.0316 StartZ=0 EndX=-183.305 EndY=-78.4316 EndZ=0
    g4: LineSegment StartX=-183.305 StartY=-74.4316 StartZ=0 EndX=-183.305 EndY=-76.0316 EndZ=0
  constraints (16):
    c: Horizontal(g0)
    c: Distance(g1) = 1.6
    c: Coincident(g1,g0)
    c: Vertical(g1)
    c: Coincident(g2,g1)
    c: Horizontal(g2)
    c: Vertical(g3)
    c: PointOnObject(g3,g-4)
    c: Horizontal(g3,g0)
    c: Tangent(g3,g-3)
    c: Vertical(g0,g-3)
    c: Coincident(g4,g2)
    c: Coincident(g4,g0)
    c: Vertical(g4)
    c: Vertical(g0,g3)
    c: DistanceY(g3,g3) = 2.4
FEATURE [Part::Extrusion] Extrude089  label="Extrude089 - fermo per protezione batteria"
  Base = -> Sketch155
  Dir = (0,-1,2e-16)
  DirMode = 2
  FaceMakerClass = Part::FaceMakerBullseye
  FaceMakerMode = 3
  LengthFwd = 8
  LengthRev = 0
  Solid = true
  Symmetric = true
FEATURE [Sketcher::SketchObject] Sketch156  label="buco per protezione batteria"
  ArcFitTolerance = 1e-06
  AttachmentSupport = -> [XZ_Plane]
  ExternalGeometry = -> [Sketch,Sketch016]
  FullyConstrained = true
  MakeInternals = false
  MapMode = 5
  Placement = pos=(0,0,0) rot=(1,0,0;1.5708rad)
  sketch-geometry (5):
    g0: LineSegment [constr] StartX=-183.305 StartY=-76.8316 StartZ=0 EndX=-183.305 EndY=-78.4316 EndZ=0
    g1: LineSegment StartX=-200.305 StartY=-78.4316 StartZ=0 EndX=-200.305 EndY=-80.4316 EndZ=0
    g2: LineSegment StartX=-200.305 StartY=-80.4316 StartZ=0 EndX=-198.505 EndY=-80.4316 EndZ=0
    g3: LineSegment StartX=-198.505 StartY=-80.4316 StartZ=0 EndX=-198.505 EndY=-78.4316 EndZ=0
    g4: LineSegment StartX=-198.505 StartY=-78.4316 StartZ=0 EndX=-200.305 EndY=-78.4316 EndZ=0
  constraints (15):
    c: Vertical(g0)
    c: Tangent(g0,g-4)
    c: PointOnObject(g0,g-3)
    c: Horizontal(g0,g-4)
    c: Coincident(g1,g2)
    c: Coincident(g2,g3)
    c: Coincident(g3,g4)
    c: Coincident(g4,g1)
    c: Vertical(g1)
    c: Vertical(g3)
    c: Horizontal(g2)
    c: Distance(g1,g3) = 1.8
    c: Distance(g2,g4) = 2
    c: Tangent(g4,g-3)
    c: Distance(g3,g0) = 15.2
FEATURE [Part::Extrusion] Extrude090  label="Extrude090 - buco per protezione batteria"
  Base = -> Sketch156
  Dir = (0,-1,2e-16)
  DirMode = 2
  FaceMakerClass = Part::FaceMakerBullseye
  FaceMakerMode = 3
  LengthFwd = 4.8
  LengthRev = 0
  Solid = true
  Symmetric = true
FEATURE [Sketcher::SketchObject] Sketch157
  ArcFitTolerance = 1e-06
  AttachmentSupport = -> [XY_Plane010]
  FullyConstrained = true
  MakeInternals = false
  MapMode = 5
  sketch-geometry (9):
    g0: LineSegment [constr] StartX=1.8 StartY=8 StartZ=0 EndX=1.8 EndY=-8 EndZ=0
    g1: LineSegment StartX=1.8 StartY=8 StartZ=0 EndX=17 EndY=8 EndZ=0
    g2: LineSegment StartX=1.8 StartY=-8 StartZ=0 EndX=17 EndY=-8 EndZ=0
    g3: LineSegment StartX=0 StartY=8 StartZ=0 EndX=0 EndY=-8 EndZ=0
    g4: LineSegment StartX=1.8 StartY=8 StartZ=0 EndX=0 EndY=8 EndZ=0
    g5: LineSegment StartX=1.8 StartY=-8 StartZ=0 EndX=0 EndY=-8 EndZ=0
    g6: LineSegment StartX=17 StartY=8 StartZ=0 EndX=17 EndY=-8 EndZ=0
    g7: Circle CenterX=8.5 CenterY=0 CenterZ=0 NormalX=0 NormalY=0 NormalZ=1 AngleXU=0 Radius=5
    g8: LineSegment [constr] StartX=17 StartY=8 StartZ=0 EndX=17 EndY=0 EndZ=0
  constraints (23):
    c: DistanceY(g0,g0) = 16
    c: Distance(g1) = 15.2
    c: Coincident(g1,g0)
    c: Horizontal(g1)
    c: Coincident(g2,g0)
    c: Horizontal(g2)
    c: Equal(g1,g2)
    c: Symmetric(g0,g0,g-1)
    c: Equal(g3,g0)
    c: Coincident(g4,g0)
    c: Horizontal(g4)
    c: DistanceX(g4,g4) = 1.8
    c: Coincident(g5,g0)
    c: Horizontal(g5)
    c: Equal(g4,g5)
    c: Coincident(g3,g4)
    c: Tangent(g3,g-2)
    c: Coincident(g6,g1)
    c: Coincident(g6,g2)
    c: Coincident(g8,g1)
    c: Symmetric(g6,g6,g8)
    c: Symmetric(g8,g-1,g7)
    c: Diameter(g7) = 10
FEATURE [PartDesign::Pad] Pad031
  Direction = (0,0,1)
  Length = 1.4
  Length2 = 10
  Profile = -> Sketch157
  ReferenceAxis = -> Sketch157 [N_Axis]
  Refine = true
  Suppressed = false
  Type = 0
FEATURE [Sketcher::SketchObject] Sketch158
  ArcFitTolerance = 1e-06
  AttachmentSupport = -> [Pad031]
  ExternalGeometry = -> [Pad031]
  FullyConstrained = true
  MakeInternals = false
  MapMode = 5
  Placement = pos=(0,0,1.4) rot=(0,0,1;0rad)
  sketch-geometry (4):
    g0: LineSegment StartX=0 StartY=8 StartZ=0 EndX=0 EndY=-8 EndZ=0
    g1: LineSegment StartX=0 StartY=8 StartZ=0 EndX=1.8 EndY=8 EndZ=0
    g2: LineSegment StartX=1.8 StartY=8 StartZ=0 EndX=1.8 EndY=-8 EndZ=0
    g3: LineSegment StartX=0 StartY=-8 StartZ=0 EndX=1.8 EndY=-8 EndZ=0
  constraints (10):
    c: Coincident(g0,g-3)
    c: Coincident(g0,g-4)
    c: Distance(g1) = 1.8
    c: Coincident(g1,g0)
    c: PointOnObject(g1,g-3)
    c: Coincident(g2,g1)
    c: Vertical(g2)
    c: Coincident(g3,g0)
    c: PointOnObject(g3,g-4)
    c: Coincident(g3,g2)
FEATURE [PartDesign::Pad] Pad032
  BaseFeature = -> Pad031
  Direction = (0,0,1)
  Length = 6.4
  Length2 = 10
  Profile = -> Sketch158
  ReferenceAxis = -> Sketch158 [N_Axis]
  Refine = true
  Suppressed = false
  Type = 0
FEATURE [Sketcher::SketchObject] Sketch159
  ArcFitTolerance = 1e-06
  AttachmentSupport = -> [Pad032]
  ExternalGeometry = -> [Pad032,Pad031]
  FullyConstrained = true
  MakeInternals = false
  MapMode = 5
  Placement = pos=(0,0,7.8) rot=(0,0,1;0rad)
  sketch-geometry (7):
    g0: LineSegment StartX=0.1 StartY=2.2 StartZ=0 EndX=0.1 EndY=-2.2 EndZ=0
    g1: LineSegment StartX=0.1 StartY=-2.2 StartZ=0 EndX=1.7 EndY=-2.2 EndZ=0
    g2: LineSegment StartX=1.7 StartY=-2.2 StartZ=0 EndX=1.7 EndY=2.2 EndZ=0
    g3: LineSegment StartX=1.7 StartY=2.2 StartZ=0 EndX=0.1 EndY=2.2 EndZ=0
    g4: GeomPoint [constr] X=0.9 Y=8 Z=0
    g5: GeomPoint [constr] X=0.9 Y=-8 Z=0
    g6: LineSegment [constr] StartX=0.9 StartY=8 StartZ=0 EndX=0.9 EndY=-8 EndZ=0
  constraints (14):
    c: Coincident(g0,g1)
    c: Coincident(g1,g2)
    c: Coincident(g2,g3)
    c: Coincident(g3,g0)
    c: Vertical(g2)
    c: Horizontal(g1)
    c: Distance(g0,g2) = 1.6
    c: Distance(g1,g3) = 4.4
    c: Symmetric(g0,g0,g-1)
    c: Symmetric(g-4,g-4,g4)
    c: Symmetric(g-3,g-5,g5)
    c: Coincident(g6,g4)
    c: Coincident(g6,g5)
    c: Symmetric(g0,g2,g6)
FEATURE [PartDesign::Pad] Pad033
  BaseFeature = -> Pad032
  Direction = (0,0,1)
  Length = 1.4
  Length2 = 10
  Profile = -> Sketch159
  ReferenceAxis = -> Sketch159 [N_Axis]
  Refine = true
  Suppressed = false
  Type = 0
FEATURE [Part::Cut] Cut053
  Base = -> Cut052
  Refine = true
  Tool = -> Extrude089
FEATURE [Part::Cut] Cut054
  Base = -> Cut053
  Refine = true
  Tool = -> Extrude090
FEATURE [Sketcher::SketchObject] Sketch160
  ArcFitTolerance = 1e-06
  AttachmentSupport = -> [Pad033]
  ExternalGeometry = -> [Pad033]
  FullyConstrained = true
  MakeInternals = false
  MapMode = 5
  Placement = pos=(0,0,1.4) rot=(0,0,1;0rad)
  sketch-geometry (4):
    g0: LineSegment StartX=15.6 StartY=3.7 StartZ=0 EndX=15.6 EndY=-3.7 EndZ=0
    g1: LineSegment StartX=15.6 StartY=-3.7 StartZ=0 EndX=17 EndY=-3.7 EndZ=0
    g2: LineSegment StartX=17 StartY=-3.7 StartZ=0 EndX=17 EndY=3.7 EndZ=0
    g3: LineSegment StartX=17 StartY=3.7 StartZ=0 EndX=15.6 EndY=3.7 EndZ=0
  constraints (10):
    c: Coincident(g0,g1)
    c: Coincident(g1,g2)
    c: Coincident(g2,g3)
    c: Coincident(g3,g0)
    c: Horizontal(g1)
    c: Horizontal(g3)
    c: Distance(g0,g2) = 1.4
    c: Distance(g1,g3) = 7.4
    c: Symmetric(g0,g0,g-1)
    c: Tangent(g2,g-3)
FEATURE [PartDesign::Pad] Pad034
  BaseFeature = -> Pad033
  Direction = (0,0,1)
  Length = 2.4
  Length2 = 10
  Profile = -> Sketch160
  ReferenceAxis = -> Sketch160 [N_Axis]
  Refine = true
  Suppressed = false
  Type = 0
FEATURE [Sketcher::SketchObject] Sketch161
  ArcFitTolerance = 1e-06
  AttachmentSupport = -> [Pad034]
  ExternalGeometry = -> [Pad034]
  FullyConstrained = true
  MakeInternals = false
  MapMode = 5
  Placement = pos=(0,0,3.8) rot=(0,0,1;0rad)
  sketch-geometry (6):
    g0: LineSegment StartX=17 StartY=3.7 StartZ=0 EndX=21 EndY=3.7 EndZ=0
    g1: LineSegment StartX=17 StartY=3.7 StartZ=0 EndX=15.6 EndY=3.7 EndZ=0
    g2: LineSegment StartX=15.6 StartY=3.7 StartZ=0 EndX=15.6 EndY=-3.7 EndZ=0
    g3: LineSegment StartX=15.6 StartY=-3.7 StartZ=0 EndX=17 EndY=-3.7 EndZ=0
    g4: LineSegment StartX=17 StartY=-3.7 StartZ=0 EndX=21 EndY=-3.7 EndZ=0
    g5: LineSegment StartX=21 StartY=3.7 StartZ=0 EndX=21 EndY=-3.7 EndZ=0
  constraints (14):
    c: Distance(g0) = 4
    c: Coincident(g0,g-4)
    c: Horizontal(g0)
    c: Coincident(g1,g0)
    c: Coincident(g1,g-3)
    c: Coincident(g2,g1)
    c: Coincident(g2,g-5)
    c: Coincident(g3,g2)
    c: Coincident(g3,g-5)
    c: Coincident(g4,g3)
    c: Horizontal(g4)
    c: Equal(g4,g0)
    c: Coincident(g5,g0)
    c: Coincident(g5,g4)
FEATURE [PartDesign::Pad] Pad035
  BaseFeature = -> Pad034
  Direction = (0,0,1)
  Length = 1.4
  Length2 = 10
  Profile = -> Sketch161
  ReferenceAxis = -> Sketch161 [N_Axis]
  Refine = true
  Suppressed = false
  Type = 0
FEATURE [PartDesign::Body] Body010  label="Protezione_inferiore_batteria"
  AllowCompound = false
  Group = -> [Sketch157,Pad031,Sketch158,Pad032,Sketch159,Pad033,Sketch160,Pad034,Sketch161,Pad035]
  Origin = -> Origin010
  Tip = -> Pad035
FEATURE [Sketcher::SketchObject] Sketch162  label="scavo_saldature_nuovo_driver_alto"
  ArcFitTolerance = 1e-06
  AttachmentSupport = -> [XZ_Plane]
  ExternalGeometry = -> [Sketch138]
  FullyConstrained = true
  MakeInternals = false
  MapMode = 5
  Placement = pos=(0,0,0) rot=(1,0,0;1.5708rad)
  sketch-geometry (4):
    g0: LineSegment StartX=-192.503 StartY=17.8001 StartZ=0 EndX=-191.336 EndY=4.65187 EndZ=0
    g1: LineSegment StartX=-192.503 StartY=17.8001 StartZ=0 EndX=-190.909 EndY=17.9416 EndZ=0
    g2: LineSegment StartX=-190.909 StartY=17.9416 StartZ=0 EndX=-189.742 EndY=4.79337 EndZ=0
    g3: LineSegment StartX=-189.742 StartY=4.79337 StartZ=0 EndX=-191.336 EndY=4.65187 EndZ=0
  constraints (10):
    c: Parallel(g0,g-3)
    c: Equal(g0,g-3)
    c: Coincident(g1,g0)
    c: Perpendicular(g0,g1)
    c: Coincident(g1,g-3)
    c: Coincident(g2,g1)
    c: Coincident(g2,g-3)
    c: Coincident(g3,g2)
    c: Coincident(g3,g0)
    c: Distance(g1) = 1.6
FEATURE [PartDesign::Body] Body  label="Struttura pistola"
  AllowCompound = false
  Group = -> [Sketch,Sketch002,Sketch004,DatumPlane,Sketch005,DatumPlane001,CopyCut,Sketch008,Sketch009,Sketch010,Sketch011,Sketch012,Sketch013,Sketch014,Sketch015,Sketch016,Sketch017,Sketch018,Sketch019,Sketch020,Sketch022,Sketch023,Sketch024,Sketch025,Sketch026,Sketch027,Sketch029,Sketch030,Sketch031,Sketch032,Sketch033,Sketch034,Sketch035,Sketch036,Sketch037,Sketch038,Sketch039,Sketch040,Sketch041,Sketch042,+31 more]
  Origin = -> Origin
FEATURE [Part::Extrusion] Extrude091  label="Extrude091 - scavo_saldature_nuovo_driver_alto"
  Base = -> Sketch162
  Dir = (0,-1,2e-16)
  DirMode = 2
  FaceMakerClass = Part::FaceMakerBullseye
  FaceMakerMode = 3
  LengthFwd = 4
  LengthRev = 0
  Placement = pos=(0,-3.8,0) rot=(0,0,1;0rad)
  Solid = true
  Symmetric = false
FEATURE [Part::Cut] Cut055
  Base = -> Cut054
  Refine = true
  Tool = -> Extrude091
note: 2 file-system paths scrubbed to <path> (originals preserved in the JSON sidecar)
